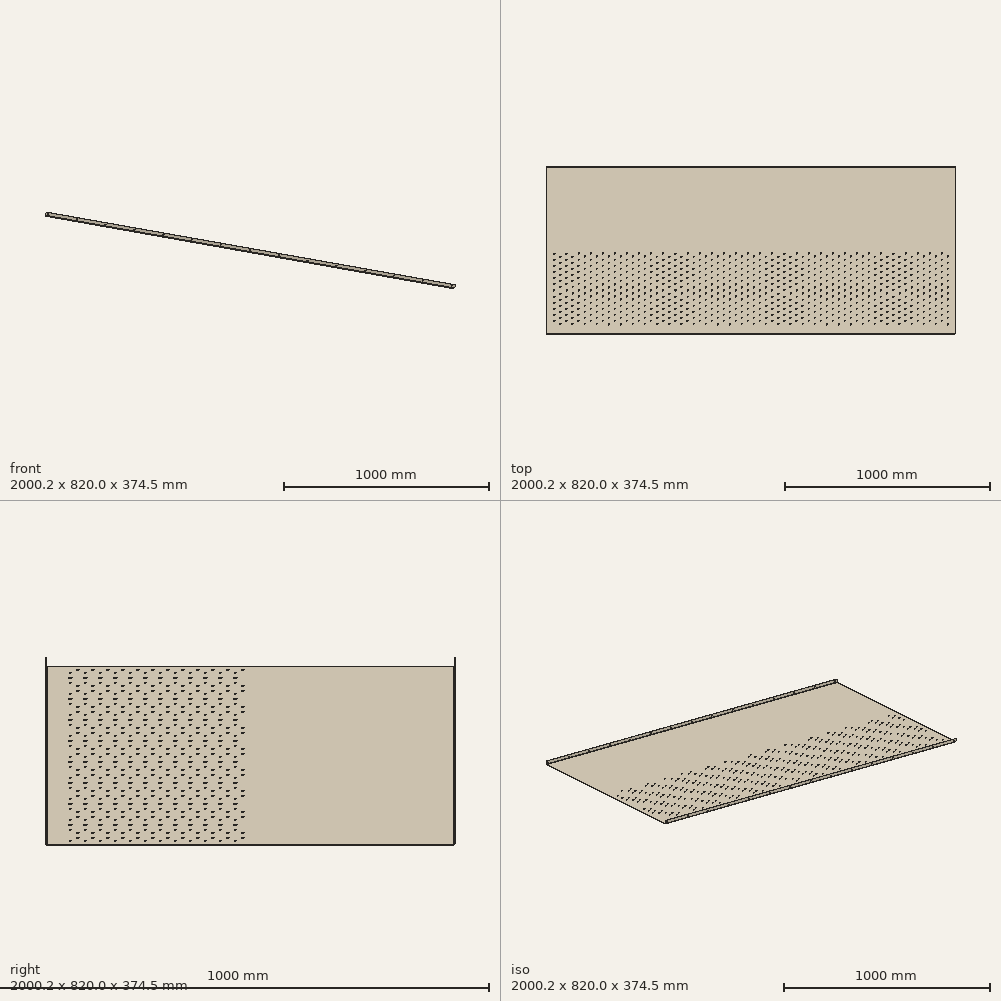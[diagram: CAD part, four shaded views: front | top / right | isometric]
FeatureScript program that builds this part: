
annotation { "Feature Type Name" : "Feature", "Feature Type Description" : "" }
export const myFeature = defineFeature(function(context is Context, id is Id, definition is map)
    precondition{}
    {
        {
            var Q0;
            Q0=qCreatedBy(makeId("Front.planeOp"),FACE);
            var sketch = newSketch(context, id + "F0", { "sketchPlane" : qUnion([Q0])});
            skLineSegment(sketch, "E0", {"start": v(1435.35, 1.97) * mm, "end": v(-561.3, 356.77) * mm});
            skLineSegment(sketch, "E1", {"start": v(-561.3, 356.77) * mm, "end": v(-561.65, 354.8) * mm});
            skLineSegment(sketch, "E2", {"start": v(1435.35, 1.97) * mm, "end": v(1435.35, 243.64) * mm});
            skLineSegment(sketch, "E3", {"start": v(-561.65, 354.8) * mm, "end": v(0, 255) * mm});
            skLineSegment(sketch, "E4", {"start": v(1435, 0) * mm, "end": v(1435.35, 1.97) * mm});
            skLineSegment(sketch, "E5", {"start": v(0, 255) * mm, "end": v(1435, 0) * mm});
            skLineSegment(sketch, "E6", {"start": v(0, 255) * mm, "end": v(0, 0) * mm, "construction": true});
            skLineSegment(sketch, "E7", {"start": v(0, 0) * mm, "end": v(1435, 0) * mm, "construction": true});
            skSolve(sketch);
        }
        {
            var Q0;
            Q0=makeQuery(id+"F0.imprint","IMPRINT",FACE,{"disambiguationData":[TD([[makeQuery(id+"F0.imprint","IMPRINT",EDGE,{"derivedFrom":sQuery(id+"F0.wireOp",EDGE,"E0")}),1.0]])]});
            extrude(context, id + "F1", {"entities" : qUnion([Q0]), "depth" : 820 * mm, "symmetric" : true});
        }
        {
            var Q0;
            Q0=makeQuery(id+"F1.opExtrude","CAP_FACE",FACE,{"disambiguationData":[OSD([sQuery(id+"F0.wireOp",EDGE,"E0"),sQuery(id+"F0.wireOp",EDGE,"E1"),sQuery(id+"F0.wireOp",EDGE,"E3"),sQuery(id+"F0.wireOp",EDGE,"E4")])],"isStart":false});
            var sketch = newSketch(context, id + "F2", { "sketchPlane" : qUnion([Q0])});
            skLineSegment(sketch, "E8", {"start": v(-561.65, 354.8) * mm, "end": v(-558.15, 374.5) * mm});
            skLineSegment(sketch, "E9", {"start": v(-558.15, 374.5) * mm, "end": v(1438.5, 19.7) * mm});
            skLineSegment(sketch, "E10", {"start": v(1438.5, 19.7) * mm, "end": v(1435, 0) * mm});
            skLineSegment(sketch, "E11", {"start": v(1435, 0) * mm, "end": v(-561.65, 354.8) * mm});
            skLineSegment(sketch, "E12", {"start": v(-558.15, 374.5) * mm, "end": v(-564.65, 375.65) * mm, "construction": true});
            skLineSegment(sketch, "E13", {"start": v(-564.65, 375.65) * mm, "end": v(-564.65, 355.34) * mm, "construction": true});
            skLineSegment(sketch, "E14", {"start": v(-564.65, 355.34) * mm, "end": v(-561.65, 354.8) * mm, "construction": true});
            skLineSegment(sketch, "E15", {"start": v(1435.35, 20.25) * mm, "end": v(1435.35, 1.97) * mm, "construction": true});
            skLineSegment(sketch, "E16", {"start": v(-564.65, 365.5) * mm, "end": v(-550.21, 362.93) * mm, "construction": true});
            skLineSegment(sketch, "E17", {"start": v(-550.21, 367) * mm, "end": v(-550.21, 358.87) * mm, "construction": true});
            skLineSegment(sketch, "E18", {"start": v(-550.21, 362.93) * mm, "end": v(1420.91, 12.66) * mm, "construction": true});
            skCircle(sketch, "E19", {"center": v(-550.21, 362.93) * mm, "radius": 3.5 * mm});
            skCircle(sketch, "E20.1.0.0", {"center": v(-409.42, 337.91) * mm, "radius": 3.5 * mm});
            skLineSegment(sketch, "E20.1.0.1", {"start": v(-409.42, 341.97) * mm, "end": v(-409.42, 333.85) * mm, "construction": true});
            skCircle(sketch, "E20.2.0.0", {"center": v(-268.62, 312.9) * mm, "radius": 3.5 * mm});
            skLineSegment(sketch, "E20.2.0.1", {"start": v(-268.62, 316.95) * mm, "end": v(-268.62, 308.83) * mm, "construction": true});
            skCircle(sketch, "E20.3.0.0", {"center": v(-127.83, 287.87) * mm, "radius": 3.5 * mm});
            skLineSegment(sketch, "E20.3.0.1", {"start": v(-127.83, 291.93) * mm, "end": v(-127.83, 283.8) * mm, "construction": true});
            skCircle(sketch, "E20.4.0.0", {"center": v(12.97, 262.85) * mm, "radius": 3.5 * mm});
            skLineSegment(sketch, "E20.4.0.1", {"start": v(12.97, 266.92) * mm, "end": v(12.97, 258.79) * mm, "construction": true});
            skCircle(sketch, "E20.5.0.0", {"center": v(153.76, 237.83) * mm, "radius": 3.5 * mm});
            skLineSegment(sketch, "E20.5.0.1", {"start": v(153.76, 241.9) * mm, "end": v(153.76, 233.77) * mm, "construction": true});
            skCircle(sketch, "E20.6.0.0", {"center": v(294.56, 212.81) * mm, "radius": 3.5 * mm});
            skLineSegment(sketch, "E20.6.0.1", {"start": v(294.56, 216.88) * mm, "end": v(294.56, 208.75) * mm, "construction": true});
            skCircle(sketch, "E20.7.0.0", {"center": v(435.35, 187.8) * mm, "radius": 3.5 * mm});
            skLineSegment(sketch, "E20.7.0.1", {"start": v(435.35, 191.86) * mm, "end": v(435.35, 183.73) * mm, "construction": true});
            skCircle(sketch, "E20.8.0.0", {"center": v(576.14, 162.78) * mm, "radius": 3.5 * mm});
            skLineSegment(sketch, "E20.8.0.1", {"start": v(576.14, 166.84) * mm, "end": v(576.14, 158.71) * mm, "construction": true});
            skCircle(sketch, "E20.9.0.0", {"center": v(716.94, 137.76) * mm, "radius": 3.5 * mm});
            skLineSegment(sketch, "E20.9.0.1", {"start": v(716.94, 141.82) * mm, "end": v(716.94, 133.7) * mm, "construction": true});
            skCircle(sketch, "E20.10.0.0", {"center": v(857.73, 112.74) * mm, "radius": 3.5 * mm});
            skLineSegment(sketch, "E20.10.0.1", {"start": v(857.73, 116.8) * mm, "end": v(857.73, 108.67) * mm, "construction": true});
            skCircle(sketch, "E20.11.0.0", {"center": v(998.53, 87.72) * mm, "radius": 3.5 * mm});
            skLineSegment(sketch, "E20.11.0.1", {"start": v(998.53, 91.78) * mm, "end": v(998.53, 83.66) * mm, "construction": true});
            skCircle(sketch, "E20.12.0.0", {"center": v(1139.32, 62.7) * mm, "radius": 3.5 * mm});
            skLineSegment(sketch, "E20.12.0.1", {"start": v(1139.32, 66.76) * mm, "end": v(1139.32, 58.64) * mm, "construction": true});
            skCircle(sketch, "E20.13.0.0", {"center": v(1280.12, 37.68) * mm, "radius": 3.5 * mm});
            skLineSegment(sketch, "E20.13.0.1", {"start": v(1280.12, 41.74) * mm, "end": v(1280.12, 33.62) * mm, "construction": true});
            skCircle(sketch, "E20.14.0.0", {"center": v(1420.91, 12.66) * mm, "radius": 3.5 * mm});
            skLineSegment(sketch, "E20.14.0.1", {"start": v(1420.91, 16.72) * mm, "end": v(1420.91, 8.6) * mm, "construction": true});
            skLineSegment(sketch, "E20.direction1", {"start": v(-550.21, 362.93) * mm, "end": v(-409.42, 337.91) * mm, "construction": true});
            skLineSegment(sketch, "E21.trimOffspring", {"start": v(1420.91, 12.66) * mm, "end": v(1435.35, 10.1) * mm, "construction": true});
            skPoint(sketch, "E22.orphan", {"position": v(1436.75, 9.85) * mm});
            skSolve(sketch);
        }
        {
            var Q0;
            Q0 = qSketchRegion(id + "F2", true);
            extrude(context, id + "F3", {"entities" : qUnion([Q0]), "operationType" : NewBodyOperationType.ADD, "oppositeDirection" : true, "depth" : 2 * mm});
        }
        {
            var Q0;
            Q0=makeQuery(id+"F1.opExtrude","CAP_FACE",FACE,{"disambiguationData":[OSD([sQuery(id+"F0.wireOp",EDGE,"E0"),sQuery(id+"F0.wireOp",EDGE,"E1"),sQuery(id+"F0.wireOp",EDGE,"E3"),sQuery(id+"F0.wireOp",EDGE,"E4")])],"isStart":true});
            var sketch = newSketch(context, id + "F4", { "sketchPlane" : qUnion([Q0])});
            skLineSegment(sketch, "E23", {"start": v(-1435, 0) * mm, "end": v(-1438.5, 19.7) * mm});
            skLineSegment(sketch, "E24", {"start": v(-1438.5, 19.7) * mm, "end": v(558.15, 374.5) * mm});
            skLineSegment(sketch, "E25", {"start": v(558.15, 374.5) * mm, "end": v(561.65, 354.8) * mm});
            skLineSegment(sketch, "E26", {"start": v(561.65, 354.8) * mm, "end": v(-1435, 0) * mm});
            skLineSegment(sketch, "E27", {"start": v(-1435.35, 1.97) * mm, "end": v(-1435.35, 20.25) * mm, "construction": true});
            skLineSegment(sketch, "E28", {"start": v(561.65, 354.8) * mm, "end": v(564.65, 355.34) * mm, "construction": true});
            skLineSegment(sketch, "E29", {"start": v(564.65, 355.34) * mm, "end": v(564.65, 375.65) * mm, "construction": true});
            skLineSegment(sketch, "E30", {"start": v(564.65, 375.65) * mm, "end": v(558.15, 374.5) * mm, "construction": true});
            skLineSegment(sketch, "E31", {"start": v(-1435.35, 10.1) * mm, "end": v(-1420.91, 12.66) * mm, "construction": true});
            skLineSegment(sketch, "E32", {"start": v(550.21, 367) * mm, "end": v(550.21, 358.87) * mm, "construction": true});
            skLineSegment(sketch, "E33", {"start": v(550.21, 362.93) * mm, "end": v(564.65, 365.5) * mm, "construction": true});
            skCircle(sketch, "E34", {"center": v(550.21, 362.93) * mm, "radius": 3.5 * mm});
            skCircle(sketch, "E35.1.0.0", {"center": v(409.42, 337.91) * mm, "radius": 3.5 * mm});
            skLineSegment(sketch, "E35.1.0.1", {"start": v(409.42, 341.97) * mm, "end": v(409.42, 333.85) * mm, "construction": true});
            skCircle(sketch, "E35.2.0.0", {"center": v(268.62, 312.9) * mm, "radius": 3.5 * mm});
            skLineSegment(sketch, "E35.2.0.1", {"start": v(268.62, 316.95) * mm, "end": v(268.62, 308.83) * mm, "construction": true});
            skCircle(sketch, "E35.3.0.0", {"center": v(127.83, 287.87) * mm, "radius": 3.5 * mm});
            skLineSegment(sketch, "E35.3.0.1", {"start": v(127.83, 291.93) * mm, "end": v(127.83, 283.8) * mm, "construction": true});
            skCircle(sketch, "E35.4.0.0", {"center": v(-12.97, 262.85) * mm, "radius": 3.5 * mm});
            skLineSegment(sketch, "E35.4.0.1", {"start": v(-12.97, 266.92) * mm, "end": v(-12.97, 258.79) * mm, "construction": true});
            skCircle(sketch, "E35.5.0.0", {"center": v(-153.76, 237.83) * mm, "radius": 3.5 * mm});
            skLineSegment(sketch, "E35.5.0.1", {"start": v(-153.76, 241.9) * mm, "end": v(-153.76, 233.77) * mm, "construction": true});
            skCircle(sketch, "E35.6.0.0", {"center": v(-294.56, 212.81) * mm, "radius": 3.5 * mm});
            skLineSegment(sketch, "E35.6.0.1", {"start": v(-294.56, 216.88) * mm, "end": v(-294.56, 208.75) * mm, "construction": true});
            skCircle(sketch, "E35.7.0.0", {"center": v(-435.35, 187.8) * mm, "radius": 3.5 * mm});
            skLineSegment(sketch, "E35.7.0.1", {"start": v(-435.35, 191.86) * mm, "end": v(-435.35, 183.73) * mm, "construction": true});
            skCircle(sketch, "E35.8.0.0", {"center": v(-576.14, 162.78) * mm, "radius": 3.5 * mm});
            skLineSegment(sketch, "E35.8.0.1", {"start": v(-576.14, 166.84) * mm, "end": v(-576.14, 158.71) * mm, "construction": true});
            skCircle(sketch, "E35.9.0.0", {"center": v(-716.94, 137.76) * mm, "radius": 3.5 * mm});
            skLineSegment(sketch, "E35.9.0.1", {"start": v(-716.94, 141.82) * mm, "end": v(-716.94, 133.7) * mm, "construction": true});
            skCircle(sketch, "E35.10.0.0", {"center": v(-857.73, 112.74) * mm, "radius": 3.5 * mm});
            skLineSegment(sketch, "E35.10.0.1", {"start": v(-857.73, 116.8) * mm, "end": v(-857.73, 108.67) * mm, "construction": true});
            skCircle(sketch, "E35.11.0.0", {"center": v(-998.53, 87.72) * mm, "radius": 3.5 * mm});
            skLineSegment(sketch, "E35.11.0.1", {"start": v(-998.53, 91.78) * mm, "end": v(-998.53, 83.66) * mm, "construction": true});
            skCircle(sketch, "E35.12.0.0", {"center": v(-1139.32, 62.7) * mm, "radius": 3.5 * mm});
            skLineSegment(sketch, "E35.12.0.1", {"start": v(-1139.32, 66.76) * mm, "end": v(-1139.32, 58.64) * mm, "construction": true});
            skCircle(sketch, "E35.13.0.0", {"center": v(-1280.12, 37.68) * mm, "radius": 3.5 * mm});
            skLineSegment(sketch, "E35.13.0.1", {"start": v(-1280.12, 41.74) * mm, "end": v(-1280.12, 33.62) * mm, "construction": true});
            skCircle(sketch, "E35.14.0.0", {"center": v(-1420.91, 12.66) * mm, "radius": 3.5 * mm});
            skLineSegment(sketch, "E35.14.0.1", {"start": v(-1420.91, 16.72) * mm, "end": v(-1420.91, 8.6) * mm, "construction": true});
            skLineSegment(sketch, "E35.direction1", {"start": v(550.21, 362.93) * mm, "end": v(409.42, 337.91) * mm, "construction": true});
            skPoint(sketch, "E36.orphan", {"position": v(-1436.75, 9.85) * mm});
            skLineSegment(sketch, "E37.trimOffspring", {"start": v(-1420.91, 12.66) * mm, "end": v(550.21, 362.93) * mm, "construction": true});
            skSolve(sketch);
        }
        {
            var Q0;
            Q0 = qSketchRegion(id + "F4", true);
            extrude(context, id + "F5", {"entities" : qUnion([Q0]), "operationType" : NewBodyOperationType.ADD, "oppositeDirection" : true, "depth" : 2 * mm});
        }
        {
            var Q0;
            Q0=makeQuery(id+"F1.opExtrude","SWEPT_FACE",FACE,{"disambiguationData":[OSD([sQuery(id+"F0.wireOp",EDGE,"E0")])]});
            var sketch = newSketch(context, id + "F6", { "sketchPlane" : qUnion([Q0])});
            skCircle(sketch, "E38", {"center": v(1373.9, -360) * mm, "radius": 3.5 * mm});
            skCircle(sketch, "E39", {"center": v(1343.9, -345) * mm, "radius": 3.5 * mm});
            skLineSegment(sketch, "E40", {"start": v(1412.87, 0) * mm, "end": v(-615.06, 0) * mm, "construction": true});
            skCircle(sketch, "E41.0.1.0", {"center": v(1373.9, -330) * mm, "radius": 3.5 * mm});
            skCircle(sketch, "E41.0.2.0", {"center": v(1373.9, -300) * mm, "radius": 3.5 * mm});
            skCircle(sketch, "E41.0.3.0", {"center": v(1373.9, -270) * mm, "radius": 3.5 * mm});
            skCircle(sketch, "E41.0.4.0", {"center": v(1373.9, -240) * mm, "radius": 3.5 * mm});
            skCircle(sketch, "E41.0.5.0", {"center": v(1373.9, -210) * mm, "radius": 3.5 * mm});
            skCircle(sketch, "E41.0.6.0", {"center": v(1373.9, -180) * mm, "radius": 3.5 * mm});
            skCircle(sketch, "E41.0.7.0", {"center": v(1373.9, -150) * mm, "radius": 3.5 * mm});
            skCircle(sketch, "E41.0.8.0", {"center": v(1373.9, -120) * mm, "radius": 3.5 * mm});
            skCircle(sketch, "E41.0.9.0", {"center": v(1373.9, -90) * mm, "radius": 3.5 * mm});
            skCircle(sketch, "E41.0.10.0", {"center": v(1373.9, -60) * mm, "radius": 3.5 * mm});
            skCircle(sketch, "E41.0.11.0", {"center": v(1373.9, -30) * mm, "radius": 3.5 * mm});
            skCircle(sketch, "E41.0.12.0", {"center": v(1373.9, 0) * mm, "radius": 3.5 * mm});
            skLineSegment(sketch, "E41.direction1", {"start": v(1373.9, -360) * mm, "end": v(1373.9, -360) * mm});
            skLineSegment(sketch, "E41.direction2", {"start": v(1373.9, -360) * mm, "end": v(1373.9, -330) * mm, "construction": true});
            skCircle(sketch, "E42.0.1.0", {"center": v(1343.9, -315) * mm, "radius": 3.5 * mm});
            skCircle(sketch, "E42.0.2.0", {"center": v(1343.9, -285) * mm, "radius": 3.5 * mm});
            skCircle(sketch, "E42.0.3.0", {"center": v(1343.9, -255) * mm, "radius": 3.5 * mm});
            skCircle(sketch, "E42.0.4.0", {"center": v(1343.9, -225) * mm, "radius": 3.5 * mm});
            skCircle(sketch, "E42.0.5.0", {"center": v(1343.9, -195) * mm, "radius": 3.5 * mm});
            skCircle(sketch, "E42.0.6.0", {"center": v(1343.9, -165) * mm, "radius": 3.5 * mm});
            skCircle(sketch, "E42.0.7.0", {"center": v(1343.9, -135) * mm, "radius": 3.5 * mm});
            skCircle(sketch, "E42.0.8.0", {"center": v(1343.9, -105) * mm, "radius": 3.5 * mm});
            skCircle(sketch, "E42.0.9.0", {"center": v(1343.9, -75) * mm, "radius": 3.5 * mm});
            skCircle(sketch, "E42.0.10.0", {"center": v(1343.9, -45) * mm, "radius": 3.5 * mm});
            skCircle(sketch, "E42.0.11.0", {"center": v(1343.9, -15) * mm, "radius": 3.5 * mm});
            skLineSegment(sketch, "E42.direction1", {"start": v(1343.9, -345) * mm, "end": v(1343.9, -345) * mm});
            skLineSegment(sketch, "E42.direction2", {"start": v(1343.9, -345) * mm, "end": v(1343.9, -315) * mm, "construction": true});
            skLineSegment(sketch, "E43.1.0.0", {"start": v(1313.9, -360) * mm, "end": v(1313.9, -330) * mm, "construction": true});
            skCircle(sketch, "E43.1.0.1", {"center": v(1313.9, -60) * mm, "radius": 3.5 * mm});
            skCircle(sketch, "E43.1.0.2", {"center": v(1313.9, -30) * mm, "radius": 3.5 * mm});
            skCircle(sketch, "E43.1.0.3", {"center": v(1313.9, 0) * mm, "radius": 3.5 * mm});
            skCircle(sketch, "E43.1.0.4", {"center": v(1313.9, -240) * mm, "radius": 3.5 * mm});
            skCircle(sketch, "E43.1.0.5", {"center": v(1313.9, -300) * mm, "radius": 3.5 * mm});
            skCircle(sketch, "E43.1.0.6", {"center": v(1283.9, -75) * mm, "radius": 3.5 * mm});
            skCircle(sketch, "E43.1.0.7", {"center": v(1283.9, -285) * mm, "radius": 3.5 * mm});
            skCircle(sketch, "E43.1.0.8", {"center": v(1283.9, -105) * mm, "radius": 3.5 * mm});
            skCircle(sketch, "E43.1.0.9", {"center": v(1283.9, -255) * mm, "radius": 3.5 * mm});
            skCircle(sketch, "E43.1.0.10", {"center": v(1283.9, -195) * mm, "radius": 3.5 * mm});
            skLineSegment(sketch, "E43.1.0.11", {"start": v(1283.9, -345) * mm, "end": v(1283.9, -315) * mm, "construction": true});
            skCircle(sketch, "E43.1.0.12", {"center": v(1283.9, -15) * mm, "radius": 3.5 * mm});
            skCircle(sketch, "E43.1.0.13", {"center": v(1313.9, -120) * mm, "radius": 3.5 * mm});
            skCircle(sketch, "E43.1.0.14", {"center": v(1283.9, -45) * mm, "radius": 3.5 * mm});
            skCircle(sketch, "E43.1.0.15", {"center": v(1313.9, -180) * mm, "radius": 3.5 * mm});
            skCircle(sketch, "E43.1.0.16", {"center": v(1313.9, -150) * mm, "radius": 3.5 * mm});
            skCircle(sketch, "E43.1.0.17", {"center": v(1313.9, -90) * mm, "radius": 3.5 * mm});
            skCircle(sketch, "E43.1.0.18", {"center": v(1283.9, -135) * mm, "radius": 3.5 * mm});
            skCircle(sketch, "E43.1.0.19", {"center": v(1283.9, -225) * mm, "radius": 3.5 * mm});
            skCircle(sketch, "E43.1.0.20", {"center": v(1313.9, -210) * mm, "radius": 3.5 * mm});
            skCircle(sketch, "E43.1.0.21", {"center": v(1283.9, -165) * mm, "radius": 3.5 * mm});
            skCircle(sketch, "E43.1.0.22", {"center": v(1313.9, -270) * mm, "radius": 3.5 * mm});
            skCircle(sketch, "E43.1.0.23", {"center": v(1313.9, -330) * mm, "radius": 3.5 * mm});
            skCircle(sketch, "E43.1.0.24", {"center": v(1283.9, -315) * mm, "radius": 3.5 * mm});
            skCircle(sketch, "E43.1.0.25", {"center": v(1283.9, -345) * mm, "radius": 3.5 * mm});
            skCircle(sketch, "E43.1.0.26", {"center": v(1313.9, -360) * mm, "radius": 3.5 * mm});
            skLineSegment(sketch, "E43.2.0.0", {"start": v(1253.9, -360) * mm, "end": v(1253.9, -330) * mm, "construction": true});
            skCircle(sketch, "E43.2.0.1", {"center": v(1253.9, -60) * mm, "radius": 3.5 * mm});
            skCircle(sketch, "E43.2.0.2", {"center": v(1253.9, -30) * mm, "radius": 3.5 * mm});
            skCircle(sketch, "E43.2.0.3", {"center": v(1253.9, 0) * mm, "radius": 3.5 * mm});
            skCircle(sketch, "E43.2.0.4", {"center": v(1253.9, -240) * mm, "radius": 3.5 * mm});
            skCircle(sketch, "E43.2.0.5", {"center": v(1253.9, -300) * mm, "radius": 3.5 * mm});
            skCircle(sketch, "E43.2.0.6", {"center": v(1223.9, -75) * mm, "radius": 3.5 * mm});
            skCircle(sketch, "E43.2.0.7", {"center": v(1223.9, -285) * mm, "radius": 3.5 * mm});
            skCircle(sketch, "E43.2.0.8", {"center": v(1223.9, -105) * mm, "radius": 3.5 * mm});
            skCircle(sketch, "E43.2.0.9", {"center": v(1223.9, -255) * mm, "radius": 3.5 * mm});
            skCircle(sketch, "E43.2.0.10", {"center": v(1223.9, -195) * mm, "radius": 3.5 * mm});
            skLineSegment(sketch, "E43.2.0.11", {"start": v(1223.9, -345) * mm, "end": v(1223.9, -315) * mm, "construction": true});
            skCircle(sketch, "E43.2.0.12", {"center": v(1223.9, -15) * mm, "radius": 3.5 * mm});
            skCircle(sketch, "E43.2.0.13", {"center": v(1253.9, -120) * mm, "radius": 3.5 * mm});
            skCircle(sketch, "E43.2.0.14", {"center": v(1223.9, -45) * mm, "radius": 3.5 * mm});
            skCircle(sketch, "E43.2.0.15", {"center": v(1253.9, -180) * mm, "radius": 3.5 * mm});
            skCircle(sketch, "E43.2.0.16", {"center": v(1253.9, -150) * mm, "radius": 3.5 * mm});
            skCircle(sketch, "E43.2.0.17", {"center": v(1253.9, -90) * mm, "radius": 3.5 * mm});
            skCircle(sketch, "E43.2.0.18", {"center": v(1223.9, -135) * mm, "radius": 3.5 * mm});
            skCircle(sketch, "E43.2.0.19", {"center": v(1223.9, -225) * mm, "radius": 3.5 * mm});
            skCircle(sketch, "E43.2.0.20", {"center": v(1253.9, -210) * mm, "radius": 3.5 * mm});
            skCircle(sketch, "E43.2.0.21", {"center": v(1223.9, -165) * mm, "radius": 3.5 * mm});
            skCircle(sketch, "E43.2.0.22", {"center": v(1253.9, -270) * mm, "radius": 3.5 * mm});
            skCircle(sketch, "E43.2.0.23", {"center": v(1253.9, -330) * mm, "radius": 3.5 * mm});
            skCircle(sketch, "E43.2.0.24", {"center": v(1223.9, -315) * mm, "radius": 3.5 * mm});
            skCircle(sketch, "E43.2.0.25", {"center": v(1223.9, -345) * mm, "radius": 3.5 * mm});
            skCircle(sketch, "E43.2.0.26", {"center": v(1253.9, -360) * mm, "radius": 3.5 * mm});
            skLineSegment(sketch, "E43.3.0.0", {"start": v(1193.9, -360) * mm, "end": v(1193.9, -330) * mm, "construction": true});
            skCircle(sketch, "E43.3.0.1", {"center": v(1193.9, -60) * mm, "radius": 3.5 * mm});
            skCircle(sketch, "E43.3.0.2", {"center": v(1193.9, -30) * mm, "radius": 3.5 * mm});
            skCircle(sketch, "E43.3.0.3", {"center": v(1193.9, 0) * mm, "radius": 3.5 * mm});
            skCircle(sketch, "E43.3.0.4", {"center": v(1193.9, -240) * mm, "radius": 3.5 * mm});
            skCircle(sketch, "E43.3.0.5", {"center": v(1193.9, -300) * mm, "radius": 3.5 * mm});
            skCircle(sketch, "E43.3.0.6", {"center": v(1163.9, -75) * mm, "radius": 3.5 * mm});
            skCircle(sketch, "E43.3.0.7", {"center": v(1163.9, -285) * mm, "radius": 3.5 * mm});
            skCircle(sketch, "E43.3.0.8", {"center": v(1163.9, -105) * mm, "radius": 3.5 * mm});
            skCircle(sketch, "E43.3.0.9", {"center": v(1163.9, -255) * mm, "radius": 3.5 * mm});
            skCircle(sketch, "E43.3.0.10", {"center": v(1163.9, -195) * mm, "radius": 3.5 * mm});
            skLineSegment(sketch, "E43.3.0.11", {"start": v(1163.9, -345) * mm, "end": v(1163.9, -315) * mm, "construction": true});
            skCircle(sketch, "E43.3.0.12", {"center": v(1163.9, -15) * mm, "radius": 3.5 * mm});
            skCircle(sketch, "E43.3.0.13", {"center": v(1193.9, -120) * mm, "radius": 3.5 * mm});
            skCircle(sketch, "E43.3.0.14", {"center": v(1163.9, -45) * mm, "radius": 3.5 * mm});
            skCircle(sketch, "E43.3.0.15", {"center": v(1193.9, -180) * mm, "radius": 3.5 * mm});
            skCircle(sketch, "E43.3.0.16", {"center": v(1193.9, -150) * mm, "radius": 3.5 * mm});
            skCircle(sketch, "E43.3.0.17", {"center": v(1193.9, -90) * mm, "radius": 3.5 * mm});
            skCircle(sketch, "E43.3.0.18", {"center": v(1163.9, -135) * mm, "radius": 3.5 * mm});
            skCircle(sketch, "E43.3.0.19", {"center": v(1163.9, -225) * mm, "radius": 3.5 * mm});
            skCircle(sketch, "E43.3.0.20", {"center": v(1193.9, -210) * mm, "radius": 3.5 * mm});
            skCircle(sketch, "E43.3.0.21", {"center": v(1163.9, -165) * mm, "radius": 3.5 * mm});
            skCircle(sketch, "E43.3.0.22", {"center": v(1193.9, -270) * mm, "radius": 3.5 * mm});
            skCircle(sketch, "E43.3.0.23", {"center": v(1193.9, -330) * mm, "radius": 3.5 * mm});
            skCircle(sketch, "E43.3.0.24", {"center": v(1163.9, -315) * mm, "radius": 3.5 * mm});
            skCircle(sketch, "E43.3.0.25", {"center": v(1163.9, -345) * mm, "radius": 3.5 * mm});
            skCircle(sketch, "E43.3.0.26", {"center": v(1193.9, -360) * mm, "radius": 3.5 * mm});
            skLineSegment(sketch, "E43.4.0.0", {"start": v(1133.9, -360) * mm, "end": v(1133.9, -330) * mm, "construction": true});
            skCircle(sketch, "E43.4.0.1", {"center": v(1133.9, -60) * mm, "radius": 3.5 * mm});
            skCircle(sketch, "E43.4.0.2", {"center": v(1133.9, -30) * mm, "radius": 3.5 * mm});
            skCircle(sketch, "E43.4.0.3", {"center": v(1133.9, 0) * mm, "radius": 3.5 * mm});
            skCircle(sketch, "E43.4.0.4", {"center": v(1133.9, -240) * mm, "radius": 3.5 * mm});
            skCircle(sketch, "E43.4.0.5", {"center": v(1133.9, -300) * mm, "radius": 3.5 * mm});
            skCircle(sketch, "E43.4.0.6", {"center": v(1103.9, -75) * mm, "radius": 3.5 * mm});
            skCircle(sketch, "E43.4.0.7", {"center": v(1103.9, -285) * mm, "radius": 3.5 * mm});
            skCircle(sketch, "E43.4.0.8", {"center": v(1103.9, -105) * mm, "radius": 3.5 * mm});
            skCircle(sketch, "E43.4.0.9", {"center": v(1103.9, -255) * mm, "radius": 3.5 * mm});
            skCircle(sketch, "E43.4.0.10", {"center": v(1103.9, -195) * mm, "radius": 3.5 * mm});
            skLineSegment(sketch, "E43.4.0.11", {"start": v(1103.9, -345) * mm, "end": v(1103.9, -315) * mm, "construction": true});
            skCircle(sketch, "E43.4.0.12", {"center": v(1103.9, -15) * mm, "radius": 3.5 * mm});
            skCircle(sketch, "E43.4.0.13", {"center": v(1133.9, -120) * mm, "radius": 3.5 * mm});
            skCircle(sketch, "E43.4.0.14", {"center": v(1103.9, -45) * mm, "radius": 3.5 * mm});
            skCircle(sketch, "E43.4.0.15", {"center": v(1133.9, -180) * mm, "radius": 3.5 * mm});
            skCircle(sketch, "E43.4.0.16", {"center": v(1133.9, -150) * mm, "radius": 3.5 * mm});
            skCircle(sketch, "E43.4.0.17", {"center": v(1133.9, -90) * mm, "radius": 3.5 * mm});
            skCircle(sketch, "E43.4.0.18", {"center": v(1103.9, -135) * mm, "radius": 3.5 * mm});
            skCircle(sketch, "E43.4.0.19", {"center": v(1103.9, -225) * mm, "radius": 3.5 * mm});
            skCircle(sketch, "E43.4.0.20", {"center": v(1133.9, -210) * mm, "radius": 3.5 * mm});
            skCircle(sketch, "E43.4.0.21", {"center": v(1103.9, -165) * mm, "radius": 3.5 * mm});
            skCircle(sketch, "E43.4.0.22", {"center": v(1133.9, -270) * mm, "radius": 3.5 * mm});
            skCircle(sketch, "E43.4.0.23", {"center": v(1133.9, -330) * mm, "radius": 3.5 * mm});
            skCircle(sketch, "E43.4.0.24", {"center": v(1103.9, -315) * mm, "radius": 3.5 * mm});
            skCircle(sketch, "E43.4.0.25", {"center": v(1103.9, -345) * mm, "radius": 3.5 * mm});
            skCircle(sketch, "E43.4.0.26", {"center": v(1133.9, -360) * mm, "radius": 3.5 * mm});
            skLineSegment(sketch, "E43.5.0.0", {"start": v(1073.9, -360) * mm, "end": v(1073.9, -330) * mm, "construction": true});
            skCircle(sketch, "E43.5.0.1", {"center": v(1073.9, -60) * mm, "radius": 3.5 * mm});
            skCircle(sketch, "E43.5.0.2", {"center": v(1073.9, -30) * mm, "radius": 3.5 * mm});
            skCircle(sketch, "E43.5.0.3", {"center": v(1073.9, 0) * mm, "radius": 3.5 * mm});
            skCircle(sketch, "E43.5.0.4", {"center": v(1073.9, -240) * mm, "radius": 3.5 * mm});
            skCircle(sketch, "E43.5.0.5", {"center": v(1073.9, -300) * mm, "radius": 3.5 * mm});
            skCircle(sketch, "E43.5.0.6", {"center": v(1043.9, -75) * mm, "radius": 3.5 * mm});
            skCircle(sketch, "E43.5.0.7", {"center": v(1043.9, -285) * mm, "radius": 3.5 * mm});
            skCircle(sketch, "E43.5.0.8", {"center": v(1043.9, -105) * mm, "radius": 3.5 * mm});
            skCircle(sketch, "E43.5.0.9", {"center": v(1043.9, -255) * mm, "radius": 3.5 * mm});
            skCircle(sketch, "E43.5.0.10", {"center": v(1043.9, -195) * mm, "radius": 3.5 * mm});
            skLineSegment(sketch, "E43.5.0.11", {"start": v(1043.9, -345) * mm, "end": v(1043.9, -315) * mm, "construction": true});
            skCircle(sketch, "E43.5.0.12", {"center": v(1043.9, -15) * mm, "radius": 3.5 * mm});
            skCircle(sketch, "E43.5.0.13", {"center": v(1073.9, -120) * mm, "radius": 3.5 * mm});
            skCircle(sketch, "E43.5.0.14", {"center": v(1043.9, -45) * mm, "radius": 3.5 * mm});
            skCircle(sketch, "E43.5.0.15", {"center": v(1073.9, -180) * mm, "radius": 3.5 * mm});
            skCircle(sketch, "E43.5.0.16", {"center": v(1073.9, -150) * mm, "radius": 3.5 * mm});
            skCircle(sketch, "E43.5.0.17", {"center": v(1073.9, -90) * mm, "radius": 3.5 * mm});
            skCircle(sketch, "E43.5.0.18", {"center": v(1043.9, -135) * mm, "radius": 3.5 * mm});
            skCircle(sketch, "E43.5.0.19", {"center": v(1043.9, -225) * mm, "radius": 3.5 * mm});
            skCircle(sketch, "E43.5.0.20", {"center": v(1073.9, -210) * mm, "radius": 3.5 * mm});
            skCircle(sketch, "E43.5.0.21", {"center": v(1043.9, -165) * mm, "radius": 3.5 * mm});
            skCircle(sketch, "E43.5.0.22", {"center": v(1073.9, -270) * mm, "radius": 3.5 * mm});
            skCircle(sketch, "E43.5.0.23", {"center": v(1073.9, -330) * mm, "radius": 3.5 * mm});
            skCircle(sketch, "E43.5.0.24", {"center": v(1043.9, -315) * mm, "radius": 3.5 * mm});
            skCircle(sketch, "E43.5.0.25", {"center": v(1043.9, -345) * mm, "radius": 3.5 * mm});
            skCircle(sketch, "E43.5.0.26", {"center": v(1073.9, -360) * mm, "radius": 3.5 * mm});
            skLineSegment(sketch, "E43.6.0.0", {"start": v(1013.9, -360) * mm, "end": v(1013.9, -330) * mm, "construction": true});
            skCircle(sketch, "E43.6.0.1", {"center": v(1013.9, -60) * mm, "radius": 3.5 * mm});
            skCircle(sketch, "E43.6.0.2", {"center": v(1013.9, -30) * mm, "radius": 3.5 * mm});
            skCircle(sketch, "E43.6.0.3", {"center": v(1013.9, 0) * mm, "radius": 3.5 * mm});
            skCircle(sketch, "E43.6.0.4", {"center": v(1013.9, -240) * mm, "radius": 3.5 * mm});
            skCircle(sketch, "E43.6.0.5", {"center": v(1013.9, -300) * mm, "radius": 3.5 * mm});
            skCircle(sketch, "E43.6.0.6", {"center": v(983.9, -75) * mm, "radius": 3.5 * mm});
            skCircle(sketch, "E43.6.0.7", {"center": v(983.9, -285) * mm, "radius": 3.5 * mm});
            skCircle(sketch, "E43.6.0.8", {"center": v(983.9, -105) * mm, "radius": 3.5 * mm});
            skCircle(sketch, "E43.6.0.9", {"center": v(983.9, -255) * mm, "radius": 3.5 * mm});
            skCircle(sketch, "E43.6.0.10", {"center": v(983.9, -195) * mm, "radius": 3.5 * mm});
            skLineSegment(sketch, "E43.6.0.11", {"start": v(983.9, -345) * mm, "end": v(983.9, -315) * mm, "construction": true});
            skCircle(sketch, "E43.6.0.12", {"center": v(983.9, -15) * mm, "radius": 3.5 * mm});
            skCircle(sketch, "E43.6.0.13", {"center": v(1013.9, -120) * mm, "radius": 3.5 * mm});
            skCircle(sketch, "E43.6.0.14", {"center": v(983.9, -45) * mm, "radius": 3.5 * mm});
            skCircle(sketch, "E43.6.0.15", {"center": v(1013.9, -180) * mm, "radius": 3.5 * mm});
            skCircle(sketch, "E43.6.0.16", {"center": v(1013.9, -150) * mm, "radius": 3.5 * mm});
            skCircle(sketch, "E43.6.0.17", {"center": v(1013.9, -90) * mm, "radius": 3.5 * mm});
            skCircle(sketch, "E43.6.0.18", {"center": v(983.9, -135) * mm, "radius": 3.5 * mm});
            skCircle(sketch, "E43.6.0.19", {"center": v(983.9, -225) * mm, "radius": 3.5 * mm});
            skCircle(sketch, "E43.6.0.20", {"center": v(1013.9, -210) * mm, "radius": 3.5 * mm});
            skCircle(sketch, "E43.6.0.21", {"center": v(983.9, -165) * mm, "radius": 3.5 * mm});
            skCircle(sketch, "E43.6.0.22", {"center": v(1013.9, -270) * mm, "radius": 3.5 * mm});
            skCircle(sketch, "E43.6.0.23", {"center": v(1013.9, -330) * mm, "radius": 3.5 * mm});
            skCircle(sketch, "E43.6.0.24", {"center": v(983.9, -315) * mm, "radius": 3.5 * mm});
            skCircle(sketch, "E43.6.0.25", {"center": v(983.9, -345) * mm, "radius": 3.5 * mm});
            skCircle(sketch, "E43.6.0.26", {"center": v(1013.9, -360) * mm, "radius": 3.5 * mm});
            skLineSegment(sketch, "E43.7.0.0", {"start": v(953.9, -360) * mm, "end": v(953.9, -330) * mm, "construction": true});
            skCircle(sketch, "E43.7.0.1", {"center": v(953.9, -60) * mm, "radius": 3.5 * mm});
            skCircle(sketch, "E43.7.0.2", {"center": v(953.9, -30) * mm, "radius": 3.5 * mm});
            skCircle(sketch, "E43.7.0.3", {"center": v(953.9, 0) * mm, "radius": 3.5 * mm});
            skCircle(sketch, "E43.7.0.4", {"center": v(953.9, -240) * mm, "radius": 3.5 * mm});
            skCircle(sketch, "E43.7.0.5", {"center": v(953.9, -300) * mm, "radius": 3.5 * mm});
            skCircle(sketch, "E43.7.0.6", {"center": v(923.9, -75) * mm, "radius": 3.5 * mm});
            skCircle(sketch, "E43.7.0.7", {"center": v(923.9, -285) * mm, "radius": 3.5 * mm});
            skCircle(sketch, "E43.7.0.8", {"center": v(923.9, -105) * mm, "radius": 3.5 * mm});
            skCircle(sketch, "E43.7.0.9", {"center": v(923.9, -255) * mm, "radius": 3.5 * mm});
            skCircle(sketch, "E43.7.0.10", {"center": v(923.9, -195) * mm, "radius": 3.5 * mm});
            skLineSegment(sketch, "E43.7.0.11", {"start": v(923.9, -345) * mm, "end": v(923.9, -315) * mm, "construction": true});
            skCircle(sketch, "E43.7.0.12", {"center": v(923.9, -15) * mm, "radius": 3.5 * mm});
            skCircle(sketch, "E43.7.0.13", {"center": v(953.9, -120) * mm, "radius": 3.5 * mm});
            skCircle(sketch, "E43.7.0.14", {"center": v(923.9, -45) * mm, "radius": 3.5 * mm});
            skCircle(sketch, "E43.7.0.15", {"center": v(953.9, -180) * mm, "radius": 3.5 * mm});
            skCircle(sketch, "E43.7.0.16", {"center": v(953.9, -150) * mm, "radius": 3.5 * mm});
            skCircle(sketch, "E43.7.0.17", {"center": v(953.9, -90) * mm, "radius": 3.5 * mm});
            skCircle(sketch, "E43.7.0.18", {"center": v(923.9, -135) * mm, "radius": 3.5 * mm});
            skCircle(sketch, "E43.7.0.19", {"center": v(923.9, -225) * mm, "radius": 3.5 * mm});
            skCircle(sketch, "E43.7.0.20", {"center": v(953.9, -210) * mm, "radius": 3.5 * mm});
            skCircle(sketch, "E43.7.0.21", {"center": v(923.9, -165) * mm, "radius": 3.5 * mm});
            skCircle(sketch, "E43.7.0.22", {"center": v(953.9, -270) * mm, "radius": 3.5 * mm});
            skCircle(sketch, "E43.7.0.23", {"center": v(953.9, -330) * mm, "radius": 3.5 * mm});
            skCircle(sketch, "E43.7.0.24", {"center": v(923.9, -315) * mm, "radius": 3.5 * mm});
            skCircle(sketch, "E43.7.0.25", {"center": v(923.9, -345) * mm, "radius": 3.5 * mm});
            skCircle(sketch, "E43.7.0.26", {"center": v(953.9, -360) * mm, "radius": 3.5 * mm});
            skLineSegment(sketch, "E43.8.0.0", {"start": v(893.9, -360) * mm, "end": v(893.9, -330) * mm, "construction": true});
            skCircle(sketch, "E43.8.0.1", {"center": v(893.9, -60) * mm, "radius": 3.5 * mm});
            skCircle(sketch, "E43.8.0.2", {"center": v(893.9, -30) * mm, "radius": 3.5 * mm});
            skCircle(sketch, "E43.8.0.3", {"center": v(893.9, 0) * mm, "radius": 3.5 * mm});
            skCircle(sketch, "E43.8.0.4", {"center": v(893.9, -240) * mm, "radius": 3.5 * mm});
            skCircle(sketch, "E43.8.0.5", {"center": v(893.9, -300) * mm, "radius": 3.5 * mm});
            skCircle(sketch, "E43.8.0.6", {"center": v(863.9, -75) * mm, "radius": 3.5 * mm});
            skCircle(sketch, "E43.8.0.7", {"center": v(863.9, -285) * mm, "radius": 3.5 * mm});
            skCircle(sketch, "E43.8.0.8", {"center": v(863.9, -105) * mm, "radius": 3.5 * mm});
            skCircle(sketch, "E43.8.0.9", {"center": v(863.9, -255) * mm, "radius": 3.5 * mm});
            skCircle(sketch, "E43.8.0.10", {"center": v(863.9, -195) * mm, "radius": 3.5 * mm});
            skLineSegment(sketch, "E43.8.0.11", {"start": v(863.9, -345) * mm, "end": v(863.9, -315) * mm, "construction": true});
            skCircle(sketch, "E43.8.0.12", {"center": v(863.9, -15) * mm, "radius": 3.5 * mm});
            skCircle(sketch, "E43.8.0.13", {"center": v(893.9, -120) * mm, "radius": 3.5 * mm});
            skCircle(sketch, "E43.8.0.14", {"center": v(863.9, -45) * mm, "radius": 3.5 * mm});
            skCircle(sketch, "E43.8.0.15", {"center": v(893.9, -180) * mm, "radius": 3.5 * mm});
            skCircle(sketch, "E43.8.0.16", {"center": v(893.9, -150) * mm, "radius": 3.5 * mm});
            skCircle(sketch, "E43.8.0.17", {"center": v(893.9, -90) * mm, "radius": 3.5 * mm});
            skCircle(sketch, "E43.8.0.18", {"center": v(863.9, -135) * mm, "radius": 3.5 * mm});
            skCircle(sketch, "E43.8.0.19", {"center": v(863.9, -225) * mm, "radius": 3.5 * mm});
            skCircle(sketch, "E43.8.0.20", {"center": v(893.9, -210) * mm, "radius": 3.5 * mm});
            skCircle(sketch, "E43.8.0.21", {"center": v(863.9, -165) * mm, "radius": 3.5 * mm});
            skCircle(sketch, "E43.8.0.22", {"center": v(893.9, -270) * mm, "radius": 3.5 * mm});
            skCircle(sketch, "E43.8.0.23", {"center": v(893.9, -330) * mm, "radius": 3.5 * mm});
            skCircle(sketch, "E43.8.0.24", {"center": v(863.9, -315) * mm, "radius": 3.5 * mm});
            skCircle(sketch, "E43.8.0.25", {"center": v(863.9, -345) * mm, "radius": 3.5 * mm});
            skCircle(sketch, "E43.8.0.26", {"center": v(893.9, -360) * mm, "radius": 3.5 * mm});
            skLineSegment(sketch, "E43.9.0.0", {"start": v(833.9, -360) * mm, "end": v(833.9, -330) * mm, "construction": true});
            skCircle(sketch, "E43.9.0.1", {"center": v(833.9, -60) * mm, "radius": 3.5 * mm});
            skCircle(sketch, "E43.9.0.2", {"center": v(833.9, -30) * mm, "radius": 3.5 * mm});
            skCircle(sketch, "E43.9.0.3", {"center": v(833.9, 0) * mm, "radius": 3.5 * mm});
            skCircle(sketch, "E43.9.0.4", {"center": v(833.9, -240) * mm, "radius": 3.5 * mm});
            skCircle(sketch, "E43.9.0.5", {"center": v(833.9, -300) * mm, "radius": 3.5 * mm});
            skCircle(sketch, "E43.9.0.6", {"center": v(803.9, -75) * mm, "radius": 3.5 * mm});
            skCircle(sketch, "E43.9.0.7", {"center": v(803.9, -285) * mm, "radius": 3.5 * mm});
            skCircle(sketch, "E43.9.0.8", {"center": v(803.9, -105) * mm, "radius": 3.5 * mm});
            skCircle(sketch, "E43.9.0.9", {"center": v(803.9, -255) * mm, "radius": 3.5 * mm});
            skCircle(sketch, "E43.9.0.10", {"center": v(803.9, -195) * mm, "radius": 3.5 * mm});
            skLineSegment(sketch, "E43.9.0.11", {"start": v(803.9, -345) * mm, "end": v(803.9, -315) * mm, "construction": true});
            skCircle(sketch, "E43.9.0.12", {"center": v(803.9, -15) * mm, "radius": 3.5 * mm});
            skCircle(sketch, "E43.9.0.13", {"center": v(833.9, -120) * mm, "radius": 3.5 * mm});
            skCircle(sketch, "E43.9.0.14", {"center": v(803.9, -45) * mm, "radius": 3.5 * mm});
            skCircle(sketch, "E43.9.0.15", {"center": v(833.9, -180) * mm, "radius": 3.5 * mm});
            skCircle(sketch, "E43.9.0.16", {"center": v(833.9, -150) * mm, "radius": 3.5 * mm});
            skCircle(sketch, "E43.9.0.17", {"center": v(833.9, -90) * mm, "radius": 3.5 * mm});
            skCircle(sketch, "E43.9.0.18", {"center": v(803.9, -135) * mm, "radius": 3.5 * mm});
            skCircle(sketch, "E43.9.0.19", {"center": v(803.9, -225) * mm, "radius": 3.5 * mm});
            skCircle(sketch, "E43.9.0.20", {"center": v(833.9, -210) * mm, "radius": 3.5 * mm});
            skCircle(sketch, "E43.9.0.21", {"center": v(803.9, -165) * mm, "radius": 3.5 * mm});
            skCircle(sketch, "E43.9.0.22", {"center": v(833.9, -270) * mm, "radius": 3.5 * mm});
            skCircle(sketch, "E43.9.0.23", {"center": v(833.9, -330) * mm, "radius": 3.5 * mm});
            skCircle(sketch, "E43.9.0.24", {"center": v(803.9, -315) * mm, "radius": 3.5 * mm});
            skCircle(sketch, "E43.9.0.25", {"center": v(803.9, -345) * mm, "radius": 3.5 * mm});
            skCircle(sketch, "E43.9.0.26", {"center": v(833.9, -360) * mm, "radius": 3.5 * mm});
            skLineSegment(sketch, "E43.10.0.0", {"start": v(773.9, -360) * mm, "end": v(773.9, -330) * mm, "construction": true});
            skCircle(sketch, "E43.10.0.1", {"center": v(773.9, -60) * mm, "radius": 3.5 * mm});
            skCircle(sketch, "E43.10.0.2", {"center": v(773.9, -30) * mm, "radius": 3.5 * mm});
            skCircle(sketch, "E43.10.0.3", {"center": v(773.9, 0) * mm, "radius": 3.5 * mm});
            skCircle(sketch, "E43.10.0.4", {"center": v(773.9, -240) * mm, "radius": 3.5 * mm});
            skCircle(sketch, "E43.10.0.5", {"center": v(773.9, -300) * mm, "radius": 3.5 * mm});
            skCircle(sketch, "E43.10.0.6", {"center": v(743.9, -75) * mm, "radius": 3.5 * mm});
            skCircle(sketch, "E43.10.0.7", {"center": v(743.9, -285) * mm, "radius": 3.5 * mm});
            skCircle(sketch, "E43.10.0.8", {"center": v(743.9, -105) * mm, "radius": 3.5 * mm});
            skCircle(sketch, "E43.10.0.9", {"center": v(743.9, -255) * mm, "radius": 3.5 * mm});
            skCircle(sketch, "E43.10.0.10", {"center": v(743.9, -195) * mm, "radius": 3.5 * mm});
            skLineSegment(sketch, "E43.10.0.11", {"start": v(743.9, -345) * mm, "end": v(743.9, -315) * mm, "construction": true});
            skCircle(sketch, "E43.10.0.12", {"center": v(743.9, -15) * mm, "radius": 3.5 * mm});
            skCircle(sketch, "E43.10.0.13", {"center": v(773.9, -120) * mm, "radius": 3.5 * mm});
            skCircle(sketch, "E43.10.0.14", {"center": v(743.9, -45) * mm, "radius": 3.5 * mm});
            skCircle(sketch, "E43.10.0.15", {"center": v(773.9, -180) * mm, "radius": 3.5 * mm});
            skCircle(sketch, "E43.10.0.16", {"center": v(773.9, -150) * mm, "radius": 3.5 * mm});
            skCircle(sketch, "E43.10.0.17", {"center": v(773.9, -90) * mm, "radius": 3.5 * mm});
            skCircle(sketch, "E43.10.0.18", {"center": v(743.9, -135) * mm, "radius": 3.5 * mm});
            skCircle(sketch, "E43.10.0.19", {"center": v(743.9, -225) * mm, "radius": 3.5 * mm});
            skCircle(sketch, "E43.10.0.20", {"center": v(773.9, -210) * mm, "radius": 3.5 * mm});
            skCircle(sketch, "E43.10.0.21", {"center": v(743.9, -165) * mm, "radius": 3.5 * mm});
            skCircle(sketch, "E43.10.0.22", {"center": v(773.9, -270) * mm, "radius": 3.5 * mm});
            skCircle(sketch, "E43.10.0.23", {"center": v(773.9, -330) * mm, "radius": 3.5 * mm});
            skCircle(sketch, "E43.10.0.24", {"center": v(743.9, -315) * mm, "radius": 3.5 * mm});
            skCircle(sketch, "E43.10.0.25", {"center": v(743.9, -345) * mm, "radius": 3.5 * mm});
            skCircle(sketch, "E43.10.0.26", {"center": v(773.9, -360) * mm, "radius": 3.5 * mm});
            skLineSegment(sketch, "E43.11.0.0", {"start": v(713.9, -360) * mm, "end": v(713.9, -330) * mm, "construction": true});
            skCircle(sketch, "E43.11.0.1", {"center": v(713.9, -60) * mm, "radius": 3.5 * mm});
            skCircle(sketch, "E43.11.0.2", {"center": v(713.9, -30) * mm, "radius": 3.5 * mm});
            skCircle(sketch, "E43.11.0.3", {"center": v(713.9, 0) * mm, "radius": 3.5 * mm});
            skCircle(sketch, "E43.11.0.4", {"center": v(713.9, -240) * mm, "radius": 3.5 * mm});
            skCircle(sketch, "E43.11.0.5", {"center": v(713.9, -300) * mm, "radius": 3.5 * mm});
            skCircle(sketch, "E43.11.0.6", {"center": v(683.9, -75) * mm, "radius": 3.5 * mm});
            skCircle(sketch, "E43.11.0.7", {"center": v(683.9, -285) * mm, "radius": 3.5 * mm});
            skCircle(sketch, "E43.11.0.8", {"center": v(683.9, -105) * mm, "radius": 3.5 * mm});
            skCircle(sketch, "E43.11.0.9", {"center": v(683.9, -255) * mm, "radius": 3.5 * mm});
            skCircle(sketch, "E43.11.0.10", {"center": v(683.9, -195) * mm, "radius": 3.5 * mm});
            skLineSegment(sketch, "E43.11.0.11", {"start": v(683.9, -345) * mm, "end": v(683.9, -315) * mm, "construction": true});
            skCircle(sketch, "E43.11.0.12", {"center": v(683.9, -15) * mm, "radius": 3.5 * mm});
            skCircle(sketch, "E43.11.0.13", {"center": v(713.9, -120) * mm, "radius": 3.5 * mm});
            skCircle(sketch, "E43.11.0.14", {"center": v(683.9, -45) * mm, "radius": 3.5 * mm});
            skCircle(sketch, "E43.11.0.15", {"center": v(713.9, -180) * mm, "radius": 3.5 * mm});
            skCircle(sketch, "E43.11.0.16", {"center": v(713.9, -150) * mm, "radius": 3.5 * mm});
            skCircle(sketch, "E43.11.0.17", {"center": v(713.9, -90) * mm, "radius": 3.5 * mm});
            skCircle(sketch, "E43.11.0.18", {"center": v(683.9, -135) * mm, "radius": 3.5 * mm});
            skCircle(sketch, "E43.11.0.19", {"center": v(683.9, -225) * mm, "radius": 3.5 * mm});
            skCircle(sketch, "E43.11.0.20", {"center": v(713.9, -210) * mm, "radius": 3.5 * mm});
            skCircle(sketch, "E43.11.0.21", {"center": v(683.9, -165) * mm, "radius": 3.5 * mm});
            skCircle(sketch, "E43.11.0.22", {"center": v(713.9, -270) * mm, "radius": 3.5 * mm});
            skCircle(sketch, "E43.11.0.23", {"center": v(713.9, -330) * mm, "radius": 3.5 * mm});
            skCircle(sketch, "E43.11.0.24", {"center": v(683.9, -315) * mm, "radius": 3.5 * mm});
            skCircle(sketch, "E43.11.0.25", {"center": v(683.9, -345) * mm, "radius": 3.5 * mm});
            skCircle(sketch, "E43.11.0.26", {"center": v(713.9, -360) * mm, "radius": 3.5 * mm});
            skLineSegment(sketch, "E43.12.0.0", {"start": v(653.9, -360) * mm, "end": v(653.9, -330) * mm, "construction": true});
            skCircle(sketch, "E43.12.0.1", {"center": v(653.9, -60) * mm, "radius": 3.5 * mm});
            skCircle(sketch, "E43.12.0.2", {"center": v(653.9, -30) * mm, "radius": 3.5 * mm});
            skCircle(sketch, "E43.12.0.3", {"center": v(653.9, 0) * mm, "radius": 3.5 * mm});
            skCircle(sketch, "E43.12.0.4", {"center": v(653.9, -240) * mm, "radius": 3.5 * mm});
            skCircle(sketch, "E43.12.0.5", {"center": v(653.9, -300) * mm, "radius": 3.5 * mm});
            skCircle(sketch, "E43.12.0.6", {"center": v(623.9, -75) * mm, "radius": 3.5 * mm});
            skCircle(sketch, "E43.12.0.7", {"center": v(623.9, -285) * mm, "radius": 3.5 * mm});
            skCircle(sketch, "E43.12.0.8", {"center": v(623.9, -105) * mm, "radius": 3.5 * mm});
            skCircle(sketch, "E43.12.0.9", {"center": v(623.9, -255) * mm, "radius": 3.5 * mm});
            skCircle(sketch, "E43.12.0.10", {"center": v(623.9, -195) * mm, "radius": 3.5 * mm});
            skLineSegment(sketch, "E43.12.0.11", {"start": v(623.9, -345) * mm, "end": v(623.9, -315) * mm, "construction": true});
            skCircle(sketch, "E43.12.0.12", {"center": v(623.9, -15) * mm, "radius": 3.5 * mm});
            skCircle(sketch, "E43.12.0.13", {"center": v(653.9, -120) * mm, "radius": 3.5 * mm});
            skCircle(sketch, "E43.12.0.14", {"center": v(623.9, -45) * mm, "radius": 3.5 * mm});
            skCircle(sketch, "E43.12.0.15", {"center": v(653.9, -180) * mm, "radius": 3.5 * mm});
            skCircle(sketch, "E43.12.0.16", {"center": v(653.9, -150) * mm, "radius": 3.5 * mm});
            skCircle(sketch, "E43.12.0.17", {"center": v(653.9, -90) * mm, "radius": 3.5 * mm});
            skCircle(sketch, "E43.12.0.18", {"center": v(623.9, -135) * mm, "radius": 3.5 * mm});
            skCircle(sketch, "E43.12.0.19", {"center": v(623.9, -225) * mm, "radius": 3.5 * mm});
            skCircle(sketch, "E43.12.0.20", {"center": v(653.9, -210) * mm, "radius": 3.5 * mm});
            skCircle(sketch, "E43.12.0.21", {"center": v(623.9, -165) * mm, "radius": 3.5 * mm});
            skCircle(sketch, "E43.12.0.22", {"center": v(653.9, -270) * mm, "radius": 3.5 * mm});
            skCircle(sketch, "E43.12.0.23", {"center": v(653.9, -330) * mm, "radius": 3.5 * mm});
            skCircle(sketch, "E43.12.0.24", {"center": v(623.9, -315) * mm, "radius": 3.5 * mm});
            skCircle(sketch, "E43.12.0.25", {"center": v(623.9, -345) * mm, "radius": 3.5 * mm});
            skCircle(sketch, "E43.12.0.26", {"center": v(653.9, -360) * mm, "radius": 3.5 * mm});
            skLineSegment(sketch, "E43.13.0.0", {"start": v(593.9, -360) * mm, "end": v(593.9, -330) * mm, "construction": true});
            skCircle(sketch, "E43.13.0.1", {"center": v(593.9, -60) * mm, "radius": 3.5 * mm});
            skCircle(sketch, "E43.13.0.2", {"center": v(593.9, -30) * mm, "radius": 3.5 * mm});
            skCircle(sketch, "E43.13.0.3", {"center": v(593.9, 0) * mm, "radius": 3.5 * mm});
            skCircle(sketch, "E43.13.0.4", {"center": v(593.9, -240) * mm, "radius": 3.5 * mm});
            skCircle(sketch, "E43.13.0.5", {"center": v(593.9, -300) * mm, "radius": 3.5 * mm});
            skCircle(sketch, "E43.13.0.6", {"center": v(563.9, -75) * mm, "radius": 3.5 * mm});
            skCircle(sketch, "E43.13.0.7", {"center": v(563.9, -285) * mm, "radius": 3.5 * mm});
            skCircle(sketch, "E43.13.0.8", {"center": v(563.9, -105) * mm, "radius": 3.5 * mm});
            skCircle(sketch, "E43.13.0.9", {"center": v(563.9, -255) * mm, "radius": 3.5 * mm});
            skCircle(sketch, "E43.13.0.10", {"center": v(563.9, -195) * mm, "radius": 3.5 * mm});
            skLineSegment(sketch, "E43.13.0.11", {"start": v(563.9, -345) * mm, "end": v(563.9, -315) * mm, "construction": true});
            skCircle(sketch, "E43.13.0.12", {"center": v(563.9, -15) * mm, "radius": 3.5 * mm});
            skCircle(sketch, "E43.13.0.13", {"center": v(593.9, -120) * mm, "radius": 3.5 * mm});
            skCircle(sketch, "E43.13.0.14", {"center": v(563.9, -45) * mm, "radius": 3.5 * mm});
            skCircle(sketch, "E43.13.0.15", {"center": v(593.9, -180) * mm, "radius": 3.5 * mm});
            skCircle(sketch, "E43.13.0.16", {"center": v(593.9, -150) * mm, "radius": 3.5 * mm});
            skCircle(sketch, "E43.13.0.17", {"center": v(593.9, -90) * mm, "radius": 3.5 * mm});
            skCircle(sketch, "E43.13.0.18", {"center": v(563.9, -135) * mm, "radius": 3.5 * mm});
            skCircle(sketch, "E43.13.0.19", {"center": v(563.9, -225) * mm, "radius": 3.5 * mm});
            skCircle(sketch, "E43.13.0.20", {"center": v(593.9, -210) * mm, "radius": 3.5 * mm});
            skCircle(sketch, "E43.13.0.21", {"center": v(563.9, -165) * mm, "radius": 3.5 * mm});
            skCircle(sketch, "E43.13.0.22", {"center": v(593.9, -270) * mm, "radius": 3.5 * mm});
            skCircle(sketch, "E43.13.0.23", {"center": v(593.9, -330) * mm, "radius": 3.5 * mm});
            skCircle(sketch, "E43.13.0.24", {"center": v(563.9, -315) * mm, "radius": 3.5 * mm});
            skCircle(sketch, "E43.13.0.25", {"center": v(563.9, -345) * mm, "radius": 3.5 * mm});
            skCircle(sketch, "E43.13.0.26", {"center": v(593.9, -360) * mm, "radius": 3.5 * mm});
            skLineSegment(sketch, "E43.14.0.0", {"start": v(533.9, -360) * mm, "end": v(533.9, -330) * mm, "construction": true});
            skCircle(sketch, "E43.14.0.1", {"center": v(533.9, -60) * mm, "radius": 3.5 * mm});
            skCircle(sketch, "E43.14.0.2", {"center": v(533.9, -30) * mm, "radius": 3.5 * mm});
            skCircle(sketch, "E43.14.0.3", {"center": v(533.9, 0) * mm, "radius": 3.5 * mm});
            skCircle(sketch, "E43.14.0.4", {"center": v(533.9, -240) * mm, "radius": 3.5 * mm});
            skCircle(sketch, "E43.14.0.5", {"center": v(533.9, -300) * mm, "radius": 3.5 * mm});
            skCircle(sketch, "E43.14.0.6", {"center": v(503.9, -75) * mm, "radius": 3.5 * mm});
            skCircle(sketch, "E43.14.0.7", {"center": v(503.9, -285) * mm, "radius": 3.5 * mm});
            skCircle(sketch, "E43.14.0.8", {"center": v(503.9, -105) * mm, "radius": 3.5 * mm});
            skCircle(sketch, "E43.14.0.9", {"center": v(503.9, -255) * mm, "radius": 3.5 * mm});
            skCircle(sketch, "E43.14.0.10", {"center": v(503.9, -195) * mm, "radius": 3.5 * mm});
            skLineSegment(sketch, "E43.14.0.11", {"start": v(503.9, -345) * mm, "end": v(503.9, -315) * mm, "construction": true});
            skCircle(sketch, "E43.14.0.12", {"center": v(503.9, -15) * mm, "radius": 3.5 * mm});
            skCircle(sketch, "E43.14.0.13", {"center": v(533.9, -120) * mm, "radius": 3.5 * mm});
            skCircle(sketch, "E43.14.0.14", {"center": v(503.9, -45) * mm, "radius": 3.5 * mm});
            skCircle(sketch, "E43.14.0.15", {"center": v(533.9, -180) * mm, "radius": 3.5 * mm});
            skCircle(sketch, "E43.14.0.16", {"center": v(533.9, -150) * mm, "radius": 3.5 * mm});
            skCircle(sketch, "E43.14.0.17", {"center": v(533.9, -90) * mm, "radius": 3.5 * mm});
            skCircle(sketch, "E43.14.0.18", {"center": v(503.9, -135) * mm, "radius": 3.5 * mm});
            skCircle(sketch, "E43.14.0.19", {"center": v(503.9, -225) * mm, "radius": 3.5 * mm});
            skCircle(sketch, "E43.14.0.20", {"center": v(533.9, -210) * mm, "radius": 3.5 * mm});
            skCircle(sketch, "E43.14.0.21", {"center": v(503.9, -165) * mm, "radius": 3.5 * mm});
            skCircle(sketch, "E43.14.0.22", {"center": v(533.9, -270) * mm, "radius": 3.5 * mm});
            skCircle(sketch, "E43.14.0.23", {"center": v(533.9, -330) * mm, "radius": 3.5 * mm});
            skCircle(sketch, "E43.14.0.24", {"center": v(503.9, -315) * mm, "radius": 3.5 * mm});
            skCircle(sketch, "E43.14.0.25", {"center": v(503.9, -345) * mm, "radius": 3.5 * mm});
            skCircle(sketch, "E43.14.0.26", {"center": v(533.9, -360) * mm, "radius": 3.5 * mm});
            skLineSegment(sketch, "E43.15.0.0", {"start": v(473.9, -360) * mm, "end": v(473.9, -330) * mm, "construction": true});
            skCircle(sketch, "E43.15.0.1", {"center": v(473.9, -60) * mm, "radius": 3.5 * mm});
            skCircle(sketch, "E43.15.0.2", {"center": v(473.9, -30) * mm, "radius": 3.5 * mm});
            skCircle(sketch, "E43.15.0.3", {"center": v(473.9, 0) * mm, "radius": 3.5 * mm});
            skCircle(sketch, "E43.15.0.4", {"center": v(473.9, -240) * mm, "radius": 3.5 * mm});
            skCircle(sketch, "E43.15.0.5", {"center": v(473.9, -300) * mm, "radius": 3.5 * mm});
            skCircle(sketch, "E43.15.0.6", {"center": v(443.9, -75) * mm, "radius": 3.5 * mm});
            skCircle(sketch, "E43.15.0.7", {"center": v(443.9, -285) * mm, "radius": 3.5 * mm});
            skCircle(sketch, "E43.15.0.8", {"center": v(443.9, -105) * mm, "radius": 3.5 * mm});
            skCircle(sketch, "E43.15.0.9", {"center": v(443.9, -255) * mm, "radius": 3.5 * mm});
            skCircle(sketch, "E43.15.0.10", {"center": v(443.9, -195) * mm, "radius": 3.5 * mm});
            skLineSegment(sketch, "E43.15.0.11", {"start": v(443.9, -345) * mm, "end": v(443.9, -315) * mm, "construction": true});
            skCircle(sketch, "E43.15.0.12", {"center": v(443.9, -15) * mm, "radius": 3.5 * mm});
            skCircle(sketch, "E43.15.0.13", {"center": v(473.9, -120) * mm, "radius": 3.5 * mm});
            skCircle(sketch, "E43.15.0.14", {"center": v(443.9, -45) * mm, "radius": 3.5 * mm});
            skCircle(sketch, "E43.15.0.15", {"center": v(473.9, -180) * mm, "radius": 3.5 * mm});
            skCircle(sketch, "E43.15.0.16", {"center": v(473.9, -150) * mm, "radius": 3.5 * mm});
            skCircle(sketch, "E43.15.0.17", {"center": v(473.9, -90) * mm, "radius": 3.5 * mm});
            skCircle(sketch, "E43.15.0.18", {"center": v(443.9, -135) * mm, "radius": 3.5 * mm});
            skCircle(sketch, "E43.15.0.19", {"center": v(443.9, -225) * mm, "radius": 3.5 * mm});
            skCircle(sketch, "E43.15.0.20", {"center": v(473.9, -210) * mm, "radius": 3.5 * mm});
            skCircle(sketch, "E43.15.0.21", {"center": v(443.9, -165) * mm, "radius": 3.5 * mm});
            skCircle(sketch, "E43.15.0.22", {"center": v(473.9, -270) * mm, "radius": 3.5 * mm});
            skCircle(sketch, "E43.15.0.23", {"center": v(473.9, -330) * mm, "radius": 3.5 * mm});
            skCircle(sketch, "E43.15.0.24", {"center": v(443.9, -315) * mm, "radius": 3.5 * mm});
            skCircle(sketch, "E43.15.0.25", {"center": v(443.9, -345) * mm, "radius": 3.5 * mm});
            skCircle(sketch, "E43.15.0.26", {"center": v(473.9, -360) * mm, "radius": 3.5 * mm});
            skLineSegment(sketch, "E43.16.0.0", {"start": v(413.9, -360) * mm, "end": v(413.9, -330) * mm, "construction": true});
            skCircle(sketch, "E43.16.0.1", {"center": v(413.9, -60) * mm, "radius": 3.5 * mm});
            skCircle(sketch, "E43.16.0.2", {"center": v(413.9, -30) * mm, "radius": 3.5 * mm});
            skCircle(sketch, "E43.16.0.3", {"center": v(413.9, 0) * mm, "radius": 3.5 * mm});
            skCircle(sketch, "E43.16.0.4", {"center": v(413.9, -240) * mm, "radius": 3.5 * mm});
            skCircle(sketch, "E43.16.0.5", {"center": v(413.9, -300) * mm, "radius": 3.5 * mm});
            skCircle(sketch, "E43.16.0.6", {"center": v(383.9, -75) * mm, "radius": 3.5 * mm});
            skCircle(sketch, "E43.16.0.7", {"center": v(383.9, -285) * mm, "radius": 3.5 * mm});
            skCircle(sketch, "E43.16.0.8", {"center": v(383.9, -105) * mm, "radius": 3.5 * mm});
            skCircle(sketch, "E43.16.0.9", {"center": v(383.9, -255) * mm, "radius": 3.5 * mm});
            skCircle(sketch, "E43.16.0.10", {"center": v(383.9, -195) * mm, "radius": 3.5 * mm});
            skLineSegment(sketch, "E43.16.0.11", {"start": v(383.9, -345) * mm, "end": v(383.9, -315) * mm, "construction": true});
            skCircle(sketch, "E43.16.0.12", {"center": v(383.9, -15) * mm, "radius": 3.5 * mm});
            skCircle(sketch, "E43.16.0.13", {"center": v(413.9, -120) * mm, "radius": 3.5 * mm});
            skCircle(sketch, "E43.16.0.14", {"center": v(383.9, -45) * mm, "radius": 3.5 * mm});
            skCircle(sketch, "E43.16.0.15", {"center": v(413.9, -180) * mm, "radius": 3.5 * mm});
            skCircle(sketch, "E43.16.0.16", {"center": v(413.9, -150) * mm, "radius": 3.5 * mm});
            skCircle(sketch, "E43.16.0.17", {"center": v(413.9, -90) * mm, "radius": 3.5 * mm});
            skCircle(sketch, "E43.16.0.18", {"center": v(383.9, -135) * mm, "radius": 3.5 * mm});
            skCircle(sketch, "E43.16.0.19", {"center": v(383.9, -225) * mm, "radius": 3.5 * mm});
            skCircle(sketch, "E43.16.0.20", {"center": v(413.9, -210) * mm, "radius": 3.5 * mm});
            skCircle(sketch, "E43.16.0.21", {"center": v(383.9, -165) * mm, "radius": 3.5 * mm});
            skCircle(sketch, "E43.16.0.22", {"center": v(413.9, -270) * mm, "radius": 3.5 * mm});
            skCircle(sketch, "E43.16.0.23", {"center": v(413.9, -330) * mm, "radius": 3.5 * mm});
            skCircle(sketch, "E43.16.0.24", {"center": v(383.9, -315) * mm, "radius": 3.5 * mm});
            skCircle(sketch, "E43.16.0.25", {"center": v(383.9, -345) * mm, "radius": 3.5 * mm});
            skCircle(sketch, "E43.16.0.26", {"center": v(413.9, -360) * mm, "radius": 3.5 * mm});
            skLineSegment(sketch, "E43.17.0.0", {"start": v(353.9, -360) * mm, "end": v(353.9, -330) * mm, "construction": true});
            skCircle(sketch, "E43.17.0.1", {"center": v(353.9, -60) * mm, "radius": 3.5 * mm});
            skCircle(sketch, "E43.17.0.2", {"center": v(353.9, -30) * mm, "radius": 3.5 * mm});
            skCircle(sketch, "E43.17.0.3", {"center": v(353.9, 0) * mm, "radius": 3.5 * mm});
            skCircle(sketch, "E43.17.0.4", {"center": v(353.9, -240) * mm, "radius": 3.5 * mm});
            skCircle(sketch, "E43.17.0.5", {"center": v(353.9, -300) * mm, "radius": 3.5 * mm});
            skCircle(sketch, "E43.17.0.6", {"center": v(323.9, -75) * mm, "radius": 3.5 * mm});
            skCircle(sketch, "E43.17.0.7", {"center": v(323.9, -285) * mm, "radius": 3.5 * mm});
            skCircle(sketch, "E43.17.0.8", {"center": v(323.9, -105) * mm, "radius": 3.5 * mm});
            skCircle(sketch, "E43.17.0.9", {"center": v(323.9, -255) * mm, "radius": 3.5 * mm});
            skCircle(sketch, "E43.17.0.10", {"center": v(323.9, -195) * mm, "radius": 3.5 * mm});
            skLineSegment(sketch, "E43.17.0.11", {"start": v(323.9, -345) * mm, "end": v(323.9, -315) * mm, "construction": true});
            skCircle(sketch, "E43.17.0.12", {"center": v(323.9, -15) * mm, "radius": 3.5 * mm});
            skCircle(sketch, "E43.17.0.13", {"center": v(353.9, -120) * mm, "radius": 3.5 * mm});
            skCircle(sketch, "E43.17.0.14", {"center": v(323.9, -45) * mm, "radius": 3.5 * mm});
            skCircle(sketch, "E43.17.0.15", {"center": v(353.9, -180) * mm, "radius": 3.5 * mm});
            skCircle(sketch, "E43.17.0.16", {"center": v(353.9, -150) * mm, "radius": 3.5 * mm});
            skCircle(sketch, "E43.17.0.17", {"center": v(353.9, -90) * mm, "radius": 3.5 * mm});
            skCircle(sketch, "E43.17.0.18", {"center": v(323.9, -135) * mm, "radius": 3.5 * mm});
            skCircle(sketch, "E43.17.0.19", {"center": v(323.9, -225) * mm, "radius": 3.5 * mm});
            skCircle(sketch, "E43.17.0.20", {"center": v(353.9, -210) * mm, "radius": 3.5 * mm});
            skCircle(sketch, "E43.17.0.21", {"center": v(323.9, -165) * mm, "radius": 3.5 * mm});
            skCircle(sketch, "E43.17.0.22", {"center": v(353.9, -270) * mm, "radius": 3.5 * mm});
            skCircle(sketch, "E43.17.0.23", {"center": v(353.9, -330) * mm, "radius": 3.5 * mm});
            skCircle(sketch, "E43.17.0.24", {"center": v(323.9, -315) * mm, "radius": 3.5 * mm});
            skCircle(sketch, "E43.17.0.25", {"center": v(323.9, -345) * mm, "radius": 3.5 * mm});
            skCircle(sketch, "E43.17.0.26", {"center": v(353.9, -360) * mm, "radius": 3.5 * mm});
            skLineSegment(sketch, "E43.18.0.0", {"start": v(293.9, -360) * mm, "end": v(293.9, -330) * mm, "construction": true});
            skCircle(sketch, "E43.18.0.1", {"center": v(293.9, -60) * mm, "radius": 3.5 * mm});
            skCircle(sketch, "E43.18.0.2", {"center": v(293.9, -30) * mm, "radius": 3.5 * mm});
            skCircle(sketch, "E43.18.0.3", {"center": v(293.9, 0) * mm, "radius": 3.5 * mm});
            skCircle(sketch, "E43.18.0.4", {"center": v(293.9, -240) * mm, "radius": 3.5 * mm});
            skCircle(sketch, "E43.18.0.5", {"center": v(293.9, -300) * mm, "radius": 3.5 * mm});
            skCircle(sketch, "E43.18.0.6", {"center": v(263.9, -75) * mm, "radius": 3.5 * mm});
            skCircle(sketch, "E43.18.0.7", {"center": v(263.9, -285) * mm, "radius": 3.5 * mm});
            skCircle(sketch, "E43.18.0.8", {"center": v(263.9, -105) * mm, "radius": 3.5 * mm});
            skCircle(sketch, "E43.18.0.9", {"center": v(263.9, -255) * mm, "radius": 3.5 * mm});
            skCircle(sketch, "E43.18.0.10", {"center": v(263.9, -195) * mm, "radius": 3.5 * mm});
            skLineSegment(sketch, "E43.18.0.11", {"start": v(263.9, -345) * mm, "end": v(263.9, -315) * mm, "construction": true});
            skCircle(sketch, "E43.18.0.12", {"center": v(263.9, -15) * mm, "radius": 3.5 * mm});
            skCircle(sketch, "E43.18.0.13", {"center": v(293.9, -120) * mm, "radius": 3.5 * mm});
            skCircle(sketch, "E43.18.0.14", {"center": v(263.9, -45) * mm, "radius": 3.5 * mm});
            skCircle(sketch, "E43.18.0.15", {"center": v(293.9, -180) * mm, "radius": 3.5 * mm});
            skCircle(sketch, "E43.18.0.16", {"center": v(293.9, -150) * mm, "radius": 3.5 * mm});
            skCircle(sketch, "E43.18.0.17", {"center": v(293.9, -90) * mm, "radius": 3.5 * mm});
            skCircle(sketch, "E43.18.0.18", {"center": v(263.9, -135) * mm, "radius": 3.5 * mm});
            skCircle(sketch, "E43.18.0.19", {"center": v(263.9, -225) * mm, "radius": 3.5 * mm});
            skCircle(sketch, "E43.18.0.20", {"center": v(293.9, -210) * mm, "radius": 3.5 * mm});
            skCircle(sketch, "E43.18.0.21", {"center": v(263.9, -165) * mm, "radius": 3.5 * mm});
            skCircle(sketch, "E43.18.0.22", {"center": v(293.9, -270) * mm, "radius": 3.5 * mm});
            skCircle(sketch, "E43.18.0.23", {"center": v(293.9, -330) * mm, "radius": 3.5 * mm});
            skCircle(sketch, "E43.18.0.24", {"center": v(263.9, -315) * mm, "radius": 3.5 * mm});
            skCircle(sketch, "E43.18.0.25", {"center": v(263.9, -345) * mm, "radius": 3.5 * mm});
            skCircle(sketch, "E43.18.0.26", {"center": v(293.9, -360) * mm, "radius": 3.5 * mm});
            skLineSegment(sketch, "E43.19.0.0", {"start": v(233.9, -360) * mm, "end": v(233.9, -330) * mm, "construction": true});
            skCircle(sketch, "E43.19.0.1", {"center": v(233.9, -60) * mm, "radius": 3.5 * mm});
            skCircle(sketch, "E43.19.0.2", {"center": v(233.9, -30) * mm, "radius": 3.5 * mm});
            skCircle(sketch, "E43.19.0.3", {"center": v(233.9, 0) * mm, "radius": 3.5 * mm});
            skCircle(sketch, "E43.19.0.4", {"center": v(233.9, -240) * mm, "radius": 3.5 * mm});
            skCircle(sketch, "E43.19.0.5", {"center": v(233.9, -300) * mm, "radius": 3.5 * mm});
            skCircle(sketch, "E43.19.0.6", {"center": v(203.9, -75) * mm, "radius": 3.5 * mm});
            skCircle(sketch, "E43.19.0.7", {"center": v(203.9, -285) * mm, "radius": 3.5 * mm});
            skCircle(sketch, "E43.19.0.8", {"center": v(203.9, -105) * mm, "radius": 3.5 * mm});
            skCircle(sketch, "E43.19.0.9", {"center": v(203.9, -255) * mm, "radius": 3.5 * mm});
            skCircle(sketch, "E43.19.0.10", {"center": v(203.9, -195) * mm, "radius": 3.5 * mm});
            skLineSegment(sketch, "E43.19.0.11", {"start": v(203.9, -345) * mm, "end": v(203.9, -315) * mm, "construction": true});
            skCircle(sketch, "E43.19.0.12", {"center": v(203.9, -15) * mm, "radius": 3.5 * mm});
            skCircle(sketch, "E43.19.0.13", {"center": v(233.9, -120) * mm, "radius": 3.5 * mm});
            skCircle(sketch, "E43.19.0.14", {"center": v(203.9, -45) * mm, "radius": 3.5 * mm});
            skCircle(sketch, "E43.19.0.15", {"center": v(233.9, -180) * mm, "radius": 3.5 * mm});
            skCircle(sketch, "E43.19.0.16", {"center": v(233.9, -150) * mm, "radius": 3.5 * mm});
            skCircle(sketch, "E43.19.0.17", {"center": v(233.9, -90) * mm, "radius": 3.5 * mm});
            skCircle(sketch, "E43.19.0.18", {"center": v(203.9, -135) * mm, "radius": 3.5 * mm});
            skCircle(sketch, "E43.19.0.19", {"center": v(203.9, -225) * mm, "radius": 3.5 * mm});
            skCircle(sketch, "E43.19.0.20", {"center": v(233.9, -210) * mm, "radius": 3.5 * mm});
            skCircle(sketch, "E43.19.0.21", {"center": v(203.9, -165) * mm, "radius": 3.5 * mm});
            skCircle(sketch, "E43.19.0.22", {"center": v(233.9, -270) * mm, "radius": 3.5 * mm});
            skCircle(sketch, "E43.19.0.23", {"center": v(233.9, -330) * mm, "radius": 3.5 * mm});
            skCircle(sketch, "E43.19.0.24", {"center": v(203.9, -315) * mm, "radius": 3.5 * mm});
            skCircle(sketch, "E43.19.0.25", {"center": v(203.9, -345) * mm, "radius": 3.5 * mm});
            skCircle(sketch, "E43.19.0.26", {"center": v(233.9, -360) * mm, "radius": 3.5 * mm});
            skLineSegment(sketch, "E43.20.0.0", {"start": v(173.9, -360) * mm, "end": v(173.9, -330) * mm, "construction": true});
            skCircle(sketch, "E43.20.0.1", {"center": v(173.9, -60) * mm, "radius": 3.5 * mm});
            skCircle(sketch, "E43.20.0.2", {"center": v(173.9, -30) * mm, "radius": 3.5 * mm});
            skCircle(sketch, "E43.20.0.3", {"center": v(173.9, 0) * mm, "radius": 3.5 * mm});
            skCircle(sketch, "E43.20.0.4", {"center": v(173.9, -240) * mm, "radius": 3.5 * mm});
            skCircle(sketch, "E43.20.0.5", {"center": v(173.9, -300) * mm, "radius": 3.5 * mm});
            skCircle(sketch, "E43.20.0.6", {"center": v(143.9, -75) * mm, "radius": 3.5 * mm});
            skCircle(sketch, "E43.20.0.7", {"center": v(143.9, -285) * mm, "radius": 3.5 * mm});
            skCircle(sketch, "E43.20.0.8", {"center": v(143.9, -105) * mm, "radius": 3.5 * mm});
            skCircle(sketch, "E43.20.0.9", {"center": v(143.9, -255) * mm, "radius": 3.5 * mm});
            skCircle(sketch, "E43.20.0.10", {"center": v(143.9, -195) * mm, "radius": 3.5 * mm});
            skLineSegment(sketch, "E43.20.0.11", {"start": v(143.9, -345) * mm, "end": v(143.9, -315) * mm, "construction": true});
            skCircle(sketch, "E43.20.0.12", {"center": v(143.9, -15) * mm, "radius": 3.5 * mm});
            skCircle(sketch, "E43.20.0.13", {"center": v(173.9, -120) * mm, "radius": 3.5 * mm});
            skCircle(sketch, "E43.20.0.14", {"center": v(143.9, -45) * mm, "radius": 3.5 * mm});
            skCircle(sketch, "E43.20.0.15", {"center": v(173.9, -180) * mm, "radius": 3.5 * mm});
            skCircle(sketch, "E43.20.0.16", {"center": v(173.9, -150) * mm, "radius": 3.5 * mm});
            skCircle(sketch, "E43.20.0.17", {"center": v(173.9, -90) * mm, "radius": 3.5 * mm});
            skCircle(sketch, "E43.20.0.18", {"center": v(143.9, -135) * mm, "radius": 3.5 * mm});
            skCircle(sketch, "E43.20.0.19", {"center": v(143.9, -225) * mm, "radius": 3.5 * mm});
            skCircle(sketch, "E43.20.0.20", {"center": v(173.9, -210) * mm, "radius": 3.5 * mm});
            skCircle(sketch, "E43.20.0.21", {"center": v(143.9, -165) * mm, "radius": 3.5 * mm});
            skCircle(sketch, "E43.20.0.22", {"center": v(173.9, -270) * mm, "radius": 3.5 * mm});
            skCircle(sketch, "E43.20.0.23", {"center": v(173.9, -330) * mm, "radius": 3.5 * mm});
            skCircle(sketch, "E43.20.0.24", {"center": v(143.9, -315) * mm, "radius": 3.5 * mm});
            skCircle(sketch, "E43.20.0.25", {"center": v(143.9, -345) * mm, "radius": 3.5 * mm});
            skCircle(sketch, "E43.20.0.26", {"center": v(173.9, -360) * mm, "radius": 3.5 * mm});
            skLineSegment(sketch, "E43.21.0.0", {"start": v(113.9, -360) * mm, "end": v(113.9, -330) * mm, "construction": true});
            skCircle(sketch, "E43.21.0.1", {"center": v(113.9, -60) * mm, "radius": 3.5 * mm});
            skCircle(sketch, "E43.21.0.2", {"center": v(113.9, -30) * mm, "radius": 3.5 * mm});
            skCircle(sketch, "E43.21.0.3", {"center": v(113.9, 0) * mm, "radius": 3.5 * mm});
            skCircle(sketch, "E43.21.0.4", {"center": v(113.9, -240) * mm, "radius": 3.5 * mm});
            skCircle(sketch, "E43.21.0.5", {"center": v(113.9, -300) * mm, "radius": 3.5 * mm});
            skCircle(sketch, "E43.21.0.6", {"center": v(83.9, -75) * mm, "radius": 3.5 * mm});
            skCircle(sketch, "E43.21.0.7", {"center": v(83.9, -285) * mm, "radius": 3.5 * mm});
            skCircle(sketch, "E43.21.0.8", {"center": v(83.9, -105) * mm, "radius": 3.5 * mm});
            skCircle(sketch, "E43.21.0.9", {"center": v(83.9, -255) * mm, "radius": 3.5 * mm});
            skCircle(sketch, "E43.21.0.10", {"center": v(83.9, -195) * mm, "radius": 3.5 * mm});
            skLineSegment(sketch, "E43.21.0.11", {"start": v(83.9, -345) * mm, "end": v(83.9, -315) * mm, "construction": true});
            skCircle(sketch, "E43.21.0.12", {"center": v(83.9, -15) * mm, "radius": 3.5 * mm});
            skCircle(sketch, "E43.21.0.13", {"center": v(113.9, -120) * mm, "radius": 3.5 * mm});
            skCircle(sketch, "E43.21.0.14", {"center": v(83.9, -45) * mm, "radius": 3.5 * mm});
            skCircle(sketch, "E43.21.0.15", {"center": v(113.9, -180) * mm, "radius": 3.5 * mm});
            skCircle(sketch, "E43.21.0.16", {"center": v(113.9, -150) * mm, "radius": 3.5 * mm});
            skCircle(sketch, "E43.21.0.17", {"center": v(113.9, -90) * mm, "radius": 3.5 * mm});
            skCircle(sketch, "E43.21.0.18", {"center": v(83.9, -135) * mm, "radius": 3.5 * mm});
            skCircle(sketch, "E43.21.0.19", {"center": v(83.9, -225) * mm, "radius": 3.5 * mm});
            skCircle(sketch, "E43.21.0.20", {"center": v(113.9, -210) * mm, "radius": 3.5 * mm});
            skCircle(sketch, "E43.21.0.21", {"center": v(83.9, -165) * mm, "radius": 3.5 * mm});
            skCircle(sketch, "E43.21.0.22", {"center": v(113.9, -270) * mm, "radius": 3.5 * mm});
            skCircle(sketch, "E43.21.0.23", {"center": v(113.9, -330) * mm, "radius": 3.5 * mm});
            skCircle(sketch, "E43.21.0.24", {"center": v(83.9, -315) * mm, "radius": 3.5 * mm});
            skCircle(sketch, "E43.21.0.25", {"center": v(83.9, -345) * mm, "radius": 3.5 * mm});
            skCircle(sketch, "E43.21.0.26", {"center": v(113.9, -360) * mm, "radius": 3.5 * mm});
            skLineSegment(sketch, "E43.22.0.0", {"start": v(53.9, -360) * mm, "end": v(53.9, -330) * mm, "construction": true});
            skCircle(sketch, "E43.22.0.1", {"center": v(53.9, -60) * mm, "radius": 3.5 * mm});
            skCircle(sketch, "E43.22.0.2", {"center": v(53.9, -30) * mm, "radius": 3.5 * mm});
            skCircle(sketch, "E43.22.0.3", {"center": v(53.9, 0) * mm, "radius": 3.5 * mm});
            skCircle(sketch, "E43.22.0.4", {"center": v(53.9, -240) * mm, "radius": 3.5 * mm});
            skCircle(sketch, "E43.22.0.5", {"center": v(53.9, -300) * mm, "radius": 3.5 * mm});
            skCircle(sketch, "E43.22.0.6", {"center": v(23.9, -75) * mm, "radius": 3.5 * mm});
            skCircle(sketch, "E43.22.0.7", {"center": v(23.9, -285) * mm, "radius": 3.5 * mm});
            skCircle(sketch, "E43.22.0.8", {"center": v(23.9, -105) * mm, "radius": 3.5 * mm});
            skCircle(sketch, "E43.22.0.9", {"center": v(23.9, -255) * mm, "radius": 3.5 * mm});
            skCircle(sketch, "E43.22.0.10", {"center": v(23.9, -195) * mm, "radius": 3.5 * mm});
            skLineSegment(sketch, "E43.22.0.11", {"start": v(23.9, -345) * mm, "end": v(23.9, -315) * mm, "construction": true});
            skCircle(sketch, "E43.22.0.12", {"center": v(23.9, -15) * mm, "radius": 3.5 * mm});
            skCircle(sketch, "E43.22.0.13", {"center": v(53.9, -120) * mm, "radius": 3.5 * mm});
            skCircle(sketch, "E43.22.0.14", {"center": v(23.9, -45) * mm, "radius": 3.5 * mm});
            skCircle(sketch, "E43.22.0.15", {"center": v(53.9, -180) * mm, "radius": 3.5 * mm});
            skCircle(sketch, "E43.22.0.16", {"center": v(53.9, -150) * mm, "radius": 3.5 * mm});
            skCircle(sketch, "E43.22.0.17", {"center": v(53.9, -90) * mm, "radius": 3.5 * mm});
            skCircle(sketch, "E43.22.0.18", {"center": v(23.9, -135) * mm, "radius": 3.5 * mm});
            skCircle(sketch, "E43.22.0.19", {"center": v(23.9, -225) * mm, "radius": 3.5 * mm});
            skCircle(sketch, "E43.22.0.20", {"center": v(53.9, -210) * mm, "radius": 3.5 * mm});
            skCircle(sketch, "E43.22.0.21", {"center": v(23.9, -165) * mm, "radius": 3.5 * mm});
            skCircle(sketch, "E43.22.0.22", {"center": v(53.9, -270) * mm, "radius": 3.5 * mm});
            skCircle(sketch, "E43.22.0.23", {"center": v(53.9, -330) * mm, "radius": 3.5 * mm});
            skCircle(sketch, "E43.22.0.24", {"center": v(23.9, -315) * mm, "radius": 3.5 * mm});
            skCircle(sketch, "E43.22.0.25", {"center": v(23.9, -345) * mm, "radius": 3.5 * mm});
            skCircle(sketch, "E43.22.0.26", {"center": v(53.9, -360) * mm, "radius": 3.5 * mm});
            skLineSegment(sketch, "E43.23.0.0", {"start": v(-6.1, -360) * mm, "end": v(-6.1, -330) * mm, "construction": true});
            skCircle(sketch, "E43.23.0.1", {"center": v(-6.1, -60) * mm, "radius": 3.5 * mm});
            skCircle(sketch, "E43.23.0.2", {"center": v(-6.1, -30) * mm, "radius": 3.5 * mm});
            skCircle(sketch, "E43.23.0.3", {"center": v(-6.1, 0) * mm, "radius": 3.5 * mm});
            skCircle(sketch, "E43.23.0.4", {"center": v(-6.1, -240) * mm, "radius": 3.5 * mm});
            skCircle(sketch, "E43.23.0.5", {"center": v(-6.1, -300) * mm, "radius": 3.5 * mm});
            skCircle(sketch, "E43.23.0.6", {"center": v(-36.1, -75) * mm, "radius": 3.5 * mm});
            skCircle(sketch, "E43.23.0.7", {"center": v(-36.1, -285) * mm, "radius": 3.5 * mm});
            skCircle(sketch, "E43.23.0.8", {"center": v(-36.1, -105) * mm, "radius": 3.5 * mm});
            skCircle(sketch, "E43.23.0.9", {"center": v(-36.1, -255) * mm, "radius": 3.5 * mm});
            skCircle(sketch, "E43.23.0.10", {"center": v(-36.1, -195) * mm, "radius": 3.5 * mm});
            skLineSegment(sketch, "E43.23.0.11", {"start": v(-36.1, -345) * mm, "end": v(-36.1, -315) * mm, "construction": true});
            skCircle(sketch, "E43.23.0.12", {"center": v(-36.1, -15) * mm, "radius": 3.5 * mm});
            skCircle(sketch, "E43.23.0.13", {"center": v(-6.1, -120) * mm, "radius": 3.5 * mm});
            skCircle(sketch, "E43.23.0.14", {"center": v(-36.1, -45) * mm, "radius": 3.5 * mm});
            skCircle(sketch, "E43.23.0.15", {"center": v(-6.1, -180) * mm, "radius": 3.5 * mm});
            skCircle(sketch, "E43.23.0.16", {"center": v(-6.1, -150) * mm, "radius": 3.5 * mm});
            skCircle(sketch, "E43.23.0.17", {"center": v(-6.1, -90) * mm, "radius": 3.5 * mm});
            skCircle(sketch, "E43.23.0.18", {"center": v(-36.1, -135) * mm, "radius": 3.5 * mm});
            skCircle(sketch, "E43.23.0.19", {"center": v(-36.1, -225) * mm, "radius": 3.5 * mm});
            skCircle(sketch, "E43.23.0.20", {"center": v(-6.1, -210) * mm, "radius": 3.5 * mm});
            skCircle(sketch, "E43.23.0.21", {"center": v(-36.1, -165) * mm, "radius": 3.5 * mm});
            skCircle(sketch, "E43.23.0.22", {"center": v(-6.1, -270) * mm, "radius": 3.5 * mm});
            skCircle(sketch, "E43.23.0.23", {"center": v(-6.1, -330) * mm, "radius": 3.5 * mm});
            skCircle(sketch, "E43.23.0.24", {"center": v(-36.1, -315) * mm, "radius": 3.5 * mm});
            skCircle(sketch, "E43.23.0.25", {"center": v(-36.1, -345) * mm, "radius": 3.5 * mm});
            skCircle(sketch, "E43.23.0.26", {"center": v(-6.1, -360) * mm, "radius": 3.5 * mm});
            skLineSegment(sketch, "E43.24.0.0", {"start": v(-66.1, -360) * mm, "end": v(-66.1, -330) * mm, "construction": true});
            skCircle(sketch, "E43.24.0.1", {"center": v(-66.1, -60) * mm, "radius": 3.5 * mm});
            skCircle(sketch, "E43.24.0.2", {"center": v(-66.1, -30) * mm, "radius": 3.5 * mm});
            skCircle(sketch, "E43.24.0.3", {"center": v(-66.1, 0) * mm, "radius": 3.5 * mm});
            skCircle(sketch, "E43.24.0.4", {"center": v(-66.1, -240) * mm, "radius": 3.5 * mm});
            skCircle(sketch, "E43.24.0.5", {"center": v(-66.1, -300) * mm, "radius": 3.5 * mm});
            skCircle(sketch, "E43.24.0.6", {"center": v(-96.1, -75) * mm, "radius": 3.5 * mm});
            skCircle(sketch, "E43.24.0.7", {"center": v(-96.1, -285) * mm, "radius": 3.5 * mm});
            skCircle(sketch, "E43.24.0.8", {"center": v(-96.1, -105) * mm, "radius": 3.5 * mm});
            skCircle(sketch, "E43.24.0.9", {"center": v(-96.1, -255) * mm, "radius": 3.5 * mm});
            skCircle(sketch, "E43.24.0.10", {"center": v(-96.1, -195) * mm, "radius": 3.5 * mm});
            skLineSegment(sketch, "E43.24.0.11", {"start": v(-96.1, -345) * mm, "end": v(-96.1, -315) * mm, "construction": true});
            skCircle(sketch, "E43.24.0.12", {"center": v(-96.1, -15) * mm, "radius": 3.5 * mm});
            skCircle(sketch, "E43.24.0.13", {"center": v(-66.1, -120) * mm, "radius": 3.5 * mm});
            skCircle(sketch, "E43.24.0.14", {"center": v(-96.1, -45) * mm, "radius": 3.5 * mm});
            skCircle(sketch, "E43.24.0.15", {"center": v(-66.1, -180) * mm, "radius": 3.5 * mm});
            skCircle(sketch, "E43.24.0.16", {"center": v(-66.1, -150) * mm, "radius": 3.5 * mm});
            skCircle(sketch, "E43.24.0.17", {"center": v(-66.1, -90) * mm, "radius": 3.5 * mm});
            skCircle(sketch, "E43.24.0.18", {"center": v(-96.1, -135) * mm, "radius": 3.5 * mm});
            skCircle(sketch, "E43.24.0.19", {"center": v(-96.1, -225) * mm, "radius": 3.5 * mm});
            skCircle(sketch, "E43.24.0.20", {"center": v(-66.1, -210) * mm, "radius": 3.5 * mm});
            skCircle(sketch, "E43.24.0.21", {"center": v(-96.1, -165) * mm, "radius": 3.5 * mm});
            skCircle(sketch, "E43.24.0.22", {"center": v(-66.1, -270) * mm, "radius": 3.5 * mm});
            skCircle(sketch, "E43.24.0.23", {"center": v(-66.1, -330) * mm, "radius": 3.5 * mm});
            skCircle(sketch, "E43.24.0.24", {"center": v(-96.1, -315) * mm, "radius": 3.5 * mm});
            skCircle(sketch, "E43.24.0.25", {"center": v(-96.1, -345) * mm, "radius": 3.5 * mm});
            skCircle(sketch, "E43.24.0.26", {"center": v(-66.1, -360) * mm, "radius": 3.5 * mm});
            skLineSegment(sketch, "E43.25.0.0", {"start": v(-126.1, -360) * mm, "end": v(-126.1, -330) * mm, "construction": true});
            skCircle(sketch, "E43.25.0.1", {"center": v(-126.1, -60) * mm, "radius": 3.5 * mm});
            skCircle(sketch, "E43.25.0.2", {"center": v(-126.1, -30) * mm, "radius": 3.5 * mm});
            skCircle(sketch, "E43.25.0.3", {"center": v(-126.1, 0) * mm, "radius": 3.5 * mm});
            skCircle(sketch, "E43.25.0.4", {"center": v(-126.1, -240) * mm, "radius": 3.5 * mm});
            skCircle(sketch, "E43.25.0.5", {"center": v(-126.1, -300) * mm, "radius": 3.5 * mm});
            skCircle(sketch, "E43.25.0.6", {"center": v(-156.1, -75) * mm, "radius": 3.5 * mm});
            skCircle(sketch, "E43.25.0.7", {"center": v(-156.1, -285) * mm, "radius": 3.5 * mm});
            skCircle(sketch, "E43.25.0.8", {"center": v(-156.1, -105) * mm, "radius": 3.5 * mm});
            skCircle(sketch, "E43.25.0.9", {"center": v(-156.1, -255) * mm, "radius": 3.5 * mm});
            skCircle(sketch, "E43.25.0.10", {"center": v(-156.1, -195) * mm, "radius": 3.5 * mm});
            skLineSegment(sketch, "E43.25.0.11", {"start": v(-156.1, -345) * mm, "end": v(-156.1, -315) * mm, "construction": true});
            skCircle(sketch, "E43.25.0.12", {"center": v(-156.1, -15) * mm, "radius": 3.5 * mm});
            skCircle(sketch, "E43.25.0.13", {"center": v(-126.1, -120) * mm, "radius": 3.5 * mm});
            skCircle(sketch, "E43.25.0.14", {"center": v(-156.1, -45) * mm, "radius": 3.5 * mm});
            skCircle(sketch, "E43.25.0.15", {"center": v(-126.1, -180) * mm, "radius": 3.5 * mm});
            skCircle(sketch, "E43.25.0.16", {"center": v(-126.1, -150) * mm, "radius": 3.5 * mm});
            skCircle(sketch, "E43.25.0.17", {"center": v(-126.1, -90) * mm, "radius": 3.5 * mm});
            skCircle(sketch, "E43.25.0.18", {"center": v(-156.1, -135) * mm, "radius": 3.5 * mm});
            skCircle(sketch, "E43.25.0.19", {"center": v(-156.1, -225) * mm, "radius": 3.5 * mm});
            skCircle(sketch, "E43.25.0.20", {"center": v(-126.1, -210) * mm, "radius": 3.5 * mm});
            skCircle(sketch, "E43.25.0.21", {"center": v(-156.1, -165) * mm, "radius": 3.5 * mm});
            skCircle(sketch, "E43.25.0.22", {"center": v(-126.1, -270) * mm, "radius": 3.5 * mm});
            skCircle(sketch, "E43.25.0.23", {"center": v(-126.1, -330) * mm, "radius": 3.5 * mm});
            skCircle(sketch, "E43.25.0.24", {"center": v(-156.1, -315) * mm, "radius": 3.5 * mm});
            skCircle(sketch, "E43.25.0.25", {"center": v(-156.1, -345) * mm, "radius": 3.5 * mm});
            skCircle(sketch, "E43.25.0.26", {"center": v(-126.1, -360) * mm, "radius": 3.5 * mm});
            skLineSegment(sketch, "E43.26.0.0", {"start": v(-186.1, -360) * mm, "end": v(-186.1, -330) * mm, "construction": true});
            skCircle(sketch, "E43.26.0.1", {"center": v(-186.1, -60) * mm, "radius": 3.5 * mm});
            skCircle(sketch, "E43.26.0.2", {"center": v(-186.1, -30) * mm, "radius": 3.5 * mm});
            skCircle(sketch, "E43.26.0.3", {"center": v(-186.1, 0) * mm, "radius": 3.5 * mm});
            skCircle(sketch, "E43.26.0.4", {"center": v(-186.1, -240) * mm, "radius": 3.5 * mm});
            skCircle(sketch, "E43.26.0.5", {"center": v(-186.1, -300) * mm, "radius": 3.5 * mm});
            skCircle(sketch, "E43.26.0.6", {"center": v(-216.1, -75) * mm, "radius": 3.5 * mm});
            skCircle(sketch, "E43.26.0.7", {"center": v(-216.1, -285) * mm, "radius": 3.5 * mm});
            skCircle(sketch, "E43.26.0.8", {"center": v(-216.1, -105) * mm, "radius": 3.5 * mm});
            skCircle(sketch, "E43.26.0.9", {"center": v(-216.1, -255) * mm, "radius": 3.5 * mm});
            skCircle(sketch, "E43.26.0.10", {"center": v(-216.1, -195) * mm, "radius": 3.5 * mm});
            skLineSegment(sketch, "E43.26.0.11", {"start": v(-216.1, -345) * mm, "end": v(-216.1, -315) * mm, "construction": true});
            skCircle(sketch, "E43.26.0.12", {"center": v(-216.1, -15) * mm, "radius": 3.5 * mm});
            skCircle(sketch, "E43.26.0.13", {"center": v(-186.1, -120) * mm, "radius": 3.5 * mm});
            skCircle(sketch, "E43.26.0.14", {"center": v(-216.1, -45) * mm, "radius": 3.5 * mm});
            skCircle(sketch, "E43.26.0.15", {"center": v(-186.1, -180) * mm, "radius": 3.5 * mm});
            skCircle(sketch, "E43.26.0.16", {"center": v(-186.1, -150) * mm, "radius": 3.5 * mm});
            skCircle(sketch, "E43.26.0.17", {"center": v(-186.1, -90) * mm, "radius": 3.5 * mm});
            skCircle(sketch, "E43.26.0.18", {"center": v(-216.1, -135) * mm, "radius": 3.5 * mm});
            skCircle(sketch, "E43.26.0.19", {"center": v(-216.1, -225) * mm, "radius": 3.5 * mm});
            skCircle(sketch, "E43.26.0.20", {"center": v(-186.1, -210) * mm, "radius": 3.5 * mm});
            skCircle(sketch, "E43.26.0.21", {"center": v(-216.1, -165) * mm, "radius": 3.5 * mm});
            skCircle(sketch, "E43.26.0.22", {"center": v(-186.1, -270) * mm, "radius": 3.5 * mm});
            skCircle(sketch, "E43.26.0.23", {"center": v(-186.1, -330) * mm, "radius": 3.5 * mm});
            skCircle(sketch, "E43.26.0.24", {"center": v(-216.1, -315) * mm, "radius": 3.5 * mm});
            skCircle(sketch, "E43.26.0.25", {"center": v(-216.1, -345) * mm, "radius": 3.5 * mm});
            skCircle(sketch, "E43.26.0.26", {"center": v(-186.1, -360) * mm, "radius": 3.5 * mm});
            skLineSegment(sketch, "E43.27.0.0", {"start": v(-246.1, -360) * mm, "end": v(-246.1, -330) * mm, "construction": true});
            skCircle(sketch, "E43.27.0.1", {"center": v(-246.1, -60) * mm, "radius": 3.5 * mm});
            skCircle(sketch, "E43.27.0.2", {"center": v(-246.1, -30) * mm, "radius": 3.5 * mm});
            skCircle(sketch, "E43.27.0.3", {"center": v(-246.1, 0) * mm, "radius": 3.5 * mm});
            skCircle(sketch, "E43.27.0.4", {"center": v(-246.1, -240) * mm, "radius": 3.5 * mm});
            skCircle(sketch, "E43.27.0.5", {"center": v(-246.1, -300) * mm, "radius": 3.5 * mm});
            skCircle(sketch, "E43.27.0.6", {"center": v(-276.1, -75) * mm, "radius": 3.5 * mm});
            skCircle(sketch, "E43.27.0.7", {"center": v(-276.1, -285) * mm, "radius": 3.5 * mm});
            skCircle(sketch, "E43.27.0.8", {"center": v(-276.1, -105) * mm, "radius": 3.5 * mm});
            skCircle(sketch, "E43.27.0.9", {"center": v(-276.1, -255) * mm, "radius": 3.5 * mm});
            skCircle(sketch, "E43.27.0.10", {"center": v(-276.1, -195) * mm, "radius": 3.5 * mm});
            skLineSegment(sketch, "E43.27.0.11", {"start": v(-276.1, -345) * mm, "end": v(-276.1, -315) * mm, "construction": true});
            skCircle(sketch, "E43.27.0.12", {"center": v(-276.1, -15) * mm, "radius": 3.5 * mm});
            skCircle(sketch, "E43.27.0.13", {"center": v(-246.1, -120) * mm, "radius": 3.5 * mm});
            skCircle(sketch, "E43.27.0.14", {"center": v(-276.1, -45) * mm, "radius": 3.5 * mm});
            skCircle(sketch, "E43.27.0.15", {"center": v(-246.1, -180) * mm, "radius": 3.5 * mm});
            skCircle(sketch, "E43.27.0.16", {"center": v(-246.1, -150) * mm, "radius": 3.5 * mm});
            skCircle(sketch, "E43.27.0.17", {"center": v(-246.1, -90) * mm, "radius": 3.5 * mm});
            skCircle(sketch, "E43.27.0.18", {"center": v(-276.1, -135) * mm, "radius": 3.5 * mm});
            skCircle(sketch, "E43.27.0.19", {"center": v(-276.1, -225) * mm, "radius": 3.5 * mm});
            skCircle(sketch, "E43.27.0.20", {"center": v(-246.1, -210) * mm, "radius": 3.5 * mm});
            skCircle(sketch, "E43.27.0.21", {"center": v(-276.1, -165) * mm, "radius": 3.5 * mm});
            skCircle(sketch, "E43.27.0.22", {"center": v(-246.1, -270) * mm, "radius": 3.5 * mm});
            skCircle(sketch, "E43.27.0.23", {"center": v(-246.1, -330) * mm, "radius": 3.5 * mm});
            skCircle(sketch, "E43.27.0.24", {"center": v(-276.1, -315) * mm, "radius": 3.5 * mm});
            skCircle(sketch, "E43.27.0.25", {"center": v(-276.1, -345) * mm, "radius": 3.5 * mm});
            skCircle(sketch, "E43.27.0.26", {"center": v(-246.1, -360) * mm, "radius": 3.5 * mm});
            skLineSegment(sketch, "E43.28.0.0", {"start": v(-306.1, -360) * mm, "end": v(-306.1, -330) * mm, "construction": true});
            skCircle(sketch, "E43.28.0.1", {"center": v(-306.1, -60) * mm, "radius": 3.5 * mm});
            skCircle(sketch, "E43.28.0.2", {"center": v(-306.1, -30) * mm, "radius": 3.5 * mm});
            skCircle(sketch, "E43.28.0.3", {"center": v(-306.1, 0) * mm, "radius": 3.5 * mm});
            skCircle(sketch, "E43.28.0.4", {"center": v(-306.1, -240) * mm, "radius": 3.5 * mm});
            skCircle(sketch, "E43.28.0.5", {"center": v(-306.1, -300) * mm, "radius": 3.5 * mm});
            skCircle(sketch, "E43.28.0.6", {"center": v(-336.1, -75) * mm, "radius": 3.5 * mm});
            skCircle(sketch, "E43.28.0.7", {"center": v(-336.1, -285) * mm, "radius": 3.5 * mm});
            skCircle(sketch, "E43.28.0.8", {"center": v(-336.1, -105) * mm, "radius": 3.5 * mm});
            skCircle(sketch, "E43.28.0.9", {"center": v(-336.1, -255) * mm, "radius": 3.5 * mm});
            skCircle(sketch, "E43.28.0.10", {"center": v(-336.1, -195) * mm, "radius": 3.5 * mm});
            skLineSegment(sketch, "E43.28.0.11", {"start": v(-336.1, -345) * mm, "end": v(-336.1, -315) * mm, "construction": true});
            skCircle(sketch, "E43.28.0.12", {"center": v(-336.1, -15) * mm, "radius": 3.5 * mm});
            skCircle(sketch, "E43.28.0.13", {"center": v(-306.1, -120) * mm, "radius": 3.5 * mm});
            skCircle(sketch, "E43.28.0.14", {"center": v(-336.1, -45) * mm, "radius": 3.5 * mm});
            skCircle(sketch, "E43.28.0.15", {"center": v(-306.1, -180) * mm, "radius": 3.5 * mm});
            skCircle(sketch, "E43.28.0.16", {"center": v(-306.1, -150) * mm, "radius": 3.5 * mm});
            skCircle(sketch, "E43.28.0.17", {"center": v(-306.1, -90) * mm, "radius": 3.5 * mm});
            skCircle(sketch, "E43.28.0.18", {"center": v(-336.1, -135) * mm, "radius": 3.5 * mm});
            skCircle(sketch, "E43.28.0.19", {"center": v(-336.1, -225) * mm, "radius": 3.5 * mm});
            skCircle(sketch, "E43.28.0.20", {"center": v(-306.1, -210) * mm, "radius": 3.5 * mm});
            skCircle(sketch, "E43.28.0.21", {"center": v(-336.1, -165) * mm, "radius": 3.5 * mm});
            skCircle(sketch, "E43.28.0.22", {"center": v(-306.1, -270) * mm, "radius": 3.5 * mm});
            skCircle(sketch, "E43.28.0.23", {"center": v(-306.1, -330) * mm, "radius": 3.5 * mm});
            skCircle(sketch, "E43.28.0.24", {"center": v(-336.1, -315) * mm, "radius": 3.5 * mm});
            skCircle(sketch, "E43.28.0.25", {"center": v(-336.1, -345) * mm, "radius": 3.5 * mm});
            skCircle(sketch, "E43.28.0.26", {"center": v(-306.1, -360) * mm, "radius": 3.5 * mm});
            skLineSegment(sketch, "E43.29.0.0", {"start": v(-366.1, -360) * mm, "end": v(-366.1, -330) * mm, "construction": true});
            skCircle(sketch, "E43.29.0.1", {"center": v(-366.1, -60) * mm, "radius": 3.5 * mm});
            skCircle(sketch, "E43.29.0.2", {"center": v(-366.1, -30) * mm, "radius": 3.5 * mm});
            skCircle(sketch, "E43.29.0.3", {"center": v(-366.1, 0) * mm, "radius": 3.5 * mm});
            skCircle(sketch, "E43.29.0.4", {"center": v(-366.1, -240) * mm, "radius": 3.5 * mm});
            skCircle(sketch, "E43.29.0.5", {"center": v(-366.1, -300) * mm, "radius": 3.5 * mm});
            skCircle(sketch, "E43.29.0.6", {"center": v(-396.1, -75) * mm, "radius": 3.5 * mm});
            skCircle(sketch, "E43.29.0.7", {"center": v(-396.1, -285) * mm, "radius": 3.5 * mm});
            skCircle(sketch, "E43.29.0.8", {"center": v(-396.1, -105) * mm, "radius": 3.5 * mm});
            skCircle(sketch, "E43.29.0.9", {"center": v(-396.1, -255) * mm, "radius": 3.5 * mm});
            skCircle(sketch, "E43.29.0.10", {"center": v(-396.1, -195) * mm, "radius": 3.5 * mm});
            skLineSegment(sketch, "E43.29.0.11", {"start": v(-396.1, -345) * mm, "end": v(-396.1, -315) * mm, "construction": true});
            skCircle(sketch, "E43.29.0.12", {"center": v(-396.1, -15) * mm, "radius": 3.5 * mm});
            skCircle(sketch, "E43.29.0.13", {"center": v(-366.1, -120) * mm, "radius": 3.5 * mm});
            skCircle(sketch, "E43.29.0.14", {"center": v(-396.1, -45) * mm, "radius": 3.5 * mm});
            skCircle(sketch, "E43.29.0.15", {"center": v(-366.1, -180) * mm, "radius": 3.5 * mm});
            skCircle(sketch, "E43.29.0.16", {"center": v(-366.1, -150) * mm, "radius": 3.5 * mm});
            skCircle(sketch, "E43.29.0.17", {"center": v(-366.1, -90) * mm, "radius": 3.5 * mm});
            skCircle(sketch, "E43.29.0.18", {"center": v(-396.1, -135) * mm, "radius": 3.5 * mm});
            skCircle(sketch, "E43.29.0.19", {"center": v(-396.1, -225) * mm, "radius": 3.5 * mm});
            skCircle(sketch, "E43.29.0.20", {"center": v(-366.1, -210) * mm, "radius": 3.5 * mm});
            skCircle(sketch, "E43.29.0.21", {"center": v(-396.1, -165) * mm, "radius": 3.5 * mm});
            skCircle(sketch, "E43.29.0.22", {"center": v(-366.1, -270) * mm, "radius": 3.5 * mm});
            skCircle(sketch, "E43.29.0.23", {"center": v(-366.1, -330) * mm, "radius": 3.5 * mm});
            skCircle(sketch, "E43.29.0.24", {"center": v(-396.1, -315) * mm, "radius": 3.5 * mm});
            skCircle(sketch, "E43.29.0.25", {"center": v(-396.1, -345) * mm, "radius": 3.5 * mm});
            skCircle(sketch, "E43.29.0.26", {"center": v(-366.1, -360) * mm, "radius": 3.5 * mm});
            skLineSegment(sketch, "E43.30.0.0", {"start": v(-426.1, -360) * mm, "end": v(-426.1, -330) * mm, "construction": true});
            skCircle(sketch, "E43.30.0.1", {"center": v(-426.1, -60) * mm, "radius": 3.5 * mm});
            skCircle(sketch, "E43.30.0.2", {"center": v(-426.1, -30) * mm, "radius": 3.5 * mm});
            skCircle(sketch, "E43.30.0.3", {"center": v(-426.1, 0) * mm, "radius": 3.5 * mm});
            skCircle(sketch, "E43.30.0.4", {"center": v(-426.1, -240) * mm, "radius": 3.5 * mm});
            skCircle(sketch, "E43.30.0.5", {"center": v(-426.1, -300) * mm, "radius": 3.5 * mm});
            skCircle(sketch, "E43.30.0.6", {"center": v(-456.1, -75) * mm, "radius": 3.5 * mm});
            skCircle(sketch, "E43.30.0.7", {"center": v(-456.1, -285) * mm, "radius": 3.5 * mm});
            skCircle(sketch, "E43.30.0.8", {"center": v(-456.1, -105) * mm, "radius": 3.5 * mm});
            skCircle(sketch, "E43.30.0.9", {"center": v(-456.1, -255) * mm, "radius": 3.5 * mm});
            skCircle(sketch, "E43.30.0.10", {"center": v(-456.1, -195) * mm, "radius": 3.5 * mm});
            skLineSegment(sketch, "E43.30.0.11", {"start": v(-456.1, -345) * mm, "end": v(-456.1, -315) * mm, "construction": true});
            skCircle(sketch, "E43.30.0.12", {"center": v(-456.1, -15) * mm, "radius": 3.5 * mm});
            skCircle(sketch, "E43.30.0.13", {"center": v(-426.1, -120) * mm, "radius": 3.5 * mm});
            skCircle(sketch, "E43.30.0.14", {"center": v(-456.1, -45) * mm, "radius": 3.5 * mm});
            skCircle(sketch, "E43.30.0.15", {"center": v(-426.1, -180) * mm, "radius": 3.5 * mm});
            skCircle(sketch, "E43.30.0.16", {"center": v(-426.1, -150) * mm, "radius": 3.5 * mm});
            skCircle(sketch, "E43.30.0.17", {"center": v(-426.1, -90) * mm, "radius": 3.5 * mm});
            skCircle(sketch, "E43.30.0.18", {"center": v(-456.1, -135) * mm, "radius": 3.5 * mm});
            skCircle(sketch, "E43.30.0.19", {"center": v(-456.1, -225) * mm, "radius": 3.5 * mm});
            skCircle(sketch, "E43.30.0.20", {"center": v(-426.1, -210) * mm, "radius": 3.5 * mm});
            skCircle(sketch, "E43.30.0.21", {"center": v(-456.1, -165) * mm, "radius": 3.5 * mm});
            skCircle(sketch, "E43.30.0.22", {"center": v(-426.1, -270) * mm, "radius": 3.5 * mm});
            skCircle(sketch, "E43.30.0.23", {"center": v(-426.1, -330) * mm, "radius": 3.5 * mm});
            skCircle(sketch, "E43.30.0.24", {"center": v(-456.1, -315) * mm, "radius": 3.5 * mm});
            skCircle(sketch, "E43.30.0.25", {"center": v(-456.1, -345) * mm, "radius": 3.5 * mm});
            skCircle(sketch, "E43.30.0.26", {"center": v(-426.1, -360) * mm, "radius": 3.5 * mm});
            skLineSegment(sketch, "E43.31.0.0", {"start": v(-486.1, -360) * mm, "end": v(-486.1, -330) * mm, "construction": true});
            skCircle(sketch, "E43.31.0.1", {"center": v(-486.1, -60) * mm, "radius": 3.5 * mm});
            skCircle(sketch, "E43.31.0.2", {"center": v(-486.1, -30) * mm, "radius": 3.5 * mm});
            skCircle(sketch, "E43.31.0.3", {"center": v(-486.1, 0) * mm, "radius": 3.5 * mm});
            skCircle(sketch, "E43.31.0.4", {"center": v(-486.1, -240) * mm, "radius": 3.5 * mm});
            skCircle(sketch, "E43.31.0.5", {"center": v(-486.1, -300) * mm, "radius": 3.5 * mm});
            skCircle(sketch, "E43.31.0.6", {"center": v(-516.1, -75) * mm, "radius": 3.5 * mm});
            skCircle(sketch, "E43.31.0.7", {"center": v(-516.1, -285) * mm, "radius": 3.5 * mm});
            skCircle(sketch, "E43.31.0.8", {"center": v(-516.1, -105) * mm, "radius": 3.5 * mm});
            skCircle(sketch, "E43.31.0.9", {"center": v(-516.1, -255) * mm, "radius": 3.5 * mm});
            skCircle(sketch, "E43.31.0.10", {"center": v(-516.1, -195) * mm, "radius": 3.5 * mm});
            skLineSegment(sketch, "E43.31.0.11", {"start": v(-516.1, -345) * mm, "end": v(-516.1, -315) * mm, "construction": true});
            skCircle(sketch, "E43.31.0.12", {"center": v(-516.1, -15) * mm, "radius": 3.5 * mm});
            skCircle(sketch, "E43.31.0.13", {"center": v(-486.1, -120) * mm, "radius": 3.5 * mm});
            skCircle(sketch, "E43.31.0.14", {"center": v(-516.1, -45) * mm, "radius": 3.5 * mm});
            skCircle(sketch, "E43.31.0.15", {"center": v(-486.1, -180) * mm, "radius": 3.5 * mm});
            skCircle(sketch, "E43.31.0.16", {"center": v(-486.1, -150) * mm, "radius": 3.5 * mm});
            skCircle(sketch, "E43.31.0.17", {"center": v(-486.1, -90) * mm, "radius": 3.5 * mm});
            skCircle(sketch, "E43.31.0.18", {"center": v(-516.1, -135) * mm, "radius": 3.5 * mm});
            skCircle(sketch, "E43.31.0.19", {"center": v(-516.1, -225) * mm, "radius": 3.5 * mm});
            skCircle(sketch, "E43.31.0.20", {"center": v(-486.1, -210) * mm, "radius": 3.5 * mm});
            skCircle(sketch, "E43.31.0.21", {"center": v(-516.1, -165) * mm, "radius": 3.5 * mm});
            skCircle(sketch, "E43.31.0.22", {"center": v(-486.1, -270) * mm, "radius": 3.5 * mm});
            skCircle(sketch, "E43.31.0.23", {"center": v(-486.1, -330) * mm, "radius": 3.5 * mm});
            skCircle(sketch, "E43.31.0.24", {"center": v(-516.1, -315) * mm, "radius": 3.5 * mm});
            skCircle(sketch, "E43.31.0.25", {"center": v(-516.1, -345) * mm, "radius": 3.5 * mm});
            skCircle(sketch, "E43.31.0.26", {"center": v(-486.1, -360) * mm, "radius": 3.5 * mm});
            skLineSegment(sketch, "E43.32.0.0", {"start": v(-546.1, -360) * mm, "end": v(-546.1, -330) * mm, "construction": true});
            skCircle(sketch, "E43.32.0.1", {"center": v(-546.1, -60) * mm, "radius": 3.5 * mm});
            skCircle(sketch, "E43.32.0.2", {"center": v(-546.1, -30) * mm, "radius": 3.5 * mm});
            skCircle(sketch, "E43.32.0.3", {"center": v(-546.1, 0) * mm, "radius": 3.5 * mm});
            skCircle(sketch, "E43.32.0.4", {"center": v(-546.1, -240) * mm, "radius": 3.5 * mm});
            skCircle(sketch, "E43.32.0.5", {"center": v(-546.1, -300) * mm, "radius": 3.5 * mm});
            skCircle(sketch, "E43.32.0.6", {"center": v(-576.1, -75) * mm, "radius": 3.5 * mm});
            skCircle(sketch, "E43.32.0.7", {"center": v(-576.1, -285) * mm, "radius": 3.5 * mm});
            skCircle(sketch, "E43.32.0.8", {"center": v(-576.1, -105) * mm, "radius": 3.5 * mm});
            skCircle(sketch, "E43.32.0.9", {"center": v(-576.1, -255) * mm, "radius": 3.5 * mm});
            skCircle(sketch, "E43.32.0.10", {"center": v(-576.1, -195) * mm, "radius": 3.5 * mm});
            skLineSegment(sketch, "E43.32.0.11", {"start": v(-576.1, -345) * mm, "end": v(-576.1, -315) * mm, "construction": true});
            skCircle(sketch, "E43.32.0.12", {"center": v(-576.1, -15) * mm, "radius": 3.5 * mm});
            skCircle(sketch, "E43.32.0.13", {"center": v(-546.1, -120) * mm, "radius": 3.5 * mm});
            skCircle(sketch, "E43.32.0.14", {"center": v(-576.1, -45) * mm, "radius": 3.5 * mm});
            skCircle(sketch, "E43.32.0.15", {"center": v(-546.1, -180) * mm, "radius": 3.5 * mm});
            skCircle(sketch, "E43.32.0.16", {"center": v(-546.1, -150) * mm, "radius": 3.5 * mm});
            skCircle(sketch, "E43.32.0.17", {"center": v(-546.1, -90) * mm, "radius": 3.5 * mm});
            skCircle(sketch, "E43.32.0.18", {"center": v(-576.1, -135) * mm, "radius": 3.5 * mm});
            skCircle(sketch, "E43.32.0.19", {"center": v(-576.1, -225) * mm, "radius": 3.5 * mm});
            skCircle(sketch, "E43.32.0.20", {"center": v(-546.1, -210) * mm, "radius": 3.5 * mm});
            skCircle(sketch, "E43.32.0.21", {"center": v(-576.1, -165) * mm, "radius": 3.5 * mm});
            skCircle(sketch, "E43.32.0.22", {"center": v(-546.1, -270) * mm, "radius": 3.5 * mm});
            skCircle(sketch, "E43.32.0.23", {"center": v(-546.1, -330) * mm, "radius": 3.5 * mm});
            skCircle(sketch, "E43.32.0.24", {"center": v(-576.1, -315) * mm, "radius": 3.5 * mm});
            skCircle(sketch, "E43.32.0.25", {"center": v(-576.1, -345) * mm, "radius": 3.5 * mm});
            skCircle(sketch, "E43.32.0.26", {"center": v(-546.1, -360) * mm, "radius": 3.5 * mm});
            skLineSegment(sketch, "E43.direction1", {"start": v(1343.9, -345) * mm, "end": v(1283.9, -345) * mm, "construction": true});
            skLineSegment(sketch, "E44", {"start": v(-576.1, -345) * mm, "end": v(-615.06, -345) * mm, "construction": true});
            skLineSegment(sketch, "E45", {"start": v(1373.9, -330) * mm, "end": v(1412.87, -330) * mm, "construction": true});
            skCircle(sketch, "E46.MirrorC", {"center": v(1343.9, 345) * mm, "radius": 3.5 * mm});
            skLineSegment(sketch, "E47.MirrorCS", {"start": v(1343.9, 345) * mm, "end": v(1283.9, 345) * mm, "construction": true});
            skLineSegment(sketch, "E48.MirrorCS", {"start": v(1373.9, 360) * mm, "end": v(1373.9, 330) * mm, "construction": true});
            skCircle(sketch, "E49.MirrorC", {"center": v(1373.9, 360) * mm, "radius": 3.5 * mm});
            skCircle(sketch, "E50.MirrorC", {"center": v(1373.9, 330) * mm, "radius": 3.5 * mm});
            skCircle(sketch, "E51.MirrorC", {"center": v(-576.1, 345) * mm, "radius": 3.5 * mm});
            skCircle(sketch, "E52.MirrorC", {"center": v(1283.9, 345) * mm, "radius": 3.5 * mm});
            skCircle(sketch, "E53.MirrorC", {"center": v(653.9, 330) * mm, "radius": 3.5 * mm});
            skCircle(sketch, "E54.MirrorC", {"center": v(-546.1, 360) * mm, "radius": 3.5 * mm});
            skCircle(sketch, "E55.MirrorC", {"center": v(23.9, 315) * mm, "radius": 3.5 * mm});
            skCircle(sketch, "E56.MirrorC", {"center": v(203.9, 345) * mm, "radius": 3.5 * mm});
            skLineSegment(sketch, "E57.MirrorCS", {"start": v(1313.9, 360) * mm, "end": v(1313.9, 330) * mm, "construction": true});
            skLineSegment(sketch, "E58.MirrorCS", {"start": v(1343.9, 345) * mm, "end": v(1343.9, 315) * mm, "construction": true});
            skLineSegment(sketch, "E59.MirrorCS", {"start": v(-576.1, 345) * mm, "end": v(-576.1, 315) * mm, "construction": true});
            skCircle(sketch, "E60.MirrorC", {"center": v(1193.9, 360) * mm, "radius": 3.5 * mm});
            skCircle(sketch, "E61.MirrorC", {"center": v(413.9, 360) * mm, "radius": 3.5 * mm});
            skCircle(sketch, "E62.MirrorC", {"center": v(1163.9, 345) * mm, "radius": 3.5 * mm});
            skCircle(sketch, "E63.MirrorC", {"center": v(-486.1, 330) * mm, "radius": 3.5 * mm});
            skCircle(sketch, "E64.MirrorC", {"center": v(-126.1, 330) * mm, "radius": 3.5 * mm});
            skCircle(sketch, "E65.MirrorC", {"center": v(1013.9, 360) * mm, "radius": 3.5 * mm});
            skCircle(sketch, "E66.MirrorC", {"center": v(803.9, 345) * mm, "radius": 3.5 * mm});
            skCircle(sketch, "E67.MirrorC", {"center": v(473.9, 330) * mm, "radius": 3.5 * mm});
            skLineSegment(sketch, "E68.MirrorCS", {"start": v(-426.1, 360) * mm, "end": v(-426.1, 330) * mm, "construction": true});
            skLineSegment(sketch, "E69.MirrorCS", {"start": v(-396.1, 345) * mm, "end": v(-396.1, 315) * mm, "construction": true});
            skCircle(sketch, "E70.MirrorC", {"center": v(623.9, 315) * mm, "radius": 3.5 * mm});
            skCircle(sketch, "E71.MirrorC", {"center": v(983.9, 345) * mm, "radius": 3.5 * mm});
            skCircle(sketch, "E72.MirrorC", {"center": v(593.9, 360) * mm, "radius": 3.5 * mm});
            skLineSegment(sketch, "E73.MirrorCS", {"start": v(743.9, 345) * mm, "end": v(743.9, 315) * mm, "construction": true});
            skLineSegment(sketch, "E74.MirrorCS", {"start": v(713.9, 360) * mm, "end": v(713.9, 330) * mm, "construction": true});
            skLineSegment(sketch, "E75.MirrorCS", {"start": v(173.9, 360) * mm, "end": v(173.9, 330) * mm, "construction": true});
            skCircle(sketch, "E76.MirrorC", {"center": v(1013.9, 330) * mm, "radius": 3.5 * mm});
            skCircle(sketch, "E77.MirrorC", {"center": v(-366.1, 360) * mm, "radius": 3.5 * mm});
            skLineSegment(sketch, "E78.MirrorCS", {"start": v(-216.1, 345) * mm, "end": v(-216.1, 315) * mm, "construction": true});
            skLineSegment(sketch, "E79.MirrorCS", {"start": v(-246.1, 360) * mm, "end": v(-246.1, 330) * mm, "construction": true});
            skCircle(sketch, "E80.MirrorC", {"center": v(53.9, 330) * mm, "radius": 3.5 * mm});
            skCircle(sketch, "E81.MirrorC", {"center": v(1163.9, 315) * mm, "radius": 3.5 * mm});
            skCircle(sketch, "E82.MirrorC", {"center": v(383.9, 315) * mm, "radius": 3.5 * mm});
            skCircle(sketch, "E83.MirrorC", {"center": v(563.9, 345) * mm, "radius": 3.5 * mm});
            skCircle(sketch, "E84.MirrorC", {"center": v(773.9, 360) * mm, "radius": 3.5 * mm});
            skLineSegment(sketch, "E85.MirrorCS", {"start": v(893.9, 360) * mm, "end": v(893.9, 330) * mm, "construction": true});
            skLineSegment(sketch, "E86.MirrorCS", {"start": v(923.9, 345) * mm, "end": v(923.9, 315) * mm, "construction": true});
            skCircle(sketch, "E87.MirrorC", {"center": v(1193.9, 330) * mm, "radius": 3.5 * mm});
            skCircle(sketch, "E88.MirrorC", {"center": v(-396.1, 345) * mm, "radius": 3.5 * mm});
            skCircle(sketch, "E89.MirrorC", {"center": v(-186.1, 360) * mm, "radius": 3.5 * mm});
            skLineSegment(sketch, "E90.MirrorCS", {"start": v(-36.1, 345) * mm, "end": v(-36.1, 315) * mm, "construction": true});
            skLineSegment(sketch, "E91.MirrorCS", {"start": v(-66.1, 360) * mm, "end": v(-66.1, 330) * mm, "construction": true});
            skCircle(sketch, "E92.MirrorC", {"center": v(233.9, 330) * mm, "radius": 3.5 * mm});
            skCircle(sketch, "E93.MirrorC", {"center": v(-576.1, 315) * mm, "radius": 3.5 * mm});
            skLineSegment(sketch, "E94.MirrorCS", {"start": v(203.9, 345) * mm, "end": v(203.9, 315) * mm, "construction": true});
            skCircle(sketch, "E95.MirrorC", {"center": v(563.9, 315) * mm, "radius": 3.5 * mm});
            skCircle(sketch, "E96.MirrorC", {"center": v(743.9, 345) * mm, "radius": 3.5 * mm});
            skCircle(sketch, "E97.MirrorC", {"center": v(953.9, 360) * mm, "radius": 3.5 * mm});
            skCircle(sketch, "E98.MirrorC", {"center": v(623.9, 345) * mm, "radius": 3.5 * mm});
            skLineSegment(sketch, "E99.MirrorCS", {"start": v(1103.9, 345) * mm, "end": v(1103.9, 315) * mm, "construction": true});
            skLineSegment(sketch, "E100.MirrorCS", {"start": v(1073.9, 360) * mm, "end": v(1073.9, 330) * mm, "construction": true});
            skCircle(sketch, "E101.MirrorC", {"center": v(-396.1, 315) * mm, "radius": 3.5 * mm});
            skCircle(sketch, "E102.MirrorC", {"center": v(-216.1, 345) * mm, "radius": 3.5 * mm});
            skCircle(sketch, "E103.MirrorC", {"center": v(-6.1, 360) * mm, "radius": 3.5 * mm});
            skLineSegment(sketch, "E104.MirrorCS", {"start": v(113.9, 360) * mm, "end": v(113.9, 330) * mm, "construction": true});
            skLineSegment(sketch, "E105.MirrorCS", {"start": v(143.9, 345) * mm, "end": v(143.9, 315) * mm, "construction": true});
            skCircle(sketch, "E106.MirrorC", {"center": v(413.9, 330) * mm, "radius": 3.5 * mm});
            skCircle(sketch, "E107.MirrorC", {"center": v(-546.1, 330) * mm, "radius": 3.5 * mm});
            skCircle(sketch, "E108.MirrorC", {"center": v(593.9, 330) * mm, "radius": 3.5 * mm});
            skCircle(sketch, "E109.MirrorC", {"center": v(743.9, 315) * mm, "radius": 3.5 * mm});
            skCircle(sketch, "E110.MirrorC", {"center": v(923.9, 345) * mm, "radius": 3.5 * mm});
            skCircle(sketch, "E111.MirrorC", {"center": v(1133.9, 360) * mm, "radius": 3.5 * mm});
            skLineSegment(sketch, "E112.MirrorCS", {"start": v(1283.9, 345) * mm, "end": v(1283.9, 315) * mm, "construction": true});
            skLineSegment(sketch, "E113.MirrorCS", {"start": v(1253.9, 360) * mm, "end": v(1253.9, 330) * mm, "construction": true});
            skCircle(sketch, "E114.MirrorC", {"center": v(-366.1, 330) * mm, "radius": 3.5 * mm});
            skCircle(sketch, "E115.MirrorC", {"center": v(-216.1, 315) * mm, "radius": 3.5 * mm});
            skCircle(sketch, "E116.MirrorC", {"center": v(-36.1, 345) * mm, "radius": 3.5 * mm});
            skCircle(sketch, "E117.MirrorC", {"center": v(173.9, 360) * mm, "radius": 3.5 * mm});
            skLineSegment(sketch, "E118.MirrorCS", {"start": v(323.9, 345) * mm, "end": v(323.9, 315) * mm, "construction": true});
            skCircle(sketch, "E119.MirrorC", {"center": v(833.9, 360) * mm, "radius": 3.5 * mm});
            skLineSegment(sketch, "E120.MirrorCS", {"start": v(-456.1, 345) * mm, "end": v(-456.1, 315) * mm, "construction": true});
            skCircle(sketch, "E121.MirrorC", {"center": v(-186.1, 330) * mm, "radius": 3.5 * mm});
            skCircle(sketch, "E122.MirrorC", {"center": v(773.9, 330) * mm, "radius": 3.5 * mm});
            skCircle(sketch, "E123.MirrorC", {"center": v(923.9, 315) * mm, "radius": 3.5 * mm});
            skCircle(sketch, "E124.MirrorC", {"center": v(1103.9, 345) * mm, "radius": 3.5 * mm});
            skCircle(sketch, "E125.MirrorC", {"center": v(1313.9, 360) * mm, "radius": 3.5 * mm});
            skCircle(sketch, "E126.MirrorC", {"center": v(-36.1, 315) * mm, "radius": 3.5 * mm});
            skCircle(sketch, "E127.MirrorC", {"center": v(143.9, 345) * mm, "radius": 3.5 * mm});
            skCircle(sketch, "E128.MirrorC", {"center": v(353.9, 360) * mm, "radius": 3.5 * mm});
            skLineSegment(sketch, "E129.MirrorCS", {"start": v(503.9, 345) * mm, "end": v(503.9, 315) * mm, "construction": true});
            skLineSegment(sketch, "E130.MirrorCS", {"start": v(473.9, 360) * mm, "end": v(473.9, 330) * mm, "construction": true});
            skLineSegment(sketch, "E131.MirrorCS", {"start": v(-306.1, 360) * mm, "end": v(-306.1, 330) * mm, "construction": true});
            skLineSegment(sketch, "E132.MirrorCS", {"start": v(-276.1, 345) * mm, "end": v(-276.1, 315) * mm, "construction": true});
            skLineSegment(sketch, "E133.MirrorCS", {"start": v(-486.1, 360) * mm, "end": v(-486.1, 330) * mm, "construction": true});
            skCircle(sketch, "E134.MirrorC", {"center": v(-336.1, 315) * mm, "radius": 3.5 * mm});
            skCircle(sketch, "E135.MirrorC", {"center": v(953.9, 330) * mm, "radius": 3.5 * mm});
            skCircle(sketch, "E136.MirrorC", {"center": v(1103.9, 315) * mm, "radius": 3.5 * mm});
            skCircle(sketch, "E137.MirrorC", {"center": v(-426.1, 360) * mm, "radius": 3.5 * mm});
            skCircle(sketch, "E138.MirrorC", {"center": v(-6.1, 330) * mm, "radius": 3.5 * mm});
            skCircle(sketch, "E139.MirrorC", {"center": v(143.9, 315) * mm, "radius": 3.5 * mm});
            skCircle(sketch, "E140.MirrorC", {"center": v(323.9, 345) * mm, "radius": 3.5 * mm});
            skCircle(sketch, "E141.MirrorC", {"center": v(533.9, 360) * mm, "radius": 3.5 * mm});
            skLineSegment(sketch, "E142.MirrorCS", {"start": v(683.9, 345) * mm, "end": v(683.9, 315) * mm, "construction": true});
            skLineSegment(sketch, "E143.MirrorCS", {"start": v(653.9, 360) * mm, "end": v(653.9, 330) * mm, "construction": true});
            skCircle(sketch, "E144.MirrorC", {"center": v(-246.1, 360) * mm, "radius": 3.5 * mm});
            skLineSegment(sketch, "E145.MirrorCS", {"start": v(-126.1, 360) * mm, "end": v(-126.1, 330) * mm, "construction": true});
            skLineSegment(sketch, "E146.MirrorCS", {"start": v(-96.1, 345) * mm, "end": v(-96.1, 315) * mm, "construction": true});
            skCircle(sketch, "E147.MirrorC", {"center": v(1133.9, 330) * mm, "radius": 3.5 * mm});
            skCircle(sketch, "E148.MirrorC", {"center": v(1283.9, 315) * mm, "radius": 3.5 * mm});
            skCircle(sketch, "E149.MirrorC", {"center": v(-456.1, 345) * mm, "radius": 3.5 * mm});
            skCircle(sketch, "E150.MirrorC", {"center": v(173.9, 330) * mm, "radius": 3.5 * mm});
            skCircle(sketch, "E151.MirrorC", {"center": v(323.9, 315) * mm, "radius": 3.5 * mm});
            skCircle(sketch, "E152.MirrorC", {"center": v(503.9, 345) * mm, "radius": 3.5 * mm});
            skCircle(sketch, "E153.MirrorC", {"center": v(713.9, 360) * mm, "radius": 3.5 * mm});
            skLineSegment(sketch, "E154.MirrorCS", {"start": v(833.9, 360) * mm, "end": v(833.9, 330) * mm, "construction": true});
            skLineSegment(sketch, "E155.MirrorCS", {"start": v(863.9, 345) * mm, "end": v(863.9, 315) * mm, "construction": true});
            skCircle(sketch, "E156.MirrorC", {"center": v(-276.1, 345) * mm, "radius": 3.5 * mm});
            skCircle(sketch, "E157.MirrorC", {"center": v(-66.1, 360) * mm, "radius": 3.5 * mm});
            skLineSegment(sketch, "E158.MirrorCS", {"start": v(53.9, 360) * mm, "end": v(53.9, 330) * mm, "construction": true});
            skLineSegment(sketch, "E159.MirrorCS", {"start": v(83.9, 345) * mm, "end": v(83.9, 315) * mm, "construction": true});
            skCircle(sketch, "E160.MirrorC", {"center": v(1313.9, 330) * mm, "radius": 3.5 * mm});
            skCircle(sketch, "E161.MirrorC", {"center": v(-456.1, 315) * mm, "radius": 3.5 * mm});
            skCircle(sketch, "E162.MirrorC", {"center": v(353.9, 330) * mm, "radius": 3.5 * mm});
            skCircle(sketch, "E163.MirrorC", {"center": v(503.9, 315) * mm, "radius": 3.5 * mm});
            skCircle(sketch, "E164.MirrorC", {"center": v(683.9, 345) * mm, "radius": 3.5 * mm});
            skCircle(sketch, "E165.MirrorC", {"center": v(893.9, 360) * mm, "radius": 3.5 * mm});
            skLineSegment(sketch, "E166.MirrorCS", {"start": v(1043.9, 345) * mm, "end": v(1043.9, 315) * mm, "construction": true});
            skLineSegment(sketch, "E167.MirrorCS", {"start": v(1013.9, 360) * mm, "end": v(1013.9, 330) * mm, "construction": true});
            skCircle(sketch, "E168.MirrorC", {"center": v(-276.1, 315) * mm, "radius": 3.5 * mm});
            skCircle(sketch, "E169.MirrorC", {"center": v(-96.1, 345) * mm, "radius": 3.5 * mm});
            skCircle(sketch, "E170.MirrorC", {"center": v(113.9, 360) * mm, "radius": 3.5 * mm});
            skLineSegment(sketch, "E171.MirrorCS", {"start": v(263.9, 345) * mm, "end": v(263.9, 315) * mm, "construction": true});
            skLineSegment(sketch, "E172.MirrorCS", {"start": v(233.9, 360) * mm, "end": v(233.9, 330) * mm, "construction": true});
            skCircle(sketch, "E173.MirrorC", {"center": v(-426.1, 330) * mm, "radius": 3.5 * mm});
            skCircle(sketch, "E174.MirrorC", {"center": v(533.9, 330) * mm, "radius": 3.5 * mm});
            skCircle(sketch, "E175.MirrorC", {"center": v(683.9, 315) * mm, "radius": 3.5 * mm});
            skCircle(sketch, "E176.MirrorC", {"center": v(863.9, 345) * mm, "radius": 3.5 * mm});
            skCircle(sketch, "E177.MirrorC", {"center": v(1073.9, 360) * mm, "radius": 3.5 * mm});
            skLineSegment(sketch, "E178.MirrorCS", {"start": v(1223.9, 345) * mm, "end": v(1223.9, 315) * mm, "construction": true});
            skLineSegment(sketch, "E179.MirrorCS", {"start": v(293.9, 360) * mm, "end": v(293.9, 330) * mm, "construction": true});
            skLineSegment(sketch, "E180.MirrorCS", {"start": v(1193.9, 360) * mm, "end": v(1193.9, 330) * mm, "construction": true});
            skCircle(sketch, "E181.MirrorC", {"center": v(-156.1, 345) * mm, "radius": 3.5 * mm});
            skCircle(sketch, "E182.MirrorC", {"center": v(-246.1, 330) * mm, "radius": 3.5 * mm});
            skCircle(sketch, "E183.MirrorC", {"center": v(-96.1, 315) * mm, "radius": 3.5 * mm});
            skCircle(sketch, "E184.MirrorC", {"center": v(83.9, 345) * mm, "radius": 3.5 * mm});
            skLineSegment(sketch, "E185.MirrorCS", {"start": v(443.9, 345) * mm, "end": v(443.9, 315) * mm, "construction": true});
            skCircle(sketch, "E186.MirrorC", {"center": v(293.9, 360) * mm, "radius": 3.5 * mm});
            skLineSegment(sketch, "E187.MirrorCS", {"start": v(413.9, 360) * mm, "end": v(413.9, 330) * mm, "construction": true});
            skLineSegment(sketch, "E188.MirrorCS", {"start": v(-516.1, 345) * mm, "end": v(-516.1, 315) * mm, "construction": true});
            skLineSegment(sketch, "E189.MirrorCS", {"start": v(-546.1, 360) * mm, "end": v(-546.1, 330) * mm, "construction": true});
            skCircle(sketch, "E190.MirrorC", {"center": v(713.9, 330) * mm, "radius": 3.5 * mm});
            skCircle(sketch, "E191.MirrorC", {"center": v(863.9, 315) * mm, "radius": 3.5 * mm});
            skCircle(sketch, "E192.MirrorC", {"center": v(53.9, 360) * mm, "radius": 3.5 * mm});
            skCircle(sketch, "E193.MirrorC", {"center": v(1043.9, 345) * mm, "radius": 3.5 * mm});
            skCircle(sketch, "E194.MirrorC", {"center": v(1253.9, 360) * mm, "radius": 3.5 * mm});
            skLineSegment(sketch, "E195.MirrorCS", {"start": v(-366.1, 360) * mm, "end": v(-366.1, 330) * mm, "construction": true});
            skLineSegment(sketch, "E196.MirrorCS", {"start": v(-336.1, 345) * mm, "end": v(-336.1, 315) * mm, "construction": true});
            skCircle(sketch, "E197.MirrorC", {"center": v(-66.1, 330) * mm, "radius": 3.5 * mm});
            skCircle(sketch, "E198.MirrorC", {"center": v(83.9, 315) * mm, "radius": 3.5 * mm});
            skCircle(sketch, "E199.MirrorC", {"center": v(263.9, 345) * mm, "radius": 3.5 * mm});
            skCircle(sketch, "E200.MirrorC", {"center": v(473.9, 360) * mm, "radius": 3.5 * mm});
            skCircle(sketch, "E201.MirrorC", {"center": v(-486.1, 360) * mm, "radius": 3.5 * mm});
            skLineSegment(sketch, "E202.MirrorCS", {"start": v(623.9, 345) * mm, "end": v(623.9, 315) * mm, "construction": true});
            skLineSegment(sketch, "E203.MirrorCS", {"start": v(593.9, 360) * mm, "end": v(593.9, 330) * mm, "construction": true});
            skCircle(sketch, "E204.MirrorC", {"center": v(893.9, 330) * mm, "radius": 3.5 * mm});
            skCircle(sketch, "E205.MirrorC", {"center": v(1043.9, 315) * mm, "radius": 3.5 * mm});
            skCircle(sketch, "E206.MirrorC", {"center": v(1223.9, 345) * mm, "radius": 3.5 * mm});
            skCircle(sketch, "E207.MirrorC", {"center": v(1343.9, 315) * mm, "radius": 3.5 * mm});
            skLineSegment(sketch, "E208.MirrorCS", {"start": v(533.9, 360) * mm, "end": v(533.9, 330) * mm, "construction": true});
            skCircle(sketch, "E209.MirrorC", {"center": v(383.9, 345) * mm, "radius": 3.5 * mm});
            skCircle(sketch, "E210.MirrorC", {"center": v(23.9, 345) * mm, "radius": 3.5 * mm});
            skCircle(sketch, "E211.MirrorC", {"center": v(983.9, 315) * mm, "radius": 3.5 * mm});
            skLineSegment(sketch, "E212.MirrorCS", {"start": v(353.9, 360) * mm, "end": v(353.9, 330) * mm, "construction": true});
            skCircle(sketch, "E213.MirrorC", {"center": v(-156.1, 315) * mm, "radius": 3.5 * mm});
            skCircle(sketch, "E214.MirrorC", {"center": v(-306.1, 330) * mm, "radius": 3.5 * mm});
            skCircle(sketch, "E215.MirrorC", {"center": v(203.9, 315) * mm, "radius": 3.5 * mm});
            skLineSegment(sketch, "E216.MirrorCS", {"start": v(1163.9, 345) * mm, "end": v(1163.9, 315) * mm, "construction": true});
            skCircle(sketch, "E217.MirrorC", {"center": v(-516.1, 315) * mm, "radius": 3.5 * mm});
            skLineSegment(sketch, "E218.MirrorCS", {"start": v(23.9, 345) * mm, "end": v(23.9, 315) * mm, "construction": true});
            skLineSegment(sketch, "E219.MirrorCS", {"start": v(983.9, 345) * mm, "end": v(983.9, 315) * mm, "construction": true});
            skLineSegment(sketch, "E220.MirrorCS", {"start": v(953.9, 360) * mm, "end": v(953.9, 330) * mm, "construction": true});
            skCircle(sketch, "E221.MirrorC", {"center": v(-516.1, 345) * mm, "radius": 3.5 * mm});
            skCircle(sketch, "E222.MirrorC", {"center": v(-336.1, 345) * mm, "radius": 3.5 * mm});
            skCircle(sketch, "E223.MirrorC", {"center": v(653.9, 360) * mm, "radius": 3.5 * mm});
            skCircle(sketch, "E224.MirrorC", {"center": v(263.9, 315) * mm, "radius": 3.5 * mm});
            skCircle(sketch, "E225.MirrorC", {"center": v(443.9, 345) * mm, "radius": 3.5 * mm});
            skLineSegment(sketch, "E226.MirrorCS", {"start": v(-186.1, 360) * mm, "end": v(-186.1, 330) * mm, "construction": true});
            skCircle(sketch, "E227.MirrorC", {"center": v(113.9, 330) * mm, "radius": 3.5 * mm});
            skLineSegment(sketch, "E228.MirrorCS", {"start": v(-156.1, 345) * mm, "end": v(-156.1, 315) * mm, "construction": true});
            skCircle(sketch, "E229.MirrorC", {"center": v(233.9, 360) * mm, "radius": 3.5 * mm});
            skLineSegment(sketch, "E230.MirrorCS", {"start": v(383.9, 345) * mm, "end": v(383.9, 315) * mm, "construction": true});
            skCircle(sketch, "E231.MirrorC", {"center": v(833.9, 330) * mm, "radius": 3.5 * mm});
            skCircle(sketch, "E232.MirrorC", {"center": v(1223.9, 315) * mm, "radius": 3.5 * mm});
            skCircle(sketch, "E233.MirrorC", {"center": v(-126.1, 360) * mm, "radius": 3.5 * mm});
            skCircle(sketch, "E234.MirrorC", {"center": v(803.9, 315) * mm, "radius": 3.5 * mm});
            skLineSegment(sketch, "E235.MirrorCS", {"start": v(773.9, 360) * mm, "end": v(773.9, 330) * mm, "construction": true});
            skLineSegment(sketch, "E236.MirrorCS", {"start": v(803.9, 345) * mm, "end": v(803.9, 315) * mm, "construction": true});
            skCircle(sketch, "E237.MirrorC", {"center": v(1073.9, 330) * mm, "radius": 3.5 * mm});
            skLineSegment(sketch, "E238.MirrorCS", {"start": v(563.9, 345) * mm, "end": v(563.9, 315) * mm, "construction": true});
            skCircle(sketch, "E239.MirrorC", {"center": v(-306.1, 360) * mm, "radius": 3.5 * mm});
            skCircle(sketch, "E240.MirrorC", {"center": v(1253.9, 330) * mm, "radius": 3.5 * mm});
            skCircle(sketch, "E241.MirrorC", {"center": v(443.9, 315) * mm, "radius": 3.5 * mm});
            skLineSegment(sketch, "E242.MirrorCS", {"start": v(1133.9, 360) * mm, "end": v(1133.9, 330) * mm, "construction": true});
            skCircle(sketch, "E243.MirrorC", {"center": v(293.9, 330) * mm, "radius": 3.5 * mm});
            skLineSegment(sketch, "E244.MirrorCS", {"start": v(-6.1, 360) * mm, "end": v(-6.1, 330) * mm, "construction": true});
            skCircle(sketch, "E245.MirrorC", {"center": v(83.9, 165) * mm, "radius": 3.5 * mm});
            skCircle(sketch, "E246.MirrorC", {"center": v(113.9, 240) * mm, "radius": 3.5 * mm});
            skCircle(sketch, "E247.MirrorC", {"center": v(473.9, 270) * mm, "radius": 3.5 * mm});
            skCircle(sketch, "E248.MirrorC", {"center": v(443.9, 75) * mm, "radius": 3.5 * mm});
            skCircle(sketch, "E249.MirrorC", {"center": v(533.9, 90) * mm, "radius": 3.5 * mm});
            skCircle(sketch, "E250.MirrorC", {"center": v(-516.1, 75) * mm, "radius": 3.5 * mm});
            skCircle(sketch, "E251.MirrorC", {"center": v(1253.9, 240) * mm, "radius": 3.5 * mm});
            skCircle(sketch, "E252.MirrorC", {"center": v(-426.1, 60) * mm, "radius": 3.5 * mm});
            skCircle(sketch, "E253.MirrorC", {"center": v(353.9, 150) * mm, "radius": 3.5 * mm});
            skCircle(sketch, "E254.MirrorC", {"center": v(173.9, 180) * mm, "radius": 3.5 * mm});
            skCircle(sketch, "E255.MirrorC", {"center": v(203.9, 105) * mm, "radius": 3.5 * mm});
            skCircle(sketch, "E256.MirrorC", {"center": v(293.9, 240) * mm, "radius": 3.5 * mm});
            skCircle(sketch, "E257.MirrorC", {"center": v(443.9, 165) * mm, "radius": 3.5 * mm});
            skCircle(sketch, "E258.MirrorC", {"center": v(143.9, 45) * mm, "radius": 3.5 * mm});
            skCircle(sketch, "E259.MirrorC", {"center": v(383.9, 255) * mm, "radius": 3.5 * mm});
            skCircle(sketch, "E260.MirrorC", {"center": v(1313.9, 180) * mm, "radius": 3.5 * mm});
            skCircle(sketch, "E261.MirrorC", {"center": v(-156.1, 285) * mm, "radius": 3.5 * mm});
            skCircle(sketch, "E262.MirrorC", {"center": v(-66.1, 30) * mm, "radius": 3.5 * mm});
            skCircle(sketch, "E263.MirrorC", {"center": v(-516.1, 165) * mm, "radius": 3.5 * mm});
            skCircle(sketch, "E264.MirrorC", {"center": v(1133.9, 180) * mm, "radius": 3.5 * mm});
            skCircle(sketch, "E265.MirrorC", {"center": v(923.9, 45) * mm, "radius": 3.5 * mm});
            skCircle(sketch, "E266.MirrorC", {"center": v(-246.1, 60) * mm, "radius": 3.5 * mm});
            skCircle(sketch, "E267.MirrorC", {"center": v(-6.1, 120) * mm, "radius": 3.5 * mm});
            skCircle(sketch, "E268.MirrorC", {"center": v(173.9, 120) * mm, "radius": 3.5 * mm});
            skCircle(sketch, "E269.MirrorC", {"center": v(473.9, 210) * mm, "radius": 3.5 * mm});
            skCircle(sketch, "E270.MirrorC", {"center": v(503.9, 225) * mm, "radius": 3.5 * mm});
            skCircle(sketch, "E271.MirrorC", {"center": v(473.9, 300) * mm, "radius": 3.5 * mm});
            skCircle(sketch, "E272.MirrorC", {"center": v(383.9, 195) * mm, "radius": 3.5 * mm});
            skCircle(sketch, "E273.MirrorC", {"center": v(353.9, 180) * mm, "radius": 3.5 * mm});
            skCircle(sketch, "E274.MirrorC", {"center": v(203.9, 255) * mm, "radius": 3.5 * mm});
            skCircle(sketch, "E275.MirrorC", {"center": v(-426.1, 150) * mm, "radius": 3.5 * mm});
            skCircle(sketch, "E276.MirrorC", {"center": v(1253.9, 210) * mm, "radius": 3.5 * mm});
            skCircle(sketch, "E277.MirrorC", {"center": v(953.9, 120) * mm, "radius": 3.5 * mm});
            skCircle(sketch, "E278.MirrorC", {"center": v(1073.9, 240) * mm, "radius": 3.5 * mm});
            skCircle(sketch, "E279.MirrorC", {"center": v(1163.9, 255) * mm, "radius": 3.5 * mm});
            skCircle(sketch, "E280.MirrorC", {"center": v(1223.9, 165) * mm, "radius": 3.5 * mm});
            skCircle(sketch, "E281.MirrorC", {"center": v(1253.9, 300) * mm, "radius": 3.5 * mm});
            skCircle(sketch, "E282.MirrorC", {"center": v(1313.9, 150) * mm, "radius": 3.5 * mm});
            skCircle(sketch, "E283.MirrorC", {"center": v(-576.1, 195) * mm, "radius": 3.5 * mm});
            skCircle(sketch, "E284.MirrorC", {"center": v(-216.1, 15) * mm, "radius": 3.5 * mm});
            skCircle(sketch, "E285.MirrorC", {"center": v(803.9, 255) * mm, "radius": 3.5 * mm});
            skCircle(sketch, "E286.MirrorC", {"center": v(-246.1, 90) * mm, "radius": 3.5 * mm});
            skCircle(sketch, "E287.MirrorC", {"center": v(383.9, 15) * mm, "radius": 3.5 * mm});
            skCircle(sketch, "E288.MirrorC", {"center": v(443.9, 285) * mm, "radius": 3.5 * mm});
            skCircle(sketch, "E289.MirrorC", {"center": v(293.9, 270) * mm, "radius": 3.5 * mm});
            skCircle(sketch, "E290.MirrorC", {"center": v(-306.1, 270) * mm, "radius": 3.5 * mm});
            skCircle(sketch, "E291.MirrorC", {"center": v(-336.1, 75) * mm, "radius": 3.5 * mm});
            skCircle(sketch, "E292.MirrorC", {"center": v(-486.1, 300) * mm, "radius": 3.5 * mm});
            skCircle(sketch, "E293.MirrorC", {"center": v(-96.1, 135) * mm, "radius": 3.5 * mm});
            skCircle(sketch, "E294.MirrorC", {"center": v(263.9, 75) * mm, "radius": 3.5 * mm});
            skCircle(sketch, "E295.MirrorC", {"center": v(353.9, 90) * mm, "radius": 3.5 * mm});
            skCircle(sketch, "E296.MirrorC", {"center": v(1373.9, 90) * mm, "radius": 3.5 * mm});
            skCircle(sketch, "E297.MirrorC", {"center": v(1373.9, 120) * mm, "radius": 3.5 * mm});
            skCircle(sketch, "E298.MirrorC", {"center": v(1373.9, 150) * mm, "radius": 3.5 * mm});
            skCircle(sketch, "E299.MirrorC", {"center": v(-516.1, 285) * mm, "radius": 3.5 * mm});
            skCircle(sketch, "E300.MirrorC", {"center": v(503.9, 135) * mm, "radius": 3.5 * mm});
            skCircle(sketch, "E301.MirrorC", {"center": v(1373.9, 60) * mm, "radius": 3.5 * mm});
            skCircle(sketch, "E302.MirrorC", {"center": v(1163.9, 195) * mm, "radius": 3.5 * mm});
            skCircle(sketch, "E303.MirrorC", {"center": v(743.9, 45) * mm, "radius": 3.5 * mm});
            skCircle(sketch, "E304.MirrorC", {"center": v(953.9, 180) * mm, "radius": 3.5 * mm});
            skCircle(sketch, "E305.MirrorC", {"center": v(893.9, 240) * mm, "radius": 3.5 * mm});
            skCircle(sketch, "E306.MirrorC", {"center": v(623.9, 105) * mm, "radius": 3.5 * mm});
            skCircle(sketch, "E307.MirrorC", {"center": v(983.9, 195) * mm, "radius": 3.5 * mm});
            skCircle(sketch, "E308.MirrorC", {"center": v(443.9, 105) * mm, "radius": 3.5 * mm});
            skCircle(sketch, "E309.MirrorC", {"center": v(893.9, 210) * mm, "radius": 3.5 * mm});
            skCircle(sketch, "E310.MirrorC", {"center": v(983.9, 255) * mm, "radius": 3.5 * mm});
            skCircle(sketch, "E311.MirrorC", {"center": v(1103.9, 45) * mm, "radius": 3.5 * mm});
            skCircle(sketch, "E312.MirrorC", {"center": v(683.9, 225) * mm, "radius": 3.5 * mm});
            skCircle(sketch, "E313.MirrorC", {"center": v(563.9, 195) * mm, "radius": 3.5 * mm});
            skCircle(sketch, "E314.MirrorC", {"center": v(533.9, 180) * mm, "radius": 3.5 * mm});
            skCircle(sketch, "E315.MirrorC", {"center": v(713.9, 150) * mm, "radius": 3.5 * mm});
            skCircle(sketch, "E316.MirrorC", {"center": v(893.9, 60) * mm, "radius": 3.5 * mm});
            skCircle(sketch, "E317.MirrorC", {"center": v(653.9, 300) * mm, "radius": 3.5 * mm});
            skCircle(sketch, "E318.MirrorC", {"center": v(893.9, 90) * mm, "radius": 3.5 * mm});
            skCircle(sketch, "E319.MirrorC", {"center": v(533.9, 30) * mm, "radius": 3.5 * mm});
            skCircle(sketch, "E320.MirrorC", {"center": v(353.9, 60) * mm, "radius": 3.5 * mm});
            skCircle(sketch, "E321.MirrorC", {"center": v(173.9, 150) * mm, "radius": 3.5 * mm});
            skCircle(sketch, "E322.MirrorC", {"center": v(113.9, 300) * mm, "radius": 3.5 * mm});
            skCircle(sketch, "E323.MirrorC", {"center": v(803.9, 75) * mm, "radius": 3.5 * mm});
            skCircle(sketch, "E324.MirrorC", {"center": v(833.9, 270) * mm, "radius": 3.5 * mm});
            skCircle(sketch, "E325.MirrorC", {"center": v(1043.9, 135) * mm, "radius": 3.5 * mm});
            skCircle(sketch, "E326.MirrorC", {"center": v(983.9, 285) * mm, "radius": 3.5 * mm});
            skCircle(sketch, "E327.MirrorC", {"center": v(923.9, 15) * mm, "radius": 3.5 * mm});
            skCircle(sketch, "E328.MirrorC", {"center": v(-426.1, 180) * mm, "radius": 3.5 * mm});
            skCircle(sketch, "E329.MirrorC", {"center": v(-306.1, 300) * mm, "radius": 3.5 * mm});
            skCircle(sketch, "E330.MirrorC", {"center": v(-336.1, 165) * mm, "radius": 3.5 * mm});
            skCircle(sketch, "E331.MirrorC", {"center": v(-396.1, 195) * mm, "radius": 3.5 * mm});
            skCircle(sketch, "E332.MirrorC", {"center": v(-126.1, 270) * mm, "radius": 3.5 * mm});
            skCircle(sketch, "E333.MirrorC", {"center": v(-246.1, 150) * mm, "radius": 3.5 * mm});
            skCircle(sketch, "E334.MirrorC", {"center": v(-36.1, 15) * mm, "radius": 3.5 * mm});
            skCircle(sketch, "E335.MirrorC", {"center": v(-66.1, 60) * mm, "radius": 3.5 * mm});
            skCircle(sketch, "E336.MirrorC", {"center": v(-66.1, 90) * mm, "radius": 3.5 * mm});
            skCircle(sketch, "E337.MirrorC", {"center": v(-156.1, 75) * mm, "radius": 3.5 * mm});
            skCircle(sketch, "E338.MirrorC", {"center": v(83.9, 135) * mm, "radius": 3.5 * mm});
            skCircle(sketch, "E339.MirrorC", {"center": v(113.9, 30) * mm, "radius": 3.5 * mm});
            skCircle(sketch, "E340.MirrorC", {"center": v(23.9, 285) * mm, "radius": 3.5 * mm});
            skCircle(sketch, "E341.MirrorC", {"center": v(1373.9, 30) * mm, "radius": 3.5 * mm});
            skCircle(sketch, "E342.MirrorC", {"center": v(1373.9, 300) * mm, "radius": 3.5 * mm});
            skCircle(sketch, "E343.MirrorC", {"center": v(1373.9, 270) * mm, "radius": 3.5 * mm});
            skCircle(sketch, "E344.MirrorC", {"center": v(1373.9, 240) * mm, "radius": 3.5 * mm});
            skCircle(sketch, "E345.MirrorC", {"center": v(1373.9, 180) * mm, "radius": 3.5 * mm});
            skCircle(sketch, "E346.MirrorC", {"center": v(1373.9, 210) * mm, "radius": 3.5 * mm});
            skCircle(sketch, "E347.MirrorC", {"center": v(1163.9, 105) * mm, "radius": 3.5 * mm});
            skCircle(sketch, "E348.MirrorC", {"center": v(1133.9, 120) * mm, "radius": 3.5 * mm});
            skCircle(sketch, "E349.MirrorC", {"center": v(713.9, 240) * mm, "radius": 3.5 * mm});
            skCircle(sketch, "E350.MirrorC", {"center": v(1073.9, 30) * mm, "radius": 3.5 * mm});
            skCircle(sketch, "E351.MirrorC", {"center": v(1283.9, 45) * mm, "radius": 3.5 * mm});
            skCircle(sketch, "E352.MirrorC", {"center": v(1343.9, 15) * mm, "radius": 3.5 * mm});
            skCircle(sketch, "E353.MirrorC", {"center": v(1223.9, 225) * mm, "radius": 3.5 * mm});
            skCircle(sketch, "E354.MirrorC", {"center": v(-576.1, 255) * mm, "radius": 3.5 * mm});
            skCircle(sketch, "E355.MirrorC", {"center": v(-486.1, 240) * mm, "radius": 3.5 * mm});
            skCircle(sketch, "E356.MirrorC", {"center": v(-486.1, 210) * mm, "radius": 3.5 * mm});
            skCircle(sketch, "E357.MirrorC", {"center": v(383.9, 105) * mm, "radius": 3.5 * mm});
            skCircle(sketch, "E358.MirrorC", {"center": v(293.9, 30) * mm, "radius": 3.5 * mm});
            skCircle(sketch, "E359.MirrorC", {"center": v(443.9, 225) * mm, "radius": 3.5 * mm});
            skCircle(sketch, "E360.MirrorC", {"center": v(353.9, 120) * mm, "radius": 3.5 * mm});
            skCircle(sketch, "E361.MirrorC", {"center": v(653.9, 210) * mm, "radius": 3.5 * mm});
            skCircle(sketch, "E362.MirrorC", {"center": v(563.9, 255) * mm, "radius": 3.5 * mm});
            skCircle(sketch, "E363.MirrorC", {"center": v(503.9, 45) * mm, "radius": 3.5 * mm});
            skCircle(sketch, "E364.MirrorC", {"center": v(743.9, 195) * mm, "radius": 3.5 * mm});
            skCircle(sketch, "E365.MirrorC", {"center": v(713.9, 180) * mm, "radius": 3.5 * mm});
            skCircle(sketch, "E366.MirrorC", {"center": v(653.9, 240) * mm, "radius": 3.5 * mm});
            skCircle(sketch, "E367.MirrorC", {"center": v(893.9, 150) * mm, "radius": 3.5 * mm});
            skCircle(sketch, "E368.MirrorC", {"center": v(833.9, 300) * mm, "radius": 3.5 * mm});
            skCircle(sketch, "E369.MirrorC", {"center": v(803.9, 165) * mm, "radius": 3.5 * mm});
            skCircle(sketch, "E370.MirrorC", {"center": v(1073.9, 90) * mm, "radius": 3.5 * mm});
            skCircle(sketch, "E371.MirrorC", {"center": v(983.9, 75) * mm, "radius": 3.5 * mm});
            skCircle(sketch, "E372.MirrorC", {"center": v(1013.9, 270) * mm, "radius": 3.5 * mm});
            skCircle(sketch, "E373.MirrorC", {"center": v(1163.9, 285) * mm, "radius": 3.5 * mm});
            skCircle(sketch, "E374.MirrorC", {"center": v(1103.9, 15) * mm, "radius": 3.5 * mm});
            skCircle(sketch, "E375.MirrorC", {"center": v(1073.9, 60) * mm, "radius": 3.5 * mm});
            skCircle(sketch, "E376.MirrorC", {"center": v(-456.1, 45) * mm, "radius": 3.5 * mm});
            skCircle(sketch, "E377.MirrorC", {"center": v(-306.1, 240) * mm, "radius": 3.5 * mm});
            skCircle(sketch, "E378.MirrorC", {"center": v(-306.1, 210) * mm, "radius": 3.5 * mm});
            skCircle(sketch, "E379.MirrorC", {"center": v(-396.1, 255) * mm, "radius": 3.5 * mm});
            skCircle(sketch, "E380.MirrorC", {"center": v(-216.1, 195) * mm, "radius": 3.5 * mm});
            skCircle(sketch, "E381.MirrorC", {"center": v(-156.1, 165) * mm, "radius": 3.5 * mm});
            skCircle(sketch, "E382.MirrorC", {"center": v(-246.1, 180) * mm, "radius": 3.5 * mm});
            skCircle(sketch, "E383.MirrorC", {"center": v(-66.1, 150) * mm, "radius": 3.5 * mm});
            skCircle(sketch, "E384.MirrorC", {"center": v(113.9, 60) * mm, "radius": 3.5 * mm});
            skCircle(sketch, "E385.MirrorC", {"center": v(-126.1, 300) * mm, "radius": 3.5 * mm});
            skCircle(sketch, "E386.MirrorC", {"center": v(23.9, 75) * mm, "radius": 3.5 * mm});
            skCircle(sketch, "E387.MirrorC", {"center": v(113.9, 90) * mm, "radius": 3.5 * mm});
            skCircle(sketch, "E388.MirrorC", {"center": v(53.9, 270) * mm, "radius": 3.5 * mm});
            skCircle(sketch, "E389.MirrorC", {"center": v(713.9, 210) * mm, "radius": 3.5 * mm});
            skCircle(sketch, "E390.MirrorC", {"center": v(263.9, 135) * mm, "radius": 3.5 * mm});
            skCircle(sketch, "E391.MirrorC", {"center": v(203.9, 285) * mm, "radius": 3.5 * mm});
            skCircle(sketch, "E392.MirrorC", {"center": v(143.9, 15) * mm, "radius": 3.5 * mm});
            skCircle(sketch, "E393.MirrorC", {"center": v(1343.9, 45) * mm, "radius": 3.5 * mm});
            skCircle(sketch, "E394.MirrorC", {"center": v(1313.9, 120) * mm, "radius": 3.5 * mm});
            skCircle(sketch, "E395.MirrorC", {"center": v(1253.9, 30) * mm, "radius": 3.5 * mm});
            skCircle(sketch, "E396.MirrorC", {"center": v(623.9, 255) * mm, "radius": 3.5 * mm});
            skCircle(sketch, "E397.MirrorC", {"center": v(1223.9, 135) * mm, "radius": 3.5 * mm});
            skCircle(sketch, "E398.MirrorC", {"center": v(-576.1, 105) * mm, "radius": 3.5 * mm});
            skCircle(sketch, "E399.MirrorC", {"center": v(-516.1, 225) * mm, "radius": 3.5 * mm});
            skCircle(sketch, "E400.MirrorC", {"center": v(443.9, 135) * mm, "radius": 3.5 * mm});
            skCircle(sketch, "E401.MirrorC", {"center": v(473.9, 30) * mm, "radius": 3.5 * mm});
            skCircle(sketch, "E402.MirrorC", {"center": v(623.9, 225) * mm, "radius": 3.5 * mm});
            skCircle(sketch, "E403.MirrorC", {"center": v(563.9, 105) * mm, "radius": 3.5 * mm});
            skCircle(sketch, "E404.MirrorC", {"center": v(533.9, 120) * mm, "radius": 3.5 * mm});
            skCircle(sketch, "E405.MirrorC", {"center": v(743.9, 255) * mm, "radius": 3.5 * mm});
            skCircle(sketch, "E406.MirrorC", {"center": v(683.9, 45) * mm, "radius": 3.5 * mm});
            skCircle(sketch, "E407.MirrorC", {"center": v(893.9, 180) * mm, "radius": 3.5 * mm});
            skCircle(sketch, "E408.MirrorC", {"center": v(833.9, 240) * mm, "radius": 3.5 * mm});
            skCircle(sketch, "E409.MirrorC", {"center": v(1073.9, 150) * mm, "radius": 3.5 * mm});
            skCircle(sketch, "E410.MirrorC", {"center": v(833.9, 210) * mm, "radius": 3.5 * mm});
            skCircle(sketch, "E411.MirrorC", {"center": v(1013.9, 300) * mm, "radius": 3.5 * mm});
            skCircle(sketch, "E412.MirrorC", {"center": v(983.9, 165) * mm, "radius": 3.5 * mm});
            skCircle(sketch, "E413.MirrorC", {"center": v(923.9, 195) * mm, "radius": 3.5 * mm});
            skCircle(sketch, "E414.MirrorC", {"center": v(1193.9, 270) * mm, "radius": 3.5 * mm});
            skCircle(sketch, "E415.MirrorC", {"center": v(1163.9, 75) * mm, "radius": 3.5 * mm});
            skCircle(sketch, "E416.MirrorC", {"center": v(1343.9, 75) * mm, "radius": 3.5 * mm});
            skCircle(sketch, "E417.MirrorC", {"center": v(1253.9, 60) * mm, "radius": 3.5 * mm});
            skCircle(sketch, "E418.MirrorC", {"center": v(1283.9, 15) * mm, "radius": 3.5 * mm});
            skCircle(sketch, "E419.MirrorC", {"center": v(1253.9, 90) * mm, "radius": 3.5 * mm});
            skCircle(sketch, "E420.MirrorC", {"center": v(-336.1, 225) * mm, "radius": 3.5 * mm});
            skCircle(sketch, "E421.MirrorC", {"center": v(-426.1, 120) * mm, "radius": 3.5 * mm});
            skCircle(sketch, "E422.MirrorC", {"center": v(-396.1, 105) * mm, "radius": 3.5 * mm});
            skCircle(sketch, "E423.MirrorC", {"center": v(-126.1, 210) * mm, "radius": 3.5 * mm});
            skCircle(sketch, "E424.MirrorC", {"center": v(-216.1, 255) * mm, "radius": 3.5 * mm});
            skCircle(sketch, "E425.MirrorC", {"center": v(-276.1, 45) * mm, "radius": 3.5 * mm});
            skCircle(sketch, "E426.MirrorC", {"center": v(-36.1, 195) * mm, "radius": 3.5 * mm});
            skCircle(sketch, "E427.MirrorC", {"center": v(-66.1, 180) * mm, "radius": 3.5 * mm});
            skCircle(sketch, "E428.MirrorC", {"center": v(-126.1, 240) * mm, "radius": 3.5 * mm});
            skCircle(sketch, "E429.MirrorC", {"center": v(113.9, 150) * mm, "radius": 3.5 * mm});
            skCircle(sketch, "E430.MirrorC", {"center": v(53.9, 300) * mm, "radius": 3.5 * mm});
            skCircle(sketch, "E431.MirrorC", {"center": v(23.9, 165) * mm, "radius": 3.5 * mm});
            skCircle(sketch, "E432.MirrorC", {"center": v(293.9, 90) * mm, "radius": 3.5 * mm});
            skCircle(sketch, "E433.MirrorC", {"center": v(203.9, 75) * mm, "radius": 3.5 * mm});
            skCircle(sketch, "E434.MirrorC", {"center": v(233.9, 270) * mm, "radius": 3.5 * mm});
            skCircle(sketch, "E435.MirrorC", {"center": v(383.9, 285) * mm, "radius": 3.5 * mm});
            skCircle(sketch, "E436.MirrorC", {"center": v(323.9, 15) * mm, "radius": 3.5 * mm});
            skCircle(sketch, "E437.MirrorC", {"center": v(293.9, 60) * mm, "radius": 3.5 * mm});
            skCircle(sketch, "E438.MirrorC", {"center": v(863.9, 165) * mm, "radius": 3.5 * mm});
            skCircle(sketch, "E439.MirrorC", {"center": v(-576.1, 285) * mm, "radius": 3.5 * mm});
            skCircle(sketch, "E440.MirrorC", {"center": v(-486.1, 30) * mm, "radius": 3.5 * mm});
            skCircle(sketch, "E441.MirrorC", {"center": v(-516.1, 135) * mm, "radius": 3.5 * mm});
            skCircle(sketch, "E442.MirrorC", {"center": v(473.9, 60) * mm, "radius": 3.5 * mm});
            skCircle(sketch, "E443.MirrorC", {"center": v(623.9, 135) * mm, "radius": 3.5 * mm});
            skCircle(sketch, "E444.MirrorC", {"center": v(563.9, 285) * mm, "radius": 3.5 * mm});
            skCircle(sketch, "E445.MirrorC", {"center": v(743.9, 105) * mm, "radius": 3.5 * mm});
            skCircle(sketch, "E446.MirrorC", {"center": v(503.9, 15) * mm, "radius": 3.5 * mm});
            skCircle(sketch, "E447.MirrorC", {"center": v(713.9, 120) * mm, "radius": 3.5 * mm});
            skCircle(sketch, "E448.MirrorC", {"center": v(653.9, 30) * mm, "radius": 3.5 * mm});
            skCircle(sketch, "E449.MirrorC", {"center": v(863.9, 45) * mm, "radius": 3.5 * mm});
            skCircle(sketch, "E450.MirrorC", {"center": v(803.9, 225) * mm, "radius": 3.5 * mm});
            skCircle(sketch, "E451.MirrorC", {"center": v(1013.9, 240) * mm, "radius": 3.5 * mm});
            skCircle(sketch, "E452.MirrorC", {"center": v(1073.9, 180) * mm, "radius": 3.5 * mm});
            skCircle(sketch, "E453.MirrorC", {"center": v(1013.9, 210) * mm, "radius": 3.5 * mm});
            skCircle(sketch, "E454.MirrorC", {"center": v(923.9, 255) * mm, "radius": 3.5 * mm});
            skCircle(sketch, "E455.MirrorC", {"center": v(1163.9, 165) * mm, "radius": 3.5 * mm});
            skCircle(sketch, "E456.MirrorC", {"center": v(1193.9, 300) * mm, "radius": 3.5 * mm});
            skCircle(sketch, "E457.MirrorC", {"center": v(1103.9, 195) * mm, "radius": 3.5 * mm});
            skCircle(sketch, "E458.MirrorC", {"center": v(1343.9, 105) * mm, "radius": 3.5 * mm});
            skCircle(sketch, "E459.MirrorC", {"center": v(1253.9, 150) * mm, "radius": 3.5 * mm});
            skCircle(sketch, "E460.MirrorC", {"center": v(-456.1, 15) * mm, "radius": 3.5 * mm});
            skCircle(sketch, "E461.MirrorC", {"center": v(-336.1, 135) * mm, "radius": 3.5 * mm});
            skCircle(sketch, "E462.MirrorC", {"center": v(803.9, 195) * mm, "radius": 3.5 * mm});
            skCircle(sketch, "E463.MirrorC", {"center": v(-396.1, 285) * mm, "radius": 3.5 * mm});
            skCircle(sketch, "E464.MirrorC", {"center": v(-306.1, 30) * mm, "radius": 3.5 * mm});
            skCircle(sketch, "E465.MirrorC", {"center": v(-156.1, 225) * mm, "radius": 3.5 * mm});
            skCircle(sketch, "E466.MirrorC", {"center": v(-216.1, 105) * mm, "radius": 3.5 * mm});
            skCircle(sketch, "E467.MirrorC", {"center": v(-246.1, 120) * mm, "radius": 3.5 * mm});
            skCircle(sketch, "E468.MirrorC", {"center": v(-96.1, 45) * mm, "radius": 3.5 * mm});
            skCircle(sketch, "E469.MirrorC", {"center": v(-36.1, 255) * mm, "radius": 3.5 * mm});
            skCircle(sketch, "E470.MirrorC", {"center": v(113.9, 180) * mm, "radius": 3.5 * mm});
            skCircle(sketch, "E471.MirrorC", {"center": v(53.9, 240) * mm, "radius": 3.5 * mm});
            skCircle(sketch, "E472.MirrorC", {"center": v(53.9, 210) * mm, "radius": 3.5 * mm});
            skCircle(sketch, "E473.MirrorC", {"center": v(293.9, 150) * mm, "radius": 3.5 * mm});
            skCircle(sketch, "E474.MirrorC", {"center": v(233.9, 300) * mm, "radius": 3.5 * mm});
            skCircle(sketch, "E475.MirrorC", {"center": v(143.9, 195) * mm, "radius": 3.5 * mm});
            skCircle(sketch, "E476.MirrorC", {"center": v(383.9, 75) * mm, "radius": 3.5 * mm});
            skCircle(sketch, "E477.MirrorC", {"center": v(203.9, 165) * mm, "radius": 3.5 * mm});
            skCircle(sketch, "E478.MirrorC", {"center": v(413.9, 270) * mm, "radius": 3.5 * mm});
            skCircle(sketch, "E479.MirrorC", {"center": v(473.9, 90) * mm, "radius": 3.5 * mm});
            skCircle(sketch, "E480.MirrorC", {"center": v(-576.1, 75) * mm, "radius": 3.5 * mm});
            skCircle(sketch, "E481.MirrorC", {"center": v(-546.1, 270) * mm, "radius": 3.5 * mm});
            skCircle(sketch, "E482.MirrorC", {"center": v(-486.1, 60) * mm, "radius": 3.5 * mm});
            skCircle(sketch, "E483.MirrorC", {"center": v(-486.1, 90) * mm, "radius": 3.5 * mm});
            skCircle(sketch, "E484.MirrorC", {"center": v(-396.1, 75) * mm, "radius": 3.5 * mm});
            skCircle(sketch, "E485.MirrorC", {"center": v(-366.1, 270) * mm, "radius": 3.5 * mm});
            skCircle(sketch, "E486.MirrorC", {"center": v(-276.1, 15) * mm, "radius": 3.5 * mm});
            skCircle(sketch, "E487.MirrorC", {"center": v(-306.1, 60) * mm, "radius": 3.5 * mm});
            skCircle(sketch, "E488.MirrorC", {"center": v(833.9, 30) * mm, "radius": 3.5 * mm});
            skCircle(sketch, "E489.MirrorC", {"center": v(-306.1, 90) * mm, "radius": 3.5 * mm});
            skCircle(sketch, "E490.MirrorC", {"center": v(803.9, 135) * mm, "radius": 3.5 * mm});
            skCircle(sketch, "E491.MirrorC", {"center": v(743.9, 285) * mm, "radius": 3.5 * mm});
            skCircle(sketch, "E492.MirrorC", {"center": v(983.9, 225) * mm, "radius": 3.5 * mm});
            skCircle(sketch, "E493.MirrorC", {"center": v(923.9, 105) * mm, "radius": 3.5 * mm});
            skCircle(sketch, "E494.MirrorC", {"center": v(893.9, 120) * mm, "radius": 3.5 * mm});
            skCircle(sketch, "E495.MirrorC", {"center": v(1103.9, 255) * mm, "radius": 3.5 * mm});
            skCircle(sketch, "E496.MirrorC", {"center": v(773.9, 180) * mm, "radius": 3.5 * mm});
            skCircle(sketch, "E497.MirrorC", {"center": v(1043.9, 45) * mm, "radius": 3.5 * mm});
            skCircle(sketch, "E498.MirrorC", {"center": v(1253.9, 180) * mm, "radius": 3.5 * mm});
            skCircle(sketch, "E499.MirrorC", {"center": v(1193.9, 240) * mm, "radius": 3.5 * mm});
            skCircle(sketch, "E500.MirrorC", {"center": v(1193.9, 210) * mm, "radius": 3.5 * mm});
            skCircle(sketch, "E501.MirrorC", {"center": v(1343.9, 135) * mm, "radius": 3.5 * mm});
            skCircle(sketch, "E502.MirrorC", {"center": v(1283.9, 195) * mm, "radius": 3.5 * mm});
            skCircle(sketch, "E503.MirrorC", {"center": v(-66.1, 120) * mm, "radius": 3.5 * mm});
            skCircle(sketch, "E504.MirrorC", {"center": v(-126.1, 30) * mm, "radius": 3.5 * mm});
            skCircle(sketch, "E505.MirrorC", {"center": v(-156.1, 135) * mm, "radius": 3.5 * mm});
            skCircle(sketch, "E506.MirrorC", {"center": v(-216.1, 285) * mm, "radius": 3.5 * mm});
            skCircle(sketch, "E507.MirrorC", {"center": v(23.9, 225) * mm, "radius": 3.5 * mm});
            skCircle(sketch, "E508.MirrorC", {"center": v(233.9, 210) * mm, "radius": 3.5 * mm});
            skCircle(sketch, "E509.MirrorC", {"center": v(-36.1, 105) * mm, "radius": 3.5 * mm});
            skCircle(sketch, "E510.MirrorC", {"center": v(143.9, 255) * mm, "radius": 3.5 * mm});
            skCircle(sketch, "E511.MirrorC", {"center": v(323.9, 195) * mm, "radius": 3.5 * mm});
            skCircle(sketch, "E512.MirrorC", {"center": v(83.9, 45) * mm, "radius": 3.5 * mm});
            skCircle(sketch, "E513.MirrorC", {"center": v(293.9, 180) * mm, "radius": 3.5 * mm});
            skCircle(sketch, "E514.MirrorC", {"center": v(233.9, 240) * mm, "radius": 3.5 * mm});
            skCircle(sketch, "E515.MirrorC", {"center": v(473.9, 150) * mm, "radius": 3.5 * mm});
            skCircle(sketch, "E516.MirrorC", {"center": v(413.9, 300) * mm, "radius": 3.5 * mm});
            skCircle(sketch, "E517.MirrorC", {"center": v(383.9, 165) * mm, "radius": 3.5 * mm});
            skCircle(sketch, "E518.MirrorC", {"center": v(593.9, 270) * mm, "radius": 3.5 * mm});
            skCircle(sketch, "E519.MirrorC", {"center": v(683.9, 15) * mm, "radius": 3.5 * mm});
            skCircle(sketch, "E520.MirrorC", {"center": v(653.9, 60) * mm, "radius": 3.5 * mm});
            skCircle(sketch, "E521.MirrorC", {"center": v(653.9, 90) * mm, "radius": 3.5 * mm});
            skCircle(sketch, "E522.MirrorC", {"center": v(563.9, 75) * mm, "radius": 3.5 * mm});
            skCircle(sketch, "E523.MirrorC", {"center": v(-396.1, 165) * mm, "radius": 3.5 * mm});
            skCircle(sketch, "E524.MirrorC", {"center": v(-366.1, 300) * mm, "radius": 3.5 * mm});
            skCircle(sketch, "E525.MirrorC", {"center": v(-456.1, 195) * mm, "radius": 3.5 * mm});
            skCircle(sketch, "E526.MirrorC", {"center": v(-186.1, 270) * mm, "radius": 3.5 * mm});
            skCircle(sketch, "E527.MirrorC", {"center": v(-306.1, 150) * mm, "radius": 3.5 * mm});
            skCircle(sketch, "E528.MirrorC", {"center": v(-96.1, 15) * mm, "radius": 3.5 * mm});
            skCircle(sketch, "E529.MirrorC", {"center": v(-126.1, 60) * mm, "radius": 3.5 * mm});
            skCircle(sketch, "E530.MirrorC", {"center": v(-126.1, 90) * mm, "radius": 3.5 * mm});
            skCircle(sketch, "E531.MirrorC", {"center": v(-216.1, 75) * mm, "radius": 3.5 * mm});
            skCircle(sketch, "E532.MirrorC", {"center": v(-486.1, 150) * mm, "radius": 3.5 * mm});
            skCircle(sketch, "E533.MirrorC", {"center": v(-546.1, 300) * mm, "radius": 3.5 * mm});
            skCircle(sketch, "E534.MirrorC", {"center": v(-576.1, 15) * mm, "radius": 3.5 * mm});
            skCircle(sketch, "E535.MirrorC", {"center": v(-576.1, 165) * mm, "radius": 3.5 * mm});
            skCircle(sketch, "E536.MirrorC", {"center": v(983.9, 135) * mm, "radius": 3.5 * mm});
            skCircle(sketch, "E537.MirrorC", {"center": v(923.9, 285) * mm, "radius": 3.5 * mm});
            skCircle(sketch, "E538.MirrorC", {"center": v(863.9, 15) * mm, "radius": 3.5 * mm});
            skCircle(sketch, "E539.MirrorC", {"center": v(1103.9, 105) * mm, "radius": 3.5 * mm});
            skCircle(sketch, "E540.MirrorC", {"center": v(1073.9, 120) * mm, "radius": 3.5 * mm});
            skCircle(sketch, "E541.MirrorC", {"center": v(1013.9, 30) * mm, "radius": 3.5 * mm});
            skCircle(sketch, "E542.MirrorC", {"center": v(1223.9, 45) * mm, "radius": 3.5 * mm});
            skCircle(sketch, "E543.MirrorC", {"center": v(1163.9, 225) * mm, "radius": 3.5 * mm});
            skCircle(sketch, "E544.MirrorC", {"center": v(1343.9, 165) * mm, "radius": 3.5 * mm});
            skCircle(sketch, "E545.MirrorC", {"center": v(1283.9, 255) * mm, "radius": 3.5 * mm});
            skCircle(sketch, "E546.MirrorC", {"center": v(-366.1, 120) * mm, "radius": 3.5 * mm});
            skCircle(sketch, "E547.MirrorC", {"center": v(-486.1, 180) * mm, "radius": 3.5 * mm});
            skCircle(sketch, "E548.MirrorC", {"center": v(-546.1, 240) * mm, "radius": 3.5 * mm});
            skCircle(sketch, "E549.MirrorC", {"center": v(-546.1, 210) * mm, "radius": 3.5 * mm});
            skCircle(sketch, "E550.MirrorC", {"center": v(53.9, 30) * mm, "radius": 3.5 * mm});
            skCircle(sketch, "E551.MirrorC", {"center": v(23.9, 135) * mm, "radius": 3.5 * mm});
            skCircle(sketch, "E552.MirrorC", {"center": v(-426.1, 30) * mm, "radius": 3.5 * mm});
            skCircle(sketch, "E553.MirrorC", {"center": v(-36.1, 285) * mm, "radius": 3.5 * mm});
            skCircle(sketch, "E554.MirrorC", {"center": v(203.9, 225) * mm, "radius": 3.5 * mm});
            skCircle(sketch, "E555.MirrorC", {"center": v(143.9, 105) * mm, "radius": 3.5 * mm});
            skCircle(sketch, "E556.MirrorC", {"center": v(113.9, 120) * mm, "radius": 3.5 * mm});
            skCircle(sketch, "E557.MirrorC", {"center": v(323.9, 255) * mm, "radius": 3.5 * mm});
            skCircle(sketch, "E558.MirrorC", {"center": v(263.9, 45) * mm, "radius": 3.5 * mm});
            skCircle(sketch, "E559.MirrorC", {"center": v(473.9, 180) * mm, "radius": 3.5 * mm});
            skCircle(sketch, "E560.MirrorC", {"center": v(413.9, 240) * mm, "radius": 3.5 * mm});
            skCircle(sketch, "E561.MirrorC", {"center": v(413.9, 210) * mm, "radius": 3.5 * mm});
            skCircle(sketch, "E562.MirrorC", {"center": v(563.9, 165) * mm, "radius": 3.5 * mm});
            skCircle(sketch, "E563.MirrorC", {"center": v(503.9, 195) * mm, "radius": 3.5 * mm});
            skCircle(sketch, "E564.MirrorC", {"center": v(653.9, 150) * mm, "radius": 3.5 * mm});
            skCircle(sketch, "E565.MirrorC", {"center": v(593.9, 300) * mm, "radius": 3.5 * mm});
            skCircle(sketch, "E566.MirrorC", {"center": v(833.9, 60) * mm, "radius": 3.5 * mm});
            skCircle(sketch, "E567.MirrorC", {"center": v(833.9, 90) * mm, "radius": 3.5 * mm});
            skCircle(sketch, "E568.MirrorC", {"center": v(743.9, 75) * mm, "radius": 3.5 * mm});
            skCircle(sketch, "E569.MirrorC", {"center": v(773.9, 270) * mm, "radius": 3.5 * mm});
            skCircle(sketch, "E570.MirrorC", {"center": v(-366.1, 210) * mm, "radius": 3.5 * mm});
            skCircle(sketch, "E571.MirrorC", {"center": v(-366.1, 240) * mm, "radius": 3.5 * mm});
            skCircle(sketch, "E572.MirrorC", {"center": v(-456.1, 255) * mm, "radius": 3.5 * mm});
            skCircle(sketch, "E573.MirrorC", {"center": v(-216.1, 165) * mm, "radius": 3.5 * mm});
            skCircle(sketch, "E574.MirrorC", {"center": v(-276.1, 195) * mm, "radius": 3.5 * mm});
            skCircle(sketch, "E575.MirrorC", {"center": v(-306.1, 180) * mm, "radius": 3.5 * mm});
            skCircle(sketch, "E576.MirrorC", {"center": v(-186.1, 300) * mm, "radius": 3.5 * mm});
            skCircle(sketch, "E577.MirrorC", {"center": v(-126.1, 150) * mm, "radius": 3.5 * mm});
            skCircle(sketch, "E578.MirrorC", {"center": v(-36.1, 75) * mm, "radius": 3.5 * mm});
            skCircle(sketch, "E579.MirrorC", {"center": v(53.9, 60) * mm, "radius": 3.5 * mm});
            skCircle(sketch, "E580.MirrorC", {"center": v(53.9, 90) * mm, "radius": 3.5 * mm});
            skCircle(sketch, "E581.MirrorC", {"center": v(-6.1, 270) * mm, "radius": 3.5 * mm});
            skCircle(sketch, "E582.MirrorC", {"center": v(1103.9, 285) * mm, "radius": 3.5 * mm});
            skCircle(sketch, "E583.MirrorC", {"center": v(1043.9, 15) * mm, "radius": 3.5 * mm});
            skCircle(sketch, "E584.MirrorC", {"center": v(1013.9, 60) * mm, "radius": 3.5 * mm});
            skCircle(sketch, "E585.MirrorC", {"center": v(-456.1, 135) * mm, "radius": 3.5 * mm});
            skCircle(sketch, "E586.MirrorC", {"center": v(1253.9, 120) * mm, "radius": 3.5 * mm});
            skCircle(sketch, "E587.MirrorC", {"center": v(1193.9, 30) * mm, "radius": 3.5 * mm});
            skCircle(sketch, "E588.MirrorC", {"center": v(1163.9, 135) * mm, "radius": 3.5 * mm});
            skCircle(sketch, "E589.MirrorC", {"center": v(1343.9, 195) * mm, "radius": 3.5 * mm});
            skCircle(sketch, "E590.MirrorC", {"center": v(1283.9, 105) * mm, "radius": 3.5 * mm});
            skCircle(sketch, "E591.MirrorC", {"center": v(-216.1, 45) * mm, "radius": 3.5 * mm});
            skCircle(sketch, "E592.MirrorC", {"center": v(-516.1, 45) * mm, "radius": 3.5 * mm});
            skCircle(sketch, "E593.MirrorC", {"center": v(-576.1, 225) * mm, "radius": 3.5 * mm});
            skCircle(sketch, "E594.MirrorC", {"center": v(203.9, 135) * mm, "radius": 3.5 * mm});
            skCircle(sketch, "E595.MirrorC", {"center": v(143.9, 285) * mm, "radius": 3.5 * mm});
            skCircle(sketch, "E596.MirrorC", {"center": v(83.9, 15) * mm, "radius": 3.5 * mm});
            skCircle(sketch, "E597.MirrorC", {"center": v(323.9, 105) * mm, "radius": 3.5 * mm});
            skCircle(sketch, "E598.MirrorC", {"center": v(293.9, 120) * mm, "radius": 3.5 * mm});
            skCircle(sketch, "E599.MirrorC", {"center": v(443.9, 45) * mm, "radius": 3.5 * mm});
            skCircle(sketch, "E600.MirrorC", {"center": v(233.9, 30) * mm, "radius": 3.5 * mm});
            skCircle(sketch, "E601.MirrorC", {"center": v(383.9, 225) * mm, "radius": 3.5 * mm});
            skCircle(sketch, "E602.MirrorC", {"center": v(593.9, 210) * mm, "radius": 3.5 * mm});
            skCircle(sketch, "E603.MirrorC", {"center": v(503.9, 255) * mm, "radius": 3.5 * mm});
            skCircle(sketch, "E604.MirrorC", {"center": v(683.9, 195) * mm, "radius": 3.5 * mm});
            skCircle(sketch, "E605.MirrorC", {"center": v(653.9, 180) * mm, "radius": 3.5 * mm});
            skCircle(sketch, "E606.MirrorC", {"center": v(593.9, 240) * mm, "radius": 3.5 * mm});
            skCircle(sketch, "E607.MirrorC", {"center": v(833.9, 150) * mm, "radius": 3.5 * mm});
            skCircle(sketch, "E608.MirrorC", {"center": v(773.9, 300) * mm, "radius": 3.5 * mm});
            skCircle(sketch, "E609.MirrorC", {"center": v(743.9, 165) * mm, "radius": 3.5 * mm});
            skCircle(sketch, "E610.MirrorC", {"center": v(1013.9, 90) * mm, "radius": 3.5 * mm});
            skCircle(sketch, "E611.MirrorC", {"center": v(923.9, 75) * mm, "radius": 3.5 * mm});
            skCircle(sketch, "E612.MirrorC", {"center": v(953.9, 270) * mm, "radius": 3.5 * mm});
            skCircle(sketch, "E613.MirrorC", {"center": v(-456.1, 105) * mm, "radius": 3.5 * mm});
            skCircle(sketch, "E614.MirrorC", {"center": v(-396.1, 225) * mm, "radius": 3.5 * mm});
            skCircle(sketch, "E615.MirrorC", {"center": v(-276.1, 255) * mm, "radius": 3.5 * mm});
            skCircle(sketch, "E616.MirrorC", {"center": v(-186.1, 210) * mm, "radius": 3.5 * mm});
            skCircle(sketch, "E617.MirrorC", {"center": v(-336.1, 45) * mm, "radius": 3.5 * mm});
            skCircle(sketch, "E618.MirrorC", {"center": v(-96.1, 195) * mm, "radius": 3.5 * mm});
            skCircle(sketch, "E619.MirrorC", {"center": v(-126.1, 180) * mm, "radius": 3.5 * mm});
            skCircle(sketch, "E620.MirrorC", {"center": v(-186.1, 240) * mm, "radius": 3.5 * mm});
            skCircle(sketch, "E621.MirrorC", {"center": v(53.9, 150) * mm, "radius": 3.5 * mm});
            skCircle(sketch, "E622.MirrorC", {"center": v(-6.1, 300) * mm, "radius": 3.5 * mm});
            skCircle(sketch, "E623.MirrorC", {"center": v(-36.1, 165) * mm, "radius": 3.5 * mm});
            skCircle(sketch, "E624.MirrorC", {"center": v(233.9, 90) * mm, "radius": 3.5 * mm});
            skCircle(sketch, "E625.MirrorC", {"center": v(143.9, 75) * mm, "radius": 3.5 * mm});
            skCircle(sketch, "E626.MirrorC", {"center": v(173.9, 270) * mm, "radius": 3.5 * mm});
            skCircle(sketch, "E627.MirrorC", {"center": v(-276.1, 225) * mm, "radius": 3.5 * mm});
            skCircle(sketch, "E628.MirrorC", {"center": v(1223.9, 15) * mm, "radius": 3.5 * mm});
            skCircle(sketch, "E629.MirrorC", {"center": v(1193.9, 60) * mm, "radius": 3.5 * mm});
            skCircle(sketch, "E630.MirrorC", {"center": v(1193.9, 90) * mm, "radius": 3.5 * mm});
            skCircle(sketch, "E631.MirrorC", {"center": v(1343.9, 225) * mm, "radius": 3.5 * mm});
            skCircle(sketch, "E632.MirrorC", {"center": v(1283.9, 285) * mm, "radius": 3.5 * mm});
            skCircle(sketch, "E633.MirrorC", {"center": v(-336.1, 105) * mm, "radius": 3.5 * mm});
            skCircle(sketch, "E634.MirrorC", {"center": v(-486.1, 120) * mm, "radius": 3.5 * mm});
            skCircle(sketch, "E635.MirrorC", {"center": v(-546.1, 30) * mm, "radius": 3.5 * mm});
            skCircle(sketch, "E636.MirrorC", {"center": v(-576.1, 135) * mm, "radius": 3.5 * mm});
            skCircle(sketch, "E637.MirrorC", {"center": v(323.9, 285) * mm, "radius": 3.5 * mm});
            skCircle(sketch, "E638.MirrorC", {"center": v(263.9, 15) * mm, "radius": 3.5 * mm});
            skCircle(sketch, "E639.MirrorC", {"center": v(233.9, 60) * mm, "radius": 3.5 * mm});
            skCircle(sketch, "E640.MirrorC", {"center": v(473.9, 120) * mm, "radius": 3.5 * mm});
            skCircle(sketch, "E641.MirrorC", {"center": v(383.9, 135) * mm, "radius": 3.5 * mm});
            skCircle(sketch, "E642.MirrorC", {"center": v(413.9, 30) * mm, "radius": 3.5 * mm});
            skCircle(sketch, "E643.MirrorC", {"center": v(563.9, 225) * mm, "radius": 3.5 * mm});
            skCircle(sketch, "E644.MirrorC", {"center": v(503.9, 105) * mm, "radius": 3.5 * mm});
            skCircle(sketch, "E645.MirrorC", {"center": v(683.9, 255) * mm, "radius": 3.5 * mm});
            skCircle(sketch, "E646.MirrorC", {"center": v(623.9, 45) * mm, "radius": 3.5 * mm});
            skCircle(sketch, "E647.MirrorC", {"center": v(833.9, 180) * mm, "radius": 3.5 * mm});
            skCircle(sketch, "E648.MirrorC", {"center": v(773.9, 240) * mm, "radius": 3.5 * mm});
            skCircle(sketch, "E649.MirrorC", {"center": v(773.9, 210) * mm, "radius": 3.5 * mm});
            skCircle(sketch, "E650.MirrorC", {"center": v(1013.9, 150) * mm, "radius": 3.5 * mm});
            skCircle(sketch, "E651.MirrorC", {"center": v(953.9, 300) * mm, "radius": 3.5 * mm});
            skCircle(sketch, "E652.MirrorC", {"center": v(923.9, 165) * mm, "radius": 3.5 * mm});
            skCircle(sketch, "E653.MirrorC", {"center": v(863.9, 195) * mm, "radius": 3.5 * mm});
            skCircle(sketch, "E654.MirrorC", {"center": v(1103.9, 75) * mm, "radius": 3.5 * mm});
            skCircle(sketch, "E655.MirrorC", {"center": v(1133.9, 270) * mm, "radius": 3.5 * mm});
            skCircle(sketch, "E656.MirrorC", {"center": v(-366.1, 30) * mm, "radius": 3.5 * mm});
            skCircle(sketch, "E657.MirrorC", {"center": v(-396.1, 135) * mm, "radius": 3.5 * mm});
            skCircle(sketch, "E658.MirrorC", {"center": v(-216.1, 225) * mm, "radius": 3.5 * mm});
            skCircle(sketch, "E659.MirrorC", {"center": v(-456.1, 285) * mm, "radius": 3.5 * mm});
            skCircle(sketch, "E660.MirrorC", {"center": v(-276.1, 105) * mm, "radius": 3.5 * mm});
            skCircle(sketch, "E661.MirrorC", {"center": v(-306.1, 120) * mm, "radius": 3.5 * mm});
            skCircle(sketch, "E662.MirrorC", {"center": v(-96.1, 255) * mm, "radius": 3.5 * mm});
            skCircle(sketch, "E663.MirrorC", {"center": v(-156.1, 45) * mm, "radius": 3.5 * mm});
            skCircle(sketch, "E664.MirrorC", {"center": v(53.9, 180) * mm, "radius": 3.5 * mm});
            skCircle(sketch, "E665.MirrorC", {"center": v(-6.1, 240) * mm, "radius": 3.5 * mm});
            skCircle(sketch, "E666.MirrorC", {"center": v(-6.1, 210) * mm, "radius": 3.5 * mm});
            skCircle(sketch, "E667.MirrorC", {"center": v(233.9, 150) * mm, "radius": 3.5 * mm});
            skCircle(sketch, "E668.MirrorC", {"center": v(173.9, 300) * mm, "radius": 3.5 * mm});
            skCircle(sketch, "E669.MirrorC", {"center": v(143.9, 165) * mm, "radius": 3.5 * mm});
            skCircle(sketch, "E670.MirrorC", {"center": v(83.9, 195) * mm, "radius": 3.5 * mm});
            skCircle(sketch, "E671.MirrorC", {"center": v(323.9, 75) * mm, "radius": 3.5 * mm});
            skCircle(sketch, "E672.MirrorC", {"center": v(353.9, 270) * mm, "radius": 3.5 * mm});
            skCircle(sketch, "E673.MirrorC", {"center": v(-66.1, 210) * mm, "radius": 3.5 * mm});
            skCircle(sketch, "E674.MirrorC", {"center": v(-66.1, 240) * mm, "radius": 3.5 * mm});
            skCircle(sketch, "E675.MirrorC", {"center": v(1343.9, 255) * mm, "radius": 3.5 * mm});
            skCircle(sketch, "E676.MirrorC", {"center": v(1283.9, 75) * mm, "radius": 3.5 * mm});
            skCircle(sketch, "E677.MirrorC", {"center": v(-516.1, 15) * mm, "radius": 3.5 * mm});
            skCircle(sketch, "E678.MirrorC", {"center": v(-546.1, 60) * mm, "radius": 3.5 * mm});
            skCircle(sketch, "E679.MirrorC", {"center": v(-546.1, 90) * mm, "radius": 3.5 * mm});
            skCircle(sketch, "E680.MirrorC", {"center": v(443.9, 15) * mm, "radius": 3.5 * mm});
            skCircle(sketch, "E681.MirrorC", {"center": v(413.9, 60) * mm, "radius": 3.5 * mm});
            skCircle(sketch, "E682.MirrorC", {"center": v(413.9, 90) * mm, "radius": 3.5 * mm});
            skCircle(sketch, "E683.MirrorC", {"center": v(563.9, 135) * mm, "radius": 3.5 * mm});
            skCircle(sketch, "E684.MirrorC", {"center": v(503.9, 285) * mm, "radius": 3.5 * mm});
            skCircle(sketch, "E685.MirrorC", {"center": v(683.9, 105) * mm, "radius": 3.5 * mm});
            skCircle(sketch, "E686.MirrorC", {"center": v(653.9, 120) * mm, "radius": 3.5 * mm});
            skCircle(sketch, "E687.MirrorC", {"center": v(593.9, 30) * mm, "radius": 3.5 * mm});
            skCircle(sketch, "E688.MirrorC", {"center": v(803.9, 45) * mm, "radius": 3.5 * mm});
            skCircle(sketch, "E689.MirrorC", {"center": v(-156.1, 255) * mm, "radius": 3.5 * mm});
            skCircle(sketch, "E690.MirrorC", {"center": v(743.9, 225) * mm, "radius": 3.5 * mm});
            skCircle(sketch, "E691.MirrorC", {"center": v(1013.9, 180) * mm, "radius": 3.5 * mm});
            skCircle(sketch, "E692.MirrorC", {"center": v(953.9, 240) * mm, "radius": 3.5 * mm});
            skCircle(sketch, "E693.MirrorC", {"center": v(863.9, 255) * mm, "radius": 3.5 * mm});
            skCircle(sketch, "E694.MirrorC", {"center": v(953.9, 210) * mm, "radius": 3.5 * mm});
            skCircle(sketch, "E695.MirrorC", {"center": v(1133.9, 300) * mm, "radius": 3.5 * mm});
            skCircle(sketch, "E696.MirrorC", {"center": v(1103.9, 165) * mm, "radius": 3.5 * mm});
            skCircle(sketch, "E697.MirrorC", {"center": v(1043.9, 195) * mm, "radius": 3.5 * mm});
            skCircle(sketch, "E698.MirrorC", {"center": v(1313.9, 270) * mm, "radius": 3.5 * mm});
            skCircle(sketch, "E699.MirrorC", {"center": v(1193.9, 150) * mm, "radius": 3.5 * mm});
            skCircle(sketch, "E700.MirrorC", {"center": v(-366.1, 60) * mm, "radius": 3.5 * mm});
            skCircle(sketch, "E701.MirrorC", {"center": v(-456.1, 75) * mm, "radius": 3.5 * mm});
            skCircle(sketch, "E702.MirrorC", {"center": v(-366.1, 90) * mm, "radius": 3.5 * mm});
            skCircle(sketch, "E703.MirrorC", {"center": v(-276.1, 285) * mm, "radius": 3.5 * mm});
            skCircle(sketch, "E704.MirrorC", {"center": v(-216.1, 135) * mm, "radius": 3.5 * mm});
            skCircle(sketch, "E705.MirrorC", {"center": v(-96.1, 105) * mm, "radius": 3.5 * mm});
            skCircle(sketch, "E706.MirrorC", {"center": v(-336.1, 15) * mm, "radius": 3.5 * mm});
            skCircle(sketch, "E707.MirrorC", {"center": v(-186.1, 30) * mm, "radius": 3.5 * mm});
            skCircle(sketch, "E708.MirrorC", {"center": v(-126.1, 120) * mm, "radius": 3.5 * mm});
            skCircle(sketch, "E709.MirrorC", {"center": v(23.9, 45) * mm, "radius": 3.5 * mm});
            skCircle(sketch, "E710.MirrorC", {"center": v(-36.1, 225) * mm, "radius": 3.5 * mm});
            skCircle(sketch, "E711.MirrorC", {"center": v(233.9, 180) * mm, "radius": 3.5 * mm});
            skCircle(sketch, "E712.MirrorC", {"center": v(173.9, 210) * mm, "radius": 3.5 * mm});
            skCircle(sketch, "E713.MirrorC", {"center": v(173.9, 240) * mm, "radius": 3.5 * mm});
            skCircle(sketch, "E714.MirrorC", {"center": v(353.9, 300) * mm, "radius": 3.5 * mm});
            skCircle(sketch, "E715.MirrorC", {"center": v(263.9, 195) * mm, "radius": 3.5 * mm});
            skCircle(sketch, "E716.MirrorC", {"center": v(83.9, 255) * mm, "radius": 3.5 * mm});
            skCircle(sketch, "E717.MirrorC", {"center": v(323.9, 165) * mm, "radius": 3.5 * mm});
            skCircle(sketch, "E718.MirrorC", {"center": v(413.9, 150) * mm, "radius": 3.5 * mm});
            skCircle(sketch, "E719.MirrorC", {"center": v(-426.1, 270) * mm, "radius": 3.5 * mm});
            skCircle(sketch, "E720.MirrorC", {"center": v(-546.1, 150) * mm, "radius": 3.5 * mm});
            skCircle(sketch, "E721.MirrorC", {"center": v(23.9, 195) * mm, "radius": 3.5 * mm});
            skCircle(sketch, "E722.MirrorC", {"center": v(593.9, 90) * mm, "radius": 3.5 * mm});
            skCircle(sketch, "E723.MirrorC", {"center": v(503.9, 75) * mm, "radius": 3.5 * mm});
            skCircle(sketch, "E724.MirrorC", {"center": v(533.9, 270) * mm, "radius": 3.5 * mm});
            skCircle(sketch, "E725.MirrorC", {"center": v(683.9, 285) * mm, "radius": 3.5 * mm});
            skCircle(sketch, "E726.MirrorC", {"center": v(593.9, 60) * mm, "radius": 3.5 * mm});
            skCircle(sketch, "E727.MirrorC", {"center": v(623.9, 15) * mm, "radius": 3.5 * mm});
            skCircle(sketch, "E728.MirrorC", {"center": v(593.9, 120) * mm, "radius": 3.5 * mm});
            skCircle(sketch, "E729.MirrorC", {"center": v(833.9, 120) * mm, "radius": 3.5 * mm});
            skCircle(sketch, "E730.MirrorC", {"center": v(773.9, 30) * mm, "radius": 3.5 * mm});
            skCircle(sketch, "E731.MirrorC", {"center": v(743.9, 135) * mm, "radius": 3.5 * mm});
            skCircle(sketch, "E732.MirrorC", {"center": v(983.9, 45) * mm, "radius": 3.5 * mm});
            skCircle(sketch, "E733.MirrorC", {"center": v(923.9, 225) * mm, "radius": 3.5 * mm});
            skCircle(sketch, "E734.MirrorC", {"center": v(863.9, 105) * mm, "radius": 3.5 * mm});
            skCircle(sketch, "E735.MirrorC", {"center": v(1133.9, 240) * mm, "radius": 3.5 * mm});
            skCircle(sketch, "E736.MirrorC", {"center": v(1133.9, 210) * mm, "radius": 3.5 * mm});
            skCircle(sketch, "E737.MirrorC", {"center": v(-6.1, 180) * mm, "radius": 3.5 * mm});
            skCircle(sketch, "E738.MirrorC", {"center": v(1043.9, 255) * mm, "radius": 3.5 * mm});
            skCircle(sketch, "E739.MirrorC", {"center": v(1283.9, 165) * mm, "radius": 3.5 * mm});
            skCircle(sketch, "E740.MirrorC", {"center": v(1223.9, 195) * mm, "radius": 3.5 * mm});
            skCircle(sketch, "E741.MirrorC", {"center": v(1193.9, 180) * mm, "radius": 3.5 * mm});
            skCircle(sketch, "E742.MirrorC", {"center": v(1343.9, 285) * mm, "radius": 3.5 * mm});
            skCircle(sketch, "E743.MirrorC", {"center": v(1313.9, 300) * mm, "radius": 3.5 * mm});
            skCircle(sketch, "E744.MirrorC", {"center": v(-366.1, 150) * mm, "radius": 3.5 * mm});
            skCircle(sketch, "E745.MirrorC", {"center": v(-186.1, 90) * mm, "radius": 3.5 * mm});
            skCircle(sketch, "E746.MirrorC", {"center": v(-426.1, 300) * mm, "radius": 3.5 * mm});
            skCircle(sketch, "E747.MirrorC", {"center": v(-246.1, 270) * mm, "radius": 3.5 * mm});
            skCircle(sketch, "E748.MirrorC", {"center": v(-96.1, 285) * mm, "radius": 3.5 * mm});
            skCircle(sketch, "E749.MirrorC", {"center": v(-276.1, 75) * mm, "radius": 3.5 * mm});
            skCircle(sketch, "E750.MirrorC", {"center": v(-156.1, 15) * mm, "radius": 3.5 * mm});
            skCircle(sketch, "E751.MirrorC", {"center": v(-186.1, 60) * mm, "radius": 3.5 * mm});
            skCircle(sketch, "E752.MirrorC", {"center": v(53.9, 120) * mm, "radius": 3.5 * mm});
            skCircle(sketch, "E753.MirrorC", {"center": v(-6.1, 30) * mm, "radius": 3.5 * mm});
            skCircle(sketch, "E754.MirrorC", {"center": v(203.9, 45) * mm, "radius": 3.5 * mm});
            skCircle(sketch, "E755.MirrorC", {"center": v(-36.1, 135) * mm, "radius": 3.5 * mm});
            skCircle(sketch, "E756.MirrorC", {"center": v(143.9, 225) * mm, "radius": 3.5 * mm});
            skCircle(sketch, "E757.MirrorC", {"center": v(353.9, 240) * mm, "radius": 3.5 * mm});
            skCircle(sketch, "E758.MirrorC", {"center": v(83.9, 105) * mm, "radius": 3.5 * mm});
            skCircle(sketch, "E759.MirrorC", {"center": v(353.9, 210) * mm, "radius": 3.5 * mm});
            skCircle(sketch, "E760.MirrorC", {"center": v(263.9, 255) * mm, "radius": 3.5 * mm});
            skCircle(sketch, "E761.MirrorC", {"center": v(443.9, 195) * mm, "radius": 3.5 * mm});
            skCircle(sketch, "E762.MirrorC", {"center": v(413.9, 180) * mm, "radius": 3.5 * mm});
            skCircle(sketch, "E763.MirrorC", {"center": v(-456.1, 165) * mm, "radius": 3.5 * mm});
            skCircle(sketch, "E764.MirrorC", {"center": v(-516.1, 195) * mm, "radius": 3.5 * mm});
            skCircle(sketch, "E765.MirrorC", {"center": v(-546.1, 180) * mm, "radius": 3.5 * mm});
            skCircle(sketch, "E766.MirrorC", {"center": v(533.9, 300) * mm, "radius": 3.5 * mm});
            skCircle(sketch, "E767.MirrorC", {"center": v(593.9, 150) * mm, "radius": 3.5 * mm});
            skCircle(sketch, "E768.MirrorC", {"center": v(503.9, 165) * mm, "radius": 3.5 * mm});
            skCircle(sketch, "E769.MirrorC", {"center": v(683.9, 75) * mm, "radius": 3.5 * mm});
            skCircle(sketch, "E770.MirrorC", {"center": v(713.9, 270) * mm, "radius": 3.5 * mm});
            skCircle(sketch, "E771.MirrorC", {"center": v(803.9, 15) * mm, "radius": 3.5 * mm});
            skCircle(sketch, "E772.MirrorC", {"center": v(773.9, 60) * mm, "radius": 3.5 * mm});
            skCircle(sketch, "E773.MirrorC", {"center": v(773.9, 90) * mm, "radius": 3.5 * mm});
            skCircle(sketch, "E774.MirrorC", {"center": v(1013.9, 120) * mm, "radius": 3.5 * mm});
            skCircle(sketch, "E775.MirrorC", {"center": v(953.9, 30) * mm, "radius": 3.5 * mm});
            skCircle(sketch, "E776.MirrorC", {"center": v(923.9, 135) * mm, "radius": 3.5 * mm});
            skCircle(sketch, "E777.MirrorC", {"center": v(863.9, 285) * mm, "radius": 3.5 * mm});
            skCircle(sketch, "E778.MirrorC", {"center": v(1103.9, 225) * mm, "radius": 3.5 * mm});
            skCircle(sketch, "E779.MirrorC", {"center": v(1043.9, 105) * mm, "radius": 3.5 * mm});
            skCircle(sketch, "E780.MirrorC", {"center": v(1313.9, 210) * mm, "radius": 3.5 * mm});
            skCircle(sketch, "E781.MirrorC", {"center": v(1223.9, 255) * mm, "radius": 3.5 * mm});
            skCircle(sketch, "E782.MirrorC", {"center": v(1163.9, 45) * mm, "radius": 3.5 * mm});
            skCircle(sketch, "E783.MirrorC", {"center": v(1313.9, 240) * mm, "radius": 3.5 * mm});
            skCircle(sketch, "E784.MirrorC", {"center": v(1073.9, 210) * mm, "radius": 3.5 * mm});
            skCircle(sketch, "E785.MirrorC", {"center": v(863.9, 225) * mm, "radius": 3.5 * mm});
            skCircle(sketch, "E786.MirrorC", {"center": v(-246.1, 30) * mm, "radius": 3.5 * mm});
            skCircle(sketch, "E787.MirrorC", {"center": v(-96.1, 225) * mm, "radius": 3.5 * mm});
            skCircle(sketch, "E788.MirrorC", {"center": v(-276.1, 135) * mm, "radius": 3.5 * mm});
            skCircle(sketch, "E789.MirrorC", {"center": v(803.9, 285) * mm, "radius": 3.5 * mm});
            skCircle(sketch, "E790.MirrorC", {"center": v(563.9, 15) * mm, "radius": 3.5 * mm});
            skCircle(sketch, "E791.MirrorC", {"center": v(-186.1, 120) * mm, "radius": 3.5 * mm});
            skCircle(sketch, "E792.MirrorC", {"center": v(293.9, 210) * mm, "radius": 3.5 * mm});
            skCircle(sketch, "E793.MirrorC", {"center": v(-396.1, 15) * mm, "radius": 3.5 * mm});
            skCircle(sketch, "E794.MirrorC", {"center": v(203.9, 195) * mm, "radius": 3.5 * mm});
            skCircle(sketch, "E795.MirrorC", {"center": v(-426.1, 90) * mm, "radius": 3.5 * mm});
            skCircle(sketch, "E796.MirrorC", {"center": v(-336.1, 285) * mm, "radius": 3.5 * mm});
            skCircle(sketch, "E797.MirrorC", {"center": v(533.9, 60) * mm, "radius": 3.5 * mm});
            skCircle(sketch, "E798.MirrorC", {"center": v(1313.9, 60) * mm, "radius": 3.5 * mm});
            skCircle(sketch, "E799.MirrorC", {"center": v(-546.1, 120) * mm, "radius": 3.5 * mm});
            skCircle(sketch, "E800.MirrorC", {"center": v(413.9, 120) * mm, "radius": 3.5 * mm});
            skCircle(sketch, "E801.MirrorC", {"center": v(353.9, 30) * mm, "radius": 3.5 * mm});
            skCircle(sketch, "E802.MirrorC", {"center": v(-6.1, 150) * mm, "radius": 3.5 * mm});
            skCircle(sketch, "E803.MirrorC", {"center": v(-516.1, 105) * mm, "radius": 3.5 * mm});
            skCircle(sketch, "E804.MirrorC", {"center": v(1313.9, 90) * mm, "radius": 3.5 * mm});
            skCircle(sketch, "E805.MirrorC", {"center": v(203.9, 15) * mm, "radius": 3.5 * mm});
            skCircle(sketch, "E806.MirrorC", {"center": v(-576.1, 45) * mm, "radius": 3.5 * mm});
            skCircle(sketch, "E807.MirrorC", {"center": v(-516.1, 255) * mm, "radius": 3.5 * mm});
            skCircle(sketch, "E808.MirrorC", {"center": v(-396.1, 45) * mm, "radius": 3.5 * mm});
            skCircle(sketch, "E809.MirrorC", {"center": v(-186.1, 180) * mm, "radius": 3.5 * mm});
            skCircle(sketch, "E810.MirrorC", {"center": v(-246.1, 240) * mm, "radius": 3.5 * mm});
            skCircle(sketch, "E811.MirrorC", {"center": v(-246.1, 210) * mm, "radius": 3.5 * mm});
            skCircle(sketch, "E812.MirrorC", {"center": v(-456.1, 225) * mm, "radius": 3.5 * mm});
            skCircle(sketch, "E813.MirrorC", {"center": v(713.9, 300) * mm, "radius": 3.5 * mm});
            skCircle(sketch, "E814.MirrorC", {"center": v(623.9, 195) * mm, "radius": 3.5 * mm});
            skCircle(sketch, "E815.MirrorC", {"center": v(533.9, 210) * mm, "radius": 3.5 * mm});
            skCircle(sketch, "E816.MirrorC", {"center": v(443.9, 255) * mm, "radius": 3.5 * mm});
            skCircle(sketch, "E817.MirrorC", {"center": v(593.9, 180) * mm, "radius": 3.5 * mm});
            skCircle(sketch, "E818.MirrorC", {"center": v(323.9, 225) * mm, "radius": 3.5 * mm});
            skCircle(sketch, "E819.MirrorC", {"center": v(263.9, 105) * mm, "radius": 3.5 * mm});
            skCircle(sketch, "E820.MirrorC", {"center": v(143.9, 135) * mm, "radius": 3.5 * mm});
            skCircle(sketch, "E821.MirrorC", {"center": v(83.9, 285) * mm, "radius": 3.5 * mm});
            skCircle(sketch, "E822.MirrorC", {"center": v(383.9, 45) * mm, "radius": 3.5 * mm});
            skCircle(sketch, "E823.MirrorC", {"center": v(-66.1, 270) * mm, "radius": 3.5 * mm});
            skCircle(sketch, "E824.MirrorC", {"center": v(-6.1, 90) * mm, "radius": 3.5 * mm});
            skCircle(sketch, "E825.MirrorC", {"center": v(233.9, 120) * mm, "radius": 3.5 * mm});
            skCircle(sketch, "E826.MirrorC", {"center": v(173.9, 30) * mm, "radius": 3.5 * mm});
            skCircle(sketch, "E827.MirrorC", {"center": v(23.9, 15) * mm, "radius": 3.5 * mm});
            skCircle(sketch, "E828.MirrorC", {"center": v(-6.1, 60) * mm, "radius": 3.5 * mm});
            skCircle(sketch, "E829.MirrorC", {"center": v(-96.1, 75) * mm, "radius": 3.5 * mm});
            skCircle(sketch, "E830.MirrorC", {"center": v(-276.1, 165) * mm, "radius": 3.5 * mm});
            skCircle(sketch, "E831.MirrorC", {"center": v(893.9, 270) * mm, "radius": 3.5 * mm});
            skCircle(sketch, "E832.MirrorC", {"center": v(623.9, 75) * mm, "radius": 3.5 * mm});
            skCircle(sketch, "E833.MirrorC", {"center": v(893.9, 30) * mm, "radius": 3.5 * mm});
            skCircle(sketch, "E834.MirrorC", {"center": v(713.9, 90) * mm, "radius": 3.5 * mm});
            skCircle(sketch, "E835.MirrorC", {"center": v(263.9, 225) * mm, "radius": 3.5 * mm});
            skCircle(sketch, "E836.MirrorC", {"center": v(773.9, 120) * mm, "radius": 3.5 * mm});
            skCircle(sketch, "E837.MirrorC", {"center": v(713.9, 60) * mm, "radius": 3.5 * mm});
            skCircle(sketch, "E838.MirrorC", {"center": v(-156.1, 105) * mm, "radius": 3.5 * mm});
            skCircle(sketch, "E839.MirrorC", {"center": v(263.9, 165) * mm, "radius": 3.5 * mm});
            skCircle(sketch, "E840.MirrorC", {"center": v(113.9, 210) * mm, "radius": 3.5 * mm});
            skCircle(sketch, "E841.MirrorC", {"center": v(83.9, 225) * mm, "radius": 3.5 * mm});
            skCircle(sketch, "E842.MirrorC", {"center": v(623.9, 285) * mm, "radius": 3.5 * mm});
            skCircle(sketch, "E843.MirrorC", {"center": v(1253.9, 270) * mm, "radius": 3.5 * mm});
            skCircle(sketch, "E844.MirrorC", {"center": v(83.9, 75) * mm, "radius": 3.5 * mm});
            skCircle(sketch, "E845.MirrorC", {"center": v(1193.9, 120) * mm, "radius": 3.5 * mm});
            skCircle(sketch, "E846.MirrorC", {"center": v(683.9, 165) * mm, "radius": 3.5 * mm});
            skCircle(sketch, "E847.MirrorC", {"center": v(-96.1, 165) * mm, "radius": 3.5 * mm});
            skCircle(sketch, "E848.MirrorC", {"center": v(-66.1, 300) * mm, "radius": 3.5 * mm});
            skCircle(sketch, "E849.MirrorC", {"center": v(-336.1, 255) * mm, "radius": 3.5 * mm});
            skCircle(sketch, "E850.MirrorC", {"center": v(-156.1, 195) * mm, "radius": 3.5 * mm});
            skCircle(sketch, "E851.MirrorC", {"center": v(863.9, 135) * mm, "radius": 3.5 * mm});
            skCircle(sketch, "E852.MirrorC", {"center": v(-486.1, 270) * mm, "radius": 3.5 * mm});
            skCircle(sketch, "E853.MirrorC", {"center": v(1103.9, 135) * mm, "radius": 3.5 * mm});
            skCircle(sketch, "E854.MirrorC", {"center": v(1043.9, 285) * mm, "radius": 3.5 * mm});
            skCircle(sketch, "E855.MirrorC", {"center": v(863.9, 75) * mm, "radius": 3.5 * mm});
            skCircle(sketch, "E856.MirrorC", {"center": v(1133.9, 30) * mm, "radius": 3.5 * mm});
            skCircle(sketch, "E857.MirrorC", {"center": v(743.9, 15) * mm, "radius": 3.5 * mm});
            skCircle(sketch, "E858.MirrorC", {"center": v(23.9, 255) * mm, "radius": 3.5 * mm});
            skCircle(sketch, "E859.MirrorC", {"center": v(713.9, 30) * mm, "radius": 3.5 * mm});
            skCircle(sketch, "E860.MirrorC", {"center": v(323.9, 45) * mm, "radius": 3.5 * mm});
            skCircle(sketch, "E861.MirrorC", {"center": v(-36.1, 45) * mm, "radius": 3.5 * mm});
            skCircle(sketch, "E862.MirrorC", {"center": v(953.9, 90) * mm, "radius": 3.5 * mm});
            skCircle(sketch, "E863.MirrorC", {"center": v(953.9, 60) * mm, "radius": 3.5 * mm});
            skCircle(sketch, "E864.MirrorC", {"center": v(983.9, 105) * mm, "radius": 3.5 * mm});
            skCircle(sketch, "E865.MirrorC", {"center": v(983.9, 15) * mm, "radius": 3.5 * mm});
            skCircle(sketch, "E866.MirrorC", {"center": v(473.9, 240) * mm, "radius": 3.5 * mm});
            skCircle(sketch, "E867.MirrorC", {"center": v(533.9, 240) * mm, "radius": 3.5 * mm});
            skCircle(sketch, "E868.MirrorC", {"center": v(773.9, 150) * mm, "radius": 3.5 * mm});
            skCircle(sketch, "E869.MirrorC", {"center": v(23.9, 105) * mm, "radius": 3.5 * mm});
            skCircle(sketch, "E870.MirrorC", {"center": v(293.9, 300) * mm, "radius": 3.5 * mm});
            skCircle(sketch, "E871.MirrorC", {"center": v(-426.1, 210) * mm, "radius": 3.5 * mm});
            skCircle(sketch, "E872.MirrorC", {"center": v(1283.9, 225) * mm, "radius": 3.5 * mm});
            skCircle(sketch, "E873.MirrorC", {"center": v(1223.9, 105) * mm, "radius": 3.5 * mm});
            skCircle(sketch, "E874.MirrorC", {"center": v(683.9, 135) * mm, "radius": 3.5 * mm});
            skCircle(sketch, "E875.MirrorC", {"center": v(-246.1, 300) * mm, "radius": 3.5 * mm});
            skCircle(sketch, "E876.MirrorC", {"center": v(-336.1, 195) * mm, "radius": 3.5 * mm});
            skCircle(sketch, "E877.MirrorC", {"center": v(-186.1, 150) * mm, "radius": 3.5 * mm});
            skCircle(sketch, "E878.MirrorC", {"center": v(-426.1, 240) * mm, "radius": 3.5 * mm});
            skCircle(sketch, "E879.MirrorC", {"center": v(653.9, 270) * mm, "radius": 3.5 * mm});
            skCircle(sketch, "E880.MirrorC", {"center": v(1283.9, 135) * mm, "radius": 3.5 * mm});
            skCircle(sketch, "E881.MirrorC", {"center": v(893.9, 300) * mm, "radius": 3.5 * mm});
            skCircle(sketch, "E882.MirrorC", {"center": v(113.9, 270) * mm, "radius": 3.5 * mm});
            skCircle(sketch, "E883.MirrorC", {"center": v(1223.9, 75) * mm, "radius": 3.5 * mm});
            skCircle(sketch, "E884.MirrorC", {"center": v(1043.9, 165) * mm, "radius": 3.5 * mm});
            skCircle(sketch, "E885.MirrorC", {"center": v(1133.9, 90) * mm, "radius": 3.5 * mm});
            skCircle(sketch, "E886.MirrorC", {"center": v(1073.9, 270) * mm, "radius": 3.5 * mm});
            skCircle(sketch, "E887.MirrorC", {"center": v(1313.9, 30) * mm, "radius": 3.5 * mm});
            skCircle(sketch, "E888.MirrorC", {"center": v(263.9, 285) * mm, "radius": 3.5 * mm});
            skCircle(sketch, "E889.MirrorC", {"center": v(1073.9, 300) * mm, "radius": 3.5 * mm});
            skCircle(sketch, "E890.MirrorC", {"center": v(323.9, 135) * mm, "radius": 3.5 * mm});
            skCircle(sketch, "E891.MirrorC", {"center": v(533.9, 150) * mm, "radius": 3.5 * mm});
            skCircle(sketch, "E892.MirrorC", {"center": v(803.9, 105) * mm, "radius": 3.5 * mm});
            skCircle(sketch, "E893.MirrorC", {"center": v(-366.1, 180) * mm, "radius": 3.5 * mm});
            skCircle(sketch, "E894.MirrorC", {"center": v(1043.9, 225) * mm, "radius": 3.5 * mm});
            skCircle(sketch, "E895.MirrorC", {"center": v(173.9, 60) * mm, "radius": 3.5 * mm});
            skCircle(sketch, "E896.MirrorC", {"center": v(1133.9, 150) * mm, "radius": 3.5 * mm});
            skCircle(sketch, "E897.MirrorC", {"center": v(173.9, 90) * mm, "radius": 3.5 * mm});
            skCircle(sketch, "E898.MirrorC", {"center": v(563.9, 45) * mm, "radius": 3.5 * mm});
            skCircle(sketch, "E899.MirrorC", {"center": v(623.9, 165) * mm, "radius": 3.5 * mm});
            skCircle(sketch, "E900.MirrorC", {"center": v(953.9, 150) * mm, "radius": 3.5 * mm});
            skCircle(sketch, "E901.MirrorC", {"center": v(1043.9, 75) * mm, "radius": 3.5 * mm});
            skCircle(sketch, "E902.MirrorC", {"center": v(1223.9, 285) * mm, "radius": 3.5 * mm});
            skCircle(sketch, "E903.MirrorC", {"center": v(1133.9, 60) * mm, "radius": 3.5 * mm});
            skCircle(sketch, "E904.MirrorC", {"center": v(1163.9, 15) * mm, "radius": 3.5 * mm});
            skLineSegment(sketch, "E905.MirrorCS", {"start": v(1343.9, 345) * mm, "end": v(1343.9, 345) * mm});
            skLineSegment(sketch, "E906.MirrorCS", {"start": v(1373.9, 360) * mm, "end": v(1373.9, 360) * mm});
            skSolve(sketch);
        }
        {
            var Q0;
            Q0=makeQuery(id+"F6.imprint","IMPRINT",FACE,{"disambiguationData":[TD([[makeQuery(id+"F6.imprint","IMPRINT",EDGE,{"derivedFrom":sQuery(id+"F6.wireOp",EDGE,"E638.MirrorC")}),-1.0]])]});
            var Q1;
            Q1=makeQuery(id+"F6.imprint","IMPRINT",FACE,{"disambiguationData":[TD([[makeQuery(id+"F6.imprint","IMPRINT",EDGE,{"derivedFrom":sQuery(id+"F6.wireOp",EDGE,"E587.MirrorC")}),-1.0]])]});
            var Q2;
            Q2=makeQuery(id+"F6.imprint","IMPRINT",FACE,{"disambiguationData":[TD([[makeQuery(id+"F6.imprint","IMPRINT",EDGE,{"derivedFrom":sQuery(id+"F6.wireOp",EDGE,"E41.0.2.0")}),1.0]])]});
            var Q3;
            Q3=makeQuery(id+"F6.imprint","IMPRINT",FACE,{"disambiguationData":[TD([[makeQuery(id+"F6.imprint","IMPRINT",EDGE,{"derivedFrom":sQuery(id+"F6.wireOp",EDGE,"E393.MirrorC")}),-1.0]])]});
            var Q4;
            Q4=makeQuery(id+"F6.imprint","IMPRINT",FACE,{"disambiguationData":[TD([[makeQuery(id+"F6.imprint","IMPRINT",EDGE,{"derivedFrom":sQuery(id+"F6.wireOp",EDGE,"E41.0.3.0")}),1.0]])]});
            var Q5;
            Q5=makeQuery(id+"F6.imprint","IMPRINT",FACE,{"disambiguationData":[TD([[makeQuery(id+"F6.imprint","IMPRINT",EDGE,{"derivedFrom":sQuery(id+"F6.wireOp",EDGE,"E341.MirrorC")}),-1.0]])]});
            var Q6;
            Q6=makeQuery(id+"F6.imprint","IMPRINT",FACE,{"disambiguationData":[TD([[makeQuery(id+"F6.imprint","IMPRINT",EDGE,{"derivedFrom":sQuery(id+"F6.wireOp",EDGE,"E41.0.4.0")}),1.0]])]});
            var Q7;
            Q7=makeQuery(id+"F6.imprint","IMPRINT",FACE,{"disambiguationData":[TD([[makeQuery(id+"F6.imprint","IMPRINT",EDGE,{"derivedFrom":sQuery(id+"F6.wireOp",EDGE,"E41.0.5.0")}),1.0]])]});
            var Q8;
            Q8=makeQuery(id+"F6.imprint","IMPRINT",FACE,{"disambiguationData":[TD([[makeQuery(id+"F6.imprint","IMPRINT",EDGE,{"derivedFrom":sQuery(id+"F6.wireOp",EDGE,"E740.MirrorC")}),-1.0]])]});
            var Q9;
            Q9=makeQuery(id+"F6.imprint","IMPRINT",FACE,{"disambiguationData":[TD([[makeQuery(id+"F6.imprint","IMPRINT",EDGE,{"derivedFrom":sQuery(id+"F6.wireOp",EDGE,"E41.0.6.0")}),1.0]])]});
            var Q10;
            Q10=makeQuery(id+"F6.imprint","IMPRINT",FACE,{"disambiguationData":[TD([[makeQuery(id+"F6.imprint","IMPRINT",EDGE,{"derivedFrom":sQuery(id+"F6.wireOp",EDGE,"E41.0.7.0")}),1.0]])]});
            var Q11;
            Q11=makeQuery(id+"F6.imprint","IMPRINT",FACE,{"disambiguationData":[TD([[makeQuery(id+"F6.imprint","IMPRINT",EDGE,{"derivedFrom":sQuery(id+"F6.wireOp",EDGE,"E601.MirrorC")}),-1.0]])]});
            var Q12;
            Q12=makeQuery(id+"F6.imprint","IMPRINT",FACE,{"disambiguationData":[TD([[makeQuery(id+"F6.imprint","IMPRINT",EDGE,{"derivedFrom":sQuery(id+"F6.wireOp",EDGE,"E653.MirrorC")}),-1.0]])]});
            var Q13;
            Q13=makeQuery(id+"F6.imprint","IMPRINT",FACE,{"disambiguationData":[TD([[makeQuery(id+"F6.imprint","IMPRINT",EDGE,{"derivedFrom":sQuery(id+"F6.wireOp",EDGE,"E41.0.8.0")}),1.0]])]});
            var Q14;
            Q14=makeQuery(id+"F6.imprint","IMPRINT",FACE,{"disambiguationData":[TD([[makeQuery(id+"F6.imprint","IMPRINT",EDGE,{"derivedFrom":sQuery(id+"F6.wireOp",EDGE,"E355.MirrorC")}),-1.0]])]});
            var Q15;
            Q15=makeQuery(id+"F6.imprint","IMPRINT",FACE,{"disambiguationData":[TD([[makeQuery(id+"F6.imprint","IMPRINT",EDGE,{"derivedFrom":sQuery(id+"F6.wireOp",EDGE,"E41.0.9.0")}),1.0]])]});
            var Q16;
            Q16=makeQuery(id+"F6.imprint","IMPRINT",FACE,{"disambiguationData":[TD([[makeQuery(id+"F6.imprint","IMPRINT",EDGE,{"derivedFrom":sQuery(id+"F6.wireOp",EDGE,"E407.MirrorC")}),-1.0]])]});
            var Q17;
            Q17=makeQuery(id+"F6.imprint","IMPRINT",FACE,{"disambiguationData":[TD([[makeQuery(id+"F6.imprint","IMPRINT",EDGE,{"derivedFrom":sQuery(id+"F6.wireOp",EDGE,"E41.0.10.0")}),1.0]])]});
            var Q18;
            Q18=makeQuery(id+"F6.imprint","IMPRINT",FACE,{"disambiguationData":[TD([[makeQuery(id+"F6.imprint","IMPRINT",EDGE,{"derivedFrom":sQuery(id+"F6.wireOp",EDGE,"E41.0.11.0")}),1.0]])]});
            var Q19;
            Q19=makeQuery(id+"F6.imprint","IMPRINT",FACE,{"disambiguationData":[TD([[makeQuery(id+"F6.imprint","IMPRINT",EDGE,{"derivedFrom":sQuery(id+"F6.wireOp",EDGE,"E808.MirrorC")}),-1.0]])]});
            var Q20;
            Q20=makeQuery(id+"F6.imprint","IMPRINT",FACE,{"disambiguationData":[TD([[makeQuery(id+"F6.imprint","IMPRINT",EDGE,{"derivedFrom":sQuery(id+"F6.wireOp",EDGE,"E608.MirrorC")}),-1.0]])]});
            var Q21;
            Q21=makeQuery(id+"F6.imprint","IMPRINT",FACE,{"disambiguationData":[TD([[makeQuery(id+"F6.imprint","IMPRINT",EDGE,{"derivedFrom":sQuery(id+"F6.wireOp",EDGE,"E361.MirrorC")}),-1.0]])]});
            var Q22;
            Q22=makeQuery(id+"F6.imprint","IMPRINT",FACE,{"disambiguationData":[TD([[makeQuery(id+"F6.imprint","IMPRINT",EDGE,{"derivedFrom":sQuery(id+"F6.wireOp",EDGE,"E556.MirrorC")}),-1.0]])]});
            var Q23;
            Q23=makeQuery(id+"F6.imprint","IMPRINT",FACE,{"disambiguationData":[TD([[makeQuery(id+"F6.imprint","IMPRINT",EDGE,{"derivedFrom":sQuery(id+"F6.wireOp",EDGE,"E347.MirrorC")}),-1.0]])]});
            var Q24;
            Q24=makeQuery(id+"F6.imprint","IMPRINT",FACE,{"disambiguationData":[TD([[makeQuery(id+"F6.imprint","IMPRINT",EDGE,{"derivedFrom":sQuery(id+"F6.wireOp",EDGE,"E762.MirrorC")}),-1.0]])]});
            var Q25;
            Q25=makeQuery(id+"F6.imprint","IMPRINT",FACE,{"disambiguationData":[TD([[makeQuery(id+"F6.imprint","IMPRINT",EDGE,{"derivedFrom":sQuery(id+"F6.wireOp",EDGE,"E571.MirrorC")}),-1.0]])]});
            var Q26;
            Q26=makeQuery(id+"F6.imprint","IMPRINT",FACE,{"disambiguationData":[TD([[makeQuery(id+"F6.imprint","IMPRINT",EDGE,{"derivedFrom":sQuery(id+"F6.wireOp",EDGE,"E623.MirrorC")}),-1.0]])]});
            var Q27;
            Q27=makeQuery(id+"F6.imprint","IMPRINT",FACE,{"disambiguationData":[TD([[makeQuery(id+"F6.imprint","IMPRINT",EDGE,{"derivedFrom":sQuery(id+"F6.wireOp",EDGE,"E377.MirrorC")}),-1.0]])]});
            var Q28;
            Q28=makeQuery(id+"F6.imprint","IMPRINT",FACE,{"disambiguationData":[TD([[makeQuery(id+"F6.imprint","IMPRINT",EDGE,{"derivedFrom":sQuery(id+"F6.wireOp",EDGE,"E699.MirrorC")}),-1.0]])]});
            var Q29;
            Q29=makeQuery(id+"F6.imprint","IMPRINT",FACE,{"disambiguationData":[TD([[makeQuery(id+"F6.imprint","IMPRINT",EDGE,{"derivedFrom":sQuery(id+"F6.wireOp",EDGE,"E453.MirrorC")}),-1.0]])]});
            var Q30;
            Q30=makeQuery(id+"F6.imprint","IMPRINT",FACE,{"disambiguationData":[TD([[makeQuery(id+"F6.imprint","IMPRINT",EDGE,{"derivedFrom":sQuery(id+"F6.wireOp",EDGE,"E401.MirrorC")}),-1.0]])]});
            var Q31;
            Q31=makeQuery(id+"F6.imprint","IMPRINT",FACE,{"disambiguationData":[TD([[makeQuery(id+"F6.imprint","IMPRINT",EDGE,{"derivedFrom":sQuery(id+"F6.wireOp",EDGE,"E383.MirrorC")}),-1.0]])]});
            var Q32;
            Q32=makeQuery(id+"F6.imprint","IMPRINT",FACE,{"disambiguationData":[TD([[makeQuery(id+"F6.imprint","IMPRINT",EDGE,{"derivedFrom":sQuery(id+"F6.wireOp",EDGE,"E801.MirrorC")}),-1.0]])]});
            var Q33;
            Q33=makeQuery(id+"F6.imprint","IMPRINT",FACE,{"disambiguationData":[TD([[makeQuery(id+"F6.imprint","IMPRINT",EDGE,{"derivedFrom":sQuery(id+"F6.wireOp",EDGE,"E662.MirrorC")}),-1.0]])]});
            var Q34;
            Q34=makeQuery(id+"F6.imprint","IMPRINT",FACE,{"disambiguationData":[TD([[makeQuery(id+"F6.imprint","IMPRINT",EDGE,{"derivedFrom":sQuery(id+"F6.wireOp",EDGE,"E714.MirrorC")}),-1.0]])]});
            var Q35;
            Q35=makeQuery(id+"F6.imprint","IMPRINT",FACE,{"disambiguationData":[TD([[makeQuery(id+"F6.imprint","IMPRINT",EDGE,{"derivedFrom":sQuery(id+"F6.wireOp",EDGE,"E416.MirrorC")}),-1.0]])]});
            var Q36;
            Q36=makeQuery(id+"F6.imprint","IMPRINT",FACE,{"disambiguationData":[TD([[makeQuery(id+"F6.imprint","IMPRINT",EDGE,{"derivedFrom":sQuery(id+"F6.wireOp",EDGE,"E469.MirrorC")}),-1.0]])]});
            var Q37;
            Q37=makeQuery(id+"F6.imprint","IMPRINT",FACE,{"disambiguationData":[TD([[makeQuery(id+"F6.imprint","IMPRINT",EDGE,{"derivedFrom":sQuery(id+"F6.wireOp",EDGE,"E816.MirrorC")}),-1.0]])]});
            var Q38;
            Q38=makeQuery(id+"F6.imprint","IMPRINT",FACE,{"disambiguationData":[TD([[makeQuery(id+"F6.imprint","IMPRINT",EDGE,{"derivedFrom":sQuery(id+"F6.wireOp",EDGE,"E868.MirrorC")}),-1.0]])]});
            var Q39;
            Q39=makeQuery(id+"F6.imprint","IMPRINT",FACE,{"disambiguationData":[TD([[makeQuery(id+"F6.imprint","IMPRINT",EDGE,{"derivedFrom":sQuery(id+"F6.wireOp",EDGE,"E616.MirrorC")}),-1.0]])]});
            var Q40;
            Q40=makeQuery(id+"F6.imprint","IMPRINT",FACE,{"disambiguationData":[TD([[makeQuery(id+"F6.imprint","IMPRINT",EDGE,{"derivedFrom":sQuery(id+"F6.wireOp",EDGE,"E668.MirrorC")}),-1.0]])]});
            var Q41;
            Q41=makeQuery(id+"F6.imprint","IMPRINT",FACE,{"disambiguationData":[TD([[makeQuery(id+"F6.imprint","IMPRINT",EDGE,{"derivedFrom":sQuery(id+"F6.wireOp",EDGE,"E370.MirrorC")}),-1.0]])]});
            var Q42;
            Q42=makeQuery(id+"F6.imprint","IMPRINT",FACE,{"disambiguationData":[TD([[makeQuery(id+"F6.imprint","IMPRINT",EDGE,{"derivedFrom":sQuery(id+"F6.wireOp",EDGE,"E422.MirrorC")}),-1.0]])]});
            var Q43;
            Q43=makeQuery(id+"F6.imprint","IMPRINT",FACE,{"disambiguationData":[TD([[makeQuery(id+"F6.imprint","IMPRINT",EDGE,{"derivedFrom":sQuery(id+"F6.wireOp",EDGE,"E353.MirrorC")}),-1.0]])]});
            var Q44;
            Q44=makeQuery(id+"F6.imprint","IMPRINT",FACE,{"disambiguationData":[TD([[makeQuery(id+"F6.imprint","IMPRINT",EDGE,{"derivedFrom":sQuery(id+"F6.wireOp",EDGE,"E771.MirrorC")}),-1.0]])]});
            var Q45;
            Q45=makeQuery(id+"F6.imprint","IMPRINT",FACE,{"disambiguationData":[TD([[makeQuery(id+"F6.imprint","IMPRINT",EDGE,{"derivedFrom":sQuery(id+"F6.wireOp",EDGE,"E822.MirrorC")}),-1.0]])]});
            var Q46;
            Q46=makeQuery(id+"F6.imprint","IMPRINT",FACE,{"disambiguationData":[TD([[makeQuery(id+"F6.imprint","IMPRINT",EDGE,{"derivedFrom":sQuery(id+"F6.wireOp",EDGE,"E631.MirrorC")}),-1.0]])]});
            var Q47;
            Q47=makeQuery(id+"F6.imprint","IMPRINT",FACE,{"disambiguationData":[TD([[makeQuery(id+"F6.imprint","IMPRINT",EDGE,{"derivedFrom":sQuery(id+"F6.wireOp",EDGE,"E684.MirrorC")}),-1.0]])]});
            var Q48;
            Q48=makeQuery(id+"F6.imprint","IMPRINT",FACE,{"disambiguationData":[TD([[makeQuery(id+"F6.imprint","IMPRINT",EDGE,{"derivedFrom":sQuery(id+"F6.wireOp",EDGE,"E386.MirrorC")}),-1.0]])]});
            var Q49;
            Q49=makeQuery(id+"F6.imprint","IMPRINT",FACE,{"disambiguationData":[TD([[makeQuery(id+"F6.imprint","IMPRINT",EDGE,{"derivedFrom":sQuery(id+"F6.wireOp",EDGE,"E438.MirrorC")}),-1.0]])]});
            var Q50;
            Q50=makeQuery(id+"F6.imprint","IMPRINT",FACE,{"disambiguationData":[TD([[makeQuery(id+"F6.imprint","IMPRINT",EDGE,{"derivedFrom":sQuery(id+"F6.wireOp",EDGE,"E367.MirrorC")}),-1.0]])]});
            var Q51;
            Q51=makeQuery(id+"F6.imprint","IMPRINT",FACE,{"disambiguationData":[TD([[makeQuery(id+"F6.imprint","IMPRINT",EDGE,{"derivedFrom":sQuery(id+"F6.wireOp",EDGE,"E837.MirrorC")}),-1.0]])]});
            var Q52;
            Q52=makeQuery(id+"F6.imprint","IMPRINT",FACE,{"disambiguationData":[TD([[makeQuery(id+"F6.imprint","IMPRINT",EDGE,{"derivedFrom":sQuery(id+"F6.wireOp",EDGE,"E786.MirrorC")}),-1.0]])]});
            var Q53;
            Q53=makeQuery(id+"F6.imprint","IMPRINT",FACE,{"disambiguationData":[TD([[makeQuery(id+"F6.imprint","IMPRINT",EDGE,{"derivedFrom":sQuery(id+"F6.wireOp",EDGE,"E514.MirrorC")}),-1.0]])]});
            var Q54;
            Q54=makeQuery(id+"F6.imprint","IMPRINT",FACE,{"disambiguationData":[TD([[makeQuery(id+"F6.imprint","IMPRINT",EDGE,{"derivedFrom":sQuery(id+"F6.wireOp",EDGE,"E462.MirrorC")}),-1.0]])]});
            var Q55;
            Q55=makeQuery(id+"F6.imprint","IMPRINT",FACE,{"disambiguationData":[TD([[makeQuery(id+"F6.imprint","IMPRINT",EDGE,{"derivedFrom":sQuery(id+"F6.wireOp",EDGE,"E444.MirrorC")}),-1.0]])]});
            var Q56;
            Q56=makeQuery(id+"F6.imprint","IMPRINT",FACE,{"disambiguationData":[TD([[makeQuery(id+"F6.imprint","IMPRINT",EDGE,{"derivedFrom":sQuery(id+"F6.wireOp",EDGE,"E861.MirrorC")}),-1.0]])]});
            var Q57;
            Q57=makeQuery(id+"F6.imprint","IMPRINT",FACE,{"disambiguationData":[TD([[makeQuery(id+"F6.imprint","IMPRINT",EDGE,{"derivedFrom":sQuery(id+"F6.wireOp",EDGE,"E708.MirrorC")}),-1.0]])]});
            var Q58;
            Q58=makeQuery(id+"F6.imprint","IMPRINT",FACE,{"disambiguationData":[TD([[makeQuery(id+"F6.imprint","IMPRINT",EDGE,{"derivedFrom":sQuery(id+"F6.wireOp",EDGE,"E477.MirrorC")}),-1.0]])]});
            var Q59;
            Q59=makeQuery(id+"F6.imprint","IMPRINT",FACE,{"disambiguationData":[TD([[makeQuery(id+"F6.imprint","IMPRINT",EDGE,{"derivedFrom":sQuery(id+"F6.wireOp",EDGE,"E530.MirrorC")}),-1.0]])]});
            var Q60;
            Q60=makeQuery(id+"F6.imprint","IMPRINT",FACE,{"disambiguationData":[TD([[makeQuery(id+"F6.imprint","IMPRINT",EDGE,{"derivedFrom":sQuery(id+"F6.wireOp",EDGE,"E876.MirrorC")}),-1.0]])]});
            var Q61;
            Q61=makeQuery(id+"F6.imprint","IMPRINT",FACE,{"disambiguationData":[TD([[makeQuery(id+"F6.imprint","IMPRINT",EDGE,{"derivedFrom":sQuery(id+"F6.wireOp",EDGE,"E459.MirrorC")}),-1.0]])]});
            var Q62;
            Q62=makeQuery(id+"F6.imprint","IMPRINT",FACE,{"disambiguationData":[TD([[makeQuery(id+"F6.imprint","IMPRINT",EDGE,{"derivedFrom":sQuery(id+"F6.wireOp",EDGE,"E723.MirrorC")}),-1.0]])]});
            var Q63;
            Q63=makeQuery(id+"F6.imprint","IMPRINT",FACE,{"disambiguationData":[TD([[makeQuery(id+"F6.imprint","IMPRINT",EDGE,{"derivedFrom":sQuery(id+"F6.wireOp",EDGE,"E484.MirrorC")}),-1.0]])]});
            var Q64;
            Q64=makeQuery(id+"F6.imprint","IMPRINT",FACE,{"disambiguationData":[TD([[makeQuery(id+"F6.imprint","IMPRINT",EDGE,{"derivedFrom":sQuery(id+"F6.wireOp",EDGE,"E677.MirrorC")}),-1.0]])]});
            var Q65;
            Q65=makeQuery(id+"F6.imprint","IMPRINT",FACE,{"disambiguationData":[TD([[makeQuery(id+"F6.imprint","IMPRINT",EDGE,{"derivedFrom":sQuery(id+"F6.wireOp",EDGE,"E431.MirrorC")}),-1.0]])]});
            var Q66;
            Q66=makeQuery(id+"F6.imprint","IMPRINT",FACE,{"disambiguationData":[TD([[makeQuery(id+"F6.imprint","IMPRINT",EDGE,{"derivedFrom":sQuery(id+"F6.wireOp",EDGE,"E883.MirrorC")}),-1.0]])]});
            var Q67;
            Q67=makeQuery(id+"F6.imprint","IMPRINT",FACE,{"disambiguationData":[TD([[makeQuery(id+"F6.imprint","IMPRINT",EDGE,{"derivedFrom":sQuery(id+"F6.wireOp",EDGE,"E730.MirrorC")}),-1.0]])]});
            var Q68;
            Q68=makeQuery(id+"F6.imprint","IMPRINT",FACE,{"disambiguationData":[TD([[makeQuery(id+"F6.imprint","IMPRINT",EDGE,{"derivedFrom":sQuery(id+"F6.wireOp",EDGE,"E413.MirrorC")}),-1.0]])]});
            var Q69;
            Q69=makeQuery(id+"F6.imprint","IMPRINT",FACE,{"disambiguationData":[TD([[makeQuery(id+"F6.imprint","IMPRINT",EDGE,{"derivedFrom":sQuery(id+"F6.wireOp",EDGE,"E831.MirrorC")}),-1.0]])]});
            var Q70;
            Q70=makeQuery(id+"F6.imprint","IMPRINT",FACE,{"disambiguationData":[TD([[makeQuery(id+"F6.imprint","IMPRINT",EDGE,{"derivedFrom":sQuery(id+"F6.wireOp",EDGE,"E447.MirrorC")}),-1.0]])]});
            var Q71;
            Q71=makeQuery(id+"F6.imprint","IMPRINT",FACE,{"disambiguationData":[TD([[makeQuery(id+"F6.imprint","IMPRINT",EDGE,{"derivedFrom":sQuery(id+"F6.wireOp",EDGE,"E499.MirrorC")}),-1.0]])]});
            var Q72;
            Q72=makeQuery(id+"F6.imprint","IMPRINT",FACE,{"disambiguationData":[TD([[makeQuery(id+"F6.imprint","IMPRINT",EDGE,{"derivedFrom":sQuery(id+"F6.wireOp",EDGE,"E899.MirrorC")}),-1.0]])]});
            var Q73;
            Q73=makeQuery(id+"F6.imprint","IMPRINT",FACE,{"disambiguationData":[TD([[makeQuery(id+"F6.imprint","IMPRINT",EDGE,{"derivedFrom":sQuery(id+"F6.wireOp",EDGE,"E846.MirrorC")}),-1.0]])]});
            var Q74;
            Q74=makeQuery(id+"F6.imprint","IMPRINT",FACE,{"disambiguationData":[TD([[makeQuery(id+"F6.imprint","IMPRINT",EDGE,{"derivedFrom":sQuery(id+"F6.wireOp",EDGE,"E692.MirrorC")}),-1.0]])]});
            var Q75;
            Q75=makeQuery(id+"F6.imprint","IMPRINT",FACE,{"disambiguationData":[TD([[makeQuery(id+"F6.imprint","IMPRINT",EDGE,{"derivedFrom":sQuery(id+"F6.wireOp",EDGE,"E428.MirrorC")}),-1.0]])]});
            var Q76;
            Q76=makeQuery(id+"F6.imprint","IMPRINT",FACE,{"disambiguationData":[TD([[makeQuery(id+"F6.imprint","IMPRINT",EDGE,{"derivedFrom":sQuery(id+"F6.wireOp",EDGE,"E576.MirrorC")}),-1.0]])]});
            var Q77;
            Q77=makeQuery(id+"F6.imprint","IMPRINT",FACE,{"disambiguationData":[TD([[makeQuery(id+"F6.imprint","IMPRINT",EDGE,{"derivedFrom":sQuery(id+"F6.wireOp",EDGE,"E523.MirrorC")}),-1.0]])]});
            var Q78;
            Q78=makeQuery(id+"F6.imprint","IMPRINT",FACE,{"disambiguationData":[TD([[makeQuery(id+"F6.imprint","IMPRINT",EDGE,{"derivedFrom":sQuery(id+"F6.wireOp",EDGE,"E505.MirrorC")}),-1.0]])]});
            var Q79;
            Q79=makeQuery(id+"F6.imprint","IMPRINT",FACE,{"disambiguationData":[TD([[makeQuery(id+"F6.imprint","IMPRINT",EDGE,{"derivedFrom":sQuery(id+"F6.wireOp",EDGE,"E539.MirrorC")}),-1.0]])]});
            var Q80;
            Q80=makeQuery(id+"F6.imprint","IMPRINT",FACE,{"disambiguationData":[TD([[makeQuery(id+"F6.imprint","IMPRINT",EDGE,{"derivedFrom":sQuery(id+"F6.wireOp",EDGE,"E592.MirrorC")}),-1.0]])]});
            var Q81;
            Q81=makeQuery(id+"F6.imprint","IMPRINT",FACE,{"disambiguationData":[TD([[makeQuery(id+"F6.imprint","IMPRINT",EDGE,{"derivedFrom":sQuery(id+"F6.wireOp",EDGE,"E520.MirrorC")}),-1.0]])]});
            var Q82;
            Q82=makeQuery(id+"F6.imprint","IMPRINT",FACE,{"disambiguationData":[TD([[makeQuery(id+"F6.imprint","IMPRINT",EDGE,{"derivedFrom":sQuery(id+"F6.wireOp",EDGE,"E745.MirrorC")}),-1.0]])]});
            var Q83;
            Q83=makeQuery(id+"F6.imprint","IMPRINT",FACE,{"disambiguationData":[TD([[makeQuery(id+"F6.imprint","IMPRINT",EDGE,{"derivedFrom":sQuery(id+"F6.wireOp",EDGE,"E493.MirrorC")}),-1.0]])]});
            var Q84;
            Q84=makeQuery(id+"F6.imprint","IMPRINT",FACE,{"disambiguationData":[TD([[makeQuery(id+"F6.imprint","IMPRINT",EDGE,{"derivedFrom":sQuery(id+"F6.wireOp",EDGE,"E545.MirrorC")}),-1.0]])]});
            var Q85;
            Q85=makeQuery(id+"F6.imprint","IMPRINT",FACE,{"disambiguationData":[TD([[makeQuery(id+"F6.imprint","IMPRINT",EDGE,{"derivedFrom":sQuery(id+"F6.wireOp",EDGE,"E474.MirrorC")}),-1.0]])]});
            var Q86;
            Q86=makeQuery(id+"F6.imprint","IMPRINT",FACE,{"disambiguationData":[TD([[makeQuery(id+"F6.imprint","IMPRINT",EDGE,{"derivedFrom":sQuery(id+"F6.wireOp",EDGE,"E892.MirrorC")}),-1.0]])]});
            var Q87;
            Q87=makeQuery(id+"F6.imprint","IMPRINT",FACE,{"disambiguationData":[TD([[makeQuery(id+"F6.imprint","IMPRINT",EDGE,{"derivedFrom":sQuery(id+"F6.wireOp",EDGE,"E507.MirrorC")}),-1.0]])]});
            var Q88;
            Q88=makeQuery(id+"F6.imprint","IMPRINT",FACE,{"disambiguationData":[TD([[makeQuery(id+"F6.imprint","IMPRINT",EDGE,{"derivedFrom":sQuery(id+"F6.wireOp",EDGE,"E560.MirrorC")}),-1.0]])]});
            var Q89;
            Q89=makeQuery(id+"F6.imprint","IMPRINT",FACE,{"disambiguationData":[TD([[makeQuery(id+"F6.imprint","IMPRINT",EDGE,{"derivedFrom":sQuery(id+"F6.wireOp",EDGE,"E490.MirrorC")}),-1.0]])]});
            var Q90;
            Q90=makeQuery(id+"F6.imprint","IMPRINT",FACE,{"disambiguationData":[TD([[makeQuery(id+"F6.imprint","IMPRINT",EDGE,{"derivedFrom":sQuery(id+"F6.wireOp",EDGE,"E582.MirrorC")}),-1.0]])]});
            var Q91;
            Q91=makeQuery(id+"F6.imprint","IMPRINT",FACE,{"disambiguationData":[TD([[makeQuery(id+"F6.imprint","IMPRINT",EDGE,{"derivedFrom":sQuery(id+"F6.wireOp",EDGE,"E791.MirrorC")}),-1.0]])]});
            var Q92;
            Q92=makeQuery(id+"F6.imprint","IMPRINT",FACE,{"disambiguationData":[TD([[makeQuery(id+"F6.imprint","IMPRINT",EDGE,{"derivedFrom":sQuery(id+"F6.wireOp",EDGE,"E738.MirrorC")}),-1.0]])]});
            var Q93;
            Q93=makeQuery(id+"F6.imprint","IMPRINT",FACE,{"disambiguationData":[TD([[makeQuery(id+"F6.imprint","IMPRINT",EDGE,{"derivedFrom":sQuery(id+"F6.wireOp",EDGE,"E636.MirrorC")}),-1.0]])]});
            var Q94;
            Q94=makeQuery(id+"F6.imprint","IMPRINT",FACE,{"disambiguationData":[TD([[makeQuery(id+"F6.imprint","IMPRINT",EDGE,{"derivedFrom":sQuery(id+"F6.wireOp",EDGE,"E585.MirrorC")}),-1.0]])]});
            var Q95;
            Q95=makeQuery(id+"F6.imprint","IMPRINT",FACE,{"disambiguationData":[TD([[makeQuery(id+"F6.imprint","IMPRINT",EDGE,{"derivedFrom":sQuery(id+"F6.wireOp",EDGE,"E597.MirrorC")}),-1.0]])]});
            var Q96;
            Q96=makeQuery(id+"F6.imprint","IMPRINT",FACE,{"disambiguationData":[TD([[makeQuery(id+"F6.imprint","IMPRINT",EDGE,{"derivedFrom":sQuery(id+"F6.wireOp",EDGE,"E754.MirrorC")}),-1.0]])]});
            var Q97;
            Q97=makeQuery(id+"F6.imprint","IMPRINT",FACE,{"disambiguationData":[TD([[makeQuery(id+"F6.imprint","IMPRINT",EDGE,{"derivedFrom":sQuery(id+"F6.wireOp",EDGE,"E806.MirrorC")}),-1.0]])]});
            var Q98;
            Q98=makeQuery(id+"F6.imprint","IMPRINT",FACE,{"disambiguationData":[TD([[makeQuery(id+"F6.imprint","IMPRINT",EDGE,{"derivedFrom":sQuery(id+"F6.wireOp",EDGE,"E600.MirrorC")}),-1.0]])]});
            var Q99;
            Q99=makeQuery(id+"F6.imprint","IMPRINT",FACE,{"disambiguationData":[TD([[makeQuery(id+"F6.imprint","IMPRINT",EDGE,{"derivedFrom":sQuery(id+"F6.wireOp",EDGE,"E651.MirrorC")}),-1.0]])]});
            var Q100;
            Q100=makeQuery(id+"F6.imprint","IMPRINT",FACE,{"disambiguationData":[TD([[makeQuery(id+"F6.imprint","IMPRINT",EDGE,{"derivedFrom":sQuery(id+"F6.wireOp",EDGE,"E554.MirrorC")}),-1.0]])]});
            var Q101;
            Q101=makeQuery(id+"F6.imprint","IMPRINT",FACE,{"disambiguationData":[TD([[makeQuery(id+"F6.imprint","IMPRINT",EDGE,{"derivedFrom":sQuery(id+"F6.wireOp",EDGE,"E760.MirrorC")}),-1.0]])]});
            var Q102;
            Q102=makeQuery(id+"F6.imprint","IMPRINT",FACE,{"disambiguationData":[TD([[makeQuery(id+"F6.imprint","IMPRINT",EDGE,{"derivedFrom":sQuery(id+"F6.wireOp",EDGE,"E536.MirrorC")}),-1.0]])]});
            var Q103;
            Q103=makeQuery(id+"F6.imprint","IMPRINT",FACE,{"disambiguationData":[TD([[makeQuery(id+"F6.imprint","IMPRINT",EDGE,{"derivedFrom":sQuery(id+"F6.wireOp",EDGE,"E606.MirrorC")}),-1.0]])]});
            var Q104;
            Q104=makeQuery(id+"F6.imprint","IMPRINT",FACE,{"disambiguationData":[TD([[makeQuery(id+"F6.imprint","IMPRINT",EDGE,{"derivedFrom":sQuery(id+"F6.wireOp",EDGE,"E566.MirrorC")}),-1.0]])]});
            var Q105;
            Q105=makeQuery(id+"F6.imprint","IMPRINT",FACE,{"disambiguationData":[TD([[makeQuery(id+"F6.imprint","IMPRINT",EDGE,{"derivedFrom":sQuery(id+"F6.wireOp",EDGE,"E776.MirrorC")}),-1.0]])]});
            var Q106;
            Q106=makeQuery(id+"F6.imprint","IMPRINT",FACE,{"disambiguationData":[TD([[makeQuery(id+"F6.imprint","IMPRINT",EDGE,{"derivedFrom":sQuery(id+"F6.wireOp",EDGE,"E551.MirrorC")}),-1.0]])]});
            var Q107;
            Q107=makeQuery(id+"F6.imprint","IMPRINT",FACE,{"disambiguationData":[TD([[makeQuery(id+"F6.imprint","IMPRINT",EDGE,{"derivedFrom":sQuery(id+"F6.wireOp",EDGE,"E569.MirrorC")}),-1.0]])]});
            var Q108;
            Q108=makeQuery(id+"F6.imprint","IMPRINT",FACE,{"disambiguationData":[TD([[makeQuery(id+"F6.imprint","IMPRINT",EDGE,{"derivedFrom":sQuery(id+"F6.wireOp",EDGE,"E621.MirrorC")}),-1.0]])]});
            var Q109;
            Q109=makeQuery(id+"F6.imprint","IMPRINT",FACE,{"disambiguationData":[TD([[makeQuery(id+"F6.imprint","IMPRINT",EDGE,{"derivedFrom":sQuery(id+"F6.wireOp",EDGE,"E642.MirrorC")}),-1.0]])]});
            var Q110;
            Q110=makeQuery(id+"F6.imprint","IMPRINT",FACE,{"disambiguationData":[TD([[makeQuery(id+"F6.imprint","IMPRINT",EDGE,{"derivedFrom":sQuery(id+"F6.wireOp",EDGE,"E851.MirrorC")}),-1.0]])]});
            var Q111;
            Q111=makeQuery(id+"F6.imprint","IMPRINT",FACE,{"disambiguationData":[TD([[makeQuery(id+"F6.imprint","IMPRINT",EDGE,{"derivedFrom":sQuery(id+"F6.wireOp",EDGE,"E799.MirrorC")}),-1.0]])]});
            var Q112;
            Q112=makeQuery(id+"F6.imprint","IMPRINT",FACE,{"disambiguationData":[TD([[makeQuery(id+"F6.imprint","IMPRINT",EDGE,{"derivedFrom":sQuery(id+"F6.wireOp",EDGE,"E697.MirrorC")}),-1.0]])]});
            var Q113;
            Q113=makeQuery(id+"F6.imprint","IMPRINT",FACE,{"disambiguationData":[TD([[makeQuery(id+"F6.imprint","IMPRINT",EDGE,{"derivedFrom":sQuery(id+"F6.wireOp",EDGE,"E645.MirrorC")}),-1.0]])]});
            var Q114;
            Q114=makeQuery(id+"F6.imprint","IMPRINT",FACE,{"disambiguationData":[TD([[makeQuery(id+"F6.imprint","IMPRINT",EDGE,{"derivedFrom":sQuery(id+"F6.wireOp",EDGE,"E881.MirrorC")}),-1.0]])]});
            var Q115;
            Q115=makeQuery(id+"F6.imprint","IMPRINT",FACE,{"disambiguationData":[TD([[makeQuery(id+"F6.imprint","IMPRINT",EDGE,{"derivedFrom":sQuery(id+"F6.wireOp",EDGE,"E657.MirrorC")}),-1.0]])]});
            var Q116;
            Q116=makeQuery(id+"F6.imprint","IMPRINT",FACE,{"disambiguationData":[TD([[makeQuery(id+"F6.imprint","IMPRINT",EDGE,{"derivedFrom":sQuery(id+"F6.wireOp",EDGE,"E814.MirrorC")}),-1.0]])]});
            var Q117;
            Q117=makeQuery(id+"F6.imprint","IMPRINT",FACE,{"disambiguationData":[TD([[makeQuery(id+"F6.imprint","IMPRINT",EDGE,{"derivedFrom":sQuery(id+"F6.wireOp",EDGE,"E866.MirrorC")}),-1.0]])]});
            var Q118;
            Q118=makeQuery(id+"F6.imprint","IMPRINT",FACE,{"disambiguationData":[TD([[makeQuery(id+"F6.imprint","IMPRINT",EDGE,{"derivedFrom":sQuery(id+"F6.wireOp",EDGE,"E660.MirrorC")}),-1.0]])]});
            var Q119;
            Q119=makeQuery(id+"F6.imprint","IMPRINT",FACE,{"disambiguationData":[TD([[makeQuery(id+"F6.imprint","IMPRINT",EDGE,{"derivedFrom":sQuery(id+"F6.wireOp",EDGE,"E712.MirrorC")}),-1.0]])]});
            var Q120;
            Q120=makeQuery(id+"F6.imprint","IMPRINT",FACE,{"disambiguationData":[TD([[makeQuery(id+"F6.imprint","IMPRINT",EDGE,{"derivedFrom":sQuery(id+"F6.wireOp",EDGE,"E612.MirrorC")}),-1.0]])]});
            var Q121;
            Q121=makeQuery(id+"F6.imprint","IMPRINT",FACE,{"disambiguationData":[TD([[makeQuery(id+"F6.imprint","IMPRINT",EDGE,{"derivedFrom":sQuery(id+"F6.wireOp",EDGE,"E769.MirrorC")}),-1.0]])]});
            var Q122;
            Q122=makeQuery(id+"F6.imprint","IMPRINT",FACE,{"disambiguationData":[TD([[makeQuery(id+"F6.imprint","IMPRINT",EDGE,{"derivedFrom":sQuery(id+"F6.wireOp",EDGE,"E821.MirrorC")}),-1.0]])]});
            var Q123;
            Q123=makeQuery(id+"F6.imprint","IMPRINT",FACE,{"disambiguationData":[TD([[makeQuery(id+"F6.imprint","IMPRINT",EDGE,{"derivedFrom":sQuery(id+"F6.wireOp",EDGE,"E614.MirrorC")}),-1.0]])]});
            var Q124;
            Q124=makeQuery(id+"F6.imprint","IMPRINT",FACE,{"disambiguationData":[TD([[makeQuery(id+"F6.imprint","IMPRINT",EDGE,{"derivedFrom":sQuery(id+"F6.wireOp",EDGE,"E666.MirrorC")}),-1.0]])]});
            var Q125;
            Q125=makeQuery(id+"F6.imprint","IMPRINT",FACE,{"disambiguationData":[TD([[makeQuery(id+"F6.imprint","IMPRINT",EDGE,{"derivedFrom":sQuery(id+"F6.wireOp",EDGE,"E784.MirrorC")}),-1.0]])]});
            var Q126;
            Q126=makeQuery(id+"F6.imprint","IMPRINT",FACE,{"disambiguationData":[TD([[makeQuery(id+"F6.imprint","IMPRINT",EDGE,{"derivedFrom":sQuery(id+"F6.wireOp",EDGE,"E835.MirrorC")}),-1.0]])]});
            var Q127;
            Q127=makeQuery(id+"F6.imprint","IMPRINT",FACE,{"disambiguationData":[TD([[makeQuery(id+"F6.imprint","IMPRINT",EDGE,{"derivedFrom":sQuery(id+"F6.wireOp",EDGE,"E629.MirrorC")}),-1.0]])]});
            var Q128;
            Q128=makeQuery(id+"F6.imprint","IMPRINT",FACE,{"disambiguationData":[TD([[makeQuery(id+"F6.imprint","IMPRINT",EDGE,{"derivedFrom":sQuery(id+"F6.wireOp",EDGE,"E682.MirrorC")}),-1.0]])]});
            var Q129;
            Q129=makeQuery(id+"F6.imprint","IMPRINT",FACE,{"disambiguationData":[TD([[makeQuery(id+"F6.imprint","IMPRINT",EDGE,{"derivedFrom":sQuery(id+"F6.wireOp",EDGE,"E703.MirrorC")}),-1.0]])]});
            var Q130;
            Q130=makeQuery(id+"F6.imprint","IMPRINT",FACE,{"disambiguationData":[TD([[makeQuery(id+"F6.imprint","IMPRINT",EDGE,{"derivedFrom":sQuery(id+"F6.wireOp",EDGE,"E875.MirrorC")}),-1.0]])]});
            var Q131;
            Q131=makeQuery(id+"F6.imprint","IMPRINT",FACE,{"disambiguationData":[TD([[makeQuery(id+"F6.imprint","IMPRINT",EDGE,{"derivedFrom":sQuery(id+"F6.wireOp",EDGE,"E706.MirrorC")}),-1.0]])]});
            var Q132;
            Q132=makeQuery(id+"F6.imprint","IMPRINT",FACE,{"disambiguationData":[TD([[makeQuery(id+"F6.imprint","IMPRINT",EDGE,{"derivedFrom":sQuery(id+"F6.wireOp",EDGE,"E718.MirrorC")}),-1.0]])]});
            var Q133;
            Q133=makeQuery(id+"F6.imprint","IMPRINT",FACE,{"disambiguationData":[TD([[makeQuery(id+"F6.imprint","IMPRINT",EDGE,{"derivedFrom":sQuery(id+"F6.wireOp",EDGE,"E890.MirrorC")}),-1.0]])]});
            var Q134;
            Q134=makeQuery(id+"F6.imprint","IMPRINT",FACE,{"disambiguationData":[TD([[makeQuery(id+"F6.imprint","IMPRINT",EDGE,{"derivedFrom":sQuery(id+"F6.wireOp",EDGE,"E721.MirrorC")}),-1.0]])]});
            var Q135;
            Q135=makeQuery(id+"F6.imprint","IMPRINT",FACE,{"disambiguationData":[TD([[makeQuery(id+"F6.imprint","IMPRINT",EDGE,{"derivedFrom":sQuery(id+"F6.wireOp",EDGE,"E844.MirrorC")}),-1.0]])]});
            var Q136;
            Q136=makeQuery(id+"F6.imprint","IMPRINT",FACE,{"disambiguationData":[TD([[makeQuery(id+"F6.imprint","IMPRINT",EDGE,{"derivedFrom":sQuery(id+"F6.wireOp",EDGE,"E897.MirrorC")}),-1.0]])]});
            var Q137;
            Q137=makeQuery(id+"F6.imprint","IMPRINT",FACE,{"disambiguationData":[TD([[makeQuery(id+"F6.imprint","IMPRINT",EDGE,{"derivedFrom":sQuery(id+"F6.wireOp",EDGE,"E672.MirrorC")}),-1.0]])]});
            var Q138;
            Q138=makeQuery(id+"F6.imprint","IMPRINT",FACE,{"disambiguationData":[TD([[makeQuery(id+"F6.imprint","IMPRINT",EDGE,{"derivedFrom":sQuery(id+"F6.wireOp",EDGE,"E728.MirrorC")}),-1.0]])]});
            var Q139;
            Q139=makeQuery(id+"F6.imprint","IMPRINT",FACE,{"disambiguationData":[TD([[makeQuery(id+"F6.imprint","IMPRINT",EDGE,{"derivedFrom":sQuery(id+"F6.wireOp",EDGE,"E829.MirrorC")}),-1.0]])]});
            var Q140;
            Q140=makeQuery(id+"F6.imprint","IMPRINT",FACE,{"disambiguationData":[TD([[makeQuery(id+"F6.imprint","IMPRINT",EDGE,{"derivedFrom":sQuery(id+"F6.wireOp",EDGE,"E675.MirrorC")}),-1.0]])]});
            var Q141;
            Q141=makeQuery(id+"F6.imprint","IMPRINT",FACE,{"disambiguationData":[TD([[makeQuery(id+"F6.imprint","IMPRINT",EDGE,{"derivedFrom":sQuery(id+"F6.wireOp",EDGE,"E688.MirrorC")}),-1.0]])]});
            var Q142;
            Q142=makeQuery(id+"F6.imprint","IMPRINT",FACE,{"disambiguationData":[TD([[makeQuery(id+"F6.imprint","IMPRINT",EDGE,{"derivedFrom":sQuery(id+"F6.wireOp",EDGE,"E859.MirrorC")}),-1.0]])]});
            var Q143;
            Q143=makeQuery(id+"F6.imprint","IMPRINT",FACE,{"disambiguationData":[TD([[makeQuery(id+"F6.imprint","IMPRINT",EDGE,{"derivedFrom":sQuery(id+"F6.wireOp",EDGE,"E690.MirrorC")}),-1.0]])]});
            var Q144;
            Q144=makeQuery(id+"F6.imprint","IMPRINT",FACE,{"disambiguationData":[TD([[makeQuery(id+"F6.imprint","IMPRINT",EDGE,{"derivedFrom":sQuery(id+"F6.wireOp",EDGE,"E758.MirrorC")}),-1.0]])]});
            var Q145;
            Q145=makeQuery(id+"F6.imprint","IMPRINT",FACE,{"disambiguationData":[TD([[makeQuery(id+"F6.imprint","IMPRINT",EDGE,{"derivedFrom":sQuery(id+"F6.wireOp",EDGE,"E743.MirrorC")}),-1.0]])]});
            var Q146;
            Q146=makeQuery(id+"F6.imprint","IMPRINT",FACE,{"disambiguationData":[TD([[makeQuery(id+"F6.imprint","IMPRINT",EDGE,{"derivedFrom":sQuery(id+"F6.wireOp",EDGE,"E733.MirrorC")}),-1.0]])]});
            var Q147;
            Q147=makeQuery(id+"F6.imprint","IMPRINT",FACE,{"disambiguationData":[TD([[makeQuery(id+"F6.imprint","IMPRINT",EDGE,{"derivedFrom":sQuery(id+"F6.wireOp",EDGE,"E381.MirrorC")}),-1.0]])]});
            var Q148;
            Q148=makeQuery(id+"F6.imprint","IMPRINT",FACE,{"disambiguationData":[TD([[makeQuery(id+"F6.imprint","IMPRINT",EDGE,{"derivedFrom":sQuery(id+"F6.wireOp",EDGE,"E344.MirrorC")}),-1.0]])]});
            var Q149;
            Q149=makeQuery(id+"F6.imprint","IMPRINT",FACE,{"disambiguationData":[TD([[makeQuery(id+"F6.imprint","IMPRINT",EDGE,{"derivedFrom":sQuery(id+"F6.wireOp",EDGE,"E397.MirrorC")}),-1.0]])]});
            var Q150;
            Q150=makeQuery(id+"F6.imprint","IMPRINT",FACE,{"disambiguationData":[TD([[makeQuery(id+"F6.imprint","IMPRINT",EDGE,{"derivedFrom":sQuery(id+"F6.wireOp",EDGE,"E351.MirrorC")}),-1.0]])]});
            var Q151;
            Q151=makeQuery(id+"F6.imprint","IMPRINT",FACE,{"disambiguationData":[TD([[makeQuery(id+"F6.imprint","IMPRINT",EDGE,{"derivedFrom":sQuery(id+"F6.wireOp",EDGE,"E365.MirrorC")}),-1.0]])]});
            var Q152;
            Q152=makeQuery(id+"F6.imprint","IMPRINT",FACE,{"disambiguationData":[TD([[makeQuery(id+"F6.imprint","IMPRINT",EDGE,{"derivedFrom":sQuery(id+"F6.wireOp",EDGE,"E442.MirrorC")}),-1.0]])]});
            var Q153;
            Q153=makeQuery(id+"F6.imprint","IMPRINT",FACE,{"disambiguationData":[TD([[makeQuery(id+"F6.imprint","IMPRINT",EDGE,{"derivedFrom":sQuery(id+"F6.wireOp",EDGE,"E390.MirrorC")}),-1.0]])]});
            var Q154;
            Q154=makeQuery(id+"F6.imprint","IMPRINT",FACE,{"disambiguationData":[TD([[makeQuery(id+"F6.imprint","IMPRINT",EDGE,{"derivedFrom":sQuery(id+"F6.wireOp",EDGE,"E457.MirrorC")}),-1.0]])]});
            var Q155;
            Q155=makeQuery(id+"F6.imprint","IMPRINT",FACE,{"disambiguationData":[TD([[makeQuery(id+"F6.imprint","IMPRINT",EDGE,{"derivedFrom":sQuery(id+"F6.wireOp",EDGE,"E405.MirrorC")}),-1.0]])]});
            var Q156;
            Q156=makeQuery(id+"F6.imprint","IMPRINT",FACE,{"disambiguationData":[TD([[makeQuery(id+"F6.imprint","IMPRINT",EDGE,{"derivedFrom":sQuery(id+"F6.wireOp",EDGE,"E359.MirrorC")}),-1.0]])]});
            var Q157;
            Q157=makeQuery(id+"F6.imprint","IMPRINT",FACE,{"disambiguationData":[TD([[makeQuery(id+"F6.imprint","IMPRINT",EDGE,{"derivedFrom":sQuery(id+"F6.wireOp",EDGE,"E411.MirrorC")}),-1.0]])]});
            var Q158;
            Q158=makeQuery(id+"F6.imprint","IMPRINT",FACE,{"disambiguationData":[TD([[makeQuery(id+"F6.imprint","IMPRINT",EDGE,{"derivedFrom":sQuery(id+"F6.wireOp",EDGE,"E374.MirrorC")}),-1.0]])]});
            var Q159;
            Q159=makeQuery(id+"F6.imprint","IMPRINT",FACE,{"disambiguationData":[TD([[makeQuery(id+"F6.imprint","IMPRINT",EDGE,{"derivedFrom":sQuery(id+"F6.wireOp",EDGE,"E426.MirrorC")}),-1.0]])]});
            var Q160;
            Q160=makeQuery(id+"F6.imprint","IMPRINT",FACE,{"disambiguationData":[TD([[makeQuery(id+"F6.imprint","IMPRINT",EDGE,{"derivedFrom":sQuery(id+"F6.wireOp",EDGE,"E503.MirrorC")}),-1.0]])]});
            var Q161;
            Q161=makeQuery(id+"F6.imprint","IMPRINT",FACE,{"disambiguationData":[TD([[makeQuery(id+"F6.imprint","IMPRINT",EDGE,{"derivedFrom":sQuery(id+"F6.wireOp",EDGE,"E450.MirrorC")}),-1.0]])]});
            var Q162;
            Q162=makeQuery(id+"F6.imprint","IMPRINT",FACE,{"disambiguationData":[TD([[makeQuery(id+"F6.imprint","IMPRINT",EDGE,{"derivedFrom":sQuery(id+"F6.wireOp",EDGE,"E518.MirrorC")}),-1.0]])]});
            var Q163;
            Q163=makeQuery(id+"F6.imprint","IMPRINT",FACE,{"disambiguationData":[TD([[makeQuery(id+"F6.imprint","IMPRINT",EDGE,{"derivedFrom":sQuery(id+"F6.wireOp",EDGE,"E466.MirrorC")}),-1.0]])]});
            var Q164;
            Q164=makeQuery(id+"F6.imprint","IMPRINT",FACE,{"disambiguationData":[TD([[makeQuery(id+"F6.imprint","IMPRINT",EDGE,{"derivedFrom":sQuery(id+"F6.wireOp",EDGE,"E472.MirrorC")}),-1.0]])]});
            var Q165;
            Q165=makeQuery(id+"F6.imprint","IMPRINT",FACE,{"disambiguationData":[TD([[makeQuery(id+"F6.imprint","IMPRINT",EDGE,{"derivedFrom":sQuery(id+"F6.wireOp",EDGE,"E488.MirrorC")}),-1.0]])]});
            var Q166;
            Q166=makeQuery(id+"F6.imprint","IMPRINT",FACE,{"disambiguationData":[TD([[makeQuery(id+"F6.imprint","IMPRINT",EDGE,{"derivedFrom":sQuery(id+"F6.wireOp",EDGE,"E435.MirrorC")}),-1.0]])]});
            var Q167;
            Q167=makeQuery(id+"F6.imprint","IMPRINT",FACE,{"disambiguationData":[TD([[makeQuery(id+"F6.imprint","IMPRINT",EDGE,{"derivedFrom":sQuery(id+"F6.wireOp",EDGE,"E564.MirrorC")}),-1.0]])]});
            var Q168;
            Q168=makeQuery(id+"F6.imprint","IMPRINT",FACE,{"disambiguationData":[TD([[makeQuery(id+"F6.imprint","IMPRINT",EDGE,{"derivedFrom":sQuery(id+"F6.wireOp",EDGE,"E511.MirrorC")}),-1.0]])]});
            var Q169;
            Q169=makeQuery(id+"F6.imprint","IMPRINT",FACE,{"disambiguationData":[TD([[makeQuery(id+"F6.imprint","IMPRINT",EDGE,{"derivedFrom":sQuery(id+"F6.wireOp",EDGE,"E527.MirrorC")}),-1.0]])]});
            var Q170;
            Q170=makeQuery(id+"F6.imprint","IMPRINT",FACE,{"disambiguationData":[TD([[makeQuery(id+"F6.imprint","IMPRINT",EDGE,{"derivedFrom":sQuery(id+"F6.wireOp",EDGE,"E580.MirrorC")}),-1.0]])]});
            var Q171;
            Q171=makeQuery(id+"F6.imprint","IMPRINT",FACE,{"disambiguationData":[TD([[makeQuery(id+"F6.imprint","IMPRINT",EDGE,{"derivedFrom":sQuery(id+"F6.wireOp",EDGE,"E481.MirrorC")}),-1.0]])]});
            var Q172;
            Q172=makeQuery(id+"F6.imprint","IMPRINT",FACE,{"disambiguationData":[TD([[makeQuery(id+"F6.imprint","IMPRINT",EDGE,{"derivedFrom":sQuery(id+"F6.wireOp",EDGE,"E534.MirrorC")}),-1.0]])]});
            var Q173;
            Q173=makeQuery(id+"F6.imprint","IMPRINT",FACE,{"disambiguationData":[TD([[makeQuery(id+"F6.imprint","IMPRINT",EDGE,{"derivedFrom":sQuery(id+"F6.wireOp",EDGE,"E497.MirrorC")}),-1.0]])]});
            var Q174;
            Q174=makeQuery(id+"F6.imprint","IMPRINT",FACE,{"disambiguationData":[TD([[makeQuery(id+"F6.imprint","IMPRINT",EDGE,{"derivedFrom":sQuery(id+"F6.wireOp",EDGE,"E549.MirrorC")}),-1.0]])]});
            var Q175;
            Q175=makeQuery(id+"F6.imprint","IMPRINT",FACE,{"disambiguationData":[TD([[makeQuery(id+"F6.imprint","IMPRINT",EDGE,{"derivedFrom":sQuery(id+"F6.wireOp",EDGE,"E640.MirrorC")}),-1.0]])]});
            var Q176;
            Q176=makeQuery(id+"F6.imprint","IMPRINT",FACE,{"disambiguationData":[TD([[makeQuery(id+"F6.imprint","IMPRINT",EDGE,{"derivedFrom":sQuery(id+"F6.wireOp",EDGE,"E589.MirrorC")}),-1.0]])]});
            var Q177;
            Q177=makeQuery(id+"F6.imprint","IMPRINT",FACE,{"disambiguationData":[TD([[makeQuery(id+"F6.imprint","IMPRINT",EDGE,{"derivedFrom":sQuery(id+"F6.wireOp",EDGE,"E379.MirrorC")}),-1.0]])]});
            var Q178;
            Q178=makeQuery(id+"F6.imprint","IMPRINT",FACE,{"disambiguationData":[TD([[makeQuery(id+"F6.imprint","IMPRINT",EDGE,{"derivedFrom":sQuery(id+"F6.wireOp",EDGE,"E603.MirrorC")}),-1.0]])]});
            var Q179;
            Q179=makeQuery(id+"F6.imprint","IMPRINT",FACE,{"disambiguationData":[TD([[makeQuery(id+"F6.imprint","IMPRINT",EDGE,{"derivedFrom":sQuery(id+"F6.wireOp",EDGE,"E655.MirrorC")}),-1.0]])]});
            var Q180;
            Q180=makeQuery(id+"F6.imprint","IMPRINT",FACE,{"disambiguationData":[TD([[makeQuery(id+"F6.imprint","IMPRINT",EDGE,{"derivedFrom":sQuery(id+"F6.wireOp",EDGE,"E395.MirrorC")}),-1.0]])]});
            var Q181;
            Q181=makeQuery(id+"F6.imprint","IMPRINT",FACE,{"disambiguationData":[TD([[makeQuery(id+"F6.imprint","IMPRINT",EDGE,{"derivedFrom":sQuery(id+"F6.wireOp",EDGE,"E342.MirrorC")}),-1.0]])]});
            var Q182;
            Q182=makeQuery(id+"F6.imprint","IMPRINT",FACE,{"disambiguationData":[TD([[makeQuery(id+"F6.imprint","IMPRINT",EDGE,{"derivedFrom":sQuery(id+"F6.wireOp",EDGE,"E610.MirrorC")}),-1.0]])]});
            var Q183;
            Q183=makeQuery(id+"F6.imprint","IMPRINT",FACE,{"disambiguationData":[TD([[makeQuery(id+"F6.imprint","IMPRINT",EDGE,{"derivedFrom":sQuery(id+"F6.wireOp",EDGE,"E595.MirrorC")}),-1.0]])]});
            var Q184;
            Q184=makeQuery(id+"F6.imprint","IMPRINT",FACE,{"disambiguationData":[TD([[makeQuery(id+"F6.imprint","IMPRINT",EDGE,{"derivedFrom":sQuery(id+"F6.wireOp",EDGE,"E349.MirrorC")}),-1.0]])]});
            var Q185;
            Q185=makeQuery(id+"F6.imprint","IMPRINT",FACE,{"disambiguationData":[TD([[makeQuery(id+"F6.imprint","IMPRINT",EDGE,{"derivedFrom":sQuery(id+"F6.wireOp",EDGE,"E625.MirrorC")}),-1.0]])]});
            var Q186;
            Q186=makeQuery(id+"F6.imprint","IMPRINT",FACE,{"disambiguationData":[TD([[makeQuery(id+"F6.imprint","IMPRINT",EDGE,{"derivedFrom":sQuery(id+"F6.wireOp",EDGE,"E573.MirrorC")}),-1.0]])]});
            var Q187;
            Q187=makeQuery(id+"F6.imprint","IMPRINT",FACE,{"disambiguationData":[TD([[makeQuery(id+"F6.imprint","IMPRINT",EDGE,{"derivedFrom":sQuery(id+"F6.wireOp",EDGE,"E363.MirrorC")}),-1.0]])]});
            var Q188;
            Q188=makeQuery(id+"F6.imprint","IMPRINT",FACE,{"disambiguationData":[TD([[makeQuery(id+"F6.imprint","IMPRINT",EDGE,{"derivedFrom":sQuery(id+"F6.wireOp",EDGE,"E558.MirrorC")}),-1.0]])]});
            var Q189;
            Q189=makeQuery(id+"F6.imprint","IMPRINT",FACE,{"disambiguationData":[TD([[makeQuery(id+"F6.imprint","IMPRINT",EDGE,{"derivedFrom":sQuery(id+"F6.wireOp",EDGE,"E648.MirrorC")}),-1.0]])]});
            var Q190;
            Q190=makeQuery(id+"F6.imprint","IMPRINT",FACE,{"disambiguationData":[TD([[makeQuery(id+"F6.imprint","IMPRINT",EDGE,{"derivedFrom":sQuery(id+"F6.wireOp",EDGE,"E701.MirrorC")}),-1.0]])]});
            var Q191;
            Q191=makeQuery(id+"F6.imprint","IMPRINT",FACE,{"disambiguationData":[TD([[makeQuery(id+"F6.imprint","IMPRINT",EDGE,{"derivedFrom":sQuery(id+"F6.wireOp",EDGE,"E388.MirrorC")}),-1.0]])]});
            var Q192;
            Q192=makeQuery(id+"F6.imprint","IMPRINT",FACE,{"disambiguationData":[TD([[makeQuery(id+"F6.imprint","IMPRINT",EDGE,{"derivedFrom":sQuery(id+"F6.wireOp",EDGE,"E440.MirrorC")}),-1.0]])]});
            var Q193;
            Q193=makeQuery(id+"F6.imprint","IMPRINT",FACE,{"disambiguationData":[TD([[makeQuery(id+"F6.imprint","IMPRINT",EDGE,{"derivedFrom":sQuery(id+"F6.wireOp",EDGE,"E716.MirrorC")}),-1.0]])]});
            var Q194;
            Q194=makeQuery(id+"F6.imprint","IMPRINT",FACE,{"disambiguationData":[TD([[makeQuery(id+"F6.imprint","IMPRINT",EDGE,{"derivedFrom":sQuery(id+"F6.wireOp",EDGE,"E455.MirrorC")}),-1.0]])]});
            var Q195;
            Q195=makeQuery(id+"F6.imprint","IMPRINT",FACE,{"disambiguationData":[TD([[makeQuery(id+"F6.imprint","IMPRINT",EDGE,{"derivedFrom":sQuery(id+"F6.wireOp",EDGE,"E403.MirrorC")}),-1.0]])]});
            var Q196;
            Q196=makeQuery(id+"F6.imprint","IMPRINT",FACE,{"disambiguationData":[TD([[makeQuery(id+"F6.imprint","IMPRINT",EDGE,{"derivedFrom":sQuery(id+"F6.wireOp",EDGE,"E618.MirrorC")}),-1.0]])]});
            var Q197;
            Q197=makeQuery(id+"F6.imprint","IMPRINT",FACE,{"disambiguationData":[TD([[makeQuery(id+"F6.imprint","IMPRINT",EDGE,{"derivedFrom":sQuery(id+"F6.wireOp",EDGE,"E670.MirrorC")}),-1.0]])]});
            var Q198;
            Q198=makeQuery(id+"F6.imprint","IMPRINT",FACE,{"disambiguationData":[TD([[makeQuery(id+"F6.imprint","IMPRINT",EDGE,{"derivedFrom":sQuery(id+"F6.wireOp",EDGE,"E357.MirrorC")}),-1.0]])]});
            var Q199;
            Q199=makeQuery(id+"F6.imprint","IMPRINT",FACE,{"disambiguationData":[TD([[makeQuery(id+"F6.imprint","IMPRINT",EDGE,{"derivedFrom":sQuery(id+"F6.wireOp",EDGE,"E409.MirrorC")}),-1.0]])]});
            var Q200;
            Q200=makeQuery(id+"F6.imprint","IMPRINT",FACE,{"disambiguationData":[TD([[makeQuery(id+"F6.imprint","IMPRINT",EDGE,{"derivedFrom":sQuery(id+"F6.wireOp",EDGE,"E686.MirrorC")}),-1.0]])]});
            var Q201;
            Q201=makeQuery(id+"F6.imprint","IMPRINT",FACE,{"disambiguationData":[TD([[makeQuery(id+"F6.imprint","IMPRINT",EDGE,{"derivedFrom":sQuery(id+"F6.wireOp",EDGE,"E633.MirrorC")}),-1.0]])]});
            var Q202;
            Q202=makeQuery(id+"F6.imprint","IMPRINT",FACE,{"disambiguationData":[TD([[makeQuery(id+"F6.imprint","IMPRINT",EDGE,{"derivedFrom":sQuery(id+"F6.wireOp",EDGE,"E372.MirrorC")}),-1.0]])]});
            var Q203;
            Q203=makeQuery(id+"F6.imprint","IMPRINT",FACE,{"disambiguationData":[TD([[makeQuery(id+"F6.imprint","IMPRINT",EDGE,{"derivedFrom":sQuery(id+"F6.wireOp",EDGE,"E424.MirrorC")}),-1.0]])]});
            var Q204;
            Q204=makeQuery(id+"F6.imprint","IMPRINT",FACE,{"disambiguationData":[TD([[makeQuery(id+"F6.imprint","IMPRINT",EDGE,{"derivedFrom":sQuery(id+"F6.wireOp",EDGE,"E516.MirrorC")}),-1.0]])]});
            var Q205;
            Q205=makeQuery(id+"F6.imprint","IMPRINT",FACE,{"disambiguationData":[TD([[makeQuery(id+"F6.imprint","IMPRINT",EDGE,{"derivedFrom":sQuery(id+"F6.wireOp",EDGE,"E464.MirrorC")}),-1.0]])]});
            var Q206;
            Q206=makeQuery(id+"F6.imprint","IMPRINT",FACE,{"disambiguationData":[TD([[makeQuery(id+"F6.imprint","IMPRINT",EDGE,{"derivedFrom":sQuery(id+"F6.wireOp",EDGE,"E725.MirrorC")}),-1.0]])]});
            var Q207;
            Q207=makeQuery(id+"F6.imprint","IMPRINT",FACE,{"disambiguationData":[TD([[makeQuery(id+"F6.imprint","IMPRINT",EDGE,{"derivedFrom":sQuery(id+"F6.wireOp",EDGE,"E479.MirrorC")}),-1.0]])]});
            var Q208;
            Q208=makeQuery(id+"F6.imprint","IMPRINT",FACE,{"disambiguationData":[TD([[makeQuery(id+"F6.imprint","IMPRINT",EDGE,{"derivedFrom":sQuery(id+"F6.wireOp",EDGE,"E532.MirrorC")}),-1.0]])]});
            var Q209;
            Q209=makeQuery(id+"F6.imprint","IMPRINT",FACE,{"disambiguationData":[TD([[makeQuery(id+"F6.imprint","IMPRINT",EDGE,{"derivedFrom":sQuery(id+"F6.wireOp",EDGE,"E732.MirrorC")}),-1.0]])]});
            var Q210;
            Q210=makeQuery(id+"F6.imprint","IMPRINT",FACE,{"disambiguationData":[TD([[makeQuery(id+"F6.imprint","IMPRINT",EDGE,{"derivedFrom":sQuery(id+"F6.wireOp",EDGE,"E486.MirrorC")}),-1.0]])]});
            var Q211;
            Q211=makeQuery(id+"F6.imprint","IMPRINT",FACE,{"disambiguationData":[TD([[makeQuery(id+"F6.imprint","IMPRINT",EDGE,{"derivedFrom":sQuery(id+"F6.wireOp",EDGE,"E679.MirrorC")}),-1.0]])]});
            var Q212;
            Q212=makeQuery(id+"F6.imprint","IMPRINT",FACE,{"disambiguationData":[TD([[makeQuery(id+"F6.imprint","IMPRINT",EDGE,{"derivedFrom":sQuery(id+"F6.wireOp",EDGE,"E418.MirrorC")}),-1.0]])]});
            var Q213;
            Q213=makeQuery(id+"F6.imprint","IMPRINT",FACE,{"disambiguationData":[TD([[makeQuery(id+"F6.imprint","IMPRINT",EDGE,{"derivedFrom":sQuery(id+"F6.wireOp",EDGE,"E470.MirrorC")}),-1.0]])]});
            var Q214;
            Q214=makeQuery(id+"F6.imprint","IMPRINT",FACE,{"disambiguationData":[TD([[makeQuery(id+"F6.imprint","IMPRINT",EDGE,{"derivedFrom":sQuery(id+"F6.wireOp",EDGE,"E694.MirrorC")}),-1.0]])]});
            var Q215;
            Q215=makeQuery(id+"F6.imprint","IMPRINT",FACE,{"disambiguationData":[TD([[makeQuery(id+"F6.imprint","IMPRINT",EDGE,{"derivedFrom":sQuery(id+"F6.wireOp",EDGE,"E449.MirrorC")}),-1.0]])]});
            var Q216;
            Q216=makeQuery(id+"F6.imprint","IMPRINT",FACE,{"disambiguationData":[TD([[makeQuery(id+"F6.imprint","IMPRINT",EDGE,{"derivedFrom":sQuery(id+"F6.wireOp",EDGE,"E501.MirrorC")}),-1.0]])]});
            var Q217;
            Q217=makeQuery(id+"F6.imprint","IMPRINT",FACE,{"disambiguationData":[TD([[makeQuery(id+"F6.imprint","IMPRINT",EDGE,{"derivedFrom":sQuery(id+"F6.wireOp",EDGE,"E433.MirrorC")}),-1.0]])]});
            var Q218;
            Q218=makeQuery(id+"F6.imprint","IMPRINT",FACE,{"disambiguationData":[TD([[makeQuery(id+"F6.imprint","IMPRINT",EDGE,{"derivedFrom":sQuery(id+"F6.wireOp",EDGE,"E578.MirrorC")}),-1.0]])]});
            var Q219;
            Q219=makeQuery(id+"F6.imprint","IMPRINT",FACE,{"disambiguationData":[TD([[makeQuery(id+"F6.imprint","IMPRINT",EDGE,{"derivedFrom":sQuery(id+"F6.wireOp",EDGE,"E525.MirrorC")}),-1.0]])]});
            var Q220;
            Q220=makeQuery(id+"F6.imprint","IMPRINT",FACE,{"disambiguationData":[TD([[makeQuery(id+"F6.imprint","IMPRINT",EDGE,{"derivedFrom":sQuery(id+"F6.wireOp",EDGE,"E747.MirrorC")}),-1.0]])]});
            var Q221;
            Q221=makeQuery(id+"F6.imprint","IMPRINT",FACE,{"disambiguationData":[TD([[makeQuery(id+"F6.imprint","IMPRINT",EDGE,{"derivedFrom":sQuery(id+"F6.wireOp",EDGE,"E541.MirrorC")}),-1.0]])]});
            var Q222;
            Q222=makeQuery(id+"F6.imprint","IMPRINT",FACE,{"disambiguationData":[TD([[makeQuery(id+"F6.imprint","IMPRINT",EDGE,{"derivedFrom":sQuery(id+"F6.wireOp",EDGE,"E593.MirrorC")}),-1.0]])]});
            var Q223;
            Q223=makeQuery(id+"F6.imprint","IMPRINT",FACE,{"disambiguationData":[TD([[makeQuery(id+"F6.imprint","IMPRINT",EDGE,{"derivedFrom":sQuery(id+"F6.wireOp",EDGE,"E495.MirrorC")}),-1.0]])]});
            var Q224;
            Q224=makeQuery(id+"F6.imprint","IMPRINT",FACE,{"disambiguationData":[TD([[makeQuery(id+"F6.imprint","IMPRINT",EDGE,{"derivedFrom":sQuery(id+"F6.wireOp",EDGE,"E547.MirrorC")}),-1.0]])]});
            var Q225;
            Q225=makeQuery(id+"F6.imprint","IMPRINT",FACE,{"disambiguationData":[TD([[makeQuery(id+"F6.imprint","IMPRINT",EDGE,{"derivedFrom":sQuery(id+"F6.wireOp",EDGE,"E509.MirrorC")}),-1.0]])]});
            var Q226;
            Q226=makeQuery(id+"F6.imprint","IMPRINT",FACE,{"disambiguationData":[TD([[makeQuery(id+"F6.imprint","IMPRINT",EDGE,{"derivedFrom":sQuery(id+"F6.wireOp",EDGE,"E562.MirrorC")}),-1.0]])]});
            var Q227;
            Q227=makeQuery(id+"F6.imprint","IMPRINT",FACE,{"disambiguationData":[TD([[makeQuery(id+"F6.imprint","IMPRINT",EDGE,{"derivedFrom":sQuery(id+"F6.wireOp",EDGE,"E613.MirrorC")}),-1.0]])]});
            var Q228;
            Q228=makeQuery(id+"F6.imprint","IMPRINT",FACE,{"disambiguationData":[TD([[makeQuery(id+"F6.imprint","IMPRINT",EDGE,{"derivedFrom":sQuery(id+"F6.wireOp",EDGE,"E628.MirrorC")}),-1.0]])]});
            var Q229;
            Q229=makeQuery(id+"F6.imprint","IMPRINT",FACE,{"disambiguationData":[TD([[makeQuery(id+"F6.imprint","IMPRINT",EDGE,{"derivedFrom":sQuery(id+"F6.wireOp",EDGE,"E584.MirrorC")}),-1.0]])]});
            var Q230;
            Q230=makeQuery(id+"F6.imprint","IMPRINT",FACE,{"disambiguationData":[TD([[makeQuery(id+"F6.imprint","IMPRINT",EDGE,{"derivedFrom":sQuery(id+"F6.wireOp",EDGE,"E599.MirrorC")}),-1.0]])]});
            var Q231;
            Q231=makeQuery(id+"F6.imprint","IMPRINT",FACE,{"disambiguationData":[TD([[makeQuery(id+"F6.imprint","IMPRINT",EDGE,{"derivedFrom":sQuery(id+"F6.wireOp",EDGE,"E674.MirrorC")}),-1.0]])]});
            var Q232;
            Q232=makeQuery(id+"F6.imprint","IMPRINT",FACE,{"disambiguationData":[TD([[makeQuery(id+"F6.imprint","IMPRINT",EDGE,{"derivedFrom":sQuery(id+"F6.wireOp",EDGE,"E644.MirrorC")}),-1.0]])]});
            var Q233;
            Q233=makeQuery(id+"F6.imprint","IMPRINT",FACE,{"disambiguationData":[TD([[makeQuery(id+"F6.imprint","IMPRINT",EDGE,{"derivedFrom":sQuery(id+"F6.wireOp",EDGE,"E659.MirrorC")}),-1.0]])]});
            var Q234;
            Q234=makeQuery(id+"F6.imprint","IMPRINT",FACE,{"disambiguationData":[TD([[makeQuery(id+"F6.imprint","IMPRINT",EDGE,{"derivedFrom":sQuery(id+"F6.wireOp",EDGE,"E735.MirrorC")}),-1.0]])]});
            var Q235;
            Q235=makeQuery(id+"F6.imprint","IMPRINT",FACE,{"disambiguationData":[TD([[makeQuery(id+"F6.imprint","IMPRINT",EDGE,{"derivedFrom":sQuery(id+"F6.wireOp",EDGE,"E705.MirrorC")}),-1.0]])]});
            var Q236;
            Q236=makeQuery(id+"F6.imprint","IMPRINT",FACE,{"disambiguationData":[TD([[makeQuery(id+"F6.imprint","IMPRINT",EDGE,{"derivedFrom":sQuery(id+"F6.wireOp",EDGE,"E720.MirrorC")}),-1.0]])]});
            var Q237;
            Q237=makeQuery(id+"F6.imprint","IMPRINT",FACE,{"disambiguationData":[TD([[makeQuery(id+"F6.imprint","IMPRINT",EDGE,{"derivedFrom":sQuery(id+"F6.wireOp",EDGE,"E766.MirrorC")}),-1.0]])]});
            var Q238;
            Q238=makeQuery(id+"F6.imprint","IMPRINT",FACE,{"disambiguationData":[TD([[makeQuery(id+"F6.imprint","IMPRINT",EDGE,{"derivedFrom":sQuery(id+"F6.wireOp",EDGE,"E781.MirrorC")}),-1.0]])]});
            var Q239;
            Q239=makeQuery(id+"F6.imprint","IMPRINT",FACE,{"disambiguationData":[TD([[makeQuery(id+"F6.imprint","IMPRINT",EDGE,{"derivedFrom":sQuery(id+"F6.wireOp",EDGE,"E751.MirrorC")}),-1.0]])]});
            var Q240;
            Q240=makeQuery(id+"F6.imprint","IMPRINT",FACE,{"disambiguationData":[TD([[makeQuery(id+"F6.imprint","IMPRINT",EDGE,{"derivedFrom":sQuery(id+"F6.wireOp",EDGE,"E826.MirrorC")}),-1.0]])]});
            var Q241;
            Q241=makeQuery(id+"F6.imprint","IMPRINT",FACE,{"disambiguationData":[TD([[makeQuery(id+"F6.imprint","IMPRINT",EDGE,{"derivedFrom":sQuery(id+"F6.wireOp",EDGE,"E856.MirrorC")}),-1.0]])]});
            var Q242;
            Q242=makeQuery(id+"F6.imprint","IMPRINT",FACE,{"disambiguationData":[TD([[makeQuery(id+"F6.imprint","IMPRINT",EDGE,{"derivedFrom":sQuery(id+"F6.wireOp",EDGE,"E841.MirrorC")}),-1.0]])]});
            var Q243;
            Q243=makeQuery(id+"F6.imprint","IMPRINT",FACE,{"disambiguationData":[TD([[makeQuery(id+"F6.imprint","IMPRINT",EDGE,{"derivedFrom":sQuery(id+"F6.wireOp",EDGE,"E796.MirrorC")}),-1.0]])]});
            var Q244;
            Q244=makeQuery(id+"F6.imprint","IMPRINT",FACE,{"disambiguationData":[TD([[makeQuery(id+"F6.imprint","IMPRINT",EDGE,{"derivedFrom":sQuery(id+"F6.wireOp",EDGE,"E382.MirrorC")}),-1.0]])]});
            var Q245;
            Q245=makeQuery(id+"F6.imprint","IMPRINT",FACE,{"disambiguationData":[TD([[makeQuery(id+"F6.imprint","IMPRINT",EDGE,{"derivedFrom":sQuery(id+"F6.wireOp",EDGE,"E903.MirrorC")}),-1.0]])]});
            var Q246;
            Q246=makeQuery(id+"F6.imprint","IMPRINT",FACE,{"disambiguationData":[TD([[makeQuery(id+"F6.imprint","IMPRINT",EDGE,{"derivedFrom":sQuery(id+"F6.wireOp",EDGE,"E345.MirrorC")}),-1.0]])]});
            var Q247;
            Q247=makeQuery(id+"F6.imprint","IMPRINT",FACE,{"disambiguationData":[TD([[makeQuery(id+"F6.imprint","IMPRINT",EDGE,{"derivedFrom":sQuery(id+"F6.wireOp",EDGE,"E398.MirrorC")}),-1.0]])]});
            var Q248;
            Q248=makeQuery(id+"F6.imprint","IMPRINT",FACE,{"disambiguationData":[TD([[makeQuery(id+"F6.imprint","IMPRINT",EDGE,{"derivedFrom":sQuery(id+"F6.wireOp",EDGE,"E352.MirrorC")}),-1.0]])]});
            var Q249;
            Q249=makeQuery(id+"F6.imprint","IMPRINT",FACE,{"disambiguationData":[TD([[makeQuery(id+"F6.imprint","IMPRINT",EDGE,{"derivedFrom":sQuery(id+"F6.wireOp",EDGE,"E872.MirrorC")}),-1.0]])]});
            var Q250;
            Q250=makeQuery(id+"F6.imprint","IMPRINT",FACE,{"disambiguationData":[TD([[makeQuery(id+"F6.imprint","IMPRINT",EDGE,{"derivedFrom":sQuery(id+"F6.wireOp",EDGE,"E366.MirrorC")}),-1.0]])]});
            var Q251;
            Q251=makeQuery(id+"F6.imprint","IMPRINT",FACE,{"disambiguationData":[TD([[makeQuery(id+"F6.imprint","IMPRINT",EDGE,{"derivedFrom":sQuery(id+"F6.wireOp",EDGE,"E887.MirrorC")}),-1.0]])]});
            var Q252;
            Q252=makeQuery(id+"F6.imprint","IMPRINT",FACE,{"disambiguationData":[TD([[makeQuery(id+"F6.imprint","IMPRINT",EDGE,{"derivedFrom":sQuery(id+"F6.wireOp",EDGE,"E443.MirrorC")}),-1.0]])]});
            var Q253;
            Q253=makeQuery(id+"F6.imprint","IMPRINT",FACE,{"disambiguationData":[TD([[makeQuery(id+"F6.imprint","IMPRINT",EDGE,{"derivedFrom":sQuery(id+"F6.wireOp",EDGE,"E391.MirrorC")}),-1.0]])]});
            var Q254;
            Q254=makeQuery(id+"F6.imprint","IMPRINT",FACE,{"disambiguationData":[TD([[makeQuery(id+"F6.imprint","IMPRINT",EDGE,{"derivedFrom":sQuery(id+"F6.wireOp",EDGE,"E458.MirrorC")}),-1.0]])]});
            var Q255;
            Q255=makeQuery(id+"F6.imprint","IMPRINT",FACE,{"disambiguationData":[TD([[makeQuery(id+"F6.imprint","IMPRINT",EDGE,{"derivedFrom":sQuery(id+"F6.wireOp",EDGE,"E406.MirrorC")}),-1.0]])]});
            var Q256;
            Q256=makeQuery(id+"F6.imprint","IMPRINT",FACE,{"disambiguationData":[TD([[makeQuery(id+"F6.imprint","IMPRINT",EDGE,{"derivedFrom":sQuery(id+"F6.wireOp",EDGE,"E360.MirrorC")}),-1.0]])]});
            var Q257;
            Q257=makeQuery(id+"F6.imprint","IMPRINT",FACE,{"disambiguationData":[TD([[makeQuery(id+"F6.imprint","IMPRINT",EDGE,{"derivedFrom":sQuery(id+"F6.wireOp",EDGE,"E412.MirrorC")}),-1.0]])]});
            var Q258;
            Q258=makeQuery(id+"F6.imprint","IMPRINT",FACE,{"disambiguationData":[TD([[makeQuery(id+"F6.imprint","IMPRINT",EDGE,{"derivedFrom":sQuery(id+"F6.wireOp",EDGE,"E375.MirrorC")}),-1.0]])]});
            var Q259;
            Q259=makeQuery(id+"F6.imprint","IMPRINT",FACE,{"disambiguationData":[TD([[makeQuery(id+"F6.imprint","IMPRINT",EDGE,{"derivedFrom":sQuery(id+"F6.wireOp",EDGE,"E427.MirrorC")}),-1.0]])]});
            var Q260;
            Q260=makeQuery(id+"F6.imprint","IMPRINT",FACE,{"disambiguationData":[TD([[makeQuery(id+"F6.imprint","IMPRINT",EDGE,{"derivedFrom":sQuery(id+"F6.wireOp",EDGE,"E752.MirrorC")}),-1.0]])]});
            var Q261;
            Q261=makeQuery(id+"F6.imprint","IMPRINT",FACE,{"disambiguationData":[TD([[makeQuery(id+"F6.imprint","IMPRINT",EDGE,{"derivedFrom":sQuery(id+"F6.wireOp",EDGE,"E804.MirrorC")}),-1.0]])]});
            var Q262;
            Q262=makeQuery(id+"F6.imprint","IMPRINT",FACE,{"disambiguationData":[TD([[makeQuery(id+"F6.imprint","IMPRINT",EDGE,{"derivedFrom":sQuery(id+"F6.wireOp",EDGE,"E767.MirrorC")}),-1.0]])]});
            var Q263;
            Q263=makeQuery(id+"F6.imprint","IMPRINT",FACE,{"disambiguationData":[TD([[makeQuery(id+"F6.imprint","IMPRINT",EDGE,{"derivedFrom":sQuery(id+"F6.wireOp",EDGE,"E819.MirrorC")}),-1.0]])]});
            var Q264;
            Q264=makeQuery(id+"F6.imprint","IMPRINT",FACE,{"disambiguationData":[TD([[makeQuery(id+"F6.imprint","IMPRINT",EDGE,{"derivedFrom":sQuery(id+"F6.wireOp",EDGE,"E749.MirrorC")}),-1.0]])]});
            var Q265;
            Q265=makeQuery(id+"F6.imprint","IMPRINT",FACE,{"disambiguationData":[TD([[makeQuery(id+"F6.imprint","IMPRINT",EDGE,{"derivedFrom":sQuery(id+"F6.wireOp",EDGE,"E774.MirrorC")}),-1.0]])]});
            var Q266;
            Q266=makeQuery(id+"F6.imprint","IMPRINT",FACE,{"disambiguationData":[TD([[makeQuery(id+"F6.imprint","IMPRINT",EDGE,{"derivedFrom":sQuery(id+"F6.wireOp",EDGE,"E789.MirrorC")}),-1.0]])]});
            var Q267;
            Q267=makeQuery(id+"F6.imprint","IMPRINT",FACE,{"disambiguationData":[TD([[makeQuery(id+"F6.imprint","IMPRINT",EDGE,{"derivedFrom":sQuery(id+"F6.wireOp",EDGE,"E736.MirrorC")}),-1.0]])]});
            var Q268;
            Q268=makeQuery(id+"F6.imprint","IMPRINT",FACE,{"disambiguationData":[TD([[makeQuery(id+"F6.imprint","IMPRINT",EDGE,{"derivedFrom":sQuery(id+"F6.wireOp",EDGE,"E812.MirrorC")}),-1.0]])]});
            var Q269;
            Q269=makeQuery(id+"F6.imprint","IMPRINT",FACE,{"disambiguationData":[TD([[makeQuery(id+"F6.imprint","IMPRINT",EDGE,{"derivedFrom":sQuery(id+"F6.wireOp",EDGE,"E864.MirrorC")}),-1.0]])]});
            var Q270;
            Q270=makeQuery(id+"F6.imprint","IMPRINT",FACE,{"disambiguationData":[TD([[makeQuery(id+"F6.imprint","IMPRINT",EDGE,{"derivedFrom":sQuery(id+"F6.wireOp",EDGE,"E794.MirrorC")}),-1.0]])]});
            var Q271;
            Q271=makeQuery(id+"F6.imprint","IMPRINT",FACE,{"disambiguationData":[TD([[makeQuery(id+"F6.imprint","IMPRINT",EDGE,{"derivedFrom":sQuery(id+"F6.wireOp",EDGE,"E879.MirrorC")}),-1.0]])]});
            var Q272;
            Q272=makeQuery(id+"F6.imprint","IMPRINT",FACE,{"disambiguationData":[TD([[makeQuery(id+"F6.imprint","IMPRINT",EDGE,{"derivedFrom":sQuery(id+"F6.wireOp",EDGE,"E827.MirrorC")}),-1.0]])]});
            var Q273;
            Q273=makeQuery(id+"F6.imprint","IMPRINT",FACE,{"disambiguationData":[TD([[makeQuery(id+"F6.imprint","IMPRINT",EDGE,{"derivedFrom":sQuery(id+"F6.wireOp",EDGE,"E810.MirrorC")}),-1.0]])]});
            var Q274;
            Q274=makeQuery(id+"F6.imprint","IMPRINT",FACE,{"disambiguationData":[TD([[makeQuery(id+"F6.imprint","IMPRINT",EDGE,{"derivedFrom":sQuery(id+"F6.wireOp",EDGE,"E782.MirrorC")}),-1.0]])]});
            var Q275;
            Q275=makeQuery(id+"F6.imprint","IMPRINT",FACE,{"disambiguationData":[TD([[makeQuery(id+"F6.imprint","IMPRINT",EDGE,{"derivedFrom":sQuery(id+"F6.wireOp",EDGE,"E833.MirrorC")}),-1.0]])]});
            var Q276;
            Q276=makeQuery(id+"F6.imprint","IMPRINT",FACE,{"disambiguationData":[TD([[makeQuery(id+"F6.imprint","IMPRINT",EDGE,{"derivedFrom":sQuery(id+"F6.wireOp",EDGE,"E764.MirrorC")}),-1.0]])]});
            var Q277;
            Q277=makeQuery(id+"F6.imprint","IMPRINT",FACE,{"disambiguationData":[TD([[makeQuery(id+"F6.imprint","IMPRINT",EDGE,{"derivedFrom":sQuery(id+"F6.wireOp",EDGE,"E849.MirrorC")}),-1.0]])]});
            var Q278;
            Q278=makeQuery(id+"F6.imprint","IMPRINT",FACE,{"disambiguationData":[TD([[makeQuery(id+"F6.imprint","IMPRINT",EDGE,{"derivedFrom":sQuery(id+"F6.wireOp",EDGE,"E797.MirrorC")}),-1.0]])]});
            var Q279;
            Q279=makeQuery(id+"F6.imprint","IMPRINT",FACE,{"disambiguationData":[TD([[makeQuery(id+"F6.imprint","IMPRINT",EDGE,{"derivedFrom":sQuery(id+"F6.wireOp",EDGE,"E779.MirrorC")}),-1.0]])]});
            var Q280;
            Q280=makeQuery(id+"F6.imprint","IMPRINT",FACE,{"disambiguationData":[TD([[makeQuery(id+"F6.imprint","IMPRINT",EDGE,{"derivedFrom":sQuery(id+"F6.wireOp",EDGE,"E873.MirrorC")}),-1.0]])]});
            var Q281;
            Q281=makeQuery(id+"F6.imprint","IMPRINT",FACE,{"disambiguationData":[TD([[makeQuery(id+"F6.imprint","IMPRINT",EDGE,{"derivedFrom":sQuery(id+"F6.wireOp",EDGE,"E854.MirrorC")}),-1.0]])]});
            var Q282;
            Q282=makeQuery(id+"F6.imprint","IMPRINT",FACE,{"disambiguationData":[TD([[makeQuery(id+"F6.imprint","IMPRINT",EDGE,{"derivedFrom":sQuery(id+"F6.wireOp",EDGE,"E888.MirrorC")}),-1.0]])]});
            var Q283;
            Q283=makeQuery(id+"F6.imprint","IMPRINT",FACE,{"disambiguationData":[TD([[makeQuery(id+"F6.imprint","IMPRINT",EDGE,{"derivedFrom":sQuery(id+"F6.wireOp",EDGE,"E870.MirrorC")}),-1.0]])]});
            var Q284;
            Q284=makeQuery(id+"F6.imprint","IMPRINT",FACE,{"disambiguationData":[TD([[makeQuery(id+"F6.imprint","IMPRINT",EDGE,{"derivedFrom":sQuery(id+"F6.wireOp",EDGE,"E842.MirrorC")}),-1.0]])]});
            var Q285;
            Q285=makeQuery(id+"F6.imprint","IMPRINT",FACE,{"disambiguationData":[TD([[makeQuery(id+"F6.imprint","IMPRINT",EDGE,{"derivedFrom":sQuery(id+"F6.wireOp",EDGE,"E895.MirrorC")}),-1.0]])]});
            var Q286;
            Q286=makeQuery(id+"F6.imprint","IMPRINT",FACE,{"disambiguationData":[TD([[makeQuery(id+"F6.imprint","IMPRINT",EDGE,{"derivedFrom":sQuery(id+"F6.wireOp",EDGE,"E824.MirrorC")}),-1.0]])]});
            var Q287;
            Q287=makeQuery(id+"F6.imprint","IMPRINT",FACE,{"disambiguationData":[TD([[makeQuery(id+"F6.imprint","IMPRINT",EDGE,{"derivedFrom":sQuery(id+"F6.wireOp",EDGE,"E857.MirrorC")}),-1.0]])]});
            var Q288;
            Q288=makeQuery(id+"F6.imprint","IMPRINT",FACE,{"disambiguationData":[TD([[makeQuery(id+"F6.imprint","IMPRINT",EDGE,{"derivedFrom":sQuery(id+"F6.wireOp",EDGE,"E839.MirrorC")}),-1.0]])]});
            var Q289;
            Q289=makeQuery(id+"F6.imprint","IMPRINT",FACE,{"disambiguationData":[TD([[makeQuery(id+"F6.imprint","IMPRINT",EDGE,{"derivedFrom":sQuery(id+"F6.wireOp",EDGE,"E904.MirrorC")}),-1.0]])]});
            var Q290;
            Q290=makeQuery(id+"F6.imprint","IMPRINT",FACE,{"disambiguationData":[TD([[makeQuery(id+"F6.imprint","IMPRINT",EDGE,{"derivedFrom":sQuery(id+"F6.wireOp",EDGE,"E885.MirrorC")}),-1.0]])]});
            var Q291;
            Q291=makeQuery(id+"F6.imprint","IMPRINT",FACE,{"disambiguationData":[TD([[makeQuery(id+"F6.imprint","IMPRINT",EDGE,{"derivedFrom":sQuery(id+"F6.wireOp",EDGE,"E901.MirrorC")}),-1.0]])]});
            var Q292;
            Q292=makeQuery(id+"F6.imprint","IMPRINT",FACE,{"disambiguationData":[TD([[makeQuery(id+"F6.imprint","IMPRINT",EDGE,{"derivedFrom":sQuery(id+"F6.wireOp",EDGE,"E354.MirrorC")}),-1.0]])]});
            var Q293;
            Q293=makeQuery(id+"F6.imprint","IMPRINT",FACE,{"disambiguationData":[TD([[makeQuery(id+"F6.imprint","IMPRINT",EDGE,{"derivedFrom":sQuery(id+"F6.wireOp",EDGE,"E369.MirrorC")}),-1.0]])]});
            var Q294;
            Q294=makeQuery(id+"F6.imprint","IMPRINT",FACE,{"disambiguationData":[TD([[makeQuery(id+"F6.imprint","IMPRINT",EDGE,{"derivedFrom":sQuery(id+"F6.wireOp",EDGE,"E415.MirrorC")}),-1.0]])]});
            var Q295;
            Q295=makeQuery(id+"F6.imprint","IMPRINT",FACE,{"disambiguationData":[TD([[makeQuery(id+"F6.imprint","IMPRINT",EDGE,{"derivedFrom":sQuery(id+"F6.wireOp",EDGE,"E430.MirrorC")}),-1.0]])]});
            var Q296;
            Q296=makeQuery(id+"F6.imprint","IMPRINT",FACE,{"disambiguationData":[TD([[makeQuery(id+"F6.imprint","IMPRINT",EDGE,{"derivedFrom":sQuery(id+"F6.wireOp",EDGE,"E385.MirrorC")}),-1.0]])]});
            var Q297;
            Q297=makeQuery(id+"F6.imprint","IMPRINT",FACE,{"disambiguationData":[TD([[makeQuery(id+"F6.imprint","IMPRINT",EDGE,{"derivedFrom":sQuery(id+"F6.wireOp",EDGE,"E400.MirrorC")}),-1.0]])]});
            var Q298;
            Q298=makeQuery(id+"F6.imprint","IMPRINT",FACE,{"disambiguationData":[TD([[makeQuery(id+"F6.imprint","IMPRINT",EDGE,{"derivedFrom":sQuery(id+"F6.wireOp",EDGE,"E492.MirrorC")}),-1.0]])]});
            var Q299;
            Q299=makeQuery(id+"F6.imprint","IMPRINT",FACE,{"disambiguationData":[TD([[makeQuery(id+"F6.imprint","IMPRINT",EDGE,{"derivedFrom":sQuery(id+"F6.wireOp",EDGE,"E506.MirrorC")}),-1.0]])]});
            var Q300;
            Q300=makeQuery(id+"F6.imprint","IMPRINT",FACE,{"disambiguationData":[TD([[makeQuery(id+"F6.imprint","IMPRINT",EDGE,{"derivedFrom":sQuery(id+"F6.wireOp",EDGE,"E461.MirrorC")}),-1.0]])]});
            var Q301;
            Q301=makeQuery(id+"F6.imprint","IMPRINT",FACE,{"disambiguationData":[TD([[makeQuery(id+"F6.imprint","IMPRINT",EDGE,{"derivedFrom":sQuery(id+"F6.wireOp",EDGE,"E446.MirrorC")}),-1.0]])]});
            var Q302;
            Q302=makeQuery(id+"F6.imprint","IMPRINT",FACE,{"disambiguationData":[TD([[makeQuery(id+"F6.imprint","IMPRINT",EDGE,{"derivedFrom":sQuery(id+"F6.wireOp",EDGE,"E476.MirrorC")}),-1.0]])]});
            var Q303;
            Q303=makeQuery(id+"F6.imprint","IMPRINT",FACE,{"disambiguationData":[TD([[makeQuery(id+"F6.imprint","IMPRINT",EDGE,{"derivedFrom":sQuery(id+"F6.wireOp",EDGE,"E553.MirrorC")}),-1.0]])]});
            var Q304;
            Q304=makeQuery(id+"F6.imprint","IMPRINT",FACE,{"disambiguationData":[TD([[makeQuery(id+"F6.imprint","IMPRINT",EDGE,{"derivedFrom":sQuery(id+"F6.wireOp",EDGE,"E568.MirrorC")}),-1.0]])]});
            var Q305;
            Q305=makeQuery(id+"F6.imprint","IMPRINT",FACE,{"disambiguationData":[TD([[makeQuery(id+"F6.imprint","IMPRINT",EDGE,{"derivedFrom":sQuery(id+"F6.wireOp",EDGE,"E522.MirrorC")}),-1.0]])]});
            var Q306;
            Q306=makeQuery(id+"F6.imprint","IMPRINT",FACE,{"disambiguationData":[TD([[makeQuery(id+"F6.imprint","IMPRINT",EDGE,{"derivedFrom":sQuery(id+"F6.wireOp",EDGE,"E538.MirrorC")}),-1.0]])]});
            var Q307;
            Q307=makeQuery(id+"F6.imprint","IMPRINT",FACE,{"disambiguationData":[TD([[makeQuery(id+"F6.imprint","IMPRINT",EDGE,{"derivedFrom":sQuery(id+"F6.wireOp",EDGE,"E709.MirrorC")}),-1.0]])]});
            var Q308;
            Q308=makeQuery(id+"F6.imprint","IMPRINT",FACE,{"disambiguationData":[TD([[makeQuery(id+"F6.imprint","IMPRINT",EDGE,{"derivedFrom":sQuery(id+"F6.wireOp",EDGE,"E515.MirrorC")}),-1.0]])]});
            var Q309;
            Q309=makeQuery(id+"F6.imprint","IMPRINT",FACE,{"disambiguationData":[TD([[makeQuery(id+"F6.imprint","IMPRINT",EDGE,{"derivedFrom":sQuery(id+"F6.wireOp",EDGE,"E463.MirrorC")}),-1.0]])]});
            var Q310;
            Q310=makeQuery(id+"F6.imprint","IMPRINT",FACE,{"disambiguationData":[TD([[makeQuery(id+"F6.imprint","IMPRINT",EDGE,{"derivedFrom":sQuery(id+"F6.wireOp",EDGE,"E445.MirrorC")}),-1.0]])]});
            var Q311;
            Q311=makeQuery(id+"F6.imprint","IMPRINT",FACE,{"disambiguationData":[TD([[makeQuery(id+"F6.imprint","IMPRINT",EDGE,{"derivedFrom":sQuery(id+"F6.wireOp",EDGE,"E862.MirrorC")}),-1.0]])]});
            var Q312;
            Q312=makeQuery(id+"F6.imprint","IMPRINT",FACE,{"disambiguationData":[TD([[makeQuery(id+"F6.imprint","IMPRINT",EDGE,{"derivedFrom":sQuery(id+"F6.wireOp",EDGE,"E724.MirrorC")}),-1.0]])]});
            var Q313;
            Q313=makeQuery(id+"F6.imprint","IMPRINT",FACE,{"disambiguationData":[TD([[makeQuery(id+"F6.imprint","IMPRINT",EDGE,{"derivedFrom":sQuery(id+"F6.wireOp",EDGE,"E478.MirrorC")}),-1.0]])]});
            var Q314;
            Q314=makeQuery(id+"F6.imprint","IMPRINT",FACE,{"disambiguationData":[TD([[makeQuery(id+"F6.imprint","IMPRINT",EDGE,{"derivedFrom":sQuery(id+"F6.wireOp",EDGE,"E531.MirrorC")}),-1.0]])]});
            var Q315;
            Q315=makeQuery(id+"F6.imprint","IMPRINT",FACE,{"disambiguationData":[TD([[makeQuery(id+"F6.imprint","IMPRINT",EDGE,{"derivedFrom":sQuery(id+"F6.wireOp",EDGE,"E877.MirrorC")}),-1.0]])]});
            var Q316;
            Q316=makeQuery(id+"F6.imprint","IMPRINT",FACE,{"disambiguationData":[TD([[makeQuery(id+"F6.imprint","IMPRINT",EDGE,{"derivedFrom":sQuery(id+"F6.wireOp",EDGE,"E460.MirrorC")}),-1.0]])]});
            var Q317;
            Q317=makeQuery(id+"F6.imprint","IMPRINT",FACE,{"disambiguationData":[TD([[makeQuery(id+"F6.imprint","IMPRINT",EDGE,{"derivedFrom":sQuery(id+"F6.wireOp",EDGE,"E678.MirrorC")}),-1.0]])]});
            var Q318;
            Q318=makeQuery(id+"F6.imprint","IMPRINT",FACE,{"disambiguationData":[TD([[makeQuery(id+"F6.imprint","IMPRINT",EDGE,{"derivedFrom":sQuery(id+"F6.wireOp",EDGE,"E731.MirrorC")}),-1.0]])]});
            var Q319;
            Q319=makeQuery(id+"F6.imprint","IMPRINT",FACE,{"disambiguationData":[TD([[makeQuery(id+"F6.imprint","IMPRINT",EDGE,{"derivedFrom":sQuery(id+"F6.wireOp",EDGE,"E432.MirrorC")}),-1.0]])]});
            var Q320;
            Q320=makeQuery(id+"F6.imprint","IMPRINT",FACE,{"disambiguationData":[TD([[makeQuery(id+"F6.imprint","IMPRINT",EDGE,{"derivedFrom":sQuery(id+"F6.wireOp",EDGE,"E485.MirrorC")}),-1.0]])]});
            var Q321;
            Q321=makeQuery(id+"F6.imprint","IMPRINT",FACE,{"disambiguationData":[TD([[makeQuery(id+"F6.imprint","IMPRINT",EDGE,{"derivedFrom":sQuery(id+"F6.wireOp",EDGE,"E414.MirrorC")}),-1.0]])]});
            var Q322;
            Q322=makeQuery(id+"F6.imprint","IMPRINT",FACE,{"disambiguationData":[TD([[makeQuery(id+"F6.imprint","IMPRINT",EDGE,{"derivedFrom":sQuery(id+"F6.wireOp",EDGE,"E884.MirrorC")}),-1.0]])]});
            var Q323;
            Q323=makeQuery(id+"F6.imprint","IMPRINT",FACE,{"disambiguationData":[TD([[makeQuery(id+"F6.imprint","IMPRINT",EDGE,{"derivedFrom":sQuery(id+"F6.wireOp",EDGE,"E693.MirrorC")}),-1.0]])]});
            var Q324;
            Q324=makeQuery(id+"F6.imprint","IMPRINT",FACE,{"disambiguationData":[TD([[makeQuery(id+"F6.imprint","IMPRINT",EDGE,{"derivedFrom":sQuery(id+"F6.wireOp",EDGE,"E448.MirrorC")}),-1.0]])]});
            var Q325;
            Q325=makeQuery(id+"F6.imprint","IMPRINT",FACE,{"disambiguationData":[TD([[makeQuery(id+"F6.imprint","IMPRINT",EDGE,{"derivedFrom":sQuery(id+"F6.wireOp",EDGE,"E500.MirrorC")}),-1.0]])]});
            var Q326;
            Q326=makeQuery(id+"F6.imprint","IMPRINT",FACE,{"disambiguationData":[TD([[makeQuery(id+"F6.imprint","IMPRINT",EDGE,{"derivedFrom":sQuery(id+"F6.wireOp",EDGE,"E429.MirrorC")}),-1.0]])]});
            var Q327;
            Q327=makeQuery(id+"F6.imprint","IMPRINT",FACE,{"disambiguationData":[TD([[makeQuery(id+"F6.imprint","IMPRINT",EDGE,{"derivedFrom":sQuery(id+"F6.wireOp",EDGE,"E900.MirrorC")}),-1.0]])]});
            var Q328;
            Q328=makeQuery(id+"F6.imprint","IMPRINT",FACE,{"disambiguationData":[TD([[makeQuery(id+"F6.imprint","IMPRINT",EDGE,{"derivedFrom":sQuery(id+"F6.wireOp",EDGE,"E847.MirrorC")}),-1.0]])]});
            var Q329;
            Q329=makeQuery(id+"F6.imprint","IMPRINT",FACE,{"disambiguationData":[TD([[makeQuery(id+"F6.imprint","IMPRINT",EDGE,{"derivedFrom":sQuery(id+"F6.wireOp",EDGE,"E577.MirrorC")}),-1.0]])]});
            var Q330;
            Q330=makeQuery(id+"F6.imprint","IMPRINT",FACE,{"disambiguationData":[TD([[makeQuery(id+"F6.imprint","IMPRINT",EDGE,{"derivedFrom":sQuery(id+"F6.wireOp",EDGE,"E524.MirrorC")}),-1.0]])]});
            var Q331;
            Q331=makeQuery(id+"F6.imprint","IMPRINT",FACE,{"disambiguationData":[TD([[makeQuery(id+"F6.imprint","IMPRINT",EDGE,{"derivedFrom":sQuery(id+"F6.wireOp",EDGE,"E540.MirrorC")}),-1.0]])]});
            var Q332;
            Q332=makeQuery(id+"F6.imprint","IMPRINT",FACE,{"disambiguationData":[TD([[makeQuery(id+"F6.imprint","IMPRINT",EDGE,{"derivedFrom":sQuery(id+"F6.wireOp",EDGE,"E346.MirrorC")}),-1.0]])]});
            var Q333;
            Q333=makeQuery(id+"F6.imprint","IMPRINT",FACE,{"disambiguationData":[TD([[makeQuery(id+"F6.imprint","IMPRINT",EDGE,{"derivedFrom":sQuery(id+"F6.wireOp",EDGE,"E521.MirrorC")}),-1.0]])]});
            var Q334;
            Q334=makeQuery(id+"F6.imprint","IMPRINT",FACE,{"disambiguationData":[TD([[makeQuery(id+"F6.imprint","IMPRINT",EDGE,{"derivedFrom":sQuery(id+"F6.wireOp",EDGE,"E746.MirrorC")}),-1.0]])]});
            var Q335;
            Q335=makeQuery(id+"F6.imprint","IMPRINT",FACE,{"disambiguationData":[TD([[makeQuery(id+"F6.imprint","IMPRINT",EDGE,{"derivedFrom":sQuery(id+"F6.wireOp",EDGE,"E546.MirrorC")}),-1.0]])]});
            var Q336;
            Q336=makeQuery(id+"F6.imprint","IMPRINT",FACE,{"disambiguationData":[TD([[makeQuery(id+"F6.imprint","IMPRINT",EDGE,{"derivedFrom":sQuery(id+"F6.wireOp",EDGE,"E494.MirrorC")}),-1.0]])]});
            var Q337;
            Q337=makeQuery(id+"F6.imprint","IMPRINT",FACE,{"disambiguationData":[TD([[makeQuery(id+"F6.imprint","IMPRINT",EDGE,{"derivedFrom":sQuery(id+"F6.wireOp",EDGE,"E475.MirrorC")}),-1.0]])]});
            var Q338;
            Q338=makeQuery(id+"F6.imprint","IMPRINT",FACE,{"disambiguationData":[TD([[makeQuery(id+"F6.imprint","IMPRINT",EDGE,{"derivedFrom":sQuery(id+"F6.wireOp",EDGE,"E893.MirrorC")}),-1.0]])]});
            var Q339;
            Q339=makeQuery(id+"F6.imprint","IMPRINT",FACE,{"disambiguationData":[TD([[makeQuery(id+"F6.imprint","IMPRINT",EDGE,{"derivedFrom":sQuery(id+"F6.wireOp",EDGE,"E508.MirrorC")}),-1.0]])]});
            var Q340;
            Q340=makeQuery(id+"F6.imprint","IMPRINT",FACE,{"disambiguationData":[TD([[makeQuery(id+"F6.imprint","IMPRINT",EDGE,{"derivedFrom":sQuery(id+"F6.wireOp",EDGE,"E561.MirrorC")}),-1.0]])]});
            var Q341;
            Q341=makeQuery(id+"F6.imprint","IMPRINT",FACE,{"disambiguationData":[TD([[makeQuery(id+"F6.imprint","IMPRINT",EDGE,{"derivedFrom":sQuery(id+"F6.wireOp",EDGE,"E491.MirrorC")}),-1.0]])]});
            var Q342;
            Q342=makeQuery(id+"F6.imprint","IMPRINT",FACE,{"disambiguationData":[TD([[makeQuery(id+"F6.imprint","IMPRINT",EDGE,{"derivedFrom":sQuery(id+"F6.wireOp",EDGE,"E43.4.0.18")}),1.0]])]});
            var Q343;
            Q343=makeQuery(id+"F6.imprint","IMPRINT",FACE,{"disambiguationData":[TD([[makeQuery(id+"F6.imprint","IMPRINT",EDGE,{"derivedFrom":sQuery(id+"F6.wireOp",EDGE,"E43.3.0.9")}),1.0]])]});
            var Q344;
            Q344=makeQuery(id+"F6.imprint","IMPRINT",FACE,{"disambiguationData":[TD([[makeQuery(id+"F6.imprint","IMPRINT",EDGE,{"derivedFrom":sQuery(id+"F6.wireOp",EDGE,"E43.2.0.18")}),1.0]])]});
            var Q345;
            Q345=makeQuery(id+"F6.imprint","IMPRINT",FACE,{"disambiguationData":[TD([[makeQuery(id+"F6.imprint","IMPRINT",EDGE,{"derivedFrom":sQuery(id+"F6.wireOp",EDGE,"E43.7.0.9")}),1.0]])]});
            var Q346;
            Q346=makeQuery(id+"F6.imprint","IMPRINT",FACE,{"disambiguationData":[TD([[makeQuery(id+"F6.imprint","IMPRINT",EDGE,{"derivedFrom":sQuery(id+"F6.wireOp",EDGE,"E637.MirrorC")}),-1.0]])]});
            var Q347;
            Q347=makeQuery(id+"F6.imprint","IMPRINT",FACE,{"disambiguationData":[TD([[makeQuery(id+"F6.imprint","IMPRINT",EDGE,{"derivedFrom":sQuery(id+"F6.wireOp",EDGE,"E43.6.0.18")}),1.0]])]});
            var Q348;
            Q348=makeQuery(id+"F6.imprint","IMPRINT",FACE,{"disambiguationData":[TD([[makeQuery(id+"F6.imprint","IMPRINT",EDGE,{"derivedFrom":sQuery(id+"F6.wireOp",EDGE,"E43.5.0.9")}),1.0]])]});
            var Q349;
            Q349=makeQuery(id+"F6.imprint","IMPRINT",FACE,{"disambiguationData":[TD([[makeQuery(id+"F6.imprint","IMPRINT",EDGE,{"derivedFrom":sQuery(id+"F6.wireOp",EDGE,"E586.MirrorC")}),-1.0]])]});
            var Q350;
            Q350=makeQuery(id+"F6.imprint","IMPRINT",FACE,{"disambiguationData":[TD([[makeQuery(id+"F6.imprint","IMPRINT",EDGE,{"derivedFrom":sQuery(id+"F6.wireOp",EDGE,"E43.9.0.9")}),1.0]])]});
            var Q351;
            Q351=makeQuery(id+"F6.imprint","IMPRINT",FACE,{"disambiguationData":[TD([[makeQuery(id+"F6.imprint","IMPRINT",EDGE,{"derivedFrom":sQuery(id+"F6.wireOp",EDGE,"E43.8.0.18")}),1.0]])]});
            var Q352;
            Q352=makeQuery(id+"F6.imprint","IMPRINT",FACE,{"disambiguationData":[TD([[makeQuery(id+"F6.imprint","IMPRINT",EDGE,{"derivedFrom":sQuery(id+"F6.wireOp",EDGE,"E43.12.0.18")}),1.0]])]});
            var Q353;
            Q353=makeQuery(id+"F6.imprint","IMPRINT",FACE,{"disambiguationData":[TD([[makeQuery(id+"F6.imprint","IMPRINT",EDGE,{"derivedFrom":sQuery(id+"F6.wireOp",EDGE,"E392.MirrorC")}),-1.0]])]});
            var Q354;
            Q354=makeQuery(id+"F6.imprint","IMPRINT",FACE,{"disambiguationData":[TD([[makeQuery(id+"F6.imprint","IMPRINT",EDGE,{"derivedFrom":sQuery(id+"F6.wireOp",EDGE,"E43.11.0.9")}),1.0]])]});
            var Q355;
            Q355=makeQuery(id+"F6.imprint","IMPRINT",FACE,{"disambiguationData":[TD([[makeQuery(id+"F6.imprint","IMPRINT",EDGE,{"derivedFrom":sQuery(id+"F6.wireOp",EDGE,"E43.10.0.18")}),1.0]])]});
            var Q356;
            Q356=makeQuery(id+"F6.imprint","IMPRINT",FACE,{"disambiguationData":[TD([[makeQuery(id+"F6.imprint","IMPRINT",EDGE,{"derivedFrom":sQuery(id+"F6.wireOp",EDGE,"E43.15.0.9")}),1.0]])]});
            var Q357;
            Q357=makeQuery(id+"F6.imprint","IMPRINT",FACE,{"disambiguationData":[TD([[makeQuery(id+"F6.imprint","IMPRINT",EDGE,{"derivedFrom":sQuery(id+"F6.wireOp",EDGE,"E43.14.0.18")}),1.0]])]});
            var Q358;
            Q358=makeQuery(id+"F6.imprint","IMPRINT",FACE,{"disambiguationData":[TD([[makeQuery(id+"F6.imprint","IMPRINT",EDGE,{"derivedFrom":sQuery(id+"F6.wireOp",EDGE,"E43.13.0.9")}),1.0]])]});
            var Q359;
            Q359=makeQuery(id+"F6.imprint","IMPRINT",FACE,{"disambiguationData":[TD([[makeQuery(id+"F6.imprint","IMPRINT",EDGE,{"derivedFrom":sQuery(id+"F6.wireOp",EDGE,"E43.17.0.9")}),1.0]])]});
            var Q360;
            Q360=makeQuery(id+"F6.imprint","IMPRINT",FACE,{"disambiguationData":[TD([[makeQuery(id+"F6.imprint","IMPRINT",EDGE,{"derivedFrom":sQuery(id+"F6.wireOp",EDGE,"E567.MirrorC")}),-1.0]])]});
            var Q361;
            Q361=makeQuery(id+"F6.imprint","IMPRINT",FACE,{"disambiguationData":[TD([[makeQuery(id+"F6.imprint","IMPRINT",EDGE,{"derivedFrom":sQuery(id+"F6.wireOp",EDGE,"E43.16.0.18")}),1.0]])]});
            var Q362;
            Q362=makeQuery(id+"F6.imprint","IMPRINT",FACE,{"disambiguationData":[TD([[makeQuery(id+"F6.imprint","IMPRINT",EDGE,{"derivedFrom":sQuery(id+"F6.wireOp",EDGE,"E792.MirrorC")}),-1.0]])]});
            var Q363;
            Q363=makeQuery(id+"F6.imprint","IMPRINT",FACE,{"disambiguationData":[TD([[makeQuery(id+"F6.imprint","IMPRINT",EDGE,{"derivedFrom":sQuery(id+"F6.wireOp",EDGE,"E43.19.0.9")}),1.0]])]});
            var Q364;
            Q364=makeQuery(id+"F6.imprint","IMPRINT",FACE,{"disambiguationData":[TD([[makeQuery(id+"F6.imprint","IMPRINT",EDGE,{"derivedFrom":sQuery(id+"F6.wireOp",EDGE,"E43.18.0.18")}),1.0]])]});
            var Q365;
            Q365=makeQuery(id+"F6.imprint","IMPRINT",FACE,{"disambiguationData":[TD([[makeQuery(id+"F6.imprint","IMPRINT",EDGE,{"derivedFrom":sQuery(id+"F6.wireOp",EDGE,"E739.MirrorC")}),-1.0]])]});
            var Q366;
            Q366=makeQuery(id+"F6.imprint","IMPRINT",FACE,{"disambiguationData":[TD([[makeQuery(id+"F6.imprint","IMPRINT",EDGE,{"derivedFrom":sQuery(id+"F6.wireOp",EDGE,"E324.MirrorC")}),-1.0]])]});
            var Q367;
            Q367=makeQuery(id+"F6.imprint","IMPRINT",FACE,{"disambiguationData":[TD([[makeQuery(id+"F6.imprint","IMPRINT",EDGE,{"derivedFrom":sQuery(id+"F6.wireOp",EDGE,"E652.MirrorC")}),-1.0]])]});
            var Q368;
            Q368=makeQuery(id+"F6.imprint","IMPRINT",FACE,{"disambiguationData":[TD([[makeQuery(id+"F6.imprint","IMPRINT",EDGE,{"derivedFrom":sQuery(id+"F6.wireOp",EDGE,"E340.MirrorC")}),-1.0]])]});
            var Q369;
            Q369=makeQuery(id+"F6.imprint","IMPRINT",FACE,{"disambiguationData":[TD([[makeQuery(id+"F6.imprint","IMPRINT",EDGE,{"derivedFrom":sQuery(id+"F6.wireOp",EDGE,"E277.MirrorC")}),-1.0]])]});
            var Q370;
            Q370=makeQuery(id+"F6.imprint","IMPRINT",FACE,{"disambiguationData":[TD([[makeQuery(id+"F6.imprint","IMPRINT",EDGE,{"derivedFrom":sQuery(id+"F6.wireOp",EDGE,"E261.MirrorC")}),-1.0]])]});
            var Q371;
            Q371=makeQuery(id+"F6.imprint","IMPRINT",FACE,{"disambiguationData":[TD([[makeQuery(id+"F6.imprint","IMPRINT",EDGE,{"derivedFrom":sQuery(id+"F6.wireOp",EDGE,"E248.MirrorC")}),-1.0]])]});
            var Q372;
            Q372=makeQuery(id+"F6.imprint","IMPRINT",FACE,{"disambiguationData":[TD([[makeQuery(id+"F6.imprint","IMPRINT",EDGE,{"derivedFrom":sQuery(id+"F6.wireOp",EDGE,"E309.MirrorC")}),-1.0]])]});
            var Q373;
            Q373=makeQuery(id+"F6.imprint","IMPRINT",FACE,{"disambiguationData":[TD([[makeQuery(id+"F6.imprint","IMPRINT",EDGE,{"derivedFrom":sQuery(id+"F6.wireOp",EDGE,"E293.MirrorC")}),-1.0]])]});
            var Q374;
            Q374=makeQuery(id+"F6.imprint","IMPRINT",FACE,{"disambiguationData":[TD([[makeQuery(id+"F6.imprint","IMPRINT",EDGE,{"derivedFrom":sQuery(id+"F6.wireOp",EDGE,"E583.MirrorC")}),-1.0]])]});
            var Q375;
            Q375=makeQuery(id+"F6.imprint","IMPRINT",FACE,{"disambiguationData":[TD([[makeQuery(id+"F6.imprint","IMPRINT",EDGE,{"derivedFrom":sQuery(id+"F6.wireOp",EDGE,"E755.MirrorC")}),-1.0]])]});
            var Q376;
            Q376=makeQuery(id+"F6.imprint","IMPRINT",FACE,{"disambiguationData":[TD([[makeQuery(id+"F6.imprint","IMPRINT",EDGE,{"derivedFrom":sQuery(id+"F6.wireOp",EDGE,"E807.MirrorC")}),-1.0]])]});
            var Q377;
            Q377=makeQuery(id+"F6.imprint","IMPRINT",FACE,{"disambiguationData":[TD([[makeQuery(id+"F6.imprint","IMPRINT",EDGE,{"derivedFrom":sQuery(id+"F6.wireOp",EDGE,"E43.1.0.9")}),1.0]])]});
            var Q378;
            Q378=makeQuery(id+"F6.imprint","IMPRINT",FACE,{"disambiguationData":[TD([[makeQuery(id+"F6.imprint","IMPRINT",EDGE,{"derivedFrom":sQuery(id+"F6.wireOp",EDGE,"E555.MirrorC")}),-1.0]])]});
            var Q379;
            Q379=makeQuery(id+"F6.imprint","IMPRINT",FACE,{"disambiguationData":[TD([[makeQuery(id+"F6.imprint","IMPRINT",EDGE,{"derivedFrom":sQuery(id+"F6.wireOp",EDGE,"E607.MirrorC")}),-1.0]])]});
            var Q380;
            Q380=makeQuery(id+"F6.imprint","IMPRINT",FACE,{"disambiguationData":[TD([[makeQuery(id+"F6.imprint","IMPRINT",EDGE,{"derivedFrom":sQuery(id+"F6.wireOp",EDGE,"E537.MirrorC")}),-1.0]])]});
            var Q381;
            Q381=makeQuery(id+"F6.imprint","IMPRINT",FACE,{"disambiguationData":[TD([[makeQuery(id+"F6.imprint","IMPRINT",EDGE,{"derivedFrom":sQuery(id+"F6.wireOp",EDGE,"E761.MirrorC")}),-1.0]])]});
            var Q382;
            Q382=makeQuery(id+"F6.imprint","IMPRINT",FACE,{"disambiguationData":[TD([[makeQuery(id+"F6.imprint","IMPRINT",EDGE,{"derivedFrom":sQuery(id+"F6.wireOp",EDGE,"E43.21.0.9")}),1.0]])]});
            var Q383;
            Q383=makeQuery(id+"F6.imprint","IMPRINT",FACE,{"disambiguationData":[TD([[makeQuery(id+"F6.imprint","IMPRINT",EDGE,{"derivedFrom":sQuery(id+"F6.wireOp",EDGE,"E43.20.0.18")}),1.0]])]});
            var Q384;
            Q384=makeQuery(id+"F6.imprint","IMPRINT",FACE,{"disambiguationData":[TD([[makeQuery(id+"F6.imprint","IMPRINT",EDGE,{"derivedFrom":sQuery(id+"F6.wireOp",EDGE,"E43.24.0.18")}),1.0]])]});
            var Q385;
            Q385=makeQuery(id+"F6.imprint","IMPRINT",FACE,{"disambiguationData":[TD([[makeQuery(id+"F6.imprint","IMPRINT",EDGE,{"derivedFrom":sQuery(id+"F6.wireOp",EDGE,"E43.23.0.9")}),1.0]])]});
            var Q386;
            Q386=makeQuery(id+"F6.imprint","IMPRINT",FACE,{"disambiguationData":[TD([[makeQuery(id+"F6.imprint","IMPRINT",EDGE,{"derivedFrom":sQuery(id+"F6.wireOp",EDGE,"E570.MirrorC")}),-1.0]])]});
            var Q387;
            Q387=makeQuery(id+"F6.imprint","IMPRINT",FACE,{"disambiguationData":[TD([[makeQuery(id+"F6.imprint","IMPRINT",EDGE,{"derivedFrom":sQuery(id+"F6.wireOp",EDGE,"E622.MirrorC")}),-1.0]])]});
            var Q388;
            Q388=makeQuery(id+"F6.imprint","IMPRINT",FACE,{"disambiguationData":[TD([[makeQuery(id+"F6.imprint","IMPRINT",EDGE,{"derivedFrom":sQuery(id+"F6.wireOp",EDGE,"E43.22.0.18")}),1.0]])]});
            var Q389;
            Q389=makeQuery(id+"F6.imprint","IMPRINT",FACE,{"disambiguationData":[TD([[makeQuery(id+"F6.imprint","IMPRINT",EDGE,{"derivedFrom":sQuery(id+"F6.wireOp",EDGE,"E43.27.0.9")}),1.0]])]});
            var Q390;
            Q390=makeQuery(id+"F6.imprint","IMPRINT",FACE,{"disambiguationData":[TD([[makeQuery(id+"F6.imprint","IMPRINT",EDGE,{"derivedFrom":sQuery(id+"F6.wireOp",EDGE,"E43.26.0.18")}),1.0]])]});
            var Q391;
            Q391=makeQuery(id+"F6.imprint","IMPRINT",FACE,{"disambiguationData":[TD([[makeQuery(id+"F6.imprint","IMPRINT",EDGE,{"derivedFrom":sQuery(id+"F6.wireOp",EDGE,"E43.25.0.9")}),1.0]])]});
            var Q392;
            Q392=makeQuery(id+"F6.imprint","IMPRINT",FACE,{"disambiguationData":[TD([[makeQuery(id+"F6.imprint","IMPRINT",EDGE,{"derivedFrom":sQuery(id+"F6.wireOp",EDGE,"E43.29.0.9")}),1.0]])]});
            var Q393;
            Q393=makeQuery(id+"F6.imprint","IMPRINT",FACE,{"disambiguationData":[TD([[makeQuery(id+"F6.imprint","IMPRINT",EDGE,{"derivedFrom":sQuery(id+"F6.wireOp",EDGE,"E43.28.0.18")}),1.0]])]});
            var Q394;
            Q394=makeQuery(id+"F6.imprint","IMPRINT",FACE,{"disambiguationData":[TD([[makeQuery(id+"F6.imprint","IMPRINT",EDGE,{"derivedFrom":sQuery(id+"F6.wireOp",EDGE,"E376.MirrorC")}),-1.0]])]});
            var Q395;
            Q395=makeQuery(id+"F6.imprint","IMPRINT",FACE,{"disambiguationData":[TD([[makeQuery(id+"F6.imprint","IMPRINT",EDGE,{"derivedFrom":sQuery(id+"F6.wireOp",EDGE,"E43.32.0.18")}),1.0]])]});
            var Q396;
            Q396=makeQuery(id+"F6.imprint","IMPRINT",FACE,{"disambiguationData":[TD([[makeQuery(id+"F6.imprint","IMPRINT",EDGE,{"derivedFrom":sQuery(id+"F6.wireOp",EDGE,"E552.MirrorC")}),-1.0]])]});
            var Q397;
            Q397=makeQuery(id+"F6.imprint","IMPRINT",FACE,{"disambiguationData":[TD([[makeQuery(id+"F6.imprint","IMPRINT",EDGE,{"derivedFrom":sQuery(id+"F6.wireOp",EDGE,"E43.31.0.9")}),1.0]])]});
            var Q398;
            Q398=makeQuery(id+"F6.imprint","IMPRINT",FACE,{"disambiguationData":[TD([[makeQuery(id+"F6.imprint","IMPRINT",EDGE,{"derivedFrom":sQuery(id+"F6.wireOp",EDGE,"E43.30.0.18")}),1.0]])]});
            var Q399;
            Q399=makeQuery(id+"F6.imprint","IMPRINT",FACE,{"disambiguationData":[TD([[makeQuery(id+"F6.imprint","IMPRINT",EDGE,{"derivedFrom":sQuery(id+"F6.wireOp",EDGE,"E777.MirrorC")}),-1.0]])]});
            var Q400;
            Q400=makeQuery(id+"F6.imprint","IMPRINT",FACE,{"disambiguationData":[TD([[makeQuery(id+"F6.imprint","IMPRINT",EDGE,{"derivedFrom":sQuery(id+"F6.wireOp",EDGE,"E452.MirrorC")}),-1.0]])]});
            var Q401;
            Q401=makeQuery(id+"F6.imprint","IMPRINT",FACE,{"disambiguationData":[TD([[makeQuery(id+"F6.imprint","IMPRINT",EDGE,{"derivedFrom":sQuery(id+"F6.wireOp",EDGE,"E643.MirrorC")}),-1.0]])]});
            var Q402;
            Q402=makeQuery(id+"F6.imprint","IMPRINT",FACE,{"disambiguationData":[TD([[makeQuery(id+"F6.imprint","IMPRINT",EDGE,{"derivedFrom":sQuery(id+"F6.wireOp",EDGE,"E852.MirrorC")}),-1.0]])]});
            var Q403;
            Q403=makeQuery(id+"F6.imprint","IMPRINT",FACE,{"disambiguationData":[TD([[makeQuery(id+"F6.imprint","IMPRINT",EDGE,{"derivedFrom":sQuery(id+"F6.wireOp",EDGE,"E800.MirrorC")}),-1.0]])]});
            var Q404;
            Q404=makeQuery(id+"F6.imprint","IMPRINT",FACE,{"disambiguationData":[TD([[makeQuery(id+"F6.imprint","IMPRINT",EDGE,{"derivedFrom":sQuery(id+"F6.wireOp",EDGE,"E698.MirrorC")}),-1.0]])]});
            var Q405;
            Q405=makeQuery(id+"F6.imprint","IMPRINT",FACE,{"disambiguationData":[TD([[makeQuery(id+"F6.imprint","IMPRINT",EDGE,{"derivedFrom":sQuery(id+"F6.wireOp",EDGE,"E646.MirrorC")}),-1.0]])]});
            var Q406;
            Q406=makeQuery(id+"F6.imprint","IMPRINT",FACE,{"disambiguationData":[TD([[makeQuery(id+"F6.imprint","IMPRINT",EDGE,{"derivedFrom":sQuery(id+"F6.wireOp",EDGE,"E468.MirrorC")}),-1.0]])]});
            var Q407;
            Q407=makeQuery(id+"F6.imprint","IMPRINT",FACE,{"disambiguationData":[TD([[makeQuery(id+"F6.imprint","IMPRINT",EDGE,{"derivedFrom":sQuery(id+"F6.wireOp",EDGE,"E658.MirrorC")}),-1.0]])]});
            var Q408;
            Q408=makeQuery(id+"F6.imprint","IMPRINT",FACE,{"disambiguationData":[TD([[makeQuery(id+"F6.imprint","IMPRINT",EDGE,{"derivedFrom":sQuery(id+"F6.wireOp",EDGE,"E815.MirrorC")}),-1.0]])]});
            var Q409;
            Q409=makeQuery(id+"F6.imprint","IMPRINT",FACE,{"disambiguationData":[TD([[makeQuery(id+"F6.imprint","IMPRINT",EDGE,{"derivedFrom":sQuery(id+"F6.wireOp",EDGE,"E867.MirrorC")}),-1.0]])]});
            var Q410;
            Q410=makeQuery(id+"F6.imprint","IMPRINT",FACE,{"disambiguationData":[TD([[makeQuery(id+"F6.imprint","IMPRINT",EDGE,{"derivedFrom":sQuery(id+"F6.wireOp",EDGE,"E661.MirrorC")}),-1.0]])]});
            var Q411;
            Q411=makeQuery(id+"F6.imprint","IMPRINT",FACE,{"disambiguationData":[TD([[makeQuery(id+"F6.imprint","IMPRINT",EDGE,{"derivedFrom":sQuery(id+"F6.wireOp",EDGE,"E713.MirrorC")}),-1.0]])]});
            var Q412;
            Q412=makeQuery(id+"F6.imprint","IMPRINT",FACE,{"disambiguationData":[TD([[makeQuery(id+"F6.imprint","IMPRINT",EDGE,{"derivedFrom":sQuery(id+"F6.wireOp",EDGE,"E421.MirrorC")}),-1.0]])]});
            var Q413;
            Q413=makeQuery(id+"F6.imprint","IMPRINT",FACE,{"disambiguationData":[TD([[makeQuery(id+"F6.imprint","IMPRINT",EDGE,{"derivedFrom":sQuery(id+"F6.wireOp",EDGE,"E322.MirrorC")}),-1.0]])]});
            var Q414;
            Q414=makeQuery(id+"F6.imprint","IMPRINT",FACE,{"disambiguationData":[TD([[makeQuery(id+"F6.imprint","IMPRINT",EDGE,{"derivedFrom":sQuery(id+"F6.wireOp",EDGE,"E615.MirrorC")}),-1.0]])]});
            var Q415;
            Q415=makeQuery(id+"F6.imprint","IMPRINT",FACE,{"disambiguationData":[TD([[makeQuery(id+"F6.imprint","IMPRINT",EDGE,{"derivedFrom":sQuery(id+"F6.wireOp",EDGE,"E338.MirrorC")}),-1.0]])]});
            var Q416;
            Q416=makeQuery(id+"F6.imprint","IMPRINT",FACE,{"disambiguationData":[TD([[makeQuery(id+"F6.imprint","IMPRINT",EDGE,{"derivedFrom":sQuery(id+"F6.wireOp",EDGE,"E246.MirrorC")}),-1.0]])]});
            var Q417;
            Q417=makeQuery(id+"F6.imprint","IMPRINT",FACE,{"disambiguationData":[TD([[makeQuery(id+"F6.imprint","IMPRINT",EDGE,{"derivedFrom":sQuery(id+"F6.wireOp",EDGE,"E307.MirrorC")}),-1.0]])]});
            var Q418;
            Q418=makeQuery(id+"F6.imprint","IMPRINT",FACE,{"disambiguationData":[TD([[makeQuery(id+"F6.imprint","IMPRINT",EDGE,{"derivedFrom":sQuery(id+"F6.wireOp",EDGE,"E291.MirrorC")}),-1.0]])]});
            var Q419;
            Q419=makeQuery(id+"F6.imprint","IMPRINT",FACE,{"disambiguationData":[TD([[makeQuery(id+"F6.imprint","IMPRINT",EDGE,{"derivedFrom":sQuery(id+"F6.wireOp",EDGE,"E275.MirrorC")}),-1.0]])]});
            var Q420;
            Q420=makeQuery(id+"F6.imprint","IMPRINT",FACE,{"disambiguationData":[TD([[makeQuery(id+"F6.imprint","IMPRINT",EDGE,{"derivedFrom":sQuery(id+"F6.wireOp",EDGE,"E598.MirrorC")}),-1.0]])]});
            var Q421;
            Q421=makeQuery(id+"F6.imprint","IMPRINT",FACE,{"disambiguationData":[TD([[makeQuery(id+"F6.imprint","IMPRINT",EDGE,{"derivedFrom":sQuery(id+"F6.wireOp",EDGE,"E43.1.0.7")}),1.0]])]});
            var Q422;
            Q422=makeQuery(id+"F6.imprint","IMPRINT",FACE,{"disambiguationData":[TD([[makeQuery(id+"F6.imprint","IMPRINT",EDGE,{"derivedFrom":sQuery(id+"F6.wireOp",EDGE,"E43.3.0.7")}),1.0]])]});
            var Q423;
            Q423=makeQuery(id+"F6.imprint","IMPRINT",FACE,{"disambiguationData":[TD([[makeQuery(id+"F6.imprint","IMPRINT",EDGE,{"derivedFrom":sQuery(id+"F6.wireOp",EDGE,"E667.MirrorC")}),-1.0]])]});
            var Q424;
            Q424=makeQuery(id+"F6.imprint","IMPRINT",FACE,{"disambiguationData":[TD([[makeQuery(id+"F6.imprint","IMPRINT",EDGE,{"derivedFrom":sQuery(id+"F6.wireOp",EDGE,"E43.2.0.16")}),1.0]])]});
            var Q425;
            Q425=makeQuery(id+"F6.imprint","IMPRINT",FACE,{"disambiguationData":[TD([[makeQuery(id+"F6.imprint","IMPRINT",EDGE,{"derivedFrom":sQuery(id+"F6.wireOp",EDGE,"E43.6.0.16")}),1.0]])]});
            var Q426;
            Q426=makeQuery(id+"F6.imprint","IMPRINT",FACE,{"disambiguationData":[TD([[makeQuery(id+"F6.imprint","IMPRINT",EDGE,{"derivedFrom":sQuery(id+"F6.wireOp",EDGE,"E770.MirrorC")}),-1.0]])]});
            var Q427;
            Q427=makeQuery(id+"F6.imprint","IMPRINT",FACE,{"disambiguationData":[TD([[makeQuery(id+"F6.imprint","IMPRINT",EDGE,{"derivedFrom":sQuery(id+"F6.wireOp",EDGE,"E43.5.0.7")}),1.0]])]});
            var Q428;
            Q428=makeQuery(id+"F6.imprint","IMPRINT",FACE,{"disambiguationData":[TD([[makeQuery(id+"F6.imprint","IMPRINT",EDGE,{"derivedFrom":sQuery(id+"F6.wireOp",EDGE,"E43.4.0.16")}),1.0]])]});
            var Q429;
            Q429=makeQuery(id+"F6.imprint","IMPRINT",FACE,{"disambiguationData":[TD([[makeQuery(id+"F6.imprint","IMPRINT",EDGE,{"derivedFrom":sQuery(id+"F6.wireOp",EDGE,"E437.MirrorC")}),-1.0]])]});
            var Q430;
            Q430=makeQuery(id+"F6.imprint","IMPRINT",FACE,{"disambiguationData":[TD([[makeQuery(id+"F6.imprint","IMPRINT",EDGE,{"derivedFrom":sQuery(id+"F6.wireOp",EDGE,"E627.MirrorC")}),-1.0]])]});
            var Q431;
            Q431=makeQuery(id+"F6.imprint","IMPRINT",FACE,{"disambiguationData":[TD([[makeQuery(id+"F6.imprint","IMPRINT",EDGE,{"derivedFrom":sQuery(id+"F6.wireOp",EDGE,"E785.MirrorC")}),-1.0]])]});
            var Q432;
            Q432=makeQuery(id+"F6.imprint","IMPRINT",FACE,{"disambiguationData":[TD([[makeQuery(id+"F6.imprint","IMPRINT",EDGE,{"derivedFrom":sQuery(id+"F6.wireOp",EDGE,"E836.MirrorC")}),-1.0]])]});
            var Q433;
            Q433=makeQuery(id+"F6.imprint","IMPRINT",FACE,{"disambiguationData":[TD([[makeQuery(id+"F6.imprint","IMPRINT",EDGE,{"derivedFrom":sQuery(id+"F6.wireOp",EDGE,"E630.MirrorC")}),-1.0]])]});
            var Q434;
            Q434=makeQuery(id+"F6.imprint","IMPRINT",FACE,{"disambiguationData":[TD([[makeQuery(id+"F6.imprint","IMPRINT",EDGE,{"derivedFrom":sQuery(id+"F6.wireOp",EDGE,"E683.MirrorC")}),-1.0]])]});
            var Q435;
            Q435=makeQuery(id+"F6.imprint","IMPRINT",FACE,{"disambiguationData":[TD([[makeQuery(id+"F6.imprint","IMPRINT",EDGE,{"derivedFrom":sQuery(id+"F6.wireOp",EDGE,"E43.26.0.16")}),1.0]])]});
            var Q436;
            Q436=makeQuery(id+"F6.imprint","IMPRINT",FACE,{"disambiguationData":[TD([[makeQuery(id+"F6.imprint","IMPRINT",EDGE,{"derivedFrom":sQuery(id+"F6.wireOp",EDGE,"E43.25.0.7")}),1.0]])]});
            var Q437;
            Q437=makeQuery(id+"F6.imprint","IMPRINT",FACE,{"disambiguationData":[TD([[makeQuery(id+"F6.imprint","IMPRINT",EDGE,{"derivedFrom":sQuery(id+"F6.wireOp",EDGE,"E43.24.0.16")}),1.0]])]});
            var Q438;
            Q438=makeQuery(id+"F6.imprint","IMPRINT",FACE,{"disambiguationData":[TD([[makeQuery(id+"F6.imprint","IMPRINT",EDGE,{"derivedFrom":sQuery(id+"F6.wireOp",EDGE,"E43.29.0.7")}),1.0]])]});
            var Q439;
            Q439=makeQuery(id+"F6.imprint","IMPRINT",FACE,{"disambiguationData":[TD([[makeQuery(id+"F6.imprint","IMPRINT",EDGE,{"derivedFrom":sQuery(id+"F6.wireOp",EDGE,"E513.MirrorC")}),-1.0]])]});
            var Q440;
            Q440=makeQuery(id+"F6.imprint","IMPRINT",FACE,{"disambiguationData":[TD([[makeQuery(id+"F6.imprint","IMPRINT",EDGE,{"derivedFrom":sQuery(id+"F6.wireOp",EDGE,"E43.28.0.16")}),1.0]])]});
            var Q441;
            Q441=makeQuery(id+"F6.imprint","IMPRINT",FACE,{"disambiguationData":[TD([[makeQuery(id+"F6.imprint","IMPRINT",EDGE,{"derivedFrom":sQuery(id+"F6.wireOp",EDGE,"E43.27.0.7")}),1.0]])]});
            var Q442;
            Q442=makeQuery(id+"F6.imprint","IMPRINT",FACE,{"disambiguationData":[TD([[makeQuery(id+"F6.imprint","IMPRINT",EDGE,{"derivedFrom":sQuery(id+"F6.wireOp",EDGE,"E43.31.0.7")}),1.0]])]});
            var Q443;
            Q443=makeQuery(id+"F6.imprint","IMPRINT",FACE,{"disambiguationData":[TD([[makeQuery(id+"F6.imprint","IMPRINT",EDGE,{"derivedFrom":sQuery(id+"F6.wireOp",EDGE,"E43.30.0.16")}),1.0]])]});
            var Q444;
            Q444=makeQuery(id+"F6.imprint","IMPRINT",FACE,{"disambiguationData":[TD([[makeQuery(id+"F6.imprint","IMPRINT",EDGE,{"derivedFrom":sQuery(id+"F6.wireOp",EDGE,"E704.MirrorC")}),-1.0]])]});
            var Q445;
            Q445=makeQuery(id+"F6.imprint","IMPRINT",FACE,{"disambiguationData":[TD([[makeQuery(id+"F6.imprint","IMPRINT",EDGE,{"derivedFrom":sQuery(id+"F6.wireOp",EDGE,"E43.32.0.16")}),1.0]])]});
            var Q446;
            Q446=makeQuery(id+"F6.imprint","IMPRINT",FACE,{"disambiguationData":[TD([[makeQuery(id+"F6.imprint","IMPRINT",EDGE,{"derivedFrom":sQuery(id+"F6.wireOp",EDGE,"E860.MirrorC")}),-1.0]])]});
            var Q447;
            Q447=makeQuery(id+"F6.imprint","IMPRINT",FACE,{"disambiguationData":[TD([[makeQuery(id+"F6.imprint","IMPRINT",EDGE,{"derivedFrom":sQuery(id+"F6.wireOp",EDGE,"E707.MirrorC")}),-1.0]])]});
            var Q448;
            Q448=makeQuery(id+"F6.imprint","IMPRINT",FACE,{"disambiguationData":[TD([[makeQuery(id+"F6.imprint","IMPRINT",EDGE,{"derivedFrom":sQuery(id+"F6.wireOp",EDGE,"E43.9.0.7")}),1.0]])]});
            var Q449;
            Q449=makeQuery(id+"F6.imprint","IMPRINT",FACE,{"disambiguationData":[TD([[makeQuery(id+"F6.imprint","IMPRINT",EDGE,{"derivedFrom":sQuery(id+"F6.wireOp",EDGE,"E43.8.0.16")}),1.0]])]});
            var Q450;
            Q450=makeQuery(id+"F6.imprint","IMPRINT",FACE,{"disambiguationData":[TD([[makeQuery(id+"F6.imprint","IMPRINT",EDGE,{"derivedFrom":sQuery(id+"F6.wireOp",EDGE,"E43.7.0.7")}),1.0]])]});
            var Q451;
            Q451=makeQuery(id+"F6.imprint","IMPRINT",FACE,{"disambiguationData":[TD([[makeQuery(id+"F6.imprint","IMPRINT",EDGE,{"derivedFrom":sQuery(id+"F6.wireOp",EDGE,"E529.MirrorC")}),-1.0]])]});
            var Q452;
            Q452=makeQuery(id+"F6.imprint","IMPRINT",FACE,{"disambiguationData":[TD([[makeQuery(id+"F6.imprint","IMPRINT",EDGE,{"derivedFrom":sQuery(id+"F6.wireOp",EDGE,"E43.11.0.7")}),1.0]])]});
            var Q453;
            Q453=makeQuery(id+"F6.imprint","IMPRINT",FACE,{"disambiguationData":[TD([[makeQuery(id+"F6.imprint","IMPRINT",EDGE,{"derivedFrom":sQuery(id+"F6.wireOp",EDGE,"E43.10.0.16")}),1.0]])]});
            var Q454;
            Q454=makeQuery(id+"F6.imprint","IMPRINT",FACE,{"disambiguationData":[TD([[makeQuery(id+"F6.imprint","IMPRINT",EDGE,{"derivedFrom":sQuery(id+"F6.wireOp",EDGE,"E43.14.0.16")}),1.0]])]});
            var Q455;
            Q455=makeQuery(id+"F6.imprint","IMPRINT",FACE,{"disambiguationData":[TD([[makeQuery(id+"F6.imprint","IMPRINT",EDGE,{"derivedFrom":sQuery(id+"F6.wireOp",EDGE,"E43.13.0.7")}),1.0]])]});
            var Q456;
            Q456=makeQuery(id+"F6.imprint","IMPRINT",FACE,{"disambiguationData":[TD([[makeQuery(id+"F6.imprint","IMPRINT",EDGE,{"derivedFrom":sQuery(id+"F6.wireOp",EDGE,"E43.12.0.16")}),1.0]])]});
            var Q457;
            Q457=makeQuery(id+"F6.imprint","IMPRINT",FACE,{"disambiguationData":[TD([[makeQuery(id+"F6.imprint","IMPRINT",EDGE,{"derivedFrom":sQuery(id+"F6.wireOp",EDGE,"E719.MirrorC")}),-1.0]])]});
            var Q458;
            Q458=makeQuery(id+"F6.imprint","IMPRINT",FACE,{"disambiguationData":[TD([[makeQuery(id+"F6.imprint","IMPRINT",EDGE,{"derivedFrom":sQuery(id+"F6.wireOp",EDGE,"E43.17.0.7")}),1.0]])]});
            var Q459;
            Q459=makeQuery(id+"F6.imprint","IMPRINT",FACE,{"disambiguationData":[TD([[makeQuery(id+"F6.imprint","IMPRINT",EDGE,{"derivedFrom":sQuery(id+"F6.wireOp",EDGE,"E43.16.0.16")}),1.0]])]});
            var Q460;
            Q460=makeQuery(id+"F6.imprint","IMPRINT",FACE,{"disambiguationData":[TD([[makeQuery(id+"F6.imprint","IMPRINT",EDGE,{"derivedFrom":sQuery(id+"F6.wireOp",EDGE,"E43.15.0.7")}),1.0]])]});
            var Q461;
            Q461=makeQuery(id+"F6.imprint","IMPRINT",FACE,{"disambiguationData":[TD([[makeQuery(id+"F6.imprint","IMPRINT",EDGE,{"derivedFrom":sQuery(id+"F6.wireOp",EDGE,"E43.18.0.16")}),1.0]])]});
            var Q462;
            Q462=makeQuery(id+"F6.imprint","IMPRINT",FACE,{"disambiguationData":[TD([[makeQuery(id+"F6.imprint","IMPRINT",EDGE,{"derivedFrom":sQuery(id+"F6.wireOp",EDGE,"E43.21.0.7")}),1.0]])]});
            var Q463;
            Q463=makeQuery(id+"F6.imprint","IMPRINT",FACE,{"disambiguationData":[TD([[makeQuery(id+"F6.imprint","IMPRINT",EDGE,{"derivedFrom":sQuery(id+"F6.wireOp",EDGE,"E43.20.0.16")}),1.0]])]});
            var Q464;
            Q464=makeQuery(id+"F6.imprint","IMPRINT",FACE,{"disambiguationData":[TD([[makeQuery(id+"F6.imprint","IMPRINT",EDGE,{"derivedFrom":sQuery(id+"F6.wireOp",EDGE,"E43.19.0.7")}),1.0]])]});
            var Q465;
            Q465=makeQuery(id+"F6.imprint","IMPRINT",FACE,{"disambiguationData":[TD([[makeQuery(id+"F6.imprint","IMPRINT",EDGE,{"derivedFrom":sQuery(id+"F6.wireOp",EDGE,"E722.MirrorC")}),-1.0]])]});
            var Q466;
            Q466=makeQuery(id+"F6.imprint","IMPRINT",FACE,{"disambiguationData":[TD([[makeQuery(id+"F6.imprint","IMPRINT",EDGE,{"derivedFrom":sQuery(id+"F6.wireOp",EDGE,"E43.23.0.7")}),1.0]])]});
            var Q467;
            Q467=makeQuery(id+"F6.imprint","IMPRINT",FACE,{"disambiguationData":[TD([[makeQuery(id+"F6.imprint","IMPRINT",EDGE,{"derivedFrom":sQuery(id+"F6.wireOp",EDGE,"E43.22.0.16")}),1.0]])]});
            var Q468;
            Q468=makeQuery(id+"F6.imprint","IMPRINT",FACE,{"disambiguationData":[TD([[makeQuery(id+"F6.imprint","IMPRINT",EDGE,{"derivedFrom":sQuery(id+"F6.wireOp",EDGE,"E339.MirrorC")}),-1.0]])]});
            var Q469;
            Q469=makeQuery(id+"F6.imprint","IMPRINT",FACE,{"disambiguationData":[TD([[makeQuery(id+"F6.imprint","IMPRINT",EDGE,{"derivedFrom":sQuery(id+"F6.wireOp",EDGE,"E247.MirrorC")}),-1.0]])]});
            var Q470;
            Q470=makeQuery(id+"F6.imprint","IMPRINT",FACE,{"disambiguationData":[TD([[makeQuery(id+"F6.imprint","IMPRINT",EDGE,{"derivedFrom":sQuery(id+"F6.wireOp",EDGE,"E483.MirrorC")}),-1.0]])]});
            var Q471;
            Q471=makeQuery(id+"F6.imprint","IMPRINT",FACE,{"disambiguationData":[TD([[makeQuery(id+"F6.imprint","IMPRINT",EDGE,{"derivedFrom":sQuery(id+"F6.wireOp",EDGE,"E673.MirrorC")}),-1.0]])]});
            var Q472;
            Q472=makeQuery(id+"F6.imprint","IMPRINT",FACE,{"disambiguationData":[TD([[makeQuery(id+"F6.imprint","IMPRINT",EDGE,{"derivedFrom":sQuery(id+"F6.wireOp",EDGE,"E308.MirrorC")}),-1.0]])]});
            var Q473;
            Q473=makeQuery(id+"F6.imprint","IMPRINT",FACE,{"disambiguationData":[TD([[makeQuery(id+"F6.imprint","IMPRINT",EDGE,{"derivedFrom":sQuery(id+"F6.wireOp",EDGE,"E292.MirrorC")}),-1.0]])]});
            var Q474;
            Q474=makeQuery(id+"F6.imprint","IMPRINT",FACE,{"disambiguationData":[TD([[makeQuery(id+"F6.imprint","IMPRINT",EDGE,{"derivedFrom":sQuery(id+"F6.wireOp",EDGE,"E276.MirrorC")}),-1.0]])]});
            var Q475;
            Q475=makeQuery(id+"F6.imprint","IMPRINT",FACE,{"disambiguationData":[TD([[makeQuery(id+"F6.imprint","IMPRINT",EDGE,{"derivedFrom":sQuery(id+"F6.wireOp",EDGE,"E43.1.0.8")}),1.0]])]});
            var Q476;
            Q476=makeQuery(id+"F6.imprint","IMPRINT",FACE,{"disambiguationData":[TD([[makeQuery(id+"F6.imprint","IMPRINT",EDGE,{"derivedFrom":sQuery(id+"F6.wireOp",EDGE,"E830.MirrorC")}),-1.0]])]});
            var Q477;
            Q477=makeQuery(id+"F6.imprint","IMPRINT",FACE,{"disambiguationData":[TD([[makeQuery(id+"F6.imprint","IMPRINT",EDGE,{"derivedFrom":sQuery(id+"F6.wireOp",EDGE,"E43.3.0.8")}),1.0]])]});
            var Q478;
            Q478=makeQuery(id+"F6.imprint","IMPRINT",FACE,{"disambiguationData":[TD([[makeQuery(id+"F6.imprint","IMPRINT",EDGE,{"derivedFrom":sQuery(id+"F6.wireOp",EDGE,"E43.2.0.17")}),1.0]])]});
            var Q479;
            Q479=makeQuery(id+"F6.imprint","IMPRINT",FACE,{"disambiguationData":[TD([[makeQuery(id+"F6.imprint","IMPRINT",EDGE,{"derivedFrom":sQuery(id+"F6.wireOp",EDGE,"E882.MirrorC")}),-1.0]])]});
            var Q480;
            Q480=makeQuery(id+"F6.imprint","IMPRINT",FACE,{"disambiguationData":[TD([[makeQuery(id+"F6.imprint","IMPRINT",EDGE,{"derivedFrom":sQuery(id+"F6.wireOp",EDGE,"E43.6.0.17")}),1.0]])]});
            var Q481;
            Q481=makeQuery(id+"F6.imprint","IMPRINT",FACE,{"disambiguationData":[TD([[makeQuery(id+"F6.imprint","IMPRINT",EDGE,{"derivedFrom":sQuery(id+"F6.wireOp",EDGE,"E676.MirrorC")}),-1.0]])]});
            var Q482;
            Q482=makeQuery(id+"F6.imprint","IMPRINT",FACE,{"disambiguationData":[TD([[makeQuery(id+"F6.imprint","IMPRINT",EDGE,{"derivedFrom":sQuery(id+"F6.wireOp",EDGE,"E43.5.0.8")}),1.0]])]});
            var Q483;
            Q483=makeQuery(id+"F6.imprint","IMPRINT",FACE,{"disambiguationData":[TD([[makeQuery(id+"F6.imprint","IMPRINT",EDGE,{"derivedFrom":sQuery(id+"F6.wireOp",EDGE,"E43.4.0.17")}),1.0]])]});
            var Q484;
            Q484=makeQuery(id+"F6.imprint","IMPRINT",FACE,{"disambiguationData":[TD([[makeQuery(id+"F6.imprint","IMPRINT",EDGE,{"derivedFrom":sQuery(id+"F6.wireOp",EDGE,"E43.9.0.8")}),1.0]])]});
            var Q485;
            Q485=makeQuery(id+"F6.imprint","IMPRINT",FACE,{"disambiguationData":[TD([[makeQuery(id+"F6.imprint","IMPRINT",EDGE,{"derivedFrom":sQuery(id+"F6.wireOp",EDGE,"E43.8.0.17")}),1.0]])]});
            var Q486;
            Q486=makeQuery(id+"F6.imprint","IMPRINT",FACE,{"disambiguationData":[TD([[makeQuery(id+"F6.imprint","IMPRINT",EDGE,{"derivedFrom":sQuery(id+"F6.wireOp",EDGE,"E729.MirrorC")}),-1.0]])]});
            var Q487;
            Q487=makeQuery(id+"F6.imprint","IMPRINT",FACE,{"disambiguationData":[TD([[makeQuery(id+"F6.imprint","IMPRINT",EDGE,{"derivedFrom":sQuery(id+"F6.wireOp",EDGE,"E43.7.0.8")}),1.0]])]});
            var Q488;
            Q488=makeQuery(id+"F6.imprint","IMPRINT",FACE,{"disambiguationData":[TD([[makeQuery(id+"F6.imprint","IMPRINT",EDGE,{"derivedFrom":sQuery(id+"F6.wireOp",EDGE,"E498.MirrorC")}),-1.0]])]});
            var Q489;
            Q489=makeQuery(id+"F6.imprint","IMPRINT",FACE,{"disambiguationData":[TD([[makeQuery(id+"F6.imprint","IMPRINT",EDGE,{"derivedFrom":sQuery(id+"F6.wireOp",EDGE,"E689.MirrorC")}),-1.0]])]});
            var Q490;
            Q490=makeQuery(id+"F6.imprint","IMPRINT",FACE,{"disambiguationData":[TD([[makeQuery(id+"F6.imprint","IMPRINT",EDGE,{"derivedFrom":sQuery(id+"F6.wireOp",EDGE,"E845.MirrorC")}),-1.0]])]});
            var Q491;
            Q491=makeQuery(id+"F6.imprint","IMPRINT",FACE,{"disambiguationData":[TD([[makeQuery(id+"F6.imprint","IMPRINT",EDGE,{"derivedFrom":sQuery(id+"F6.wireOp",EDGE,"E898.MirrorC")}),-1.0]])]});
            var Q492;
            Q492=makeQuery(id+"F6.imprint","IMPRINT",FACE,{"disambiguationData":[TD([[makeQuery(id+"F6.imprint","IMPRINT",EDGE,{"derivedFrom":sQuery(id+"F6.wireOp",EDGE,"E691.MirrorC")}),-1.0]])]});
            var Q493;
            Q493=makeQuery(id+"F6.imprint","IMPRINT",FACE,{"disambiguationData":[TD([[makeQuery(id+"F6.imprint","IMPRINT",EDGE,{"derivedFrom":sQuery(id+"F6.wireOp",EDGE,"E323.MirrorC")}),-1.0]])]});
            var Q494;
            Q494=makeQuery(id+"F6.imprint","IMPRINT",FACE,{"disambiguationData":[TD([[makeQuery(id+"F6.imprint","IMPRINT",EDGE,{"derivedFrom":sQuery(id+"F6.wireOp",EDGE,"E43.29.0.8")}),1.0]])]});
            var Q495;
            Q495=makeQuery(id+"F6.imprint","IMPRINT",FACE,{"disambiguationData":[TD([[makeQuery(id+"F6.imprint","IMPRINT",EDGE,{"derivedFrom":sQuery(id+"F6.wireOp",EDGE,"E43.28.0.17")}),1.0]])]});
            var Q496;
            Q496=makeQuery(id+"F6.imprint","IMPRINT",FACE,{"disambiguationData":[TD([[makeQuery(id+"F6.imprint","IMPRINT",EDGE,{"derivedFrom":sQuery(id+"F6.wireOp",EDGE,"E43.27.0.8")}),1.0]])]});
            var Q497;
            Q497=makeQuery(id+"F6.imprint","IMPRINT",FACE,{"disambiguationData":[TD([[makeQuery(id+"F6.imprint","IMPRINT",EDGE,{"derivedFrom":sQuery(id+"F6.wireOp",EDGE,"E43.31.0.8")}),1.0]])]});
            var Q498;
            Q498=makeQuery(id+"F6.imprint","IMPRINT",FACE,{"disambiguationData":[TD([[makeQuery(id+"F6.imprint","IMPRINT",EDGE,{"derivedFrom":sQuery(id+"F6.wireOp",EDGE,"E43.30.0.17")}),1.0]])]});
            var Q499;
            Q499=makeQuery(id+"F6.imprint","IMPRINT",FACE,{"disambiguationData":[TD([[makeQuery(id+"F6.imprint","IMPRINT",EDGE,{"derivedFrom":sQuery(id+"F6.wireOp",EDGE,"E43.32.0.17")}),1.0]])]});
            var Q500;
            Q500=makeQuery(id+"F6.imprint","IMPRINT",FACE,{"disambiguationData":[TD([[makeQuery(id+"F6.imprint","IMPRINT",EDGE,{"derivedFrom":sQuery(id+"F6.wireOp",EDGE,"E575.MirrorC")}),-1.0]])]});
            var Q501;
            Q501=makeQuery(id+"F6.imprint","IMPRINT",FACE,{"disambiguationData":[TD([[makeQuery(id+"F6.imprint","IMPRINT",EDGE,{"derivedFrom":sQuery(id+"F6.wireOp",EDGE,"E43.11.0.8")}),1.0]])]});
            var Q502;
            Q502=makeQuery(id+"F6.imprint","IMPRINT",FACE,{"disambiguationData":[TD([[makeQuery(id+"F6.imprint","IMPRINT",EDGE,{"derivedFrom":sQuery(id+"F6.wireOp",EDGE,"E43.10.0.17")}),1.0]])]});
            var Q503;
            Q503=makeQuery(id+"F6.imprint","IMPRINT",FACE,{"disambiguationData":[TD([[makeQuery(id+"F6.imprint","IMPRINT",EDGE,{"derivedFrom":sQuery(id+"F6.wireOp",EDGE,"E43.14.0.17")}),1.0]])]});
            var Q504;
            Q504=makeQuery(id+"F6.imprint","IMPRINT",FACE,{"disambiguationData":[TD([[makeQuery(id+"F6.imprint","IMPRINT",EDGE,{"derivedFrom":sQuery(id+"F6.wireOp",EDGE,"E43.13.0.8")}),1.0]])]});
            var Q505;
            Q505=makeQuery(id+"F6.imprint","IMPRINT",FACE,{"disambiguationData":[TD([[makeQuery(id+"F6.imprint","IMPRINT",EDGE,{"derivedFrom":sQuery(id+"F6.wireOp",EDGE,"E43.12.0.17")}),1.0]])]});
            var Q506;
            Q506=makeQuery(id+"F6.imprint","IMPRINT",FACE,{"disambiguationData":[TD([[makeQuery(id+"F6.imprint","IMPRINT",EDGE,{"derivedFrom":sQuery(id+"F6.wireOp",EDGE,"E43.17.0.8")}),1.0]])]});
            var Q507;
            Q507=makeQuery(id+"F6.imprint","IMPRINT",FACE,{"disambiguationData":[TD([[makeQuery(id+"F6.imprint","IMPRINT",EDGE,{"derivedFrom":sQuery(id+"F6.wireOp",EDGE,"E43.16.0.17")}),1.0]])]});
            var Q508;
            Q508=makeQuery(id+"F6.imprint","IMPRINT",FACE,{"disambiguationData":[TD([[makeQuery(id+"F6.imprint","IMPRINT",EDGE,{"derivedFrom":sQuery(id+"F6.wireOp",EDGE,"E43.15.0.8")}),1.0]])]});
            var Q509;
            Q509=makeQuery(id+"F6.imprint","IMPRINT",FACE,{"disambiguationData":[TD([[makeQuery(id+"F6.imprint","IMPRINT",EDGE,{"derivedFrom":sQuery(id+"F6.wireOp",EDGE,"E43.18.0.17")}),1.0]])]});
            var Q510;
            Q510=makeQuery(id+"F6.imprint","IMPRINT",FACE,{"disambiguationData":[TD([[makeQuery(id+"F6.imprint","IMPRINT",EDGE,{"derivedFrom":sQuery(id+"F6.wireOp",EDGE,"E744.MirrorC")}),-1.0]])]});
            var Q511;
            Q511=makeQuery(id+"F6.imprint","IMPRINT",FACE,{"disambiguationData":[TD([[makeQuery(id+"F6.imprint","IMPRINT",EDGE,{"derivedFrom":sQuery(id+"F6.wireOp",EDGE,"E43.21.0.8")}),1.0]])]});
            var Q512;
            Q512=makeQuery(id+"F6.imprint","IMPRINT",FACE,{"disambiguationData":[TD([[makeQuery(id+"F6.imprint","IMPRINT",EDGE,{"derivedFrom":sQuery(id+"F6.wireOp",EDGE,"E43.20.0.17")}),1.0]])]});
            var Q513;
            Q513=makeQuery(id+"F6.imprint","IMPRINT",FACE,{"disambiguationData":[TD([[makeQuery(id+"F6.imprint","IMPRINT",EDGE,{"derivedFrom":sQuery(id+"F6.wireOp",EDGE,"E43.19.0.8")}),1.0]])]});
            var Q514;
            Q514=makeQuery(id+"F6.imprint","IMPRINT",FACE,{"disambiguationData":[TD([[makeQuery(id+"F6.imprint","IMPRINT",EDGE,{"derivedFrom":sQuery(id+"F6.wireOp",EDGE,"E591.MirrorC")}),-1.0]])]});
            var Q515;
            Q515=makeQuery(id+"F6.imprint","IMPRINT",FACE,{"disambiguationData":[TD([[makeQuery(id+"F6.imprint","IMPRINT",EDGE,{"derivedFrom":sQuery(id+"F6.wireOp",EDGE,"E43.23.0.8")}),1.0]])]});
            var Q516;
            Q516=makeQuery(id+"F6.imprint","IMPRINT",FACE,{"disambiguationData":[TD([[makeQuery(id+"F6.imprint","IMPRINT",EDGE,{"derivedFrom":sQuery(id+"F6.wireOp",EDGE,"E43.22.0.17")}),1.0]])]});
            var Q517;
            Q517=makeQuery(id+"F6.imprint","IMPRINT",FACE,{"disambiguationData":[TD([[makeQuery(id+"F6.imprint","IMPRINT",EDGE,{"derivedFrom":sQuery(id+"F6.wireOp",EDGE,"E43.26.0.17")}),1.0]])]});
            var Q518;
            Q518=makeQuery(id+"F6.imprint","IMPRINT",FACE,{"disambiguationData":[TD([[makeQuery(id+"F6.imprint","IMPRINT",EDGE,{"derivedFrom":sQuery(id+"F6.wireOp",EDGE,"E43.25.0.8")}),1.0]])]});
            var Q519;
            Q519=makeQuery(id+"F6.imprint","IMPRINT",FACE,{"disambiguationData":[TD([[makeQuery(id+"F6.imprint","IMPRINT",EDGE,{"derivedFrom":sQuery(id+"F6.wireOp",EDGE,"E43.24.0.17")}),1.0]])]});
            var Q520;
            Q520=makeQuery(id+"F6.imprint","IMPRINT",FACE,{"disambiguationData":[TD([[makeQuery(id+"F6.imprint","IMPRINT",EDGE,{"derivedFrom":sQuery(id+"F6.wireOp",EDGE,"E734.MirrorC")}),-1.0]])]});
            var Q521;
            Q521=makeQuery(id+"F6.imprint","IMPRINT",FACE,{"disambiguationData":[TD([[makeQuery(id+"F6.imprint","IMPRINT",EDGE,{"derivedFrom":sQuery(id+"F6.wireOp",EDGE,"E891.MirrorC")}),-1.0]])]});
            var Q522;
            Q522=makeQuery(id+"F6.imprint","IMPRINT",FACE,{"disambiguationData":[TD([[makeQuery(id+"F6.imprint","IMPRINT",EDGE,{"derivedFrom":sQuery(id+"F6.wireOp",EDGE,"E544.MirrorC")}),-1.0]])]});
            var Q523;
            Q523=makeQuery(id+"F6.imprint","IMPRINT",FACE,{"disambiguationData":[TD([[makeQuery(id+"F6.imprint","IMPRINT",EDGE,{"derivedFrom":sQuery(id+"F6.wireOp",EDGE,"E559.MirrorC")}),-1.0]])]});
            var Q524;
            Q524=makeQuery(id+"F6.imprint","IMPRINT",FACE,{"disambiguationData":[TD([[makeQuery(id+"F6.imprint","IMPRINT",EDGE,{"derivedFrom":sQuery(id+"F6.wireOp",EDGE,"E790.MirrorC")}),-1.0]])]});
            var Q525;
            Q525=makeQuery(id+"F6.imprint","IMPRINT",FACE,{"disambiguationData":[TD([[makeQuery(id+"F6.imprint","IMPRINT",EDGE,{"derivedFrom":sQuery(id+"F6.wireOp",EDGE,"E737.MirrorC")}),-1.0]])]});
            var Q526;
            Q526=makeQuery(id+"F6.imprint","IMPRINT",FACE,{"disambiguationData":[TD([[makeQuery(id+"F6.imprint","IMPRINT",EDGE,{"derivedFrom":sQuery(id+"F6.wireOp",EDGE,"E635.MirrorC")}),-1.0]])]});
            var Q527;
            Q527=makeQuery(id+"F6.imprint","IMPRINT",FACE,{"disambiguationData":[TD([[makeQuery(id+"F6.imprint","IMPRINT",EDGE,{"derivedFrom":sQuery(id+"F6.wireOp",EDGE,"E750.MirrorC")}),-1.0]])]});
            var Q528;
            Q528=makeQuery(id+"F6.imprint","IMPRINT",FACE,{"disambiguationData":[TD([[makeQuery(id+"F6.imprint","IMPRINT",EDGE,{"derivedFrom":sQuery(id+"F6.wireOp",EDGE,"E820.MirrorC")}),-1.0]])]});
            var Q529;
            Q529=makeQuery(id+"F6.imprint","IMPRINT",FACE,{"disambiguationData":[TD([[makeQuery(id+"F6.imprint","IMPRINT",EDGE,{"derivedFrom":sQuery(id+"F6.wireOp",EDGE,"E753.MirrorC")}),-1.0]])]});
            var Q530;
            Q530=makeQuery(id+"F6.imprint","IMPRINT",FACE,{"disambiguationData":[TD([[makeQuery(id+"F6.imprint","IMPRINT",EDGE,{"derivedFrom":sQuery(id+"F6.wireOp",EDGE,"E805.MirrorC")}),-1.0]])]});
            var Q531;
            Q531=makeQuery(id+"F6.imprint","IMPRINT",FACE,{"disambiguationData":[TD([[makeQuery(id+"F6.imprint","IMPRINT",EDGE,{"derivedFrom":sQuery(id+"F6.wireOp",EDGE,"E650.MirrorC")}),-1.0]])]});
            var Q532;
            Q532=makeQuery(id+"F6.imprint","IMPRINT",FACE,{"disambiguationData":[TD([[makeQuery(id+"F6.imprint","IMPRINT",EDGE,{"derivedFrom":sQuery(id+"F6.wireOp",EDGE,"E759.MirrorC")}),-1.0]])]});
            var Q533;
            Q533=makeQuery(id+"F6.imprint","IMPRINT",FACE,{"disambiguationData":[TD([[makeQuery(id+"F6.imprint","IMPRINT",EDGE,{"derivedFrom":sQuery(id+"F6.wireOp",EDGE,"E605.MirrorC")}),-1.0]])]});
            var Q534;
            Q534=makeQuery(id+"F6.imprint","IMPRINT",FACE,{"disambiguationData":[TD([[makeQuery(id+"F6.imprint","IMPRINT",EDGE,{"derivedFrom":sQuery(id+"F6.wireOp",EDGE,"E775.MirrorC")}),-1.0]])]});
            var Q535;
            Q535=makeQuery(id+"F6.imprint","IMPRINT",FACE,{"disambiguationData":[TD([[makeQuery(id+"F6.imprint","IMPRINT",EDGE,{"derivedFrom":sQuery(id+"F6.wireOp",EDGE,"E620.MirrorC")}),-1.0]])]});
            var Q536;
            Q536=makeQuery(id+"F6.imprint","IMPRINT",FACE,{"disambiguationData":[TD([[makeQuery(id+"F6.imprint","IMPRINT",EDGE,{"derivedFrom":sQuery(id+"F6.wireOp",EDGE,"E813.MirrorC")}),-1.0]])]});
            var Q537;
            Q537=makeQuery(id+"F6.imprint","IMPRINT",FACE,{"disambiguationData":[TD([[makeQuery(id+"F6.imprint","IMPRINT",EDGE,{"derivedFrom":sQuery(id+"F6.wireOp",EDGE,"E865.MirrorC")}),-1.0]])]});
            var Q538;
            Q538=makeQuery(id+"F6.imprint","IMPRINT",FACE,{"disambiguationData":[TD([[makeQuery(id+"F6.imprint","IMPRINT",EDGE,{"derivedFrom":sQuery(id+"F6.wireOp",EDGE,"E696.MirrorC")}),-1.0]])]});
            var Q539;
            Q539=makeQuery(id+"F6.imprint","IMPRINT",FACE,{"disambiguationData":[TD([[makeQuery(id+"F6.imprint","IMPRINT",EDGE,{"derivedFrom":sQuery(id+"F6.wireOp",EDGE,"E795.MirrorC")}),-1.0]])]});
            var Q540;
            Q540=makeQuery(id+"F6.imprint","IMPRINT",FACE,{"disambiguationData":[TD([[makeQuery(id+"F6.imprint","IMPRINT",EDGE,{"derivedFrom":sQuery(id+"F6.wireOp",EDGE,"E828.MirrorC")}),-1.0]])]});
            var Q541;
            Q541=makeQuery(id+"F6.imprint","IMPRINT",FACE,{"disambiguationData":[TD([[makeQuery(id+"F6.imprint","IMPRINT",EDGE,{"derivedFrom":sQuery(id+"F6.wireOp",EDGE,"E880.MirrorC")}),-1.0]])]});
            var Q542;
            Q542=makeQuery(id+"F6.imprint","IMPRINT",FACE,{"disambiguationData":[TD([[makeQuery(id+"F6.imprint","IMPRINT",EDGE,{"derivedFrom":sQuery(id+"F6.wireOp",EDGE,"E711.MirrorC")}),-1.0]])]});
            var Q543;
            Q543=makeQuery(id+"F6.imprint","IMPRINT",FACE,{"disambiguationData":[TD([[makeQuery(id+"F6.imprint","IMPRINT",EDGE,{"derivedFrom":sQuery(id+"F6.wireOp",EDGE,"E811.MirrorC")}),-1.0]])]});
            var Q544;
            Q544=makeQuery(id+"F6.imprint","IMPRINT",FACE,{"disambiguationData":[TD([[makeQuery(id+"F6.imprint","IMPRINT",EDGE,{"derivedFrom":sQuery(id+"F6.wireOp",EDGE,"E765.MirrorC")}),-1.0]])]});
            var Q545;
            Q545=makeQuery(id+"F6.imprint","IMPRINT",FACE,{"disambiguationData":[TD([[makeQuery(id+"F6.imprint","IMPRINT",EDGE,{"derivedFrom":sQuery(id+"F6.wireOp",EDGE,"E783.MirrorC")}),-1.0]])]});
            var Q546;
            Q546=makeQuery(id+"F6.imprint","IMPRINT",FACE,{"disambiguationData":[TD([[makeQuery(id+"F6.imprint","IMPRINT",EDGE,{"derivedFrom":sQuery(id+"F6.wireOp",EDGE,"E834.MirrorC")}),-1.0]])]});
            var Q547;
            Q547=makeQuery(id+"F6.imprint","IMPRINT",FACE,{"disambiguationData":[TD([[makeQuery(id+"F6.imprint","IMPRINT",EDGE,{"derivedFrom":sQuery(id+"F6.wireOp",EDGE,"E310.MirrorC")}),-1.0]])]});
            var Q548;
            Q548=makeQuery(id+"F6.imprint","IMPRINT",FACE,{"disambiguationData":[TD([[makeQuery(id+"F6.imprint","IMPRINT",EDGE,{"derivedFrom":sQuery(id+"F6.wireOp",EDGE,"E325.MirrorC")}),-1.0]])]});
            var Q549;
            Q549=makeQuery(id+"F6.imprint","IMPRINT",FACE,{"disambiguationData":[TD([[makeQuery(id+"F6.imprint","IMPRINT",EDGE,{"derivedFrom":sQuery(id+"F6.wireOp",EDGE,"E665.MirrorC")}),-1.0]])]});
            var Q550;
            Q550=makeQuery(id+"F6.imprint","IMPRINT",FACE,{"disambiguationData":[TD([[makeQuery(id+"F6.imprint","IMPRINT",EDGE,{"derivedFrom":sQuery(id+"F6.wireOp",EDGE,"E768.MirrorC")}),-1.0]])]});
            var Q551;
            Q551=makeQuery(id+"F6.imprint","IMPRINT",FACE,{"disambiguationData":[TD([[makeQuery(id+"F6.imprint","IMPRINT",EDGE,{"derivedFrom":sQuery(id+"F6.wireOp",EDGE,"E262.MirrorC")}),-1.0]])]});
            var Q552;
            Q552=makeQuery(id+"F6.imprint","IMPRINT",FACE,{"disambiguationData":[TD([[makeQuery(id+"F6.imprint","IMPRINT",EDGE,{"derivedFrom":sQuery(id+"F6.wireOp",EDGE,"E249.MirrorC")}),-1.0]])]});
            var Q553;
            Q553=makeQuery(id+"F6.imprint","IMPRINT",FACE,{"disambiguationData":[TD([[makeQuery(id+"F6.imprint","IMPRINT",EDGE,{"derivedFrom":sQuery(id+"F6.wireOp",EDGE,"E294.MirrorC")}),-1.0]])]});
            var Q554;
            Q554=makeQuery(id+"F6.imprint","IMPRINT",FACE,{"disambiguationData":[TD([[makeQuery(id+"F6.imprint","IMPRINT",EDGE,{"derivedFrom":sQuery(id+"F6.wireOp",EDGE,"E278.MirrorC")}),-1.0]])]});
            var Q555;
            Q555=makeQuery(id+"F6.imprint","IMPRINT",FACE,{"disambiguationData":[TD([[makeQuery(id+"F6.imprint","IMPRINT",EDGE,{"derivedFrom":sQuery(id+"F6.wireOp",EDGE,"E850.MirrorC")}),-1.0]])]});
            var Q556;
            Q556=makeQuery(id+"F6.imprint","IMPRINT",FACE,{"disambiguationData":[TD([[makeQuery(id+"F6.imprint","IMPRINT",EDGE,{"derivedFrom":sQuery(id+"F6.wireOp",EDGE,"E798.MirrorC")}),-1.0]])]});
            var Q557;
            Q557=makeQuery(id+"F6.imprint","IMPRINT",FACE,{"disambiguationData":[TD([[makeQuery(id+"F6.imprint","IMPRINT",EDGE,{"derivedFrom":sQuery(id+"F6.wireOp",EDGE,"E681.MirrorC")}),-1.0]])]});
            var Q558;
            Q558=makeQuery(id+"F6.imprint","IMPRINT",FACE,{"disambiguationData":[TD([[makeQuery(id+"F6.imprint","IMPRINT",EDGE,{"derivedFrom":sQuery(id+"F6.wireOp",EDGE,"E780.MirrorC")}),-1.0]])]});
            var Q559;
            Q559=makeQuery(id+"F6.imprint","IMPRINT",FACE,{"disambiguationData":[TD([[makeQuery(id+"F6.imprint","IMPRINT",EDGE,{"derivedFrom":sQuery(id+"F6.wireOp",EDGE,"E43.18.0.19")}),1.0]])]});
            var Q560;
            Q560=makeQuery(id+"F6.imprint","IMPRINT",FACE,{"disambiguationData":[TD([[makeQuery(id+"F6.imprint","IMPRINT",EDGE,{"derivedFrom":sQuery(id+"F6.wireOp",EDGE,"E43.18.0.1")}),1.0]])]});
            var Q561;
            Q561=makeQuery(id+"F6.imprint","IMPRINT",FACE,{"disambiguationData":[TD([[makeQuery(id+"F6.imprint","IMPRINT",EDGE,{"derivedFrom":sQuery(id+"F6.wireOp",EDGE,"E43.17.0.10")}),1.0]])]});
            var Q562;
            Q562=makeQuery(id+"F6.imprint","IMPRINT",FACE,{"disambiguationData":[TD([[makeQuery(id+"F6.imprint","IMPRINT",EDGE,{"derivedFrom":sQuery(id+"F6.wireOp",EDGE,"E43.21.0.10")}),1.0]])]});
            var Q563;
            Q563=makeQuery(id+"F6.imprint","IMPRINT",FACE,{"disambiguationData":[TD([[makeQuery(id+"F6.imprint","IMPRINT",EDGE,{"derivedFrom":sQuery(id+"F6.wireOp",EDGE,"E43.20.0.19")}),1.0]])]});
            var Q564;
            Q564=makeQuery(id+"F6.imprint","IMPRINT",FACE,{"disambiguationData":[TD([[makeQuery(id+"F6.imprint","IMPRINT",EDGE,{"derivedFrom":sQuery(id+"F6.wireOp",EDGE,"E43.20.0.1")}),1.0]])]});
            var Q565;
            Q565=makeQuery(id+"F6.imprint","IMPRINT",FACE,{"disambiguationData":[TD([[makeQuery(id+"F6.imprint","IMPRINT",EDGE,{"derivedFrom":sQuery(id+"F6.wireOp",EDGE,"E43.19.0.10")}),1.0]])]});
            var Q566;
            Q566=makeQuery(id+"F6.imprint","IMPRINT",FACE,{"disambiguationData":[TD([[makeQuery(id+"F6.imprint","IMPRINT",EDGE,{"derivedFrom":sQuery(id+"F6.wireOp",EDGE,"E43.24.0.1")}),1.0]])]});
            var Q567;
            Q567=makeQuery(id+"F6.imprint","IMPRINT",FACE,{"disambiguationData":[TD([[makeQuery(id+"F6.imprint","IMPRINT",EDGE,{"derivedFrom":sQuery(id+"F6.wireOp",EDGE,"E43.23.0.10")}),1.0]])]});
            var Q568;
            Q568=makeQuery(id+"F6.imprint","IMPRINT",FACE,{"disambiguationData":[TD([[makeQuery(id+"F6.imprint","IMPRINT",EDGE,{"derivedFrom":sQuery(id+"F6.wireOp",EDGE,"E43.22.0.19")}),1.0]])]});
            var Q569;
            Q569=makeQuery(id+"F6.imprint","IMPRINT",FACE,{"disambiguationData":[TD([[makeQuery(id+"F6.imprint","IMPRINT",EDGE,{"derivedFrom":sQuery(id+"F6.wireOp",EDGE,"E43.22.0.1")}),1.0]])]});
            var Q570;
            Q570=makeQuery(id+"F6.imprint","IMPRINT",FACE,{"disambiguationData":[TD([[makeQuery(id+"F6.imprint","IMPRINT",EDGE,{"derivedFrom":sQuery(id+"F6.wireOp",EDGE,"E43.26.0.19")}),1.0]])]});
            var Q571;
            Q571=makeQuery(id+"F6.imprint","IMPRINT",FACE,{"disambiguationData":[TD([[makeQuery(id+"F6.imprint","IMPRINT",EDGE,{"derivedFrom":sQuery(id+"F6.wireOp",EDGE,"E43.26.0.1")}),1.0]])]});
            var Q572;
            Q572=makeQuery(id+"F6.imprint","IMPRINT",FACE,{"disambiguationData":[TD([[makeQuery(id+"F6.imprint","IMPRINT",EDGE,{"derivedFrom":sQuery(id+"F6.wireOp",EDGE,"E43.25.0.10")}),1.0]])]});
            var Q573;
            Q573=makeQuery(id+"F6.imprint","IMPRINT",FACE,{"disambiguationData":[TD([[makeQuery(id+"F6.imprint","IMPRINT",EDGE,{"derivedFrom":sQuery(id+"F6.wireOp",EDGE,"E43.24.0.19")}),1.0]])]});
            var Q574;
            Q574=makeQuery(id+"F6.imprint","IMPRINT",FACE,{"disambiguationData":[TD([[makeQuery(id+"F6.imprint","IMPRINT",EDGE,{"derivedFrom":sQuery(id+"F6.wireOp",EDGE,"E43.29.0.10")}),1.0]])]});
            var Q575;
            Q575=makeQuery(id+"F6.imprint","IMPRINT",FACE,{"disambiguationData":[TD([[makeQuery(id+"F6.imprint","IMPRINT",EDGE,{"derivedFrom":sQuery(id+"F6.wireOp",EDGE,"E43.28.0.19")}),1.0]])]});
            var Q576;
            Q576=makeQuery(id+"F6.imprint","IMPRINT",FACE,{"disambiguationData":[TD([[makeQuery(id+"F6.imprint","IMPRINT",EDGE,{"derivedFrom":sQuery(id+"F6.wireOp",EDGE,"E43.28.0.1")}),1.0]])]});
            var Q577;
            Q577=makeQuery(id+"F6.imprint","IMPRINT",FACE,{"disambiguationData":[TD([[makeQuery(id+"F6.imprint","IMPRINT",EDGE,{"derivedFrom":sQuery(id+"F6.wireOp",EDGE,"E43.27.0.10")}),1.0]])]});
            var Q578;
            Q578=makeQuery(id+"F6.imprint","IMPRINT",FACE,{"disambiguationData":[TD([[makeQuery(id+"F6.imprint","IMPRINT",EDGE,{"derivedFrom":sQuery(id+"F6.wireOp",EDGE,"E43.32.0.1")}),1.0]])]});
            var Q579;
            Q579=makeQuery(id+"F6.imprint","IMPRINT",FACE,{"disambiguationData":[TD([[makeQuery(id+"F6.imprint","IMPRINT",EDGE,{"derivedFrom":sQuery(id+"F6.wireOp",EDGE,"E43.31.0.10")}),1.0]])]});
            var Q580;
            Q580=makeQuery(id+"F6.imprint","IMPRINT",FACE,{"disambiguationData":[TD([[makeQuery(id+"F6.imprint","IMPRINT",EDGE,{"derivedFrom":sQuery(id+"F6.wireOp",EDGE,"E43.30.0.19")}),1.0]])]});
            var Q581;
            Q581=makeQuery(id+"F6.imprint","IMPRINT",FACE,{"disambiguationData":[TD([[makeQuery(id+"F6.imprint","IMPRINT",EDGE,{"derivedFrom":sQuery(id+"F6.wireOp",EDGE,"E43.30.0.1")}),1.0]])]});
            var Q582;
            Q582=makeQuery(id+"F6.imprint","IMPRINT",FACE,{"disambiguationData":[TD([[makeQuery(id+"F6.imprint","IMPRINT",EDGE,{"derivedFrom":sQuery(id+"F6.wireOp",EDGE,"E504.MirrorC")}),-1.0]])]});
            var Q583;
            Q583=makeQuery(id+"F6.imprint","IMPRINT",FACE,{"disambiguationData":[TD([[makeQuery(id+"F6.imprint","IMPRINT",EDGE,{"derivedFrom":sQuery(id+"F6.wireOp",EDGE,"E451.MirrorC")}),-1.0]])]});
            var Q584;
            Q584=makeQuery(id+"F6.imprint","IMPRINT",FACE,{"disambiguationData":[TD([[makeQuery(id+"F6.imprint","IMPRINT",EDGE,{"derivedFrom":sQuery(id+"F6.wireOp",EDGE,"E43.32.0.19")}),1.0]])]});
            var Q585;
            Q585=makeQuery(id+"F6.imprint","IMPRINT",FACE,{"disambiguationData":[TD([[makeQuery(id+"F6.imprint","IMPRINT",EDGE,{"derivedFrom":sQuery(id+"F6.wireOp",EDGE,"E43.1.0.10")}),1.0]])]});
            var Q586;
            Q586=makeQuery(id+"F6.imprint","IMPRINT",FACE,{"disambiguationData":[TD([[makeQuery(id+"F6.imprint","IMPRINT",EDGE,{"derivedFrom":sQuery(id+"F6.wireOp",EDGE,"E42.0.4.0")}),1.0]])]});
            var Q587;
            Q587=makeQuery(id+"F6.imprint","IMPRINT",FACE,{"disambiguationData":[TD([[makeQuery(id+"F6.imprint","IMPRINT",EDGE,{"derivedFrom":sQuery(id+"F6.wireOp",EDGE,"E43.4.0.1")}),1.0]])]});
            var Q588;
            Q588=makeQuery(id+"F6.imprint","IMPRINT",FACE,{"disambiguationData":[TD([[makeQuery(id+"F6.imprint","IMPRINT",EDGE,{"derivedFrom":sQuery(id+"F6.wireOp",EDGE,"E43.3.0.10")}),1.0]])]});
            var Q589;
            Q589=makeQuery(id+"F6.imprint","IMPRINT",FACE,{"disambiguationData":[TD([[makeQuery(id+"F6.imprint","IMPRINT",EDGE,{"derivedFrom":sQuery(id+"F6.wireOp",EDGE,"E43.2.0.19")}),1.0]])]});
            var Q590;
            Q590=makeQuery(id+"F6.imprint","IMPRINT",FACE,{"disambiguationData":[TD([[makeQuery(id+"F6.imprint","IMPRINT",EDGE,{"derivedFrom":sQuery(id+"F6.wireOp",EDGE,"E43.2.0.1")}),1.0]])]});
            var Q591;
            Q591=makeQuery(id+"F6.imprint","IMPRINT",FACE,{"disambiguationData":[TD([[makeQuery(id+"F6.imprint","IMPRINT",EDGE,{"derivedFrom":sQuery(id+"F6.wireOp",EDGE,"E43.6.0.19")}),1.0]])]});
            var Q592;
            Q592=makeQuery(id+"F6.imprint","IMPRINT",FACE,{"disambiguationData":[TD([[makeQuery(id+"F6.imprint","IMPRINT",EDGE,{"derivedFrom":sQuery(id+"F6.wireOp",EDGE,"E43.6.0.1")}),1.0]])]});
            var Q593;
            Q593=makeQuery(id+"F6.imprint","IMPRINT",FACE,{"disambiguationData":[TD([[makeQuery(id+"F6.imprint","IMPRINT",EDGE,{"derivedFrom":sQuery(id+"F6.wireOp",EDGE,"E43.5.0.10")}),1.0]])]});
            var Q594;
            Q594=makeQuery(id+"F6.imprint","IMPRINT",FACE,{"disambiguationData":[TD([[makeQuery(id+"F6.imprint","IMPRINT",EDGE,{"derivedFrom":sQuery(id+"F6.wireOp",EDGE,"E43.4.0.19")}),1.0]])]});
            var Q595;
            Q595=makeQuery(id+"F6.imprint","IMPRINT",FACE,{"disambiguationData":[TD([[makeQuery(id+"F6.imprint","IMPRINT",EDGE,{"derivedFrom":sQuery(id+"F6.wireOp",EDGE,"E43.9.0.10")}),1.0]])]});
            var Q596;
            Q596=makeQuery(id+"F6.imprint","IMPRINT",FACE,{"disambiguationData":[TD([[makeQuery(id+"F6.imprint","IMPRINT",EDGE,{"derivedFrom":sQuery(id+"F6.wireOp",EDGE,"E43.8.0.19")}),1.0]])]});
            var Q597;
            Q597=makeQuery(id+"F6.imprint","IMPRINT",FACE,{"disambiguationData":[TD([[makeQuery(id+"F6.imprint","IMPRINT",EDGE,{"derivedFrom":sQuery(id+"F6.wireOp",EDGE,"E43.8.0.1")}),1.0]])]});
            var Q598;
            Q598=makeQuery(id+"F6.imprint","IMPRINT",FACE,{"disambiguationData":[TD([[makeQuery(id+"F6.imprint","IMPRINT",EDGE,{"derivedFrom":sQuery(id+"F6.wireOp",EDGE,"E43.7.0.10")}),1.0]])]});
            var Q599;
            Q599=makeQuery(id+"F6.imprint","IMPRINT",FACE,{"disambiguationData":[TD([[makeQuery(id+"F6.imprint","IMPRINT",EDGE,{"derivedFrom":sQuery(id+"F6.wireOp",EDGE,"E43.12.0.1")}),1.0]])]});
            var Q600;
            Q600=makeQuery(id+"F6.imprint","IMPRINT",FACE,{"disambiguationData":[TD([[makeQuery(id+"F6.imprint","IMPRINT",EDGE,{"derivedFrom":sQuery(id+"F6.wireOp",EDGE,"E43.11.0.10")}),1.0]])]});
            var Q601;
            Q601=makeQuery(id+"F6.imprint","IMPRINT",FACE,{"disambiguationData":[TD([[makeQuery(id+"F6.imprint","IMPRINT",EDGE,{"derivedFrom":sQuery(id+"F6.wireOp",EDGE,"E43.10.0.19")}),1.0]])]});
            var Q602;
            Q602=makeQuery(id+"F6.imprint","IMPRINT",FACE,{"disambiguationData":[TD([[makeQuery(id+"F6.imprint","IMPRINT",EDGE,{"derivedFrom":sQuery(id+"F6.wireOp",EDGE,"E43.10.0.1")}),1.0]])]});
            var Q603;
            Q603=makeQuery(id+"F6.imprint","IMPRINT",FACE,{"disambiguationData":[TD([[makeQuery(id+"F6.imprint","IMPRINT",EDGE,{"derivedFrom":sQuery(id+"F6.wireOp",EDGE,"E43.14.0.19")}),1.0]])]});
            var Q604;
            Q604=makeQuery(id+"F6.imprint","IMPRINT",FACE,{"disambiguationData":[TD([[makeQuery(id+"F6.imprint","IMPRINT",EDGE,{"derivedFrom":sQuery(id+"F6.wireOp",EDGE,"E43.14.0.1")}),1.0]])]});
            var Q605;
            Q605=makeQuery(id+"F6.imprint","IMPRINT",FACE,{"disambiguationData":[TD([[makeQuery(id+"F6.imprint","IMPRINT",EDGE,{"derivedFrom":sQuery(id+"F6.wireOp",EDGE,"E43.13.0.10")}),1.0]])]});
            var Q606;
            Q606=makeQuery(id+"F6.imprint","IMPRINT",FACE,{"disambiguationData":[TD([[makeQuery(id+"F6.imprint","IMPRINT",EDGE,{"derivedFrom":sQuery(id+"F6.wireOp",EDGE,"E43.12.0.19")}),1.0]])]});
            var Q607;
            Q607=makeQuery(id+"F6.imprint","IMPRINT",FACE,{"disambiguationData":[TD([[makeQuery(id+"F6.imprint","IMPRINT",EDGE,{"derivedFrom":sQuery(id+"F6.wireOp",EDGE,"E43.16.0.19")}),1.0]])]});
            var Q608;
            Q608=makeQuery(id+"F6.imprint","IMPRINT",FACE,{"disambiguationData":[TD([[makeQuery(id+"F6.imprint","IMPRINT",EDGE,{"derivedFrom":sQuery(id+"F6.wireOp",EDGE,"E43.16.0.1")}),1.0]])]});
            var Q609;
            Q609=makeQuery(id+"F6.imprint","IMPRINT",FACE,{"disambiguationData":[TD([[makeQuery(id+"F6.imprint","IMPRINT",EDGE,{"derivedFrom":sQuery(id+"F6.wireOp",EDGE,"E467.MirrorC")}),-1.0]])]});
            var Q610;
            Q610=makeQuery(id+"F6.imprint","IMPRINT",FACE,{"disambiguationData":[TD([[makeQuery(id+"F6.imprint","IMPRINT",EDGE,{"derivedFrom":sQuery(id+"F6.wireOp",EDGE,"E43.15.0.10")}),1.0]])]});
            var Q611;
            Q611=makeQuery(id+"F6.imprint","IMPRINT",FACE,{"disambiguationData":[TD([[makeQuery(id+"F6.imprint","IMPRINT",EDGE,{"derivedFrom":sQuery(id+"F6.wireOp",EDGE,"E519.MirrorC")}),-1.0]])]});
            var Q612;
            Q612=makeQuery(id+"F6.imprint","IMPRINT",FACE,{"disambiguationData":[TD([[makeQuery(id+"F6.imprint","IMPRINT",EDGE,{"derivedFrom":sQuery(id+"F6.wireOp",EDGE,"E311.MirrorC")}),-1.0]])]});
            var Q613;
            Q613=makeQuery(id+"F6.imprint","IMPRINT",FACE,{"disambiguationData":[TD([[makeQuery(id+"F6.imprint","IMPRINT",EDGE,{"derivedFrom":sQuery(id+"F6.wireOp",EDGE,"E326.MirrorC")}),-1.0]])]});
            var Q614;
            Q614=makeQuery(id+"F6.imprint","IMPRINT",FACE,{"disambiguationData":[TD([[makeQuery(id+"F6.imprint","IMPRINT",EDGE,{"derivedFrom":sQuery(id+"F6.wireOp",EDGE,"E263.MirrorC")}),-1.0]])]});
            var Q615;
            Q615=makeQuery(id+"F6.imprint","IMPRINT",FACE,{"disambiguationData":[TD([[makeQuery(id+"F6.imprint","IMPRINT",EDGE,{"derivedFrom":sQuery(id+"F6.wireOp",EDGE,"E250.MirrorC")}),-1.0]])]});
            var Q616;
            Q616=makeQuery(id+"F6.imprint","IMPRINT",FACE,{"disambiguationData":[TD([[makeQuery(id+"F6.imprint","IMPRINT",EDGE,{"derivedFrom":sQuery(id+"F6.wireOp",EDGE,"E420.MirrorC")}),-1.0]])]});
            var Q617;
            Q617=makeQuery(id+"F6.imprint","IMPRINT",FACE,{"disambiguationData":[TD([[makeQuery(id+"F6.imprint","IMPRINT",EDGE,{"derivedFrom":sQuery(id+"F6.wireOp",EDGE,"E473.MirrorC")}),-1.0]])]});
            var Q618;
            Q618=makeQuery(id+"F6.imprint","IMPRINT",FACE,{"disambiguationData":[TD([[makeQuery(id+"F6.imprint","IMPRINT",EDGE,{"derivedFrom":sQuery(id+"F6.wireOp",EDGE,"E295.MirrorC")}),-1.0]])]});
            var Q619;
            Q619=makeQuery(id+"F6.imprint","IMPRINT",FACE,{"disambiguationData":[TD([[makeQuery(id+"F6.imprint","IMPRINT",EDGE,{"derivedFrom":sQuery(id+"F6.wireOp",EDGE,"E279.MirrorC")}),-1.0]])]});
            var Q620;
            Q620=makeQuery(id+"F6.imprint","IMPRINT",FACE,{"disambiguationData":[TD([[makeQuery(id+"F6.imprint","IMPRINT",EDGE,{"derivedFrom":sQuery(id+"F6.wireOp",EDGE,"E436.MirrorC")}),-1.0]])]});
            var Q621;
            Q621=makeQuery(id+"F6.imprint","IMPRINT",FACE,{"disambiguationData":[TD([[makeQuery(id+"F6.imprint","IMPRINT",EDGE,{"derivedFrom":sQuery(id+"F6.wireOp",EDGE,"E489.MirrorC")}),-1.0]])]});
            var Q622;
            Q622=makeQuery(id+"F6.imprint","IMPRINT",FACE,{"disambiguationData":[TD([[makeQuery(id+"F6.imprint","IMPRINT",EDGE,{"derivedFrom":sQuery(id+"F6.wireOp",EDGE,"E43.18.0.20")}),1.0]])]});
            var Q623;
            Q623=makeQuery(id+"F6.imprint","IMPRINT",FACE,{"disambiguationData":[TD([[makeQuery(id+"F6.imprint","IMPRINT",EDGE,{"derivedFrom":sQuery(id+"F6.wireOp",EDGE,"E43.18.0.2")}),1.0]])]});
            var Q624;
            Q624=makeQuery(id+"F6.imprint","IMPRINT",FACE,{"disambiguationData":[TD([[makeQuery(id+"F6.imprint","IMPRINT",EDGE,{"derivedFrom":sQuery(id+"F6.wireOp",EDGE,"E43.17.0.12")}),1.0]])]});
            var Q625;
            Q625=makeQuery(id+"F6.imprint","IMPRINT",FACE,{"disambiguationData":[TD([[makeQuery(id+"F6.imprint","IMPRINT",EDGE,{"derivedFrom":sQuery(id+"F6.wireOp",EDGE,"E43.21.0.12")}),1.0]])]});
            var Q626;
            Q626=makeQuery(id+"F6.imprint","IMPRINT",FACE,{"disambiguationData":[TD([[makeQuery(id+"F6.imprint","IMPRINT",EDGE,{"derivedFrom":sQuery(id+"F6.wireOp",EDGE,"E43.20.0.20")}),1.0]])]});
            var Q627;
            Q627=makeQuery(id+"F6.imprint","IMPRINT",FACE,{"disambiguationData":[TD([[makeQuery(id+"F6.imprint","IMPRINT",EDGE,{"derivedFrom":sQuery(id+"F6.wireOp",EDGE,"E43.20.0.2")}),1.0]])]});
            var Q628;
            Q628=makeQuery(id+"F6.imprint","IMPRINT",FACE,{"disambiguationData":[TD([[makeQuery(id+"F6.imprint","IMPRINT",EDGE,{"derivedFrom":sQuery(id+"F6.wireOp",EDGE,"E43.19.0.12")}),1.0]])]});
            var Q629;
            Q629=makeQuery(id+"F6.imprint","IMPRINT",FACE,{"disambiguationData":[TD([[makeQuery(id+"F6.imprint","IMPRINT",EDGE,{"derivedFrom":sQuery(id+"F6.wireOp",EDGE,"E43.24.0.2")}),1.0]])]});
            var Q630;
            Q630=makeQuery(id+"F6.imprint","IMPRINT",FACE,{"disambiguationData":[TD([[makeQuery(id+"F6.imprint","IMPRINT",EDGE,{"derivedFrom":sQuery(id+"F6.wireOp",EDGE,"E43.23.0.12")}),1.0]])]});
            var Q631;
            Q631=makeQuery(id+"F6.imprint","IMPRINT",FACE,{"disambiguationData":[TD([[makeQuery(id+"F6.imprint","IMPRINT",EDGE,{"derivedFrom":sQuery(id+"F6.wireOp",EDGE,"E43.22.0.20")}),1.0]])]});
            var Q632;
            Q632=makeQuery(id+"F6.imprint","IMPRINT",FACE,{"disambiguationData":[TD([[makeQuery(id+"F6.imprint","IMPRINT",EDGE,{"derivedFrom":sQuery(id+"F6.wireOp",EDGE,"E43.22.0.2")}),1.0]])]});
            var Q633;
            Q633=makeQuery(id+"F6.imprint","IMPRINT",FACE,{"disambiguationData":[TD([[makeQuery(id+"F6.imprint","IMPRINT",EDGE,{"derivedFrom":sQuery(id+"F6.wireOp",EDGE,"E43.26.0.20")}),1.0]])]});
            var Q634;
            Q634=makeQuery(id+"F6.imprint","IMPRINT",FACE,{"disambiguationData":[TD([[makeQuery(id+"F6.imprint","IMPRINT",EDGE,{"derivedFrom":sQuery(id+"F6.wireOp",EDGE,"E43.26.0.2")}),1.0]])]});
            var Q635;
            Q635=makeQuery(id+"F6.imprint","IMPRINT",FACE,{"disambiguationData":[TD([[makeQuery(id+"F6.imprint","IMPRINT",EDGE,{"derivedFrom":sQuery(id+"F6.wireOp",EDGE,"E43.25.0.12")}),1.0]])]});
            var Q636;
            Q636=makeQuery(id+"F6.imprint","IMPRINT",FACE,{"disambiguationData":[TD([[makeQuery(id+"F6.imprint","IMPRINT",EDGE,{"derivedFrom":sQuery(id+"F6.wireOp",EDGE,"E43.24.0.20")}),1.0]])]});
            var Q637;
            Q637=makeQuery(id+"F6.imprint","IMPRINT",FACE,{"disambiguationData":[TD([[makeQuery(id+"F6.imprint","IMPRINT",EDGE,{"derivedFrom":sQuery(id+"F6.wireOp",EDGE,"E565.MirrorC")}),-1.0]])]});
            var Q638;
            Q638=makeQuery(id+"F6.imprint","IMPRINT",FACE,{"disambiguationData":[TD([[makeQuery(id+"F6.imprint","IMPRINT",EDGE,{"derivedFrom":sQuery(id+"F6.wireOp",EDGE,"E43.29.0.12")}),1.0]])]});
            var Q639;
            Q639=makeQuery(id+"F6.imprint","IMPRINT",FACE,{"disambiguationData":[TD([[makeQuery(id+"F6.imprint","IMPRINT",EDGE,{"derivedFrom":sQuery(id+"F6.wireOp",EDGE,"E43.28.0.20")}),1.0]])]});
            var Q640;
            Q640=makeQuery(id+"F6.imprint","IMPRINT",FACE,{"disambiguationData":[TD([[makeQuery(id+"F6.imprint","IMPRINT",EDGE,{"derivedFrom":sQuery(id+"F6.wireOp",EDGE,"E43.28.0.2")}),1.0]])]});
            var Q641;
            Q641=makeQuery(id+"F6.imprint","IMPRINT",FACE,{"disambiguationData":[TD([[makeQuery(id+"F6.imprint","IMPRINT",EDGE,{"derivedFrom":sQuery(id+"F6.wireOp",EDGE,"E512.MirrorC")}),-1.0]])]});
            var Q642;
            Q642=makeQuery(id+"F6.imprint","IMPRINT",FACE,{"disambiguationData":[TD([[makeQuery(id+"F6.imprint","IMPRINT",EDGE,{"derivedFrom":sQuery(id+"F6.wireOp",EDGE,"E43.27.0.12")}),1.0]])]});
            var Q643;
            Q643=makeQuery(id+"F6.imprint","IMPRINT",FACE,{"disambiguationData":[TD([[makeQuery(id+"F6.imprint","IMPRINT",EDGE,{"derivedFrom":sQuery(id+"F6.wireOp",EDGE,"E43.32.0.2")}),1.0]])]});
            var Q644;
            Q644=makeQuery(id+"F6.imprint","IMPRINT",FACE,{"disambiguationData":[TD([[makeQuery(id+"F6.imprint","IMPRINT",EDGE,{"derivedFrom":sQuery(id+"F6.wireOp",EDGE,"E43.31.0.12")}),1.0]])]});
            var Q645;
            Q645=makeQuery(id+"F6.imprint","IMPRINT",FACE,{"disambiguationData":[TD([[makeQuery(id+"F6.imprint","IMPRINT",EDGE,{"derivedFrom":sQuery(id+"F6.wireOp",EDGE,"E43.30.0.20")}),1.0]])]});
            var Q646;
            Q646=makeQuery(id+"F6.imprint","IMPRINT",FACE,{"disambiguationData":[TD([[makeQuery(id+"F6.imprint","IMPRINT",EDGE,{"derivedFrom":sQuery(id+"F6.wireOp",EDGE,"E43.30.0.2")}),1.0]])]});
            var Q647;
            Q647=makeQuery(id+"F6.imprint","IMPRINT",FACE,{"disambiguationData":[TD([[makeQuery(id+"F6.imprint","IMPRINT",EDGE,{"derivedFrom":sQuery(id+"F6.wireOp",EDGE,"E43.32.0.20")}),1.0]])]});
            var Q648;
            Q648=makeQuery(id+"F6.imprint","IMPRINT",FACE,{"disambiguationData":[TD([[makeQuery(id+"F6.imprint","IMPRINT",EDGE,{"derivedFrom":sQuery(id+"F6.wireOp",EDGE,"E43.1.0.12")}),1.0]])]});
            var Q649;
            Q649=makeQuery(id+"F6.imprint","IMPRINT",FACE,{"disambiguationData":[TD([[makeQuery(id+"F6.imprint","IMPRINT",EDGE,{"derivedFrom":sQuery(id+"F6.wireOp",EDGE,"E42.0.5.0")}),1.0]])]});
            var Q650;
            Q650=makeQuery(id+"F6.imprint","IMPRINT",FACE,{"disambiguationData":[TD([[makeQuery(id+"F6.imprint","IMPRINT",EDGE,{"derivedFrom":sQuery(id+"F6.wireOp",EDGE,"E43.4.0.2")}),1.0]])]});
            var Q651;
            Q651=makeQuery(id+"F6.imprint","IMPRINT",FACE,{"disambiguationData":[TD([[makeQuery(id+"F6.imprint","IMPRINT",EDGE,{"derivedFrom":sQuery(id+"F6.wireOp",EDGE,"E43.3.0.12")}),1.0]])]});
            var Q652;
            Q652=makeQuery(id+"F6.imprint","IMPRINT",FACE,{"disambiguationData":[TD([[makeQuery(id+"F6.imprint","IMPRINT",EDGE,{"derivedFrom":sQuery(id+"F6.wireOp",EDGE,"E43.2.0.20")}),1.0]])]});
            var Q653;
            Q653=makeQuery(id+"F6.imprint","IMPRINT",FACE,{"disambiguationData":[TD([[makeQuery(id+"F6.imprint","IMPRINT",EDGE,{"derivedFrom":sQuery(id+"F6.wireOp",EDGE,"E43.2.0.2")}),1.0]])]});
            var Q654;
            Q654=makeQuery(id+"F6.imprint","IMPRINT",FACE,{"disambiguationData":[TD([[makeQuery(id+"F6.imprint","IMPRINT",EDGE,{"derivedFrom":sQuery(id+"F6.wireOp",EDGE,"E43.6.0.20")}),1.0]])]});
            var Q655;
            Q655=makeQuery(id+"F6.imprint","IMPRINT",FACE,{"disambiguationData":[TD([[makeQuery(id+"F6.imprint","IMPRINT",EDGE,{"derivedFrom":sQuery(id+"F6.wireOp",EDGE,"E43.6.0.2")}),1.0]])]});
            var Q656;
            Q656=makeQuery(id+"F6.imprint","IMPRINT",FACE,{"disambiguationData":[TD([[makeQuery(id+"F6.imprint","IMPRINT",EDGE,{"derivedFrom":sQuery(id+"F6.wireOp",EDGE,"E43.5.0.12")}),1.0]])]});
            var Q657;
            Q657=makeQuery(id+"F6.imprint","IMPRINT",FACE,{"disambiguationData":[TD([[makeQuery(id+"F6.imprint","IMPRINT",EDGE,{"derivedFrom":sQuery(id+"F6.wireOp",EDGE,"E43.4.0.20")}),1.0]])]});
            var Q658;
            Q658=makeQuery(id+"F6.imprint","IMPRINT",FACE,{"disambiguationData":[TD([[makeQuery(id+"F6.imprint","IMPRINT",EDGE,{"derivedFrom":sQuery(id+"F6.wireOp",EDGE,"E43.9.0.12")}),1.0]])]});
            var Q659;
            Q659=makeQuery(id+"F6.imprint","IMPRINT",FACE,{"disambiguationData":[TD([[makeQuery(id+"F6.imprint","IMPRINT",EDGE,{"derivedFrom":sQuery(id+"F6.wireOp",EDGE,"E43.8.0.20")}),1.0]])]});
            var Q660;
            Q660=makeQuery(id+"F6.imprint","IMPRINT",FACE,{"disambiguationData":[TD([[makeQuery(id+"F6.imprint","IMPRINT",EDGE,{"derivedFrom":sQuery(id+"F6.wireOp",EDGE,"E43.8.0.2")}),1.0]])]});
            var Q661;
            Q661=makeQuery(id+"F6.imprint","IMPRINT",FACE,{"disambiguationData":[TD([[makeQuery(id+"F6.imprint","IMPRINT",EDGE,{"derivedFrom":sQuery(id+"F6.wireOp",EDGE,"E43.7.0.12")}),1.0]])]});
            var Q662;
            Q662=makeQuery(id+"F6.imprint","IMPRINT",FACE,{"disambiguationData":[TD([[makeQuery(id+"F6.imprint","IMPRINT",EDGE,{"derivedFrom":sQuery(id+"F6.wireOp",EDGE,"E43.12.0.2")}),1.0]])]});
            var Q663;
            Q663=makeQuery(id+"F6.imprint","IMPRINT",FACE,{"disambiguationData":[TD([[makeQuery(id+"F6.imprint","IMPRINT",EDGE,{"derivedFrom":sQuery(id+"F6.wireOp",EDGE,"E43.11.0.12")}),1.0]])]});
            var Q664;
            Q664=makeQuery(id+"F6.imprint","IMPRINT",FACE,{"disambiguationData":[TD([[makeQuery(id+"F6.imprint","IMPRINT",EDGE,{"derivedFrom":sQuery(id+"F6.wireOp",EDGE,"E43.10.0.20")}),1.0]])]});
            var Q665;
            Q665=makeQuery(id+"F6.imprint","IMPRINT",FACE,{"disambiguationData":[TD([[makeQuery(id+"F6.imprint","IMPRINT",EDGE,{"derivedFrom":sQuery(id+"F6.wireOp",EDGE,"E528.MirrorC")}),-1.0]])]});
            var Q666;
            Q666=makeQuery(id+"F6.imprint","IMPRINT",FACE,{"disambiguationData":[TD([[makeQuery(id+"F6.imprint","IMPRINT",EDGE,{"derivedFrom":sQuery(id+"F6.wireOp",EDGE,"E581.MirrorC")}),-1.0]])]});
            var Q667;
            Q667=makeQuery(id+"F6.imprint","IMPRINT",FACE,{"disambiguationData":[TD([[makeQuery(id+"F6.imprint","IMPRINT",EDGE,{"derivedFrom":sQuery(id+"F6.wireOp",EDGE,"E43.10.0.2")}),1.0]])]});
            var Q668;
            Q668=makeQuery(id+"F6.imprint","IMPRINT",FACE,{"disambiguationData":[TD([[makeQuery(id+"F6.imprint","IMPRINT",EDGE,{"derivedFrom":sQuery(id+"F6.wireOp",EDGE,"E43.14.0.20")}),1.0]])]});
            var Q669;
            Q669=makeQuery(id+"F6.imprint","IMPRINT",FACE,{"disambiguationData":[TD([[makeQuery(id+"F6.imprint","IMPRINT",EDGE,{"derivedFrom":sQuery(id+"F6.wireOp",EDGE,"E43.14.0.2")}),1.0]])]});
            var Q670;
            Q670=makeQuery(id+"F6.imprint","IMPRINT",FACE,{"disambiguationData":[TD([[makeQuery(id+"F6.imprint","IMPRINT",EDGE,{"derivedFrom":sQuery(id+"F6.wireOp",EDGE,"E43.13.0.12")}),1.0]])]});
            var Q671;
            Q671=makeQuery(id+"F6.imprint","IMPRINT",FACE,{"disambiguationData":[TD([[makeQuery(id+"F6.imprint","IMPRINT",EDGE,{"derivedFrom":sQuery(id+"F6.wireOp",EDGE,"E43.12.0.20")}),1.0]])]});
            var Q672;
            Q672=makeQuery(id+"F6.imprint","IMPRINT",FACE,{"disambiguationData":[TD([[makeQuery(id+"F6.imprint","IMPRINT",EDGE,{"derivedFrom":sQuery(id+"F6.wireOp",EDGE,"E43.16.0.20")}),1.0]])]});
            var Q673;
            Q673=makeQuery(id+"F6.imprint","IMPRINT",FACE,{"disambiguationData":[TD([[makeQuery(id+"F6.imprint","IMPRINT",EDGE,{"derivedFrom":sQuery(id+"F6.wireOp",EDGE,"E43.16.0.2")}),1.0]])]});
            var Q674;
            Q674=makeQuery(id+"F6.imprint","IMPRINT",FACE,{"disambiguationData":[TD([[makeQuery(id+"F6.imprint","IMPRINT",EDGE,{"derivedFrom":sQuery(id+"F6.wireOp",EDGE,"E43.15.0.12")}),1.0]])]});
            var Q675;
            Q675=makeQuery(id+"F6.imprint","IMPRINT",FACE,{"disambiguationData":[TD([[makeQuery(id+"F6.imprint","IMPRINT",EDGE,{"derivedFrom":sQuery(id+"F6.wireOp",EDGE,"E312.MirrorC")}),-1.0]])]});
            var Q676;
            Q676=makeQuery(id+"F6.imprint","IMPRINT",FACE,{"disambiguationData":[TD([[makeQuery(id+"F6.imprint","IMPRINT",EDGE,{"derivedFrom":sQuery(id+"F6.wireOp",EDGE,"E327.MirrorC")}),-1.0]])]});
            var Q677;
            Q677=makeQuery(id+"F6.imprint","IMPRINT",FACE,{"disambiguationData":[TD([[makeQuery(id+"F6.imprint","IMPRINT",EDGE,{"derivedFrom":sQuery(id+"F6.wireOp",EDGE,"E264.MirrorC")}),-1.0]])]});
            var Q678;
            Q678=makeQuery(id+"F6.imprint","IMPRINT",FACE,{"disambiguationData":[TD([[makeQuery(id+"F6.imprint","IMPRINT",EDGE,{"derivedFrom":sQuery(id+"F6.wireOp",EDGE,"E251.MirrorC")}),-1.0]])]});
            var Q679;
            Q679=makeQuery(id+"F6.imprint","IMPRINT",FACE,{"disambiguationData":[TD([[makeQuery(id+"F6.imprint","IMPRINT",EDGE,{"derivedFrom":sQuery(id+"F6.wireOp",EDGE,"E296.MirrorC")}),-1.0]])]});
            var Q680;
            Q680=makeQuery(id+"F6.imprint","IMPRINT",FACE,{"disambiguationData":[TD([[makeQuery(id+"F6.imprint","IMPRINT",EDGE,{"derivedFrom":sQuery(id+"F6.wireOp",EDGE,"E280.MirrorC")}),-1.0]])]});
            var Q681;
            Q681=makeQuery(id+"F6.imprint","IMPRINT",FACE,{"disambiguationData":[TD([[makeQuery(id+"F6.imprint","IMPRINT",EDGE,{"derivedFrom":sQuery(id+"F6.wireOp",EDGE,"E43.1.0.13")}),1.0]])]});
            var Q682;
            Q682=makeQuery(id+"F6.imprint","IMPRINT",FACE,{"disambiguationData":[TD([[makeQuery(id+"F6.imprint","IMPRINT",EDGE,{"derivedFrom":sQuery(id+"F6.wireOp",EDGE,"E482.MirrorC")}),-1.0]])]});
            var Q683;
            Q683=makeQuery(id+"F6.imprint","IMPRINT",FACE,{"disambiguationData":[TD([[makeQuery(id+"F6.imprint","IMPRINT",EDGE,{"derivedFrom":sQuery(id+"F6.wireOp",EDGE,"E42.0.6.0")}),1.0]])]});
            var Q684;
            Q684=makeQuery(id+"F6.imprint","IMPRINT",FACE,{"disambiguationData":[TD([[makeQuery(id+"F6.imprint","IMPRINT",EDGE,{"derivedFrom":sQuery(id+"F6.wireOp",EDGE,"E535.MirrorC")}),-1.0]])]});
            var Q685;
            Q685=makeQuery(id+"F6.imprint","IMPRINT",FACE,{"disambiguationData":[TD([[makeQuery(id+"F6.imprint","IMPRINT",EDGE,{"derivedFrom":sQuery(id+"F6.wireOp",EDGE,"E550.MirrorC")}),-1.0]])]});
            var Q686;
            Q686=makeQuery(id+"F6.imprint","IMPRINT",FACE,{"disambiguationData":[TD([[makeQuery(id+"F6.imprint","IMPRINT",EDGE,{"derivedFrom":sQuery(id+"F6.wireOp",EDGE,"E43.21.0.13")}),1.0]])]});
            var Q687;
            Q687=makeQuery(id+"F6.imprint","IMPRINT",FACE,{"disambiguationData":[TD([[makeQuery(id+"F6.imprint","IMPRINT",EDGE,{"derivedFrom":sQuery(id+"F6.wireOp",EDGE,"E43.20.0.21")}),1.0]])]});
            var Q688;
            Q688=makeQuery(id+"F6.imprint","IMPRINT",FACE,{"disambiguationData":[TD([[makeQuery(id+"F6.imprint","IMPRINT",EDGE,{"derivedFrom":sQuery(id+"F6.wireOp",EDGE,"E43.20.0.4")}),1.0]])]});
            var Q689;
            Q689=makeQuery(id+"F6.imprint","IMPRINT",FACE,{"disambiguationData":[TD([[makeQuery(id+"F6.imprint","IMPRINT",EDGE,{"derivedFrom":sQuery(id+"F6.wireOp",EDGE,"E43.19.0.13")}),1.0]])]});
            var Q690;
            Q690=makeQuery(id+"F6.imprint","IMPRINT",FACE,{"disambiguationData":[TD([[makeQuery(id+"F6.imprint","IMPRINT",EDGE,{"derivedFrom":sQuery(id+"F6.wireOp",EDGE,"E43.24.0.4")}),1.0]])]});
            var Q691;
            Q691=makeQuery(id+"F6.imprint","IMPRINT",FACE,{"disambiguationData":[TD([[makeQuery(id+"F6.imprint","IMPRINT",EDGE,{"derivedFrom":sQuery(id+"F6.wireOp",EDGE,"E43.23.0.13")}),1.0]])]});
            var Q692;
            Q692=makeQuery(id+"F6.imprint","IMPRINT",FACE,{"disambiguationData":[TD([[makeQuery(id+"F6.imprint","IMPRINT",EDGE,{"derivedFrom":sQuery(id+"F6.wireOp",EDGE,"E43.22.0.21")}),1.0]])]});
            var Q693;
            Q693=makeQuery(id+"F6.imprint","IMPRINT",FACE,{"disambiguationData":[TD([[makeQuery(id+"F6.imprint","IMPRINT",EDGE,{"derivedFrom":sQuery(id+"F6.wireOp",EDGE,"E43.22.0.4")}),1.0]])]});
            var Q694;
            Q694=makeQuery(id+"F6.imprint","IMPRINT",FACE,{"disambiguationData":[TD([[makeQuery(id+"F6.imprint","IMPRINT",EDGE,{"derivedFrom":sQuery(id+"F6.wireOp",EDGE,"E43.26.0.21")}),1.0]])]});
            var Q695;
            Q695=makeQuery(id+"F6.imprint","IMPRINT",FACE,{"disambiguationData":[TD([[makeQuery(id+"F6.imprint","IMPRINT",EDGE,{"derivedFrom":sQuery(id+"F6.wireOp",EDGE,"E43.26.0.4")}),1.0]])]});
            var Q696;
            Q696=makeQuery(id+"F6.imprint","IMPRINT",FACE,{"disambiguationData":[TD([[makeQuery(id+"F6.imprint","IMPRINT",EDGE,{"derivedFrom":sQuery(id+"F6.wireOp",EDGE,"E43.25.0.13")}),1.0]])]});
            var Q697;
            Q697=makeQuery(id+"F6.imprint","IMPRINT",FACE,{"disambiguationData":[TD([[makeQuery(id+"F6.imprint","IMPRINT",EDGE,{"derivedFrom":sQuery(id+"F6.wireOp",EDGE,"E43.24.0.21")}),1.0]])]});
            var Q698;
            Q698=makeQuery(id+"F6.imprint","IMPRINT",FACE,{"disambiguationData":[TD([[makeQuery(id+"F6.imprint","IMPRINT",EDGE,{"derivedFrom":sQuery(id+"F6.wireOp",EDGE,"E43.29.0.13")}),1.0]])]});
            var Q699;
            Q699=makeQuery(id+"F6.imprint","IMPRINT",FACE,{"disambiguationData":[TD([[makeQuery(id+"F6.imprint","IMPRINT",EDGE,{"derivedFrom":sQuery(id+"F6.wireOp",EDGE,"E43.28.0.21")}),1.0]])]});
            var Q700;
            Q700=makeQuery(id+"F6.imprint","IMPRINT",FACE,{"disambiguationData":[TD([[makeQuery(id+"F6.imprint","IMPRINT",EDGE,{"derivedFrom":sQuery(id+"F6.wireOp",EDGE,"E43.28.0.4")}),1.0]])]});
            var Q701;
            Q701=makeQuery(id+"F6.imprint","IMPRINT",FACE,{"disambiguationData":[TD([[makeQuery(id+"F6.imprint","IMPRINT",EDGE,{"derivedFrom":sQuery(id+"F6.wireOp",EDGE,"E43.27.0.13")}),1.0]])]});
            var Q702;
            Q702=makeQuery(id+"F6.imprint","IMPRINT",FACE,{"disambiguationData":[TD([[makeQuery(id+"F6.imprint","IMPRINT",EDGE,{"derivedFrom":sQuery(id+"F6.wireOp",EDGE,"E43.32.0.4")}),1.0]])]});
            var Q703;
            Q703=makeQuery(id+"F6.imprint","IMPRINT",FACE,{"disambiguationData":[TD([[makeQuery(id+"F6.imprint","IMPRINT",EDGE,{"derivedFrom":sQuery(id+"F6.wireOp",EDGE,"E43.31.0.13")}),1.0]])]});
            var Q704;
            Q704=makeQuery(id+"F6.imprint","IMPRINT",FACE,{"disambiguationData":[TD([[makeQuery(id+"F6.imprint","IMPRINT",EDGE,{"derivedFrom":sQuery(id+"F6.wireOp",EDGE,"E43.30.0.21")}),1.0]])]});
            var Q705;
            Q705=makeQuery(id+"F6.imprint","IMPRINT",FACE,{"disambiguationData":[TD([[makeQuery(id+"F6.imprint","IMPRINT",EDGE,{"derivedFrom":sQuery(id+"F6.wireOp",EDGE,"E43.30.0.4")}),1.0]])]});
            var Q706;
            Q706=makeQuery(id+"F6.imprint","IMPRINT",FACE,{"disambiguationData":[TD([[makeQuery(id+"F6.imprint","IMPRINT",EDGE,{"derivedFrom":sQuery(id+"F6.wireOp",EDGE,"E626.MirrorC")}),-1.0]])]});
            var Q707;
            Q707=makeQuery(id+"F6.imprint","IMPRINT",FACE,{"disambiguationData":[TD([[makeQuery(id+"F6.imprint","IMPRINT",EDGE,{"derivedFrom":sQuery(id+"F6.wireOp",EDGE,"E574.MirrorC")}),-1.0]])]});
            var Q708;
            Q708=makeQuery(id+"F6.imprint","IMPRINT",FACE,{"disambiguationData":[TD([[makeQuery(id+"F6.imprint","IMPRINT",EDGE,{"derivedFrom":sQuery(id+"F6.wireOp",EDGE,"E43.32.0.21")}),1.0]])]});
            var Q709;
            Q709=makeQuery(id+"F6.imprint","IMPRINT",FACE,{"disambiguationData":[TD([[makeQuery(id+"F6.imprint","IMPRINT",EDGE,{"derivedFrom":sQuery(id+"F6.wireOp",EDGE,"E380.MirrorC")}),-1.0]])]});
            var Q710;
            Q710=makeQuery(id+"F6.imprint","IMPRINT",FACE,{"disambiguationData":[TD([[makeQuery(id+"F6.imprint","IMPRINT",EDGE,{"derivedFrom":sQuery(id+"F6.wireOp",EDGE,"E43.4.0.4")}),1.0]])]});
            var Q711;
            Q711=makeQuery(id+"F6.imprint","IMPRINT",FACE,{"disambiguationData":[TD([[makeQuery(id+"F6.imprint","IMPRINT",EDGE,{"derivedFrom":sQuery(id+"F6.wireOp",EDGE,"E43.3.0.13")}),1.0]])]});
            var Q712;
            Q712=makeQuery(id+"F6.imprint","IMPRINT",FACE,{"disambiguationData":[TD([[makeQuery(id+"F6.imprint","IMPRINT",EDGE,{"derivedFrom":sQuery(id+"F6.wireOp",EDGE,"E43.2.0.21")}),1.0]])]});
            var Q713;
            Q713=makeQuery(id+"F6.imprint","IMPRINT",FACE,{"disambiguationData":[TD([[makeQuery(id+"F6.imprint","IMPRINT",EDGE,{"derivedFrom":sQuery(id+"F6.wireOp",EDGE,"E43.2.0.4")}),1.0]])]});
            var Q714;
            Q714=makeQuery(id+"F6.imprint","IMPRINT",FACE,{"disambiguationData":[TD([[makeQuery(id+"F6.imprint","IMPRINT",EDGE,{"derivedFrom":sQuery(id+"F6.wireOp",EDGE,"E43.6.0.21")}),1.0]])]});
            var Q715;
            Q715=makeQuery(id+"F6.imprint","IMPRINT",FACE,{"disambiguationData":[TD([[makeQuery(id+"F6.imprint","IMPRINT",EDGE,{"derivedFrom":sQuery(id+"F6.wireOp",EDGE,"E43.6.0.4")}),1.0]])]});
            var Q716;
            Q716=makeQuery(id+"F6.imprint","IMPRINT",FACE,{"disambiguationData":[TD([[makeQuery(id+"F6.imprint","IMPRINT",EDGE,{"derivedFrom":sQuery(id+"F6.wireOp",EDGE,"E43.5.0.13")}),1.0]])]});
            var Q717;
            Q717=makeQuery(id+"F6.imprint","IMPRINT",FACE,{"disambiguationData":[TD([[makeQuery(id+"F6.imprint","IMPRINT",EDGE,{"derivedFrom":sQuery(id+"F6.wireOp",EDGE,"E43.4.0.21")}),1.0]])]});
            var Q718;
            Q718=makeQuery(id+"F6.imprint","IMPRINT",FACE,{"disambiguationData":[TD([[makeQuery(id+"F6.imprint","IMPRINT",EDGE,{"derivedFrom":sQuery(id+"F6.wireOp",EDGE,"E43.9.0.13")}),1.0]])]});
            var Q719;
            Q719=makeQuery(id+"F6.imprint","IMPRINT",FACE,{"disambiguationData":[TD([[makeQuery(id+"F6.imprint","IMPRINT",EDGE,{"derivedFrom":sQuery(id+"F6.wireOp",EDGE,"E43.8.0.21")}),1.0]])]});
            var Q720;
            Q720=makeQuery(id+"F6.imprint","IMPRINT",FACE,{"disambiguationData":[TD([[makeQuery(id+"F6.imprint","IMPRINT",EDGE,{"derivedFrom":sQuery(id+"F6.wireOp",EDGE,"E43.8.0.4")}),1.0]])]});
            var Q721;
            Q721=makeQuery(id+"F6.imprint","IMPRINT",FACE,{"disambiguationData":[TD([[makeQuery(id+"F6.imprint","IMPRINT",EDGE,{"derivedFrom":sQuery(id+"F6.wireOp",EDGE,"E43.7.0.13")}),1.0]])]});
            var Q722;
            Q722=makeQuery(id+"F6.imprint","IMPRINT",FACE,{"disambiguationData":[TD([[makeQuery(id+"F6.imprint","IMPRINT",EDGE,{"derivedFrom":sQuery(id+"F6.wireOp",EDGE,"E43.12.0.4")}),1.0]])]});
            var Q723;
            Q723=makeQuery(id+"F6.imprint","IMPRINT",FACE,{"disambiguationData":[TD([[makeQuery(id+"F6.imprint","IMPRINT",EDGE,{"derivedFrom":sQuery(id+"F6.wireOp",EDGE,"E43.11.0.13")}),1.0]])]});
            var Q724;
            Q724=makeQuery(id+"F6.imprint","IMPRINT",FACE,{"disambiguationData":[TD([[makeQuery(id+"F6.imprint","IMPRINT",EDGE,{"derivedFrom":sQuery(id+"F6.wireOp",EDGE,"E43.10.0.21")}),1.0]])]});
            var Q725;
            Q725=makeQuery(id+"F6.imprint","IMPRINT",FACE,{"disambiguationData":[TD([[makeQuery(id+"F6.imprint","IMPRINT",EDGE,{"derivedFrom":sQuery(id+"F6.wireOp",EDGE,"E43.10.0.4")}),1.0]])]});
            var Q726;
            Q726=makeQuery(id+"F6.imprint","IMPRINT",FACE,{"disambiguationData":[TD([[makeQuery(id+"F6.imprint","IMPRINT",EDGE,{"derivedFrom":sQuery(id+"F6.wireOp",EDGE,"E43.14.0.21")}),1.0]])]});
            var Q727;
            Q727=makeQuery(id+"F6.imprint","IMPRINT",FACE,{"disambiguationData":[TD([[makeQuery(id+"F6.imprint","IMPRINT",EDGE,{"derivedFrom":sQuery(id+"F6.wireOp",EDGE,"E43.14.0.4")}),1.0]])]});
            var Q728;
            Q728=makeQuery(id+"F6.imprint","IMPRINT",FACE,{"disambiguationData":[TD([[makeQuery(id+"F6.imprint","IMPRINT",EDGE,{"derivedFrom":sQuery(id+"F6.wireOp",EDGE,"E43.13.0.13")}),1.0]])]});
            var Q729;
            Q729=makeQuery(id+"F6.imprint","IMPRINT",FACE,{"disambiguationData":[TD([[makeQuery(id+"F6.imprint","IMPRINT",EDGE,{"derivedFrom":sQuery(id+"F6.wireOp",EDGE,"E43.12.0.21")}),1.0]])]});
            var Q730;
            Q730=makeQuery(id+"F6.imprint","IMPRINT",FACE,{"disambiguationData":[TD([[makeQuery(id+"F6.imprint","IMPRINT",EDGE,{"derivedFrom":sQuery(id+"F6.wireOp",EDGE,"E43.16.0.21")}),1.0]])]});
            var Q731;
            Q731=makeQuery(id+"F6.imprint","IMPRINT",FACE,{"disambiguationData":[TD([[makeQuery(id+"F6.imprint","IMPRINT",EDGE,{"derivedFrom":sQuery(id+"F6.wireOp",EDGE,"E43.16.0.4")}),1.0]])]});
            var Q732;
            Q732=makeQuery(id+"F6.imprint","IMPRINT",FACE,{"disambiguationData":[TD([[makeQuery(id+"F6.imprint","IMPRINT",EDGE,{"derivedFrom":sQuery(id+"F6.wireOp",EDGE,"E641.MirrorC")}),-1.0]])]});
            var Q733;
            Q733=makeQuery(id+"F6.imprint","IMPRINT",FACE,{"disambiguationData":[TD([[makeQuery(id+"F6.imprint","IMPRINT",EDGE,{"derivedFrom":sQuery(id+"F6.wireOp",EDGE,"E43.15.0.13")}),1.0]])]});
            var Q734;
            Q734=makeQuery(id+"F6.imprint","IMPRINT",FACE,{"disambiguationData":[TD([[makeQuery(id+"F6.imprint","IMPRINT",EDGE,{"derivedFrom":sQuery(id+"F6.wireOp",EDGE,"E590.MirrorC")}),-1.0]])]});
            var Q735;
            Q735=makeQuery(id+"F6.imprint","IMPRINT",FACE,{"disambiguationData":[TD([[makeQuery(id+"F6.imprint","IMPRINT",EDGE,{"derivedFrom":sQuery(id+"F6.wireOp",EDGE,"E43.18.0.21")}),1.0]])]});
            var Q736;
            Q736=makeQuery(id+"F6.imprint","IMPRINT",FACE,{"disambiguationData":[TD([[makeQuery(id+"F6.imprint","IMPRINT",EDGE,{"derivedFrom":sQuery(id+"F6.wireOp",EDGE,"E396.MirrorC")}),-1.0]])]});
            var Q737;
            Q737=makeQuery(id+"F6.imprint","IMPRINT",FACE,{"disambiguationData":[TD([[makeQuery(id+"F6.imprint","IMPRINT",EDGE,{"derivedFrom":sQuery(id+"F6.wireOp",EDGE,"E43.18.0.4")}),1.0]])]});
            var Q738;
            Q738=makeQuery(id+"F6.imprint","IMPRINT",FACE,{"disambiguationData":[TD([[makeQuery(id+"F6.imprint","IMPRINT",EDGE,{"derivedFrom":sQuery(id+"F6.wireOp",EDGE,"E43.17.0.13")}),1.0]])]});
            var Q739;
            Q739=makeQuery(id+"F6.imprint","IMPRINT",FACE,{"disambiguationData":[TD([[makeQuery(id+"F6.imprint","IMPRINT",EDGE,{"derivedFrom":sQuery(id+"F6.wireOp",EDGE,"E343.MirrorC")}),-1.0]])]});
            var Q740;
            Q740=makeQuery(id+"F6.imprint","IMPRINT",FACE,{"disambiguationData":[TD([[makeQuery(id+"F6.imprint","IMPRINT",EDGE,{"derivedFrom":sQuery(id+"F6.wireOp",EDGE,"E313.MirrorC")}),-1.0]])]});
            var Q741;
            Q741=makeQuery(id+"F6.imprint","IMPRINT",FACE,{"disambiguationData":[TD([[makeQuery(id+"F6.imprint","IMPRINT",EDGE,{"derivedFrom":sQuery(id+"F6.wireOp",EDGE,"E328.MirrorC")}),-1.0]])]});
            var Q742;
            Q742=makeQuery(id+"F6.imprint","IMPRINT",FACE,{"disambiguationData":[TD([[makeQuery(id+"F6.imprint","IMPRINT",EDGE,{"derivedFrom":sQuery(id+"F6.wireOp",EDGE,"E265.MirrorC")}),-1.0]])]});
            var Q743;
            Q743=makeQuery(id+"F6.imprint","IMPRINT",FACE,{"disambiguationData":[TD([[makeQuery(id+"F6.imprint","IMPRINT",EDGE,{"derivedFrom":sQuery(id+"F6.wireOp",EDGE,"E543.MirrorC")}),-1.0]])]});
            var Q744;
            Q744=makeQuery(id+"F6.imprint","IMPRINT",FACE,{"disambiguationData":[TD([[makeQuery(id+"F6.imprint","IMPRINT",EDGE,{"derivedFrom":sQuery(id+"F6.wireOp",EDGE,"E297.MirrorC")}),-1.0]])]});
            var Q745;
            Q745=makeQuery(id+"F6.imprint","IMPRINT",FACE,{"disambiguationData":[TD([[makeQuery(id+"F6.imprint","IMPRINT",EDGE,{"derivedFrom":sQuery(id+"F6.wireOp",EDGE,"E596.MirrorC")}),-1.0]])]});
            var Q746;
            Q746=makeQuery(id+"F6.imprint","IMPRINT",FACE,{"disambiguationData":[TD([[makeQuery(id+"F6.imprint","IMPRINT",EDGE,{"derivedFrom":sQuery(id+"F6.wireOp",EDGE,"E281.MirrorC")}),-1.0]])]});
            var Q747;
            Q747=makeQuery(id+"F6.imprint","IMPRINT",FACE,{"disambiguationData":[TD([[makeQuery(id+"F6.imprint","IMPRINT",EDGE,{"derivedFrom":sQuery(id+"F6.wireOp",EDGE,"E43.1.0.14")}),1.0]])]});
            var Q748;
            Q748=makeQuery(id+"F6.imprint","IMPRINT",FACE,{"disambiguationData":[TD([[makeQuery(id+"F6.imprint","IMPRINT",EDGE,{"derivedFrom":sQuery(id+"F6.wireOp",EDGE,"E350.MirrorC")}),-1.0]])]});
            var Q749;
            Q749=makeQuery(id+"F6.imprint","IMPRINT",FACE,{"disambiguationData":[TD([[makeQuery(id+"F6.imprint","IMPRINT",EDGE,{"derivedFrom":sQuery(id+"F6.wireOp",EDGE,"E42.0.7.0")}),1.0]])]});
            var Q750;
            Q750=makeQuery(id+"F6.imprint","IMPRINT",FACE,{"disambiguationData":[TD([[makeQuery(id+"F6.imprint","IMPRINT",EDGE,{"derivedFrom":sQuery(id+"F6.wireOp",EDGE,"E43.4.0.5")}),1.0]])]});
            var Q751;
            Q751=makeQuery(id+"F6.imprint","IMPRINT",FACE,{"disambiguationData":[TD([[makeQuery(id+"F6.imprint","IMPRINT",EDGE,{"derivedFrom":sQuery(id+"F6.wireOp",EDGE,"E43.3.0.14")}),1.0]])]});
            var Q752;
            Q752=makeQuery(id+"F6.imprint","IMPRINT",FACE,{"disambiguationData":[TD([[makeQuery(id+"F6.imprint","IMPRINT",EDGE,{"derivedFrom":sQuery(id+"F6.wireOp",EDGE,"E43.2.0.22")}),1.0]])]});
            var Q753;
            Q753=makeQuery(id+"F6.imprint","IMPRINT",FACE,{"disambiguationData":[TD([[makeQuery(id+"F6.imprint","IMPRINT",EDGE,{"derivedFrom":sQuery(id+"F6.wireOp",EDGE,"E43.2.0.5")}),1.0]])]});
            var Q754;
            Q754=makeQuery(id+"F6.imprint","IMPRINT",FACE,{"disambiguationData":[TD([[makeQuery(id+"F6.imprint","IMPRINT",EDGE,{"derivedFrom":sQuery(id+"F6.wireOp",EDGE,"E611.MirrorC")}),-1.0]])]});
            var Q755;
            Q755=makeQuery(id+"F6.imprint","IMPRINT",FACE,{"disambiguationData":[TD([[makeQuery(id+"F6.imprint","IMPRINT",EDGE,{"derivedFrom":sQuery(id+"F6.wireOp",EDGE,"E364.MirrorC")}),-1.0]])]});
            var Q756;
            Q756=makeQuery(id+"F6.imprint","IMPRINT",FACE,{"disambiguationData":[TD([[makeQuery(id+"F6.imprint","IMPRINT",EDGE,{"derivedFrom":sQuery(id+"F6.wireOp",EDGE,"E43.24.0.5")}),1.0]])]});
            var Q757;
            Q757=makeQuery(id+"F6.imprint","IMPRINT",FACE,{"disambiguationData":[TD([[makeQuery(id+"F6.imprint","IMPRINT",EDGE,{"derivedFrom":sQuery(id+"F6.wireOp",EDGE,"E43.23.0.14")}),1.0]])]});
            var Q758;
            Q758=makeQuery(id+"F6.imprint","IMPRINT",FACE,{"disambiguationData":[TD([[makeQuery(id+"F6.imprint","IMPRINT",EDGE,{"derivedFrom":sQuery(id+"F6.wireOp",EDGE,"E43.22.0.22")}),1.0]])]});
            var Q759;
            Q759=makeQuery(id+"F6.imprint","IMPRINT",FACE,{"disambiguationData":[TD([[makeQuery(id+"F6.imprint","IMPRINT",EDGE,{"derivedFrom":sQuery(id+"F6.wireOp",EDGE,"E43.22.0.5")}),1.0]])]});
            var Q760;
            Q760=makeQuery(id+"F6.imprint","IMPRINT",FACE,{"disambiguationData":[TD([[makeQuery(id+"F6.imprint","IMPRINT",EDGE,{"derivedFrom":sQuery(id+"F6.wireOp",EDGE,"E43.26.0.22")}),1.0]])]});
            var Q761;
            Q761=makeQuery(id+"F6.imprint","IMPRINT",FACE,{"disambiguationData":[TD([[makeQuery(id+"F6.imprint","IMPRINT",EDGE,{"derivedFrom":sQuery(id+"F6.wireOp",EDGE,"E43.26.0.5")}),1.0]])]});
            var Q762;
            Q762=makeQuery(id+"F6.imprint","IMPRINT",FACE,{"disambiguationData":[TD([[makeQuery(id+"F6.imprint","IMPRINT",EDGE,{"derivedFrom":sQuery(id+"F6.wireOp",EDGE,"E43.25.0.14")}),1.0]])]});
            var Q763;
            Q763=makeQuery(id+"F6.imprint","IMPRINT",FACE,{"disambiguationData":[TD([[makeQuery(id+"F6.imprint","IMPRINT",EDGE,{"derivedFrom":sQuery(id+"F6.wireOp",EDGE,"E43.24.0.22")}),1.0]])]});
            var Q764;
            Q764=makeQuery(id+"F6.imprint","IMPRINT",FACE,{"disambiguationData":[TD([[makeQuery(id+"F6.imprint","IMPRINT",EDGE,{"derivedFrom":sQuery(id+"F6.wireOp",EDGE,"E43.29.0.14")}),1.0]])]});
            var Q765;
            Q765=makeQuery(id+"F6.imprint","IMPRINT",FACE,{"disambiguationData":[TD([[makeQuery(id+"F6.imprint","IMPRINT",EDGE,{"derivedFrom":sQuery(id+"F6.wireOp",EDGE,"E43.28.0.22")}),1.0]])]});
            var Q766;
            Q766=makeQuery(id+"F6.imprint","IMPRINT",FACE,{"disambiguationData":[TD([[makeQuery(id+"F6.imprint","IMPRINT",EDGE,{"derivedFrom":sQuery(id+"F6.wireOp",EDGE,"E43.28.0.5")}),1.0]])]});
            var Q767;
            Q767=makeQuery(id+"F6.imprint","IMPRINT",FACE,{"disambiguationData":[TD([[makeQuery(id+"F6.imprint","IMPRINT",EDGE,{"derivedFrom":sQuery(id+"F6.wireOp",EDGE,"E702.MirrorC")}),-1.0]])]});
            var Q768;
            Q768=makeQuery(id+"F6.imprint","IMPRINT",FACE,{"disambiguationData":[TD([[makeQuery(id+"F6.imprint","IMPRINT",EDGE,{"derivedFrom":sQuery(id+"F6.wireOp",EDGE,"E649.MirrorC")}),-1.0]])]});
            var Q769;
            Q769=makeQuery(id+"F6.imprint","IMPRINT",FACE,{"disambiguationData":[TD([[makeQuery(id+"F6.imprint","IMPRINT",EDGE,{"derivedFrom":sQuery(id+"F6.wireOp",EDGE,"E43.27.0.14")}),1.0]])]});
            var Q770;
            Q770=makeQuery(id+"F6.imprint","IMPRINT",FACE,{"disambiguationData":[TD([[makeQuery(id+"F6.imprint","IMPRINT",EDGE,{"derivedFrom":sQuery(id+"F6.wireOp",EDGE,"E43.32.0.5")}),1.0]])]});
            var Q771;
            Q771=makeQuery(id+"F6.imprint","IMPRINT",FACE,{"disambiguationData":[TD([[makeQuery(id+"F6.imprint","IMPRINT",EDGE,{"derivedFrom":sQuery(id+"F6.wireOp",EDGE,"E43.31.0.14")}),1.0]])]});
            var Q772;
            Q772=makeQuery(id+"F6.imprint","IMPRINT",FACE,{"disambiguationData":[TD([[makeQuery(id+"F6.imprint","IMPRINT",EDGE,{"derivedFrom":sQuery(id+"F6.wireOp",EDGE,"E43.30.0.22")}),1.0]])]});
            var Q773;
            Q773=makeQuery(id+"F6.imprint","IMPRINT",FACE,{"disambiguationData":[TD([[makeQuery(id+"F6.imprint","IMPRINT",EDGE,{"derivedFrom":sQuery(id+"F6.wireOp",EDGE,"E43.30.0.5")}),1.0]])]});
            var Q774;
            Q774=makeQuery(id+"F6.imprint","IMPRINT",FACE,{"disambiguationData":[TD([[makeQuery(id+"F6.imprint","IMPRINT",EDGE,{"derivedFrom":sQuery(id+"F6.wireOp",EDGE,"E389.MirrorC")}),-1.0]])]});
            var Q775;
            Q775=makeQuery(id+"F6.imprint","IMPRINT",FACE,{"disambiguationData":[TD([[makeQuery(id+"F6.imprint","IMPRINT",EDGE,{"derivedFrom":sQuery(id+"F6.wireOp",EDGE,"E441.MirrorC")}),-1.0]])]});
            var Q776;
            Q776=makeQuery(id+"F6.imprint","IMPRINT",FACE,{"disambiguationData":[TD([[makeQuery(id+"F6.imprint","IMPRINT",EDGE,{"derivedFrom":sQuery(id+"F6.wireOp",EDGE,"E43.32.0.22")}),1.0]])]});
            var Q777;
            Q777=makeQuery(id+"F6.imprint","IMPRINT",FACE,{"disambiguationData":[TD([[makeQuery(id+"F6.imprint","IMPRINT",EDGE,{"derivedFrom":sQuery(id+"F6.wireOp",EDGE,"E43.6.0.22")}),1.0]])]});
            var Q778;
            Q778=makeQuery(id+"F6.imprint","IMPRINT",FACE,{"disambiguationData":[TD([[makeQuery(id+"F6.imprint","IMPRINT",EDGE,{"derivedFrom":sQuery(id+"F6.wireOp",EDGE,"E43.6.0.5")}),1.0]])]});
            var Q779;
            Q779=makeQuery(id+"F6.imprint","IMPRINT",FACE,{"disambiguationData":[TD([[makeQuery(id+"F6.imprint","IMPRINT",EDGE,{"derivedFrom":sQuery(id+"F6.wireOp",EDGE,"E43.5.0.14")}),1.0]])]});
            var Q780;
            Q780=makeQuery(id+"F6.imprint","IMPRINT",FACE,{"disambiguationData":[TD([[makeQuery(id+"F6.imprint","IMPRINT",EDGE,{"derivedFrom":sQuery(id+"F6.wireOp",EDGE,"E43.4.0.22")}),1.0]])]});
            var Q781;
            Q781=makeQuery(id+"F6.imprint","IMPRINT",FACE,{"disambiguationData":[TD([[makeQuery(id+"F6.imprint","IMPRINT",EDGE,{"derivedFrom":sQuery(id+"F6.wireOp",EDGE,"E43.9.0.14")}),1.0]])]});
            var Q782;
            Q782=makeQuery(id+"F6.imprint","IMPRINT",FACE,{"disambiguationData":[TD([[makeQuery(id+"F6.imprint","IMPRINT",EDGE,{"derivedFrom":sQuery(id+"F6.wireOp",EDGE,"E43.8.0.22")}),1.0]])]});
            var Q783;
            Q783=makeQuery(id+"F6.imprint","IMPRINT",FACE,{"disambiguationData":[TD([[makeQuery(id+"F6.imprint","IMPRINT",EDGE,{"derivedFrom":sQuery(id+"F6.wireOp",EDGE,"E43.8.0.5")}),1.0]])]});
            var Q784;
            Q784=makeQuery(id+"F6.imprint","IMPRINT",FACE,{"disambiguationData":[TD([[makeQuery(id+"F6.imprint","IMPRINT",EDGE,{"derivedFrom":sQuery(id+"F6.wireOp",EDGE,"E43.7.0.14")}),1.0]])]});
            var Q785;
            Q785=makeQuery(id+"F6.imprint","IMPRINT",FACE,{"disambiguationData":[TD([[makeQuery(id+"F6.imprint","IMPRINT",EDGE,{"derivedFrom":sQuery(id+"F6.wireOp",EDGE,"E664.MirrorC")}),-1.0]])]});
            var Q786;
            Q786=makeQuery(id+"F6.imprint","IMPRINT",FACE,{"disambiguationData":[TD([[makeQuery(id+"F6.imprint","IMPRINT",EDGE,{"derivedFrom":sQuery(id+"F6.wireOp",EDGE,"E43.12.0.5")}),1.0]])]});
            var Q787;
            Q787=makeQuery(id+"F6.imprint","IMPRINT",FACE,{"disambiguationData":[TD([[makeQuery(id+"F6.imprint","IMPRINT",EDGE,{"derivedFrom":sQuery(id+"F6.wireOp",EDGE,"E43.11.0.14")}),1.0]])]});
            var Q788;
            Q788=makeQuery(id+"F6.imprint","IMPRINT",FACE,{"disambiguationData":[TD([[makeQuery(id+"F6.imprint","IMPRINT",EDGE,{"derivedFrom":sQuery(id+"F6.wireOp",EDGE,"E717.MirrorC")}),-1.0]])]});
            var Q789;
            Q789=makeQuery(id+"F6.imprint","IMPRINT",FACE,{"disambiguationData":[TD([[makeQuery(id+"F6.imprint","IMPRINT",EDGE,{"derivedFrom":sQuery(id+"F6.wireOp",EDGE,"E43.10.0.22")}),1.0]])]});
            var Q790;
            Q790=makeQuery(id+"F6.imprint","IMPRINT",FACE,{"disambiguationData":[TD([[makeQuery(id+"F6.imprint","IMPRINT",EDGE,{"derivedFrom":sQuery(id+"F6.wireOp",EDGE,"E43.10.0.5")}),1.0]])]});
            var Q791;
            Q791=makeQuery(id+"F6.imprint","IMPRINT",FACE,{"disambiguationData":[TD([[makeQuery(id+"F6.imprint","IMPRINT",EDGE,{"derivedFrom":sQuery(id+"F6.wireOp",EDGE,"E43.14.0.22")}),1.0]])]});
            var Q792;
            Q792=makeQuery(id+"F6.imprint","IMPRINT",FACE,{"disambiguationData":[TD([[makeQuery(id+"F6.imprint","IMPRINT",EDGE,{"derivedFrom":sQuery(id+"F6.wireOp",EDGE,"E43.14.0.5")}),1.0]])]});
            var Q793;
            Q793=makeQuery(id+"F6.imprint","IMPRINT",FACE,{"disambiguationData":[TD([[makeQuery(id+"F6.imprint","IMPRINT",EDGE,{"derivedFrom":sQuery(id+"F6.wireOp",EDGE,"E43.13.0.14")}),1.0]])]});
            var Q794;
            Q794=makeQuery(id+"F6.imprint","IMPRINT",FACE,{"disambiguationData":[TD([[makeQuery(id+"F6.imprint","IMPRINT",EDGE,{"derivedFrom":sQuery(id+"F6.wireOp",EDGE,"E43.12.0.22")}),1.0]])]});
            var Q795;
            Q795=makeQuery(id+"F6.imprint","IMPRINT",FACE,{"disambiguationData":[TD([[makeQuery(id+"F6.imprint","IMPRINT",EDGE,{"derivedFrom":sQuery(id+"F6.wireOp",EDGE,"E456.MirrorC")}),-1.0]])]});
            var Q796;
            Q796=makeQuery(id+"F6.imprint","IMPRINT",FACE,{"disambiguationData":[TD([[makeQuery(id+"F6.imprint","IMPRINT",EDGE,{"derivedFrom":sQuery(id+"F6.wireOp",EDGE,"E43.16.0.22")}),1.0]])]});
            var Q797;
            Q797=makeQuery(id+"F6.imprint","IMPRINT",FACE,{"disambiguationData":[TD([[makeQuery(id+"F6.imprint","IMPRINT",EDGE,{"derivedFrom":sQuery(id+"F6.wireOp",EDGE,"E43.16.0.5")}),1.0]])]});
            var Q798;
            Q798=makeQuery(id+"F6.imprint","IMPRINT",FACE,{"disambiguationData":[TD([[makeQuery(id+"F6.imprint","IMPRINT",EDGE,{"derivedFrom":sQuery(id+"F6.wireOp",EDGE,"E43.15.0.14")}),1.0]])]});
            var Q799;
            Q799=makeQuery(id+"F6.imprint","IMPRINT",FACE,{"disambiguationData":[TD([[makeQuery(id+"F6.imprint","IMPRINT",EDGE,{"derivedFrom":sQuery(id+"F6.wireOp",EDGE,"E404.MirrorC")}),-1.0]])]});
            var Q800;
            Q800=makeQuery(id+"F6.imprint","IMPRINT",FACE,{"disambiguationData":[TD([[makeQuery(id+"F6.imprint","IMPRINT",EDGE,{"derivedFrom":sQuery(id+"F6.wireOp",EDGE,"E43.18.0.22")}),1.0]])]});
            var Q801;
            Q801=makeQuery(id+"F6.imprint","IMPRINT",FACE,{"disambiguationData":[TD([[makeQuery(id+"F6.imprint","IMPRINT",EDGE,{"derivedFrom":sQuery(id+"F6.wireOp",EDGE,"E43.18.0.5")}),1.0]])]});
            var Q802;
            Q802=makeQuery(id+"F6.imprint","IMPRINT",FACE,{"disambiguationData":[TD([[makeQuery(id+"F6.imprint","IMPRINT",EDGE,{"derivedFrom":sQuery(id+"F6.wireOp",EDGE,"E43.17.0.14")}),1.0]])]});
            var Q803;
            Q803=makeQuery(id+"F6.imprint","IMPRINT",FACE,{"disambiguationData":[TD([[makeQuery(id+"F6.imprint","IMPRINT",EDGE,{"derivedFrom":sQuery(id+"F6.wireOp",EDGE,"E43.21.0.14")}),1.0]])]});
            var Q804;
            Q804=makeQuery(id+"F6.imprint","IMPRINT",FACE,{"disambiguationData":[TD([[makeQuery(id+"F6.imprint","IMPRINT",EDGE,{"derivedFrom":sQuery(id+"F6.wireOp",EDGE,"E43.20.0.22")}),1.0]])]});
            var Q805;
            Q805=makeQuery(id+"F6.imprint","IMPRINT",FACE,{"disambiguationData":[TD([[makeQuery(id+"F6.imprint","IMPRINT",EDGE,{"derivedFrom":sQuery(id+"F6.wireOp",EDGE,"E43.20.0.5")}),1.0]])]});
            var Q806;
            Q806=makeQuery(id+"F6.imprint","IMPRINT",FACE,{"disambiguationData":[TD([[makeQuery(id+"F6.imprint","IMPRINT",EDGE,{"derivedFrom":sQuery(id+"F6.wireOp",EDGE,"E43.19.0.14")}),1.0]])]});
            var Q807;
            Q807=makeQuery(id+"F6.imprint","IMPRINT",FACE,{"disambiguationData":[TD([[makeQuery(id+"F6.imprint","IMPRINT",EDGE,{"derivedFrom":sQuery(id+"F6.wireOp",EDGE,"E329.MirrorC")}),-1.0]])]});
            var Q808;
            Q808=makeQuery(id+"F6.imprint","IMPRINT",FACE,{"disambiguationData":[TD([[makeQuery(id+"F6.imprint","IMPRINT",EDGE,{"derivedFrom":sQuery(id+"F6.wireOp",EDGE,"E266.MirrorC")}),-1.0]])]});
            var Q809;
            Q809=makeQuery(id+"F6.imprint","IMPRINT",FACE,{"disambiguationData":[TD([[makeQuery(id+"F6.imprint","IMPRINT",EDGE,{"derivedFrom":sQuery(id+"F6.wireOp",EDGE,"E671.MirrorC")}),-1.0]])]});
            var Q810;
            Q810=makeQuery(id+"F6.imprint","IMPRINT",FACE,{"disambiguationData":[TD([[makeQuery(id+"F6.imprint","IMPRINT",EDGE,{"derivedFrom":sQuery(id+"F6.wireOp",EDGE,"E252.MirrorC")}),-1.0]])]});
            var Q811;
            Q811=makeQuery(id+"F6.imprint","IMPRINT",FACE,{"disambiguationData":[TD([[makeQuery(id+"F6.imprint","IMPRINT",EDGE,{"derivedFrom":sQuery(id+"F6.wireOp",EDGE,"E298.MirrorC")}),-1.0]])]});
            var Q812;
            Q812=makeQuery(id+"F6.imprint","IMPRINT",FACE,{"disambiguationData":[TD([[makeQuery(id+"F6.imprint","IMPRINT",EDGE,{"derivedFrom":sQuery(id+"F6.wireOp",EDGE,"E282.MirrorC")}),-1.0]])]});
            var Q813;
            Q813=makeQuery(id+"F6.imprint","IMPRINT",FACE,{"disambiguationData":[TD([[makeQuery(id+"F6.imprint","IMPRINT",EDGE,{"derivedFrom":sQuery(id+"F6.wireOp",EDGE,"E604.MirrorC")}),-1.0]])]});
            var Q814;
            Q814=makeQuery(id+"F6.imprint","IMPRINT",FACE,{"disambiguationData":[TD([[makeQuery(id+"F6.imprint","IMPRINT",EDGE,{"derivedFrom":sQuery(id+"F6.wireOp",EDGE,"E43.1.0.15")}),1.0]])]});
            var Q815;
            Q815=makeQuery(id+"F6.imprint","IMPRINT",FACE,{"disambiguationData":[TD([[makeQuery(id+"F6.imprint","IMPRINT",EDGE,{"derivedFrom":sQuery(id+"F6.wireOp",EDGE,"E42.0.8.0")}),1.0]])]});
            var Q816;
            Q816=makeQuery(id+"F6.imprint","IMPRINT",FACE,{"disambiguationData":[TD([[makeQuery(id+"F6.imprint","IMPRINT",EDGE,{"derivedFrom":sQuery(id+"F6.wireOp",EDGE,"E656.MirrorC")}),-1.0]])]});
            var Q817;
            Q817=makeQuery(id+"F6.imprint","IMPRINT",FACE,{"disambiguationData":[TD([[makeQuery(id+"F6.imprint","IMPRINT",EDGE,{"derivedFrom":sQuery(id+"F6.wireOp",EDGE,"E43.4.0.6")}),1.0]])]});
            var Q818;
            Q818=makeQuery(id+"F6.imprint","IMPRINT",FACE,{"disambiguationData":[TD([[makeQuery(id+"F6.imprint","IMPRINT",EDGE,{"derivedFrom":sQuery(id+"F6.wireOp",EDGE,"E43.3.0.15")}),1.0]])]});
            var Q819;
            Q819=makeQuery(id+"F6.imprint","IMPRINT",FACE,{"disambiguationData":[TD([[makeQuery(id+"F6.imprint","IMPRINT",EDGE,{"derivedFrom":sQuery(id+"F6.wireOp",EDGE,"E43.2.0.6")}),1.0]])]});
            var Q820;
            Q820=makeQuery(id+"F6.imprint","IMPRINT",FACE,{"disambiguationData":[TD([[makeQuery(id+"F6.imprint","IMPRINT",EDGE,{"derivedFrom":sQuery(id+"F6.wireOp",EDGE,"E358.MirrorC")}),-1.0]])]});
            var Q821;
            Q821=makeQuery(id+"F6.imprint","IMPRINT",FACE,{"disambiguationData":[TD([[makeQuery(id+"F6.imprint","IMPRINT",EDGE,{"derivedFrom":sQuery(id+"F6.wireOp",EDGE,"E410.MirrorC")}),-1.0]])]});
            var Q822;
            Q822=makeQuery(id+"F6.imprint","IMPRINT",FACE,{"disambiguationData":[TD([[makeQuery(id+"F6.imprint","IMPRINT",EDGE,{"derivedFrom":sQuery(id+"F6.wireOp",EDGE,"E43.6.0.6")}),1.0]])]});
            var Q823;
            Q823=makeQuery(id+"F6.imprint","IMPRINT",FACE,{"disambiguationData":[TD([[makeQuery(id+"F6.imprint","IMPRINT",EDGE,{"derivedFrom":sQuery(id+"F6.wireOp",EDGE,"E43.5.0.15")}),1.0]])]});
            var Q824;
            Q824=makeQuery(id+"F6.imprint","IMPRINT",FACE,{"disambiguationData":[TD([[makeQuery(id+"F6.imprint","IMPRINT",EDGE,{"derivedFrom":sQuery(id+"F6.wireOp",EDGE,"E687.MirrorC")}),-1.0]])]});
            var Q825;
            Q825=makeQuery(id+"F6.imprint","IMPRINT",FACE,{"disambiguationData":[TD([[makeQuery(id+"F6.imprint","IMPRINT",EDGE,{"derivedFrom":sQuery(id+"F6.wireOp",EDGE,"E634.MirrorC")}),-1.0]])]});
            var Q826;
            Q826=makeQuery(id+"F6.imprint","IMPRINT",FACE,{"disambiguationData":[TD([[makeQuery(id+"F6.imprint","IMPRINT",EDGE,{"derivedFrom":sQuery(id+"F6.wireOp",EDGE,"E425.MirrorC")}),-1.0]])]});
            var Q827;
            Q827=makeQuery(id+"F6.imprint","IMPRINT",FACE,{"disambiguationData":[TD([[makeQuery(id+"F6.imprint","IMPRINT",EDGE,{"derivedFrom":sQuery(id+"F6.wireOp",EDGE,"E619.MirrorC")}),-1.0]])]});
            var Q828;
            Q828=makeQuery(id+"F6.imprint","IMPRINT",FACE,{"disambiguationData":[TD([[makeQuery(id+"F6.imprint","IMPRINT",EDGE,{"derivedFrom":sQuery(id+"F6.wireOp",EDGE,"E314.MirrorC")}),-1.0]])]});
            var Q829;
            Q829=makeQuery(id+"F6.imprint","IMPRINT",FACE,{"disambiguationData":[TD([[makeQuery(id+"F6.imprint","IMPRINT",EDGE,{"derivedFrom":sQuery(id+"F6.wireOp",EDGE,"E373.MirrorC")}),-1.0]])]});
            var Q830;
            Q830=makeQuery(id+"F6.imprint","IMPRINT",FACE,{"disambiguationData":[TD([[makeQuery(id+"F6.imprint","IMPRINT",EDGE,{"derivedFrom":sQuery(id+"F6.wireOp",EDGE,"E43.26.0.6")}),1.0]])]});
            var Q831;
            Q831=makeQuery(id+"F6.imprint","IMPRINT",FACE,{"disambiguationData":[TD([[makeQuery(id+"F6.imprint","IMPRINT",EDGE,{"derivedFrom":sQuery(id+"F6.wireOp",EDGE,"E43.25.0.15")}),1.0]])]});
            var Q832;
            Q832=makeQuery(id+"F6.imprint","IMPRINT",FACE,{"disambiguationData":[TD([[makeQuery(id+"F6.imprint","IMPRINT",EDGE,{"derivedFrom":sQuery(id+"F6.wireOp",EDGE,"E43.29.0.15")}),1.0]])]});
            var Q833;
            Q833=makeQuery(id+"F6.imprint","IMPRINT",FACE,{"disambiguationData":[TD([[makeQuery(id+"F6.imprint","IMPRINT",EDGE,{"derivedFrom":sQuery(id+"F6.wireOp",EDGE,"E43.28.0.6")}),1.0]])]});
            var Q834;
            Q834=makeQuery(id+"F6.imprint","IMPRINT",FACE,{"disambiguationData":[TD([[makeQuery(id+"F6.imprint","IMPRINT",EDGE,{"derivedFrom":sQuery(id+"F6.wireOp",EDGE,"E43.27.0.15")}),1.0]])]});
            var Q835;
            Q835=makeQuery(id+"F6.imprint","IMPRINT",FACE,{"disambiguationData":[TD([[makeQuery(id+"F6.imprint","IMPRINT",EDGE,{"derivedFrom":sQuery(id+"F6.wireOp",EDGE,"E43.32.0.6")}),1.0]])]});
            var Q836;
            Q836=makeQuery(id+"F6.imprint","IMPRINT",FACE,{"disambiguationData":[TD([[makeQuery(id+"F6.imprint","IMPRINT",EDGE,{"derivedFrom":sQuery(id+"F6.wireOp",EDGE,"E43.31.0.15")}),1.0]])]});
            var Q837;
            Q837=makeQuery(id+"F6.imprint","IMPRINT",FACE,{"disambiguationData":[TD([[makeQuery(id+"F6.imprint","IMPRINT",EDGE,{"derivedFrom":sQuery(id+"F6.wireOp",EDGE,"E43.30.0.6")}),1.0]])]});
            var Q838;
            Q838=makeQuery(id+"F6.imprint","IMPRINT",FACE,{"disambiguationData":[TD([[makeQuery(id+"F6.imprint","IMPRINT",EDGE,{"derivedFrom":sQuery(id+"F6.wireOp",EDGE,"E710.MirrorC")}),-1.0]])]});
            var Q839;
            Q839=makeQuery(id+"F6.imprint","IMPRINT",FACE,{"disambiguationData":[TD([[makeQuery(id+"F6.imprint","IMPRINT",EDGE,{"derivedFrom":sQuery(id+"F6.wireOp",EDGE,"E502.MirrorC")}),-1.0]])]});
            var Q840;
            Q840=makeQuery(id+"F6.imprint","IMPRINT",FACE,{"disambiguationData":[TD([[makeQuery(id+"F6.imprint","IMPRINT",EDGE,{"derivedFrom":sQuery(id+"F6.wireOp",EDGE,"E43.9.0.15")}),1.0]])]});
            var Q841;
            Q841=makeQuery(id+"F6.imprint","IMPRINT",FACE,{"disambiguationData":[TD([[makeQuery(id+"F6.imprint","IMPRINT",EDGE,{"derivedFrom":sQuery(id+"F6.wireOp",EDGE,"E43.8.0.6")}),1.0]])]});
            var Q842;
            Q842=makeQuery(id+"F6.imprint","IMPRINT",FACE,{"disambiguationData":[TD([[makeQuery(id+"F6.imprint","IMPRINT",EDGE,{"derivedFrom":sQuery(id+"F6.wireOp",EDGE,"E43.7.0.15")}),1.0]])]});
            var Q843;
            Q843=makeQuery(id+"F6.imprint","IMPRINT",FACE,{"disambiguationData":[TD([[makeQuery(id+"F6.imprint","IMPRINT",EDGE,{"derivedFrom":sQuery(id+"F6.wireOp",EDGE,"E43.12.0.6")}),1.0]])]});
            var Q844;
            Q844=makeQuery(id+"F6.imprint","IMPRINT",FACE,{"disambiguationData":[TD([[makeQuery(id+"F6.imprint","IMPRINT",EDGE,{"derivedFrom":sQuery(id+"F6.wireOp",EDGE,"E43.11.0.15")}),1.0]])]});
            var Q845;
            Q845=makeQuery(id+"F6.imprint","IMPRINT",FACE,{"disambiguationData":[TD([[makeQuery(id+"F6.imprint","IMPRINT",EDGE,{"derivedFrom":sQuery(id+"F6.wireOp",EDGE,"E43.10.0.6")}),1.0]])]});
            var Q846;
            Q846=makeQuery(id+"F6.imprint","IMPRINT",FACE,{"disambiguationData":[TD([[makeQuery(id+"F6.imprint","IMPRINT",EDGE,{"derivedFrom":sQuery(id+"F6.wireOp",EDGE,"E43.14.0.6")}),1.0]])]});
            var Q847;
            Q847=makeQuery(id+"F6.imprint","IMPRINT",FACE,{"disambiguationData":[TD([[makeQuery(id+"F6.imprint","IMPRINT",EDGE,{"derivedFrom":sQuery(id+"F6.wireOp",EDGE,"E43.13.0.15")}),1.0]])]});
            var Q848;
            Q848=makeQuery(id+"F6.imprint","IMPRINT",FACE,{"disambiguationData":[TD([[makeQuery(id+"F6.imprint","IMPRINT",EDGE,{"derivedFrom":sQuery(id+"F6.wireOp",EDGE,"E726.MirrorC")}),-1.0]])]});
            var Q849;
            Q849=makeQuery(id+"F6.imprint","IMPRINT",FACE,{"disambiguationData":[TD([[makeQuery(id+"F6.imprint","IMPRINT",EDGE,{"derivedFrom":sQuery(id+"F6.wireOp",EDGE,"E43.16.0.6")}),1.0]])]});
            var Q850;
            Q850=makeQuery(id+"F6.imprint","IMPRINT",FACE,{"disambiguationData":[TD([[makeQuery(id+"F6.imprint","IMPRINT",EDGE,{"derivedFrom":sQuery(id+"F6.wireOp",EDGE,"E43.15.0.15")}),1.0]])]});
            var Q851;
            Q851=makeQuery(id+"F6.imprint","IMPRINT",FACE,{"disambiguationData":[TD([[makeQuery(id+"F6.imprint","IMPRINT",EDGE,{"derivedFrom":sQuery(id+"F6.wireOp",EDGE,"E517.MirrorC")}),-1.0]])]});
            var Q852;
            Q852=makeQuery(id+"F6.imprint","IMPRINT",FACE,{"disambiguationData":[TD([[makeQuery(id+"F6.imprint","IMPRINT",EDGE,{"derivedFrom":sQuery(id+"F6.wireOp",EDGE,"E43.18.0.6")}),1.0]])]});
            var Q853;
            Q853=makeQuery(id+"F6.imprint","IMPRINT",FACE,{"disambiguationData":[TD([[makeQuery(id+"F6.imprint","IMPRINT",EDGE,{"derivedFrom":sQuery(id+"F6.wireOp",EDGE,"E43.17.0.15")}),1.0]])]});
            var Q854;
            Q854=makeQuery(id+"F6.imprint","IMPRINT",FACE,{"disambiguationData":[TD([[makeQuery(id+"F6.imprint","IMPRINT",EDGE,{"derivedFrom":sQuery(id+"F6.wireOp",EDGE,"E465.MirrorC")}),-1.0]])]});
            var Q855;
            Q855=makeQuery(id+"F6.imprint","IMPRINT",FACE,{"disambiguationData":[TD([[makeQuery(id+"F6.imprint","IMPRINT",EDGE,{"derivedFrom":sQuery(id+"F6.wireOp",EDGE,"E43.21.0.15")}),1.0]])]});
            var Q856;
            Q856=makeQuery(id+"F6.imprint","IMPRINT",FACE,{"disambiguationData":[TD([[makeQuery(id+"F6.imprint","IMPRINT",EDGE,{"derivedFrom":sQuery(id+"F6.wireOp",EDGE,"E43.20.0.6")}),1.0]])]});
            var Q857;
            Q857=makeQuery(id+"F6.imprint","IMPRINT",FACE,{"disambiguationData":[TD([[makeQuery(id+"F6.imprint","IMPRINT",EDGE,{"derivedFrom":sQuery(id+"F6.wireOp",EDGE,"E43.19.0.15")}),1.0]])]});
            var Q858;
            Q858=makeQuery(id+"F6.imprint","IMPRINT",FACE,{"disambiguationData":[TD([[makeQuery(id+"F6.imprint","IMPRINT",EDGE,{"derivedFrom":sQuery(id+"F6.wireOp",EDGE,"E43.24.0.6")}),1.0]])]});
            var Q859;
            Q859=makeQuery(id+"F6.imprint","IMPRINT",FACE,{"disambiguationData":[TD([[makeQuery(id+"F6.imprint","IMPRINT",EDGE,{"derivedFrom":sQuery(id+"F6.wireOp",EDGE,"E43.23.0.15")}),1.0]])]});
            var Q860;
            Q860=makeQuery(id+"F6.imprint","IMPRINT",FACE,{"disambiguationData":[TD([[makeQuery(id+"F6.imprint","IMPRINT",EDGE,{"derivedFrom":sQuery(id+"F6.wireOp",EDGE,"E43.22.0.6")}),1.0]])]});
            var Q861;
            Q861=makeQuery(id+"F6.imprint","IMPRINT",FACE,{"disambiguationData":[TD([[makeQuery(id+"F6.imprint","IMPRINT",EDGE,{"derivedFrom":sQuery(id+"F6.wireOp",EDGE,"E267.MirrorC")}),-1.0]])]});
            var Q862;
            Q862=makeQuery(id+"F6.imprint","IMPRINT",FACE,{"disambiguationData":[TD([[makeQuery(id+"F6.imprint","IMPRINT",EDGE,{"derivedFrom":sQuery(id+"F6.wireOp",EDGE,"E253.MirrorC")}),-1.0]])]});
            var Q863;
            Q863=makeQuery(id+"F6.imprint","IMPRINT",FACE,{"disambiguationData":[TD([[makeQuery(id+"F6.imprint","IMPRINT",EDGE,{"derivedFrom":sQuery(id+"F6.wireOp",EDGE,"E680.MirrorC")}),-1.0]])]});
            var Q864;
            Q864=makeQuery(id+"F6.imprint","IMPRINT",FACE,{"disambiguationData":[TD([[makeQuery(id+"F6.imprint","IMPRINT",EDGE,{"derivedFrom":sQuery(id+"F6.wireOp",EDGE,"E299.MirrorC")}),-1.0]])]});
            var Q865;
            Q865=makeQuery(id+"F6.imprint","IMPRINT",FACE,{"disambiguationData":[TD([[makeQuery(id+"F6.imprint","IMPRINT",EDGE,{"derivedFrom":sQuery(id+"F6.wireOp",EDGE,"E283.MirrorC")}),-1.0]])]});
            var Q866;
            Q866=makeQuery(id+"F6.imprint","IMPRINT",FACE,{"disambiguationData":[TD([[makeQuery(id+"F6.imprint","IMPRINT",EDGE,{"derivedFrom":sQuery(id+"F6.wireOp",EDGE,"E419.MirrorC")}),-1.0]])]});
            var Q867;
            Q867=makeQuery(id+"F6.imprint","IMPRINT",FACE,{"disambiguationData":[TD([[makeQuery(id+"F6.imprint","IMPRINT",EDGE,{"derivedFrom":sQuery(id+"F6.wireOp",EDGE,"E43.1.0.16")}),1.0]])]});
            var Q868;
            Q868=makeQuery(id+"F6.imprint","IMPRINT",FACE,{"disambiguationData":[TD([[makeQuery(id+"F6.imprint","IMPRINT",EDGE,{"derivedFrom":sQuery(id+"F6.wireOp",EDGE,"E471.MirrorC")}),-1.0]])]});
            var Q869;
            Q869=makeQuery(id+"F6.imprint","IMPRINT",FACE,{"disambiguationData":[TD([[makeQuery(id+"F6.imprint","IMPRINT",EDGE,{"derivedFrom":sQuery(id+"F6.wireOp",EDGE,"E42.0.9.0")}),1.0]])]});
            var Q870;
            Q870=makeQuery(id+"F6.imprint","IMPRINT",FACE,{"disambiguationData":[TD([[makeQuery(id+"F6.imprint","IMPRINT",EDGE,{"derivedFrom":sQuery(id+"F6.wireOp",EDGE,"E43.4.0.7")}),1.0]])]});
            var Q871;
            Q871=makeQuery(id+"F6.imprint","IMPRINT",FACE,{"disambiguationData":[TD([[makeQuery(id+"F6.imprint","IMPRINT",EDGE,{"derivedFrom":sQuery(id+"F6.wireOp",EDGE,"E43.3.0.16")}),1.0]])]});
            var Q872;
            Q872=makeQuery(id+"F6.imprint","IMPRINT",FACE,{"disambiguationData":[TD([[makeQuery(id+"F6.imprint","IMPRINT",EDGE,{"derivedFrom":sQuery(id+"F6.wireOp",EDGE,"E43.2.0.7")}),1.0]])]});
            var Q873;
            Q873=makeQuery(id+"F6.imprint","IMPRINT",FACE,{"disambiguationData":[TD([[makeQuery(id+"F6.imprint","IMPRINT",EDGE,{"derivedFrom":sQuery(id+"F6.wireOp",EDGE,"E43.6.0.7")}),1.0]])]});
            var Q874;
            Q874=makeQuery(id+"F6.imprint","IMPRINT",FACE,{"disambiguationData":[TD([[makeQuery(id+"F6.imprint","IMPRINT",EDGE,{"derivedFrom":sQuery(id+"F6.wireOp",EDGE,"E43.5.0.16")}),1.0]])]});
            var Q875;
            Q875=makeQuery(id+"F6.imprint","IMPRINT",FACE,{"disambiguationData":[TD([[makeQuery(id+"F6.imprint","IMPRINT",EDGE,{"derivedFrom":sQuery(id+"F6.wireOp",EDGE,"E43.9.0.16")}),1.0]])]});
            var Q876;
            Q876=makeQuery(id+"F6.imprint","IMPRINT",FACE,{"disambiguationData":[TD([[makeQuery(id+"F6.imprint","IMPRINT",EDGE,{"derivedFrom":sQuery(id+"F6.wireOp",EDGE,"E43.8.0.7")}),1.0]])]});
            var Q877;
            Q877=makeQuery(id+"F6.imprint","IMPRINT",FACE,{"disambiguationData":[TD([[makeQuery(id+"F6.imprint","IMPRINT",EDGE,{"derivedFrom":sQuery(id+"F6.wireOp",EDGE,"E43.7.0.16")}),1.0]])]});
            var Q878;
            Q878=makeQuery(id+"F6.imprint","IMPRINT",FACE,{"disambiguationData":[TD([[makeQuery(id+"F6.imprint","IMPRINT",EDGE,{"derivedFrom":sQuery(id+"F6.wireOp",EDGE,"E695.MirrorC")}),-1.0]])]});
            var Q879;
            Q879=makeQuery(id+"F6.imprint","IMPRINT",FACE,{"disambiguationData":[TD([[makeQuery(id+"F6.imprint","IMPRINT",EDGE,{"derivedFrom":sQuery(id+"F6.wireOp",EDGE,"E434.MirrorC")}),-1.0]])]});
            var Q880;
            Q880=makeQuery(id+"F6.imprint","IMPRINT",FACE,{"disambiguationData":[TD([[makeQuery(id+"F6.imprint","IMPRINT",EDGE,{"derivedFrom":sQuery(id+"F6.wireOp",EDGE,"E487.MirrorC")}),-1.0]])]});
            var Q881;
            Q881=makeQuery(id+"F6.imprint","IMPRINT",FACE,{"disambiguationData":[TD([[makeQuery(id+"F6.imprint","IMPRINT",EDGE,{"derivedFrom":sQuery(id+"F6.wireOp",EDGE,"E315.MirrorC")}),-1.0]])]});
            var Q882;
            Q882=makeQuery(id+"F6.imprint","IMPRINT",FACE,{"disambiguationData":[TD([[makeQuery(id+"F6.imprint","IMPRINT",EDGE,{"derivedFrom":sQuery(id+"F6.wireOp",EDGE,"E330.MirrorC")}),-1.0]])]});
            var Q883;
            Q883=makeQuery(id+"F6.imprint","IMPRINT",FACE,{"disambiguationData":[TD([[makeQuery(id+"F6.imprint","IMPRINT",EDGE,{"derivedFrom":sQuery(id+"F6.wireOp",EDGE,"E43.29.0.16")}),1.0]])]});
            var Q884;
            Q884=makeQuery(id+"F6.imprint","IMPRINT",FACE,{"disambiguationData":[TD([[makeQuery(id+"F6.imprint","IMPRINT",EDGE,{"derivedFrom":sQuery(id+"F6.wireOp",EDGE,"E43.28.0.7")}),1.0]])]});
            var Q885;
            Q885=makeQuery(id+"F6.imprint","IMPRINT",FACE,{"disambiguationData":[TD([[makeQuery(id+"F6.imprint","IMPRINT",EDGE,{"derivedFrom":sQuery(id+"F6.wireOp",EDGE,"E43.27.0.16")}),1.0]])]});
            var Q886;
            Q886=makeQuery(id+"F6.imprint","IMPRINT",FACE,{"disambiguationData":[TD([[makeQuery(id+"F6.imprint","IMPRINT",EDGE,{"derivedFrom":sQuery(id+"F6.wireOp",EDGE,"E43.32.0.7")}),1.0]])]});
            var Q887;
            Q887=makeQuery(id+"F6.imprint","IMPRINT",FACE,{"disambiguationData":[TD([[makeQuery(id+"F6.imprint","IMPRINT",EDGE,{"derivedFrom":sQuery(id+"F6.wireOp",EDGE,"E43.31.0.16")}),1.0]])]});
            var Q888;
            Q888=makeQuery(id+"F6.imprint","IMPRINT",FACE,{"disambiguationData":[TD([[makeQuery(id+"F6.imprint","IMPRINT",EDGE,{"derivedFrom":sQuery(id+"F6.wireOp",EDGE,"E43.30.0.7")}),1.0]])]});
            var Q889;
            Q889=makeQuery(id+"F6.imprint","IMPRINT",FACE,{"disambiguationData":[TD([[makeQuery(id+"F6.imprint","IMPRINT",EDGE,{"derivedFrom":sQuery(id+"F6.wireOp",EDGE,"E579.MirrorC")}),-1.0]])]});
            var Q890;
            Q890=makeQuery(id+"F6.imprint","IMPRINT",FACE,{"disambiguationData":[TD([[makeQuery(id+"F6.imprint","IMPRINT",EDGE,{"derivedFrom":sQuery(id+"F6.wireOp",EDGE,"E526.MirrorC")}),-1.0]])]});
            var Q891;
            Q891=makeQuery(id+"F6.imprint","IMPRINT",FACE,{"disambiguationData":[TD([[makeQuery(id+"F6.imprint","IMPRINT",EDGE,{"derivedFrom":sQuery(id+"F6.wireOp",EDGE,"E43.12.0.7")}),1.0]])]});
            var Q892;
            Q892=makeQuery(id+"F6.imprint","IMPRINT",FACE,{"disambiguationData":[TD([[makeQuery(id+"F6.imprint","IMPRINT",EDGE,{"derivedFrom":sQuery(id+"F6.wireOp",EDGE,"E43.11.0.16")}),1.0]])]});
            var Q893;
            Q893=makeQuery(id+"F6.imprint","IMPRINT",FACE,{"disambiguationData":[TD([[makeQuery(id+"F6.imprint","IMPRINT",EDGE,{"derivedFrom":sQuery(id+"F6.wireOp",EDGE,"E748.MirrorC")}),-1.0]])]});
            var Q894;
            Q894=makeQuery(id+"F6.imprint","IMPRINT",FACE,{"disambiguationData":[TD([[makeQuery(id+"F6.imprint","IMPRINT",EDGE,{"derivedFrom":sQuery(id+"F6.wireOp",EDGE,"E43.10.0.7")}),1.0]])]});
            var Q895;
            Q895=makeQuery(id+"F6.imprint","IMPRINT",FACE,{"disambiguationData":[TD([[makeQuery(id+"F6.imprint","IMPRINT",EDGE,{"derivedFrom":sQuery(id+"F6.wireOp",EDGE,"E43.14.0.7")}),1.0]])]});
            var Q896;
            Q896=makeQuery(id+"F6.imprint","IMPRINT",FACE,{"disambiguationData":[TD([[makeQuery(id+"F6.imprint","IMPRINT",EDGE,{"derivedFrom":sQuery(id+"F6.wireOp",EDGE,"E43.13.0.16")}),1.0]])]});
            var Q897;
            Q897=makeQuery(id+"F6.imprint","IMPRINT",FACE,{"disambiguationData":[TD([[makeQuery(id+"F6.imprint","IMPRINT",EDGE,{"derivedFrom":sQuery(id+"F6.wireOp",EDGE,"E542.MirrorC")}),-1.0]])]});
            var Q898;
            Q898=makeQuery(id+"F6.imprint","IMPRINT",FACE,{"disambiguationData":[TD([[makeQuery(id+"F6.imprint","IMPRINT",EDGE,{"derivedFrom":sQuery(id+"F6.wireOp",EDGE,"E594.MirrorC")}),-1.0]])]});
            var Q899;
            Q899=makeQuery(id+"F6.imprint","IMPRINT",FACE,{"disambiguationData":[TD([[makeQuery(id+"F6.imprint","IMPRINT",EDGE,{"derivedFrom":sQuery(id+"F6.wireOp",EDGE,"E43.16.0.7")}),1.0]])]});
            var Q900;
            Q900=makeQuery(id+"F6.imprint","IMPRINT",FACE,{"disambiguationData":[TD([[makeQuery(id+"F6.imprint","IMPRINT",EDGE,{"derivedFrom":sQuery(id+"F6.wireOp",EDGE,"E43.15.0.16")}),1.0]])]});
            var Q901;
            Q901=makeQuery(id+"F6.imprint","IMPRINT",FACE,{"disambiguationData":[TD([[makeQuery(id+"F6.imprint","IMPRINT",EDGE,{"derivedFrom":sQuery(id+"F6.wireOp",EDGE,"E43.18.0.7")}),1.0]])]});
            var Q902;
            Q902=makeQuery(id+"F6.imprint","IMPRINT",FACE,{"disambiguationData":[TD([[makeQuery(id+"F6.imprint","IMPRINT",EDGE,{"derivedFrom":sQuery(id+"F6.wireOp",EDGE,"E43.17.0.16")}),1.0]])]});
            var Q903;
            Q903=makeQuery(id+"F6.imprint","IMPRINT",FACE,{"disambiguationData":[TD([[makeQuery(id+"F6.imprint","IMPRINT",EDGE,{"derivedFrom":sQuery(id+"F6.wireOp",EDGE,"E43.21.0.16")}),1.0]])]});
            var Q904;
            Q904=makeQuery(id+"F6.imprint","IMPRINT",FACE,{"disambiguationData":[TD([[makeQuery(id+"F6.imprint","IMPRINT",EDGE,{"derivedFrom":sQuery(id+"F6.wireOp",EDGE,"E43.20.0.7")}),1.0]])]});
            var Q905;
            Q905=makeQuery(id+"F6.imprint","IMPRINT",FACE,{"disambiguationData":[TD([[makeQuery(id+"F6.imprint","IMPRINT",EDGE,{"derivedFrom":sQuery(id+"F6.wireOp",EDGE,"E43.19.0.16")}),1.0]])]});
            var Q906;
            Q906=makeQuery(id+"F6.imprint","IMPRINT",FACE,{"disambiguationData":[TD([[makeQuery(id+"F6.imprint","IMPRINT",EDGE,{"derivedFrom":sQuery(id+"F6.wireOp",EDGE,"E43.24.0.7")}),1.0]])]});
            var Q907;
            Q907=makeQuery(id+"F6.imprint","IMPRINT",FACE,{"disambiguationData":[TD([[makeQuery(id+"F6.imprint","IMPRINT",EDGE,{"derivedFrom":sQuery(id+"F6.wireOp",EDGE,"E43.23.0.16")}),1.0]])]});
            var Q908;
            Q908=makeQuery(id+"F6.imprint","IMPRINT",FACE,{"disambiguationData":[TD([[makeQuery(id+"F6.imprint","IMPRINT",EDGE,{"derivedFrom":sQuery(id+"F6.wireOp",EDGE,"E43.22.0.7")}),1.0]])]});
            var Q909;
            Q909=makeQuery(id+"F6.imprint","IMPRINT",FACE,{"disambiguationData":[TD([[makeQuery(id+"F6.imprint","IMPRINT",EDGE,{"derivedFrom":sQuery(id+"F6.wireOp",EDGE,"E43.26.0.7")}),1.0]])]});
            var Q910;
            Q910=makeQuery(id+"F6.imprint","IMPRINT",FACE,{"disambiguationData":[TD([[makeQuery(id+"F6.imprint","IMPRINT",EDGE,{"derivedFrom":sQuery(id+"F6.wireOp",EDGE,"E43.25.0.16")}),1.0]])]});
            var Q911;
            Q911=makeQuery(id+"F6.imprint","IMPRINT",FACE,{"disambiguationData":[TD([[makeQuery(id+"F6.imprint","IMPRINT",EDGE,{"derivedFrom":sQuery(id+"F6.wireOp",EDGE,"E548.MirrorC")}),-1.0]])]});
            var Q912;
            Q912=makeQuery(id+"F6.imprint","IMPRINT",FACE,{"disambiguationData":[TD([[makeQuery(id+"F6.imprint","IMPRINT",EDGE,{"derivedFrom":sQuery(id+"F6.wireOp",EDGE,"E480.MirrorC")}),-1.0]])]});
            var Q913;
            Q913=makeQuery(id+"F6.imprint","IMPRINT",FACE,{"disambiguationData":[TD([[makeQuery(id+"F6.imprint","IMPRINT",EDGE,{"derivedFrom":sQuery(id+"F6.wireOp",EDGE,"E533.MirrorC")}),-1.0]])]});
            var Q914;
            Q914=makeQuery(id+"F6.imprint","IMPRINT",FACE,{"disambiguationData":[TD([[makeQuery(id+"F6.imprint","IMPRINT",EDGE,{"derivedFrom":sQuery(id+"F6.wireOp",EDGE,"E510.MirrorC")}),-1.0]])]});
            var Q915;
            Q915=makeQuery(id+"F6.imprint","IMPRINT",FACE,{"disambiguationData":[TD([[makeQuery(id+"F6.imprint","IMPRINT",EDGE,{"derivedFrom":sQuery(id+"F6.wireOp",EDGE,"E563.MirrorC")}),-1.0]])]});
            var Q916;
            Q916=makeQuery(id+"F6.imprint","IMPRINT",FACE,{"disambiguationData":[TD([[makeQuery(id+"F6.imprint","IMPRINT",EDGE,{"derivedFrom":sQuery(id+"F6.wireOp",EDGE,"E496.MirrorC")}),-1.0]])]});
            var Q917;
            Q917=makeQuery(id+"F6.imprint","IMPRINT",FACE,{"disambiguationData":[TD([[makeQuery(id+"F6.imprint","IMPRINT",EDGE,{"derivedFrom":sQuery(id+"F6.wireOp",EDGE,"E793.MirrorC")}),-1.0]])]});
            var Q918;
            Q918=makeQuery(id+"F6.imprint","IMPRINT",FACE,{"disambiguationData":[TD([[makeQuery(id+"F6.imprint","IMPRINT",EDGE,{"derivedFrom":sQuery(id+"F6.wireOp",EDGE,"E741.MirrorC")}),-1.0]])]});
            var Q919;
            Q919=makeQuery(id+"F6.imprint","IMPRINT",FACE,{"disambiguationData":[TD([[makeQuery(id+"F6.imprint","IMPRINT",EDGE,{"derivedFrom":sQuery(id+"F6.wireOp",EDGE,"E639.MirrorC")}),-1.0]])]});
            var Q920;
            Q920=makeQuery(id+"F6.imprint","IMPRINT",FACE,{"disambiguationData":[TD([[makeQuery(id+"F6.imprint","IMPRINT",EDGE,{"derivedFrom":sQuery(id+"F6.wireOp",EDGE,"E588.MirrorC")}),-1.0]])]});
            var Q921;
            Q921=makeQuery(id+"F6.imprint","IMPRINT",FACE,{"disambiguationData":[TD([[makeQuery(id+"F6.imprint","IMPRINT",EDGE,{"derivedFrom":sQuery(id+"F6.wireOp",EDGE,"E378.MirrorC")}),-1.0]])]});
            var Q922;
            Q922=makeQuery(id+"F6.imprint","IMPRINT",FACE,{"disambiguationData":[TD([[makeQuery(id+"F6.imprint","IMPRINT",EDGE,{"derivedFrom":sQuery(id+"F6.wireOp",EDGE,"E756.MirrorC")}),-1.0]])]});
            var Q923;
            Q923=makeQuery(id+"F6.imprint","IMPRINT",FACE,{"disambiguationData":[TD([[makeQuery(id+"F6.imprint","IMPRINT",EDGE,{"derivedFrom":sQuery(id+"F6.wireOp",EDGE,"E809.MirrorC")}),-1.0]])]});
            var Q924;
            Q924=makeQuery(id+"F6.imprint","IMPRINT",FACE,{"disambiguationData":[TD([[makeQuery(id+"F6.imprint","IMPRINT",EDGE,{"derivedFrom":sQuery(id+"F6.wireOp",EDGE,"E602.MirrorC")}),-1.0]])]});
            var Q925;
            Q925=makeQuery(id+"F6.imprint","IMPRINT",FACE,{"disambiguationData":[TD([[makeQuery(id+"F6.imprint","IMPRINT",EDGE,{"derivedFrom":sQuery(id+"F6.wireOp",EDGE,"E654.MirrorC")}),-1.0]])]});
            var Q926;
            Q926=makeQuery(id+"F6.imprint","IMPRINT",FACE,{"disambiguationData":[TD([[makeQuery(id+"F6.imprint","IMPRINT",EDGE,{"derivedFrom":sQuery(id+"F6.wireOp",EDGE,"E394.MirrorC")}),-1.0]])]});
            var Q927;
            Q927=makeQuery(id+"F6.imprint","IMPRINT",FACE,{"disambiguationData":[TD([[makeQuery(id+"F6.imprint","IMPRINT",EDGE,{"derivedFrom":sQuery(id+"F6.wireOp",EDGE,"E763.MirrorC")}),-1.0]])]});
            var Q928;
            Q928=makeQuery(id+"F6.imprint","IMPRINT",FACE,{"disambiguationData":[TD([[makeQuery(id+"F6.imprint","IMPRINT",EDGE,{"derivedFrom":sQuery(id+"F6.wireOp",EDGE,"E557.MirrorC")}),-1.0]])]});
            var Q929;
            Q929=makeQuery(id+"F6.imprint","IMPRINT",FACE,{"disambiguationData":[TD([[makeQuery(id+"F6.imprint","IMPRINT",EDGE,{"derivedFrom":sQuery(id+"F6.wireOp",EDGE,"E609.MirrorC")}),-1.0]])]});
            var Q930;
            Q930=makeQuery(id+"F6.imprint","IMPRINT",FACE,{"disambiguationData":[TD([[makeQuery(id+"F6.imprint","IMPRINT",EDGE,{"derivedFrom":sQuery(id+"F6.wireOp",EDGE,"E348.MirrorC")}),-1.0]])]});
            var Q931;
            Q931=makeQuery(id+"F6.imprint","IMPRINT",FACE,{"disambiguationData":[TD([[makeQuery(id+"F6.imprint","IMPRINT",EDGE,{"derivedFrom":sQuery(id+"F6.wireOp",EDGE,"E778.MirrorC")}),-1.0]])]});
            var Q932;
            Q932=makeQuery(id+"F6.imprint","IMPRINT",FACE,{"disambiguationData":[TD([[makeQuery(id+"F6.imprint","IMPRINT",EDGE,{"derivedFrom":sQuery(id+"F6.wireOp",EDGE,"E572.MirrorC")}),-1.0]])]});
            var Q933;
            Q933=makeQuery(id+"F6.imprint","IMPRINT",FACE,{"disambiguationData":[TD([[makeQuery(id+"F6.imprint","IMPRINT",EDGE,{"derivedFrom":sQuery(id+"F6.wireOp",EDGE,"E624.MirrorC")}),-1.0]])]});
            var Q934;
            Q934=makeQuery(id+"F6.imprint","IMPRINT",FACE,{"disambiguationData":[TD([[makeQuery(id+"F6.imprint","IMPRINT",EDGE,{"derivedFrom":sQuery(id+"F6.wireOp",EDGE,"E362.MirrorC")}),-1.0]])]});
            var Q935;
            Q935=makeQuery(id+"F6.imprint","IMPRINT",FACE,{"disambiguationData":[TD([[makeQuery(id+"F6.imprint","IMPRINT",EDGE,{"derivedFrom":sQuery(id+"F6.wireOp",EDGE,"E700.MirrorC")}),-1.0]])]});
            var Q936;
            Q936=makeQuery(id+"F6.imprint","IMPRINT",FACE,{"disambiguationData":[TD([[makeQuery(id+"F6.imprint","IMPRINT",EDGE,{"derivedFrom":sQuery(id+"F6.wireOp",EDGE,"E647.MirrorC")}),-1.0]])]});
            var Q937;
            Q937=makeQuery(id+"F6.imprint","IMPRINT",FACE,{"disambiguationData":[TD([[makeQuery(id+"F6.imprint","IMPRINT",EDGE,{"derivedFrom":sQuery(id+"F6.wireOp",EDGE,"E454.MirrorC")}),-1.0]])]});
            var Q938;
            Q938=makeQuery(id+"F6.imprint","IMPRINT",FACE,{"disambiguationData":[TD([[makeQuery(id+"F6.imprint","IMPRINT",EDGE,{"derivedFrom":sQuery(id+"F6.wireOp",EDGE,"E43.2.0.8")}),1.0]])]});
            var Q939;
            Q939=makeQuery(id+"F6.imprint","IMPRINT",FACE,{"disambiguationData":[TD([[makeQuery(id+"F6.imprint","IMPRINT",EDGE,{"derivedFrom":sQuery(id+"F6.wireOp",EDGE,"E43.1.0.17")}),1.0]])]});
            var Q940;
            Q940=makeQuery(id+"F6.imprint","IMPRINT",FACE,{"disambiguationData":[TD([[makeQuery(id+"F6.imprint","IMPRINT",EDGE,{"derivedFrom":sQuery(id+"F6.wireOp",EDGE,"E42.0.10.0")}),1.0]])]});
            var Q941;
            Q941=makeQuery(id+"F6.imprint","IMPRINT",FACE,{"disambiguationData":[TD([[makeQuery(id+"F6.imprint","IMPRINT",EDGE,{"derivedFrom":sQuery(id+"F6.wireOp",EDGE,"E402.MirrorC")}),-1.0]])]});
            var Q942;
            Q942=makeQuery(id+"F6.imprint","IMPRINT",FACE,{"disambiguationData":[TD([[makeQuery(id+"F6.imprint","IMPRINT",EDGE,{"derivedFrom":sQuery(id+"F6.wireOp",EDGE,"E43.5.0.17")}),1.0]])]});
            var Q943;
            Q943=makeQuery(id+"F6.imprint","IMPRINT",FACE,{"disambiguationData":[TD([[makeQuery(id+"F6.imprint","IMPRINT",EDGE,{"derivedFrom":sQuery(id+"F6.wireOp",EDGE,"E43.4.0.8")}),1.0]])]});
            var Q944;
            Q944=makeQuery(id+"F6.imprint","IMPRINT",FACE,{"disambiguationData":[TD([[makeQuery(id+"F6.imprint","IMPRINT",EDGE,{"derivedFrom":sQuery(id+"F6.wireOp",EDGE,"E43.3.0.17")}),1.0]])]});
            var Q945;
            Q945=makeQuery(id+"F6.imprint","IMPRINT",FACE,{"disambiguationData":[TD([[makeQuery(id+"F6.imprint","IMPRINT",EDGE,{"derivedFrom":sQuery(id+"F6.wireOp",EDGE,"E43.8.0.8")}),1.0]])]});
            var Q946;
            Q946=makeQuery(id+"F6.imprint","IMPRINT",FACE,{"disambiguationData":[TD([[makeQuery(id+"F6.imprint","IMPRINT",EDGE,{"derivedFrom":sQuery(id+"F6.wireOp",EDGE,"E43.7.0.17")}),1.0]])]});
            var Q947;
            Q947=makeQuery(id+"F6.imprint","IMPRINT",FACE,{"disambiguationData":[TD([[makeQuery(id+"F6.imprint","IMPRINT",EDGE,{"derivedFrom":sQuery(id+"F6.wireOp",EDGE,"E43.6.0.8")}),1.0]])]});
            var Q948;
            Q948=makeQuery(id+"F6.imprint","IMPRINT",FACE,{"disambiguationData":[TD([[makeQuery(id+"F6.imprint","IMPRINT",EDGE,{"derivedFrom":sQuery(id+"F6.wireOp",EDGE,"E43.10.0.8")}),1.0]])]});
            var Q949;
            Q949=makeQuery(id+"F6.imprint","IMPRINT",FACE,{"disambiguationData":[TD([[makeQuery(id+"F6.imprint","IMPRINT",EDGE,{"derivedFrom":sQuery(id+"F6.wireOp",EDGE,"E43.9.0.17")}),1.0]])]});
            var Q950;
            Q950=makeQuery(id+"F6.imprint","IMPRINT",FACE,{"disambiguationData":[TD([[makeQuery(id+"F6.imprint","IMPRINT",EDGE,{"derivedFrom":sQuery(id+"F6.wireOp",EDGE,"E43.13.0.17")}),1.0]])]});
            var Q951;
            Q951=makeQuery(id+"F6.imprint","IMPRINT",FACE,{"disambiguationData":[TD([[makeQuery(id+"F6.imprint","IMPRINT",EDGE,{"derivedFrom":sQuery(id+"F6.wireOp",EDGE,"E43.12.0.8")}),1.0]])]});
            var Q952;
            Q952=makeQuery(id+"F6.imprint","IMPRINT",FACE,{"disambiguationData":[TD([[makeQuery(id+"F6.imprint","IMPRINT",EDGE,{"derivedFrom":sQuery(id+"F6.wireOp",EDGE,"E384.MirrorC")}),-1.0]])]});
            var Q953;
            Q953=makeQuery(id+"F6.imprint","IMPRINT",FACE,{"disambiguationData":[TD([[makeQuery(id+"F6.imprint","IMPRINT",EDGE,{"derivedFrom":sQuery(id+"F6.wireOp",EDGE,"E853.MirrorC")}),-1.0]])]});
            var Q954;
            Q954=makeQuery(id+"F6.imprint","IMPRINT",FACE,{"disambiguationData":[TD([[makeQuery(id+"F6.imprint","IMPRINT",EDGE,{"derivedFrom":sQuery(id+"F6.wireOp",EDGE,"E802.MirrorC")}),-1.0]])]});
            var Q955;
            Q955=makeQuery(id+"F6.imprint","IMPRINT",FACE,{"disambiguationData":[TD([[makeQuery(id+"F6.imprint","IMPRINT",EDGE,{"derivedFrom":sQuery(id+"F6.wireOp",EDGE,"E43.11.0.17")}),1.0]])]});
            var Q956;
            Q956=makeQuery(id+"F6.imprint","IMPRINT",FACE,{"disambiguationData":[TD([[makeQuery(id+"F6.imprint","IMPRINT",EDGE,{"derivedFrom":sQuery(id+"F6.wireOp",EDGE,"E43.16.0.8")}),1.0]])]});
            var Q957;
            Q957=makeQuery(id+"F6.imprint","IMPRINT",FACE,{"disambiguationData":[TD([[makeQuery(id+"F6.imprint","IMPRINT",EDGE,{"derivedFrom":sQuery(id+"F6.wireOp",EDGE,"E43.15.0.17")}),1.0]])]});
            var Q958;
            Q958=makeQuery(id+"F6.imprint","IMPRINT",FACE,{"disambiguationData":[TD([[makeQuery(id+"F6.imprint","IMPRINT",EDGE,{"derivedFrom":sQuery(id+"F6.wireOp",EDGE,"E43.14.0.8")}),1.0]])]});
            var Q959;
            Q959=makeQuery(id+"F6.imprint","IMPRINT",FACE,{"disambiguationData":[TD([[makeQuery(id+"F6.imprint","IMPRINT",EDGE,{"derivedFrom":sQuery(id+"F6.wireOp",EDGE,"E663.MirrorC")}),-1.0]])]});
            var Q960;
            Q960=makeQuery(id+"F6.imprint","IMPRINT",FACE,{"disambiguationData":[TD([[makeQuery(id+"F6.imprint","IMPRINT",EDGE,{"derivedFrom":sQuery(id+"F6.wireOp",EDGE,"E715.MirrorC")}),-1.0]])]});
            var Q961;
            Q961=makeQuery(id+"F6.imprint","IMPRINT",FACE,{"disambiguationData":[TD([[makeQuery(id+"F6.imprint","IMPRINT",EDGE,{"derivedFrom":sQuery(id+"F6.wireOp",EDGE,"E417.MirrorC")}),-1.0]])]});
            var Q962;
            Q962=makeQuery(id+"F6.imprint","IMPRINT",FACE,{"disambiguationData":[TD([[makeQuery(id+"F6.imprint","IMPRINT",EDGE,{"derivedFrom":sQuery(id+"F6.wireOp",EDGE,"E316.MirrorC")}),-1.0]])]});
            var Q963;
            Q963=makeQuery(id+"F6.imprint","IMPRINT",FACE,{"disambiguationData":[TD([[makeQuery(id+"F6.imprint","IMPRINT",EDGE,{"derivedFrom":sQuery(id+"F6.wireOp",EDGE,"E331.MirrorC")}),-1.0]])]});
            var Q964;
            Q964=makeQuery(id+"F6.imprint","IMPRINT",FACE,{"disambiguationData":[TD([[makeQuery(id+"F6.imprint","IMPRINT",EDGE,{"derivedFrom":sQuery(id+"F6.wireOp",EDGE,"E817.MirrorC")}),-1.0]])]});
            var Q965;
            Q965=makeQuery(id+"F6.imprint","IMPRINT",FACE,{"disambiguationData":[TD([[makeQuery(id+"F6.imprint","IMPRINT",EDGE,{"derivedFrom":sQuery(id+"F6.wireOp",EDGE,"E869.MirrorC")}),-1.0]])]});
            var Q966;
            Q966=makeQuery(id+"F6.imprint","IMPRINT",FACE,{"disambiguationData":[TD([[makeQuery(id+"F6.imprint","IMPRINT",EDGE,{"derivedFrom":sQuery(id+"F6.wireOp",EDGE,"E399.MirrorC")}),-1.0]])]});
            var Q967;
            Q967=makeQuery(id+"F6.imprint","IMPRINT",FACE,{"disambiguationData":[TD([[makeQuery(id+"F6.imprint","IMPRINT",EDGE,{"derivedFrom":sQuery(id+"F6.wireOp",EDGE,"E300.MirrorC")}),-1.0]])]});
            var Q968;
            Q968=makeQuery(id+"F6.imprint","IMPRINT",FACE,{"disambiguationData":[TD([[makeQuery(id+"F6.imprint","IMPRINT",EDGE,{"derivedFrom":sQuery(id+"F6.wireOp",EDGE,"E284.MirrorC")}),-1.0]])]});
            var Q969;
            Q969=makeQuery(id+"F6.imprint","IMPRINT",FACE,{"disambiguationData":[TD([[makeQuery(id+"F6.imprint","IMPRINT",EDGE,{"derivedFrom":sQuery(id+"F6.wireOp",EDGE,"E268.MirrorC")}),-1.0]])]});
            var Q970;
            Q970=makeQuery(id+"F6.imprint","IMPRINT",FACE,{"disambiguationData":[TD([[makeQuery(id+"F6.imprint","IMPRINT",EDGE,{"derivedFrom":sQuery(id+"F6.wireOp",EDGE,"E254.MirrorC")}),-1.0]])]});
            var Q971;
            Q971=makeQuery(id+"F6.imprint","IMPRINT",FACE,{"disambiguationData":[TD([[makeQuery(id+"F6.imprint","IMPRINT",EDGE,{"derivedFrom":sQuery(id+"F6.wireOp",EDGE,"E669.MirrorC")}),-1.0]])]});
            var Q972;
            Q972=makeQuery(id+"F6.imprint","IMPRINT",FACE,{"disambiguationData":[TD([[makeQuery(id+"F6.imprint","IMPRINT",EDGE,{"derivedFrom":sQuery(id+"F6.wireOp",EDGE,"E772.MirrorC")}),-1.0]])]});
            var Q973;
            Q973=makeQuery(id+"F6.imprint","IMPRINT",FACE,{"disambiguationData":[TD([[makeQuery(id+"F6.imprint","IMPRINT",EDGE,{"derivedFrom":sQuery(id+"F6.wireOp",EDGE,"E423.MirrorC")}),-1.0]])]});
            var Q974;
            Q974=makeQuery(id+"F6.imprint","IMPRINT",FACE,{"disambiguationData":[TD([[makeQuery(id+"F6.imprint","IMPRINT",EDGE,{"derivedFrom":sQuery(id+"F6.wireOp",EDGE,"E617.MirrorC")}),-1.0]])]});
            var Q975;
            Q975=makeQuery(id+"F6.imprint","IMPRINT",FACE,{"disambiguationData":[TD([[makeQuery(id+"F6.imprint","IMPRINT",EDGE,{"derivedFrom":sQuery(id+"F6.wireOp",EDGE,"E356.MirrorC")}),-1.0]])]});
            var Q976;
            Q976=makeQuery(id+"F6.imprint","IMPRINT",FACE,{"disambiguationData":[TD([[makeQuery(id+"F6.imprint","IMPRINT",EDGE,{"derivedFrom":sQuery(id+"F6.wireOp",EDGE,"E408.MirrorC")}),-1.0]])]});
            var Q977;
            Q977=makeQuery(id+"F6.imprint","IMPRINT",FACE,{"disambiguationData":[TD([[makeQuery(id+"F6.imprint","IMPRINT",EDGE,{"derivedFrom":sQuery(id+"F6.wireOp",EDGE,"E823.MirrorC")}),-1.0]])]});
            var Q978;
            Q978=makeQuery(id+"F6.imprint","IMPRINT",FACE,{"disambiguationData":[TD([[makeQuery(id+"F6.imprint","IMPRINT",EDGE,{"derivedFrom":sQuery(id+"F6.wireOp",EDGE,"E632.MirrorC")}),-1.0]])]});
            var Q979;
            Q979=makeQuery(id+"F6.imprint","IMPRINT",FACE,{"disambiguationData":[TD([[makeQuery(id+"F6.imprint","IMPRINT",EDGE,{"derivedFrom":sQuery(id+"F6.wireOp",EDGE,"E685.MirrorC")}),-1.0]])]});
            var Q980;
            Q980=makeQuery(id+"F6.imprint","IMPRINT",FACE,{"disambiguationData":[TD([[makeQuery(id+"F6.imprint","IMPRINT",EDGE,{"derivedFrom":sQuery(id+"F6.wireOp",EDGE,"E43.17.0.17")}),1.0]])]});
            var Q981;
            Q981=makeQuery(id+"F6.imprint","IMPRINT",FACE,{"disambiguationData":[TD([[makeQuery(id+"F6.imprint","IMPRINT",EDGE,{"derivedFrom":sQuery(id+"F6.wireOp",EDGE,"E368.MirrorC")}),-1.0]])]});
            var Q982;
            Q982=makeQuery(id+"F6.imprint","IMPRINT",FACE,{"disambiguationData":[TD([[makeQuery(id+"F6.imprint","IMPRINT",EDGE,{"derivedFrom":sQuery(id+"F6.wireOp",EDGE,"E43.20.0.8")}),1.0]])]});
            var Q983;
            Q983=makeQuery(id+"F6.imprint","IMPRINT",FACE,{"disambiguationData":[TD([[makeQuery(id+"F6.imprint","IMPRINT",EDGE,{"derivedFrom":sQuery(id+"F6.wireOp",EDGE,"E43.19.0.17")}),1.0]])]});
            var Q984;
            Q984=makeQuery(id+"F6.imprint","IMPRINT",FACE,{"disambiguationData":[TD([[makeQuery(id+"F6.imprint","IMPRINT",EDGE,{"derivedFrom":sQuery(id+"F6.wireOp",EDGE,"E387.MirrorC")}),-1.0]])]});
            var Q985;
            Q985=makeQuery(id+"F6.imprint","IMPRINT",FACE,{"disambiguationData":[TD([[makeQuery(id+"F6.imprint","IMPRINT",EDGE,{"derivedFrom":sQuery(id+"F6.wireOp",EDGE,"E43.18.0.8")}),1.0]])]});
            var Q986;
            Q986=makeQuery(id+"F6.imprint","IMPRINT",FACE,{"disambiguationData":[TD([[makeQuery(id+"F6.imprint","IMPRINT",EDGE,{"derivedFrom":sQuery(id+"F6.wireOp",EDGE,"E439.MirrorC")}),-1.0]])]});
            var Q987;
            Q987=makeQuery(id+"F6.imprint","IMPRINT",FACE,{"disambiguationData":[TD([[makeQuery(id+"F6.imprint","IMPRINT",EDGE,{"derivedFrom":sQuery(id+"F6.wireOp",EDGE,"E43.22.0.8")}),1.0]])]});
            var Q988;
            Q988=makeQuery(id+"F6.imprint","IMPRINT",FACE,{"disambiguationData":[TD([[makeQuery(id+"F6.imprint","IMPRINT",EDGE,{"derivedFrom":sQuery(id+"F6.wireOp",EDGE,"E43.21.0.17")}),1.0]])]});
            var Q989;
            Q989=makeQuery(id+"F6.imprint","IMPRINT",FACE,{"disambiguationData":[TD([[makeQuery(id+"F6.imprint","IMPRINT",EDGE,{"derivedFrom":sQuery(id+"F6.wireOp",EDGE,"E43.25.0.17")}),1.0]])]});
            var Q990;
            Q990=makeQuery(id+"F6.imprint","IMPRINT",FACE,{"disambiguationData":[TD([[makeQuery(id+"F6.imprint","IMPRINT",EDGE,{"derivedFrom":sQuery(id+"F6.wireOp",EDGE,"E43.24.0.8")}),1.0]])]});
            var Q991;
            Q991=makeQuery(id+"F6.imprint","IMPRINT",FACE,{"disambiguationData":[TD([[makeQuery(id+"F6.imprint","IMPRINT",EDGE,{"derivedFrom":sQuery(id+"F6.wireOp",EDGE,"E43.23.0.17")}),1.0]])]});
            var Q992;
            Q992=makeQuery(id+"F6.imprint","IMPRINT",FACE,{"disambiguationData":[TD([[makeQuery(id+"F6.imprint","IMPRINT",EDGE,{"derivedFrom":sQuery(id+"F6.wireOp",EDGE,"E43.28.0.8")}),1.0]])]});
            var Q993;
            Q993=makeQuery(id+"F6.imprint","IMPRINT",FACE,{"disambiguationData":[TD([[makeQuery(id+"F6.imprint","IMPRINT",EDGE,{"derivedFrom":sQuery(id+"F6.wireOp",EDGE,"E43.27.0.17")}),1.0]])]});
            var Q994;
            Q994=makeQuery(id+"F6.imprint","IMPRINT",FACE,{"disambiguationData":[TD([[makeQuery(id+"F6.imprint","IMPRINT",EDGE,{"derivedFrom":sQuery(id+"F6.wireOp",EDGE,"E371.MirrorC")}),-1.0]])]});
            var Q995;
            Q995=makeQuery(id+"F6.imprint","IMPRINT",FACE,{"disambiguationData":[TD([[makeQuery(id+"F6.imprint","IMPRINT",EDGE,{"derivedFrom":sQuery(id+"F6.wireOp",EDGE,"E43.26.0.8")}),1.0]])]});
            var Q996;
            Q996=makeQuery(id+"F6.imprint","IMPRINT",FACE,{"disambiguationData":[TD([[makeQuery(id+"F6.imprint","IMPRINT",EDGE,{"derivedFrom":sQuery(id+"F6.wireOp",EDGE,"E838.MirrorC")}),-1.0]])]});
            var Q997;
            Q997=makeQuery(id+"F6.imprint","IMPRINT",FACE,{"disambiguationData":[TD([[makeQuery(id+"F6.imprint","IMPRINT",EDGE,{"derivedFrom":sQuery(id+"F6.wireOp",EDGE,"E43.30.0.8")}),1.0]])]});
            var Q998;
            Q998=makeQuery(id+"F6.imprint","IMPRINT",FACE,{"disambiguationData":[TD([[makeQuery(id+"F6.imprint","IMPRINT",EDGE,{"derivedFrom":sQuery(id+"F6.wireOp",EDGE,"E787.MirrorC")}),-1.0]])]});
            var Q999;
            Q999=makeQuery(id+"F6.imprint","IMPRINT",FACE,{"disambiguationData":[TD([[makeQuery(id+"F6.imprint","IMPRINT",EDGE,{"derivedFrom":sQuery(id+"F6.wireOp",EDGE,"E43.29.0.17")}),1.0]])]});
            var Q1000;
            Q1000=makeQuery(id+"F6.imprint","IMPRINT",FACE,{"disambiguationData":[TD([[makeQuery(id+"F6.imprint","IMPRINT",EDGE,{"derivedFrom":sQuery(id+"F6.wireOp",EDGE,"E43.32.0.8")}),1.0]])]});
            var Q1001;
            Q1001=makeQuery(id+"F6.imprint","IMPRINT",FACE,{"disambiguationData":[TD([[makeQuery(id+"F6.imprint","IMPRINT",EDGE,{"derivedFrom":sQuery(id+"F6.wireOp",EDGE,"E43.31.0.17")}),1.0]])]});
            var Q1002;
            Q1002=makeQuery(id+"F6.imprint","IMPRINT",FACE,{"disambiguationData":[TD([[makeQuery(id+"F6.imprint","IMPRINT",EDGE,{"derivedFrom":sQuery(id+"F6.wireOp",EDGE,"E43.2.0.9")}),1.0]])]});
            var Q1003;
            Q1003=makeQuery(id+"F6.imprint","IMPRINT",FACE,{"disambiguationData":[TD([[makeQuery(id+"F6.imprint","IMPRINT",EDGE,{"derivedFrom":sQuery(id+"F6.wireOp",EDGE,"E43.1.0.18")}),1.0]])]});
            var Q1004;
            Q1004=makeQuery(id+"F6.imprint","IMPRINT",FACE,{"disambiguationData":[TD([[makeQuery(id+"F6.imprint","IMPRINT",EDGE,{"derivedFrom":sQuery(id+"F6.wireOp",EDGE,"E42.0.11.0")}),1.0]])]});
            var Q1005;
            Q1005=makeQuery(id+"F6.imprint","IMPRINT",FACE,{"disambiguationData":[TD([[makeQuery(id+"F6.imprint","IMPRINT",EDGE,{"derivedFrom":sQuery(id+"F6.wireOp",EDGE,"E43.5.0.18")}),1.0]])]});
            var Q1006;
            Q1006=makeQuery(id+"F6.imprint","IMPRINT",FACE,{"disambiguationData":[TD([[makeQuery(id+"F6.imprint","IMPRINT",EDGE,{"derivedFrom":sQuery(id+"F6.wireOp",EDGE,"E43.4.0.9")}),1.0]])]});
            var Q1007;
            Q1007=makeQuery(id+"F6.imprint","IMPRINT",FACE,{"disambiguationData":[TD([[makeQuery(id+"F6.imprint","IMPRINT",EDGE,{"derivedFrom":sQuery(id+"F6.wireOp",EDGE,"E43.3.0.18")}),1.0]])]});
            var Q1008;
            Q1008=makeQuery(id+"F6.imprint","IMPRINT",FACE,{"disambiguationData":[TD([[makeQuery(id+"F6.imprint","IMPRINT",EDGE,{"derivedFrom":sQuery(id+"F6.wireOp",EDGE,"E43.8.0.9")}),1.0]])]});
            var Q1009;
            Q1009=makeQuery(id+"F6.imprint","IMPRINT",FACE,{"disambiguationData":[TD([[makeQuery(id+"F6.imprint","IMPRINT",EDGE,{"derivedFrom":sQuery(id+"F6.wireOp",EDGE,"E43.7.0.18")}),1.0]])]});
            var Q1010;
            Q1010=makeQuery(id+"F6.imprint","IMPRINT",FACE,{"disambiguationData":[TD([[makeQuery(id+"F6.imprint","IMPRINT",EDGE,{"derivedFrom":sQuery(id+"F6.wireOp",EDGE,"E43.6.0.9")}),1.0]])]});
            var Q1011;
            Q1011=makeQuery(id+"F6.imprint","IMPRINT",FACE,{"disambiguationData":[TD([[makeQuery(id+"F6.imprint","IMPRINT",EDGE,{"derivedFrom":sQuery(id+"F6.wireOp",EDGE,"E43.10.0.9")}),1.0]])]});
            var Q1012;
            Q1012=makeQuery(id+"F6.imprint","IMPRINT",FACE,{"disambiguationData":[TD([[makeQuery(id+"F6.imprint","IMPRINT",EDGE,{"derivedFrom":sQuery(id+"F6.wireOp",EDGE,"E43.9.0.18")}),1.0]])]});
            var Q1013;
            Q1013=makeQuery(id+"F6.imprint","IMPRINT",FACE,{"disambiguationData":[TD([[makeQuery(id+"F6.imprint","IMPRINT",EDGE,{"derivedFrom":sQuery(id+"F6.wireOp",EDGE,"E43.13.0.18")}),1.0]])]});
            var Q1014;
            Q1014=makeQuery(id+"F6.imprint","IMPRINT",FACE,{"disambiguationData":[TD([[makeQuery(id+"F6.imprint","IMPRINT",EDGE,{"derivedFrom":sQuery(id+"F6.wireOp",EDGE,"E43.12.0.9")}),1.0]])]});
            var Q1015;
            Q1015=makeQuery(id+"F6.imprint","IMPRINT",FACE,{"disambiguationData":[TD([[makeQuery(id+"F6.imprint","IMPRINT",EDGE,{"derivedFrom":sQuery(id+"F6.wireOp",EDGE,"E43.11.0.18")}),1.0]])]});
            var Q1016;
            Q1016=makeQuery(id+"F6.imprint","IMPRINT",FACE,{"disambiguationData":[TD([[makeQuery(id+"F6.imprint","IMPRINT",EDGE,{"derivedFrom":sQuery(id+"F6.wireOp",EDGE,"E43.16.0.9")}),1.0]])]});
            var Q1017;
            Q1017=makeQuery(id+"F6.imprint","IMPRINT",FACE,{"disambiguationData":[TD([[makeQuery(id+"F6.imprint","IMPRINT",EDGE,{"derivedFrom":sQuery(id+"F6.wireOp",EDGE,"E43.15.0.18")}),1.0]])]});
            var Q1018;
            Q1018=makeQuery(id+"F6.imprint","IMPRINT",FACE,{"disambiguationData":[TD([[makeQuery(id+"F6.imprint","IMPRINT",EDGE,{"derivedFrom":sQuery(id+"F6.wireOp",EDGE,"E43.14.0.9")}),1.0]])]});
            var Q1019;
            Q1019=makeQuery(id+"F6.imprint","IMPRINT",FACE,{"disambiguationData":[TD([[makeQuery(id+"F6.imprint","IMPRINT",EDGE,{"derivedFrom":sQuery(id+"F6.wireOp",EDGE,"E317.MirrorC")}),-1.0]])]});
            var Q1020;
            Q1020=makeQuery(id+"F6.imprint","IMPRINT",FACE,{"disambiguationData":[TD([[makeQuery(id+"F6.imprint","IMPRINT",EDGE,{"derivedFrom":sQuery(id+"F6.wireOp",EDGE,"E332.MirrorC")}),-1.0]])]});
            var Q1021;
            Q1021=makeQuery(id+"F6.imprint","IMPRINT",FACE,{"disambiguationData":[TD([[makeQuery(id+"F6.imprint","IMPRINT",EDGE,{"derivedFrom":sQuery(id+"F6.wireOp",EDGE,"E301.MirrorC")}),-1.0]])]});
            var Q1022;
            Q1022=makeQuery(id+"F6.imprint","IMPRINT",FACE,{"disambiguationData":[TD([[makeQuery(id+"F6.imprint","IMPRINT",EDGE,{"derivedFrom":sQuery(id+"F6.wireOp",EDGE,"E285.MirrorC")}),-1.0]])]});
            var Q1023;
            Q1023=makeQuery(id+"F6.imprint","IMPRINT",FACE,{"disambiguationData":[TD([[makeQuery(id+"F6.imprint","IMPRINT",EDGE,{"derivedFrom":sQuery(id+"F6.wireOp",EDGE,"E269.MirrorC")}),-1.0]])]});
            var Q1024;
            Q1024=makeQuery(id+"F6.imprint","IMPRINT",FACE,{"disambiguationData":[TD([[makeQuery(id+"F6.imprint","IMPRINT",EDGE,{"derivedFrom":sQuery(id+"F6.wireOp",EDGE,"E255.MirrorC")}),-1.0]])]});
            var Q1025;
            Q1025=makeQuery(id+"F6.imprint","IMPRINT",FACE,{"disambiguationData":[TD([[makeQuery(id+"F6.imprint","IMPRINT",EDGE,{"derivedFrom":sQuery(id+"F6.wireOp",EDGE,"E43.17.0.18")}),1.0]])]});
            var Q1026;
            Q1026=makeQuery(id+"F6.imprint","IMPRINT",FACE,{"disambiguationData":[TD([[makeQuery(id+"F6.imprint","IMPRINT",EDGE,{"derivedFrom":sQuery(id+"F6.wireOp",EDGE,"E43.20.0.9")}),1.0]])]});
            var Q1027;
            Q1027=makeQuery(id+"F6.imprint","IMPRINT",FACE,{"disambiguationData":[TD([[makeQuery(id+"F6.imprint","IMPRINT",EDGE,{"derivedFrom":sQuery(id+"F6.wireOp",EDGE,"E43.19.0.18")}),1.0]])]});
            var Q1028;
            Q1028=makeQuery(id+"F6.imprint","IMPRINT",FACE,{"disambiguationData":[TD([[makeQuery(id+"F6.imprint","IMPRINT",EDGE,{"derivedFrom":sQuery(id+"F6.wireOp",EDGE,"E43.18.0.9")}),1.0]])]});
            var Q1029;
            Q1029=makeQuery(id+"F6.imprint","IMPRINT",FACE,{"disambiguationData":[TD([[makeQuery(id+"F6.imprint","IMPRINT",EDGE,{"derivedFrom":sQuery(id+"F6.wireOp",EDGE,"E43.22.0.9")}),1.0]])]});
            var Q1030;
            Q1030=makeQuery(id+"F6.imprint","IMPRINT",FACE,{"disambiguationData":[TD([[makeQuery(id+"F6.imprint","IMPRINT",EDGE,{"derivedFrom":sQuery(id+"F6.wireOp",EDGE,"E43.21.0.18")}),1.0]])]});
            var Q1031;
            Q1031=makeQuery(id+"F6.imprint","IMPRINT",FACE,{"disambiguationData":[TD([[makeQuery(id+"F6.imprint","IMPRINT",EDGE,{"derivedFrom":sQuery(id+"F6.wireOp",EDGE,"E43.25.0.18")}),1.0]])]});
            var Q1032;
            Q1032=makeQuery(id+"F6.imprint","IMPRINT",FACE,{"disambiguationData":[TD([[makeQuery(id+"F6.imprint","IMPRINT",EDGE,{"derivedFrom":sQuery(id+"F6.wireOp",EDGE,"E43.24.0.9")}),1.0]])]});
            var Q1033;
            Q1033=makeQuery(id+"F6.imprint","IMPRINT",FACE,{"disambiguationData":[TD([[makeQuery(id+"F6.imprint","IMPRINT",EDGE,{"derivedFrom":sQuery(id+"F6.wireOp",EDGE,"E43.23.0.18")}),1.0]])]});
            var Q1034;
            Q1034=makeQuery(id+"F6.imprint","IMPRINT",FACE,{"disambiguationData":[TD([[makeQuery(id+"F6.imprint","IMPRINT",EDGE,{"derivedFrom":sQuery(id+"F6.wireOp",EDGE,"E43.28.0.9")}),1.0]])]});
            var Q1035;
            Q1035=makeQuery(id+"F6.imprint","IMPRINT",FACE,{"disambiguationData":[TD([[makeQuery(id+"F6.imprint","IMPRINT",EDGE,{"derivedFrom":sQuery(id+"F6.wireOp",EDGE,"E43.27.0.18")}),1.0]])]});
            var Q1036;
            Q1036=makeQuery(id+"F6.imprint","IMPRINT",FACE,{"disambiguationData":[TD([[makeQuery(id+"F6.imprint","IMPRINT",EDGE,{"derivedFrom":sQuery(id+"F6.wireOp",EDGE,"E43.26.0.9")}),1.0]])]});
            var Q1037;
            Q1037=makeQuery(id+"F6.imprint","IMPRINT",FACE,{"disambiguationData":[TD([[makeQuery(id+"F6.imprint","IMPRINT",EDGE,{"derivedFrom":sQuery(id+"F6.wireOp",EDGE,"E43.30.0.9")}),1.0]])]});
            var Q1038;
            Q1038=makeQuery(id+"F6.imprint","IMPRINT",FACE,{"disambiguationData":[TD([[makeQuery(id+"F6.imprint","IMPRINT",EDGE,{"derivedFrom":sQuery(id+"F6.wireOp",EDGE,"E43.29.0.18")}),1.0]])]});
            var Q1039;
            Q1039=makeQuery(id+"F6.imprint","IMPRINT",FACE,{"disambiguationData":[TD([[makeQuery(id+"F6.imprint","IMPRINT",EDGE,{"derivedFrom":sQuery(id+"F6.wireOp",EDGE,"E43.32.0.9")}),1.0]])]});
            var Q1040;
            Q1040=makeQuery(id+"F6.imprint","IMPRINT",FACE,{"disambiguationData":[TD([[makeQuery(id+"F6.imprint","IMPRINT",EDGE,{"derivedFrom":sQuery(id+"F6.wireOp",EDGE,"E43.31.0.18")}),1.0]])]});
            var Q1041;
            Q1041=makeQuery(id+"F6.imprint","IMPRINT",FACE,{"disambiguationData":[TD([[makeQuery(id+"F6.imprint","IMPRINT",EDGE,{"derivedFrom":sQuery(id+"F6.wireOp",EDGE,"E43.3.0.1")}),1.0]])]});
            var Q1042;
            Q1042=makeQuery(id+"F6.imprint","IMPRINT",FACE,{"disambiguationData":[TD([[makeQuery(id+"F6.imprint","IMPRINT",EDGE,{"derivedFrom":sQuery(id+"F6.wireOp",EDGE,"E43.2.0.10")}),1.0]])]});
            var Q1043;
            Q1043=makeQuery(id+"F6.imprint","IMPRINT",FACE,{"disambiguationData":[TD([[makeQuery(id+"F6.imprint","IMPRINT",EDGE,{"derivedFrom":sQuery(id+"F6.wireOp",EDGE,"E43.1.0.19")}),1.0]])]});
            var Q1044;
            Q1044=makeQuery(id+"F6.imprint","IMPRINT",FACE,{"disambiguationData":[TD([[makeQuery(id+"F6.imprint","IMPRINT",EDGE,{"derivedFrom":sQuery(id+"F6.wireOp",EDGE,"E43.1.0.1")}),1.0]])]});
            var Q1045;
            Q1045=makeQuery(id+"F6.imprint","IMPRINT",FACE,{"disambiguationData":[TD([[makeQuery(id+"F6.imprint","IMPRINT",EDGE,{"derivedFrom":sQuery(id+"F6.wireOp",EDGE,"E43.5.0.19")}),1.0]])]});
            var Q1046;
            Q1046=makeQuery(id+"F6.imprint","IMPRINT",FACE,{"disambiguationData":[TD([[makeQuery(id+"F6.imprint","IMPRINT",EDGE,{"derivedFrom":sQuery(id+"F6.wireOp",EDGE,"E43.5.0.1")}),1.0]])]});
            var Q1047;
            Q1047=makeQuery(id+"F6.imprint","IMPRINT",FACE,{"disambiguationData":[TD([[makeQuery(id+"F6.imprint","IMPRINT",EDGE,{"derivedFrom":sQuery(id+"F6.wireOp",EDGE,"E43.4.0.10")}),1.0]])]});
            var Q1048;
            Q1048=makeQuery(id+"F6.imprint","IMPRINT",FACE,{"disambiguationData":[TD([[makeQuery(id+"F6.imprint","IMPRINT",EDGE,{"derivedFrom":sQuery(id+"F6.wireOp",EDGE,"E43.3.0.19")}),1.0]])]});
            var Q1049;
            Q1049=makeQuery(id+"F6.imprint","IMPRINT",FACE,{"disambiguationData":[TD([[makeQuery(id+"F6.imprint","IMPRINT",EDGE,{"derivedFrom":sQuery(id+"F6.wireOp",EDGE,"E43.8.0.10")}),1.0]])]});
            var Q1050;
            Q1050=makeQuery(id+"F6.imprint","IMPRINT",FACE,{"disambiguationData":[TD([[makeQuery(id+"F6.imprint","IMPRINT",EDGE,{"derivedFrom":sQuery(id+"F6.wireOp",EDGE,"E43.7.0.19")}),1.0]])]});
            var Q1051;
            Q1051=makeQuery(id+"F6.imprint","IMPRINT",FACE,{"disambiguationData":[TD([[makeQuery(id+"F6.imprint","IMPRINT",EDGE,{"derivedFrom":sQuery(id+"F6.wireOp",EDGE,"E43.7.0.1")}),1.0]])]});
            var Q1052;
            Q1052=makeQuery(id+"F6.imprint","IMPRINT",FACE,{"disambiguationData":[TD([[makeQuery(id+"F6.imprint","IMPRINT",EDGE,{"derivedFrom":sQuery(id+"F6.wireOp",EDGE,"E43.6.0.10")}),1.0]])]});
            var Q1053;
            Q1053=makeQuery(id+"F6.imprint","IMPRINT",FACE,{"disambiguationData":[TD([[makeQuery(id+"F6.imprint","IMPRINT",EDGE,{"derivedFrom":sQuery(id+"F6.wireOp",EDGE,"E43.11.0.1")}),1.0]])]});
            var Q1054;
            Q1054=makeQuery(id+"F6.imprint","IMPRINT",FACE,{"disambiguationData":[TD([[makeQuery(id+"F6.imprint","IMPRINT",EDGE,{"derivedFrom":sQuery(id+"F6.wireOp",EDGE,"E43.10.0.10")}),1.0]])]});
            var Q1055;
            Q1055=makeQuery(id+"F6.imprint","IMPRINT",FACE,{"disambiguationData":[TD([[makeQuery(id+"F6.imprint","IMPRINT",EDGE,{"derivedFrom":sQuery(id+"F6.wireOp",EDGE,"E43.9.0.19")}),1.0]])]});
            var Q1056;
            Q1056=makeQuery(id+"F6.imprint","IMPRINT",FACE,{"disambiguationData":[TD([[makeQuery(id+"F6.imprint","IMPRINT",EDGE,{"derivedFrom":sQuery(id+"F6.wireOp",EDGE,"E43.9.0.1")}),1.0]])]});
            var Q1057;
            Q1057=makeQuery(id+"F6.imprint","IMPRINT",FACE,{"disambiguationData":[TD([[makeQuery(id+"F6.imprint","IMPRINT",EDGE,{"derivedFrom":sQuery(id+"F6.wireOp",EDGE,"E43.13.0.19")}),1.0]])]});
            var Q1058;
            Q1058=makeQuery(id+"F6.imprint","IMPRINT",FACE,{"disambiguationData":[TD([[makeQuery(id+"F6.imprint","IMPRINT",EDGE,{"derivedFrom":sQuery(id+"F6.wireOp",EDGE,"E43.13.0.1")}),1.0]])]});
            var Q1059;
            Q1059=makeQuery(id+"F6.imprint","IMPRINT",FACE,{"disambiguationData":[TD([[makeQuery(id+"F6.imprint","IMPRINT",EDGE,{"derivedFrom":sQuery(id+"F6.wireOp",EDGE,"E43.12.0.10")}),1.0]])]});
            var Q1060;
            Q1060=makeQuery(id+"F6.imprint","IMPRINT",FACE,{"disambiguationData":[TD([[makeQuery(id+"F6.imprint","IMPRINT",EDGE,{"derivedFrom":sQuery(id+"F6.wireOp",EDGE,"E43.11.0.19")}),1.0]])]});
            var Q1061;
            Q1061=makeQuery(id+"F6.imprint","IMPRINT",FACE,{"disambiguationData":[TD([[makeQuery(id+"F6.imprint","IMPRINT",EDGE,{"derivedFrom":sQuery(id+"F6.wireOp",EDGE,"E43.16.0.10")}),1.0]])]});
            var Q1062;
            Q1062=makeQuery(id+"F6.imprint","IMPRINT",FACE,{"disambiguationData":[TD([[makeQuery(id+"F6.imprint","IMPRINT",EDGE,{"derivedFrom":sQuery(id+"F6.wireOp",EDGE,"E43.15.0.19")}),1.0]])]});
            var Q1063;
            Q1063=makeQuery(id+"F6.imprint","IMPRINT",FACE,{"disambiguationData":[TD([[makeQuery(id+"F6.imprint","IMPRINT",EDGE,{"derivedFrom":sQuery(id+"F6.wireOp",EDGE,"E43.15.0.1")}),1.0]])]});
            var Q1064;
            Q1064=makeQuery(id+"F6.imprint","IMPRINT",FACE,{"disambiguationData":[TD([[makeQuery(id+"F6.imprint","IMPRINT",EDGE,{"derivedFrom":sQuery(id+"F6.wireOp",EDGE,"E43.14.0.10")}),1.0]])]});
            var Q1065;
            Q1065=makeQuery(id+"F6.imprint","IMPRINT",FACE,{"disambiguationData":[TD([[makeQuery(id+"F6.imprint","IMPRINT",EDGE,{"derivedFrom":sQuery(id+"F6.wireOp",EDGE,"E43.17.0.1")}),1.0]])]});
            var Q1066;
            Q1066=makeQuery(id+"F6.imprint","IMPRINT",FACE,{"disambiguationData":[TD([[makeQuery(id+"F6.imprint","IMPRINT",EDGE,{"derivedFrom":sQuery(id+"F6.wireOp",EDGE,"E43.17.0.19")}),1.0]])]});
            var Q1067;
            Q1067=makeQuery(id+"F6.imprint","IMPRINT",FACE,{"disambiguationData":[TD([[makeQuery(id+"F6.imprint","IMPRINT",EDGE,{"derivedFrom":sQuery(id+"F6.wireOp",EDGE,"E318.MirrorC")}),-1.0]])]});
            var Q1068;
            Q1068=makeQuery(id+"F6.imprint","IMPRINT",FACE,{"disambiguationData":[TD([[makeQuery(id+"F6.imprint","IMPRINT",EDGE,{"derivedFrom":sQuery(id+"F6.wireOp",EDGE,"E333.MirrorC")}),-1.0]])]});
            var Q1069;
            Q1069=makeQuery(id+"F6.imprint","IMPRINT",FACE,{"disambiguationData":[TD([[makeQuery(id+"F6.imprint","IMPRINT",EDGE,{"derivedFrom":sQuery(id+"F6.wireOp",EDGE,"E302.MirrorC")}),-1.0]])]});
            var Q1070;
            Q1070=makeQuery(id+"F6.imprint","IMPRINT",FACE,{"disambiguationData":[TD([[makeQuery(id+"F6.imprint","IMPRINT",EDGE,{"derivedFrom":sQuery(id+"F6.wireOp",EDGE,"E286.MirrorC")}),-1.0]])]});
            var Q1071;
            Q1071=makeQuery(id+"F6.imprint","IMPRINT",FACE,{"disambiguationData":[TD([[makeQuery(id+"F6.imprint","IMPRINT",EDGE,{"derivedFrom":sQuery(id+"F6.wireOp",EDGE,"E270.MirrorC")}),-1.0]])]});
            var Q1072;
            Q1072=makeQuery(id+"F6.imprint","IMPRINT",FACE,{"disambiguationData":[TD([[makeQuery(id+"F6.imprint","IMPRINT",EDGE,{"derivedFrom":sQuery(id+"F6.wireOp",EDGE,"E256.MirrorC")}),-1.0]])]});
            var Q1073;
            Q1073=makeQuery(id+"F6.imprint","IMPRINT",FACE,{"disambiguationData":[TD([[makeQuery(id+"F6.imprint","IMPRINT",EDGE,{"derivedFrom":sQuery(id+"F6.wireOp",EDGE,"E43.20.0.10")}),1.0]])]});
            var Q1074;
            Q1074=makeQuery(id+"F6.imprint","IMPRINT",FACE,{"disambiguationData":[TD([[makeQuery(id+"F6.imprint","IMPRINT",EDGE,{"derivedFrom":sQuery(id+"F6.wireOp",EDGE,"E43.19.0.19")}),1.0]])]});
            var Q1075;
            Q1075=makeQuery(id+"F6.imprint","IMPRINT",FACE,{"disambiguationData":[TD([[makeQuery(id+"F6.imprint","IMPRINT",EDGE,{"derivedFrom":sQuery(id+"F6.wireOp",EDGE,"E43.19.0.1")}),1.0]])]});
            var Q1076;
            Q1076=makeQuery(id+"F6.imprint","IMPRINT",FACE,{"disambiguationData":[TD([[makeQuery(id+"F6.imprint","IMPRINT",EDGE,{"derivedFrom":sQuery(id+"F6.wireOp",EDGE,"E43.18.0.10")}),1.0]])]});
            var Q1077;
            Q1077=makeQuery(id+"F6.imprint","IMPRINT",FACE,{"disambiguationData":[TD([[makeQuery(id+"F6.imprint","IMPRINT",EDGE,{"derivedFrom":sQuery(id+"F6.wireOp",EDGE,"E43.23.0.1")}),1.0]])]});
            var Q1078;
            Q1078=makeQuery(id+"F6.imprint","IMPRINT",FACE,{"disambiguationData":[TD([[makeQuery(id+"F6.imprint","IMPRINT",EDGE,{"derivedFrom":sQuery(id+"F6.wireOp",EDGE,"E43.22.0.10")}),1.0]])]});
            var Q1079;
            Q1079=makeQuery(id+"F6.imprint","IMPRINT",FACE,{"disambiguationData":[TD([[makeQuery(id+"F6.imprint","IMPRINT",EDGE,{"derivedFrom":sQuery(id+"F6.wireOp",EDGE,"E43.21.0.19")}),1.0]])]});
            var Q1080;
            Q1080=makeQuery(id+"F6.imprint","IMPRINT",FACE,{"disambiguationData":[TD([[makeQuery(id+"F6.imprint","IMPRINT",EDGE,{"derivedFrom":sQuery(id+"F6.wireOp",EDGE,"E43.21.0.1")}),1.0]])]});
            var Q1081;
            Q1081=makeQuery(id+"F6.imprint","IMPRINT",FACE,{"disambiguationData":[TD([[makeQuery(id+"F6.imprint","IMPRINT",EDGE,{"derivedFrom":sQuery(id+"F6.wireOp",EDGE,"E43.25.0.19")}),1.0]])]});
            var Q1082;
            Q1082=makeQuery(id+"F6.imprint","IMPRINT",FACE,{"disambiguationData":[TD([[makeQuery(id+"F6.imprint","IMPRINT",EDGE,{"derivedFrom":sQuery(id+"F6.wireOp",EDGE,"E43.25.0.1")}),1.0]])]});
            var Q1083;
            Q1083=makeQuery(id+"F6.imprint","IMPRINT",FACE,{"disambiguationData":[TD([[makeQuery(id+"F6.imprint","IMPRINT",EDGE,{"derivedFrom":sQuery(id+"F6.wireOp",EDGE,"E43.24.0.10")}),1.0]])]});
            var Q1084;
            Q1084=makeQuery(id+"F6.imprint","IMPRINT",FACE,{"disambiguationData":[TD([[makeQuery(id+"F6.imprint","IMPRINT",EDGE,{"derivedFrom":sQuery(id+"F6.wireOp",EDGE,"E43.23.0.19")}),1.0]])]});
            var Q1085;
            Q1085=makeQuery(id+"F6.imprint","IMPRINT",FACE,{"disambiguationData":[TD([[makeQuery(id+"F6.imprint","IMPRINT",EDGE,{"derivedFrom":sQuery(id+"F6.wireOp",EDGE,"E43.28.0.10")}),1.0]])]});
            var Q1086;
            Q1086=makeQuery(id+"F6.imprint","IMPRINT",FACE,{"disambiguationData":[TD([[makeQuery(id+"F6.imprint","IMPRINT",EDGE,{"derivedFrom":sQuery(id+"F6.wireOp",EDGE,"E43.27.0.19")}),1.0]])]});
            var Q1087;
            Q1087=makeQuery(id+"F6.imprint","IMPRINT",FACE,{"disambiguationData":[TD([[makeQuery(id+"F6.imprint","IMPRINT",EDGE,{"derivedFrom":sQuery(id+"F6.wireOp",EDGE,"E43.27.0.1")}),1.0]])]});
            var Q1088;
            Q1088=makeQuery(id+"F6.imprint","IMPRINT",FACE,{"disambiguationData":[TD([[makeQuery(id+"F6.imprint","IMPRINT",EDGE,{"derivedFrom":sQuery(id+"F6.wireOp",EDGE,"E43.26.0.10")}),1.0]])]});
            var Q1089;
            Q1089=makeQuery(id+"F6.imprint","IMPRINT",FACE,{"disambiguationData":[TD([[makeQuery(id+"F6.imprint","IMPRINT",EDGE,{"derivedFrom":sQuery(id+"F6.wireOp",EDGE,"E43.31.0.1")}),1.0]])]});
            var Q1090;
            Q1090=makeQuery(id+"F6.imprint","IMPRINT",FACE,{"disambiguationData":[TD([[makeQuery(id+"F6.imprint","IMPRINT",EDGE,{"derivedFrom":sQuery(id+"F6.wireOp",EDGE,"E43.30.0.10")}),1.0]])]});
            var Q1091;
            Q1091=makeQuery(id+"F6.imprint","IMPRINT",FACE,{"disambiguationData":[TD([[makeQuery(id+"F6.imprint","IMPRINT",EDGE,{"derivedFrom":sQuery(id+"F6.wireOp",EDGE,"E43.29.0.19")}),1.0]])]});
            var Q1092;
            Q1092=makeQuery(id+"F6.imprint","IMPRINT",FACE,{"disambiguationData":[TD([[makeQuery(id+"F6.imprint","IMPRINT",EDGE,{"derivedFrom":sQuery(id+"F6.wireOp",EDGE,"E43.29.0.1")}),1.0]])]});
            var Q1093;
            Q1093=makeQuery(id+"F6.imprint","IMPRINT",FACE,{"disambiguationData":[TD([[makeQuery(id+"F6.imprint","IMPRINT",EDGE,{"derivedFrom":sQuery(id+"F6.wireOp",EDGE,"E43.32.0.10")}),1.0]])]});
            var Q1094;
            Q1094=makeQuery(id+"F6.imprint","IMPRINT",FACE,{"disambiguationData":[TD([[makeQuery(id+"F6.imprint","IMPRINT",EDGE,{"derivedFrom":sQuery(id+"F6.wireOp",EDGE,"E43.31.0.19")}),1.0]])]});
            var Q1095;
            Q1095=makeQuery(id+"F6.imprint","IMPRINT",FACE,{"disambiguationData":[TD([[makeQuery(id+"F6.imprint","IMPRINT",EDGE,{"derivedFrom":sQuery(id+"F6.wireOp",EDGE,"E43.5.0.20")}),1.0]])]});
            var Q1096;
            Q1096=makeQuery(id+"F6.imprint","IMPRINT",FACE,{"disambiguationData":[TD([[makeQuery(id+"F6.imprint","IMPRINT",EDGE,{"derivedFrom":sQuery(id+"F6.wireOp",EDGE,"E43.5.0.2")}),1.0]])]});
            var Q1097;
            Q1097=makeQuery(id+"F6.imprint","IMPRINT",FACE,{"disambiguationData":[TD([[makeQuery(id+"F6.imprint","IMPRINT",EDGE,{"derivedFrom":sQuery(id+"F6.wireOp",EDGE,"E43.4.0.12")}),1.0]])]});
            var Q1098;
            Q1098=makeQuery(id+"F6.imprint","IMPRINT",FACE,{"disambiguationData":[TD([[makeQuery(id+"F6.imprint","IMPRINT",EDGE,{"derivedFrom":sQuery(id+"F6.wireOp",EDGE,"E43.3.0.20")}),1.0]])]});
            var Q1099;
            Q1099=makeQuery(id+"F6.imprint","IMPRINT",FACE,{"disambiguationData":[TD([[makeQuery(id+"F6.imprint","IMPRINT",EDGE,{"derivedFrom":sQuery(id+"F6.wireOp",EDGE,"E43.8.0.12")}),1.0]])]});
            var Q1100;
            Q1100=makeQuery(id+"F6.imprint","IMPRINT",FACE,{"disambiguationData":[TD([[makeQuery(id+"F6.imprint","IMPRINT",EDGE,{"derivedFrom":sQuery(id+"F6.wireOp",EDGE,"E43.7.0.20")}),1.0]])]});
            var Q1101;
            Q1101=makeQuery(id+"F6.imprint","IMPRINT",FACE,{"disambiguationData":[TD([[makeQuery(id+"F6.imprint","IMPRINT",EDGE,{"derivedFrom":sQuery(id+"F6.wireOp",EDGE,"E43.7.0.2")}),1.0]])]});
            var Q1102;
            Q1102=makeQuery(id+"F6.imprint","IMPRINT",FACE,{"disambiguationData":[TD([[makeQuery(id+"F6.imprint","IMPRINT",EDGE,{"derivedFrom":sQuery(id+"F6.wireOp",EDGE,"E43.6.0.12")}),1.0]])]});
            var Q1103;
            Q1103=makeQuery(id+"F6.imprint","IMPRINT",FACE,{"disambiguationData":[TD([[makeQuery(id+"F6.imprint","IMPRINT",EDGE,{"derivedFrom":sQuery(id+"F6.wireOp",EDGE,"E43.11.0.2")}),1.0]])]});
            var Q1104;
            Q1104=makeQuery(id+"F6.imprint","IMPRINT",FACE,{"disambiguationData":[TD([[makeQuery(id+"F6.imprint","IMPRINT",EDGE,{"derivedFrom":sQuery(id+"F6.wireOp",EDGE,"E43.10.0.12")}),1.0]])]});
            var Q1105;
            Q1105=makeQuery(id+"F6.imprint","IMPRINT",FACE,{"disambiguationData":[TD([[makeQuery(id+"F6.imprint","IMPRINT",EDGE,{"derivedFrom":sQuery(id+"F6.wireOp",EDGE,"E43.9.0.20")}),1.0]])]});
            var Q1106;
            Q1106=makeQuery(id+"F6.imprint","IMPRINT",FACE,{"disambiguationData":[TD([[makeQuery(id+"F6.imprint","IMPRINT",EDGE,{"derivedFrom":sQuery(id+"F6.wireOp",EDGE,"E43.9.0.2")}),1.0]])]});
            var Q1107;
            Q1107=makeQuery(id+"F6.imprint","IMPRINT",FACE,{"disambiguationData":[TD([[makeQuery(id+"F6.imprint","IMPRINT",EDGE,{"derivedFrom":sQuery(id+"F6.wireOp",EDGE,"E43.13.0.20")}),1.0]])]});
            var Q1108;
            Q1108=makeQuery(id+"F6.imprint","IMPRINT",FACE,{"disambiguationData":[TD([[makeQuery(id+"F6.imprint","IMPRINT",EDGE,{"derivedFrom":sQuery(id+"F6.wireOp",EDGE,"E43.13.0.2")}),1.0]])]});
            var Q1109;
            Q1109=makeQuery(id+"F6.imprint","IMPRINT",FACE,{"disambiguationData":[TD([[makeQuery(id+"F6.imprint","IMPRINT",EDGE,{"derivedFrom":sQuery(id+"F6.wireOp",EDGE,"E43.12.0.12")}),1.0]])]});
            var Q1110;
            Q1110=makeQuery(id+"F6.imprint","IMPRINT",FACE,{"disambiguationData":[TD([[makeQuery(id+"F6.imprint","IMPRINT",EDGE,{"derivedFrom":sQuery(id+"F6.wireOp",EDGE,"E43.11.0.20")}),1.0]])]});
            var Q1111;
            Q1111=makeQuery(id+"F6.imprint","IMPRINT",FACE,{"disambiguationData":[TD([[makeQuery(id+"F6.imprint","IMPRINT",EDGE,{"derivedFrom":sQuery(id+"F6.wireOp",EDGE,"E43.16.0.12")}),1.0]])]});
            var Q1112;
            Q1112=makeQuery(id+"F6.imprint","IMPRINT",FACE,{"disambiguationData":[TD([[makeQuery(id+"F6.imprint","IMPRINT",EDGE,{"derivedFrom":sQuery(id+"F6.wireOp",EDGE,"E43.15.0.20")}),1.0]])]});
            var Q1113;
            Q1113=makeQuery(id+"F6.imprint","IMPRINT",FACE,{"disambiguationData":[TD([[makeQuery(id+"F6.imprint","IMPRINT",EDGE,{"derivedFrom":sQuery(id+"F6.wireOp",EDGE,"E43.15.0.2")}),1.0]])]});
            var Q1114;
            Q1114=makeQuery(id+"F6.imprint","IMPRINT",FACE,{"disambiguationData":[TD([[makeQuery(id+"F6.imprint","IMPRINT",EDGE,{"derivedFrom":sQuery(id+"F6.wireOp",EDGE,"E43.14.0.12")}),1.0]])]});
            var Q1115;
            Q1115=makeQuery(id+"F6.imprint","IMPRINT",FACE,{"disambiguationData":[TD([[makeQuery(id+"F6.imprint","IMPRINT",EDGE,{"derivedFrom":sQuery(id+"F6.wireOp",EDGE,"E43.17.0.2")}),1.0]])]});
            var Q1116;
            Q1116=makeQuery(id+"F6.imprint","IMPRINT",FACE,{"disambiguationData":[TD([[makeQuery(id+"F6.imprint","IMPRINT",EDGE,{"derivedFrom":sQuery(id+"F6.wireOp",EDGE,"E43.17.0.20")}),1.0]])]});
            var Q1117;
            Q1117=makeQuery(id+"F6.imprint","IMPRINT",FACE,{"disambiguationData":[TD([[makeQuery(id+"F6.imprint","IMPRINT",EDGE,{"derivedFrom":sQuery(id+"F6.wireOp",EDGE,"E43.20.0.12")}),1.0]])]});
            var Q1118;
            Q1118=makeQuery(id+"F6.imprint","IMPRINT",FACE,{"disambiguationData":[TD([[makeQuery(id+"F6.imprint","IMPRINT",EDGE,{"derivedFrom":sQuery(id+"F6.wireOp",EDGE,"E43.19.0.20")}),1.0]])]});
            var Q1119;
            Q1119=makeQuery(id+"F6.imprint","IMPRINT",FACE,{"disambiguationData":[TD([[makeQuery(id+"F6.imprint","IMPRINT",EDGE,{"derivedFrom":sQuery(id+"F6.wireOp",EDGE,"E43.19.0.2")}),1.0]])]});
            var Q1120;
            Q1120=makeQuery(id+"F6.imprint","IMPRINT",FACE,{"disambiguationData":[TD([[makeQuery(id+"F6.imprint","IMPRINT",EDGE,{"derivedFrom":sQuery(id+"F6.wireOp",EDGE,"E43.18.0.12")}),1.0]])]});
            var Q1121;
            Q1121=makeQuery(id+"F6.imprint","IMPRINT",FACE,{"disambiguationData":[TD([[makeQuery(id+"F6.imprint","IMPRINT",EDGE,{"derivedFrom":sQuery(id+"F6.wireOp",EDGE,"E319.MirrorC")}),-1.0]])]});
            var Q1122;
            Q1122=makeQuery(id+"F6.imprint","IMPRINT",FACE,{"disambiguationData":[TD([[makeQuery(id+"F6.imprint","IMPRINT",EDGE,{"derivedFrom":sQuery(id+"F6.wireOp",EDGE,"E334.MirrorC")}),-1.0]])]});
            var Q1123;
            Q1123=makeQuery(id+"F6.imprint","IMPRINT",FACE,{"disambiguationData":[TD([[makeQuery(id+"F6.imprint","IMPRINT",EDGE,{"derivedFrom":sQuery(id+"F6.wireOp",EDGE,"E303.MirrorC")}),-1.0]])]});
            var Q1124;
            Q1124=makeQuery(id+"F6.imprint","IMPRINT",FACE,{"disambiguationData":[TD([[makeQuery(id+"F6.imprint","IMPRINT",EDGE,{"derivedFrom":sQuery(id+"F6.wireOp",EDGE,"E287.MirrorC")}),-1.0]])]});
            var Q1125;
            Q1125=makeQuery(id+"F6.imprint","IMPRINT",FACE,{"disambiguationData":[TD([[makeQuery(id+"F6.imprint","IMPRINT",EDGE,{"derivedFrom":sQuery(id+"F6.wireOp",EDGE,"E271.MirrorC")}),-1.0]])]});
            var Q1126;
            Q1126=makeQuery(id+"F6.imprint","IMPRINT",FACE,{"disambiguationData":[TD([[makeQuery(id+"F6.imprint","IMPRINT",EDGE,{"derivedFrom":sQuery(id+"F6.wireOp",EDGE,"E257.MirrorC")}),-1.0]])]});
            var Q1127;
            Q1127=makeQuery(id+"F6.imprint","IMPRINT",FACE,{"disambiguationData":[TD([[makeQuery(id+"F6.imprint","IMPRINT",EDGE,{"derivedFrom":sQuery(id+"F6.wireOp",EDGE,"E43.3.0.2")}),1.0]])]});
            var Q1128;
            Q1128=makeQuery(id+"F6.imprint","IMPRINT",FACE,{"disambiguationData":[TD([[makeQuery(id+"F6.imprint","IMPRINT",EDGE,{"derivedFrom":sQuery(id+"F6.wireOp",EDGE,"E43.2.0.12")}),1.0]])]});
            var Q1129;
            Q1129=makeQuery(id+"F6.imprint","IMPRINT",FACE,{"disambiguationData":[TD([[makeQuery(id+"F6.imprint","IMPRINT",EDGE,{"derivedFrom":sQuery(id+"F6.wireOp",EDGE,"E43.1.0.20")}),1.0]])]});
            var Q1130;
            Q1130=makeQuery(id+"F6.imprint","IMPRINT",FACE,{"disambiguationData":[TD([[makeQuery(id+"F6.imprint","IMPRINT",EDGE,{"derivedFrom":sQuery(id+"F6.wireOp",EDGE,"E43.1.0.2")}),1.0]])]});
            var Q1131;
            Q1131=makeQuery(id+"F6.imprint","IMPRINT",FACE,{"disambiguationData":[TD([[makeQuery(id+"F6.imprint","IMPRINT",EDGE,{"derivedFrom":sQuery(id+"F6.wireOp",EDGE,"E43.23.0.2")}),1.0]])]});
            var Q1132;
            Q1132=makeQuery(id+"F6.imprint","IMPRINT",FACE,{"disambiguationData":[TD([[makeQuery(id+"F6.imprint","IMPRINT",EDGE,{"derivedFrom":sQuery(id+"F6.wireOp",EDGE,"E43.22.0.12")}),1.0]])]});
            var Q1133;
            Q1133=makeQuery(id+"F6.imprint","IMPRINT",FACE,{"disambiguationData":[TD([[makeQuery(id+"F6.imprint","IMPRINT",EDGE,{"derivedFrom":sQuery(id+"F6.wireOp",EDGE,"E43.21.0.20")}),1.0]])]});
            var Q1134;
            Q1134=makeQuery(id+"F6.imprint","IMPRINT",FACE,{"disambiguationData":[TD([[makeQuery(id+"F6.imprint","IMPRINT",EDGE,{"derivedFrom":sQuery(id+"F6.wireOp",EDGE,"E43.21.0.2")}),1.0]])]});
            var Q1135;
            Q1135=makeQuery(id+"F6.imprint","IMPRINT",FACE,{"disambiguationData":[TD([[makeQuery(id+"F6.imprint","IMPRINT",EDGE,{"derivedFrom":sQuery(id+"F6.wireOp",EDGE,"E43.25.0.20")}),1.0]])]});
            var Q1136;
            Q1136=makeQuery(id+"F6.imprint","IMPRINT",FACE,{"disambiguationData":[TD([[makeQuery(id+"F6.imprint","IMPRINT",EDGE,{"derivedFrom":sQuery(id+"F6.wireOp",EDGE,"E43.25.0.2")}),1.0]])]});
            var Q1137;
            Q1137=makeQuery(id+"F6.imprint","IMPRINT",FACE,{"disambiguationData":[TD([[makeQuery(id+"F6.imprint","IMPRINT",EDGE,{"derivedFrom":sQuery(id+"F6.wireOp",EDGE,"E43.24.0.12")}),1.0]])]});
            var Q1138;
            Q1138=makeQuery(id+"F6.imprint","IMPRINT",FACE,{"disambiguationData":[TD([[makeQuery(id+"F6.imprint","IMPRINT",EDGE,{"derivedFrom":sQuery(id+"F6.wireOp",EDGE,"E43.23.0.20")}),1.0]])]});
            var Q1139;
            Q1139=makeQuery(id+"F6.imprint","IMPRINT",FACE,{"disambiguationData":[TD([[makeQuery(id+"F6.imprint","IMPRINT",EDGE,{"derivedFrom":sQuery(id+"F6.wireOp",EDGE,"E43.28.0.12")}),1.0]])]});
            var Q1140;
            Q1140=makeQuery(id+"F6.imprint","IMPRINT",FACE,{"disambiguationData":[TD([[makeQuery(id+"F6.imprint","IMPRINT",EDGE,{"derivedFrom":sQuery(id+"F6.wireOp",EDGE,"E43.27.0.20")}),1.0]])]});
            var Q1141;
            Q1141=makeQuery(id+"F6.imprint","IMPRINT",FACE,{"disambiguationData":[TD([[makeQuery(id+"F6.imprint","IMPRINT",EDGE,{"derivedFrom":sQuery(id+"F6.wireOp",EDGE,"E43.27.0.2")}),1.0]])]});
            var Q1142;
            Q1142=makeQuery(id+"F6.imprint","IMPRINT",FACE,{"disambiguationData":[TD([[makeQuery(id+"F6.imprint","IMPRINT",EDGE,{"derivedFrom":sQuery(id+"F6.wireOp",EDGE,"E43.26.0.12")}),1.0]])]});
            var Q1143;
            Q1143=makeQuery(id+"F6.imprint","IMPRINT",FACE,{"disambiguationData":[TD([[makeQuery(id+"F6.imprint","IMPRINT",EDGE,{"derivedFrom":sQuery(id+"F6.wireOp",EDGE,"E43.31.0.2")}),1.0]])]});
            var Q1144;
            Q1144=makeQuery(id+"F6.imprint","IMPRINT",FACE,{"disambiguationData":[TD([[makeQuery(id+"F6.imprint","IMPRINT",EDGE,{"derivedFrom":sQuery(id+"F6.wireOp",EDGE,"E43.30.0.12")}),1.0]])]});
            var Q1145;
            Q1145=makeQuery(id+"F6.imprint","IMPRINT",FACE,{"disambiguationData":[TD([[makeQuery(id+"F6.imprint","IMPRINT",EDGE,{"derivedFrom":sQuery(id+"F6.wireOp",EDGE,"E43.29.0.20")}),1.0]])]});
            var Q1146;
            Q1146=makeQuery(id+"F6.imprint","IMPRINT",FACE,{"disambiguationData":[TD([[makeQuery(id+"F6.imprint","IMPRINT",EDGE,{"derivedFrom":sQuery(id+"F6.wireOp",EDGE,"E43.29.0.2")}),1.0]])]});
            var Q1147;
            Q1147=makeQuery(id+"F6.imprint","IMPRINT",FACE,{"disambiguationData":[TD([[makeQuery(id+"F6.imprint","IMPRINT",EDGE,{"derivedFrom":sQuery(id+"F6.wireOp",EDGE,"E43.32.0.12")}),1.0]])]});
            var Q1148;
            Q1148=makeQuery(id+"F6.imprint","IMPRINT",FACE,{"disambiguationData":[TD([[makeQuery(id+"F6.imprint","IMPRINT",EDGE,{"derivedFrom":sQuery(id+"F6.wireOp",EDGE,"E43.31.0.20")}),1.0]])]});
            var Q1149;
            Q1149=makeQuery(id+"F6.imprint","IMPRINT",FACE,{"disambiguationData":[TD([[makeQuery(id+"F6.imprint","IMPRINT",EDGE,{"derivedFrom":sQuery(id+"F6.wireOp",EDGE,"E43.8.0.13")}),1.0]])]});
            var Q1150;
            Q1150=makeQuery(id+"F6.imprint","IMPRINT",FACE,{"disambiguationData":[TD([[makeQuery(id+"F6.imprint","IMPRINT",EDGE,{"derivedFrom":sQuery(id+"F6.wireOp",EDGE,"E43.7.0.21")}),1.0]])]});
            var Q1151;
            Q1151=makeQuery(id+"F6.imprint","IMPRINT",FACE,{"disambiguationData":[TD([[makeQuery(id+"F6.imprint","IMPRINT",EDGE,{"derivedFrom":sQuery(id+"F6.wireOp",EDGE,"E43.7.0.4")}),1.0]])]});
            var Q1152;
            Q1152=makeQuery(id+"F6.imprint","IMPRINT",FACE,{"disambiguationData":[TD([[makeQuery(id+"F6.imprint","IMPRINT",EDGE,{"derivedFrom":sQuery(id+"F6.wireOp",EDGE,"E43.6.0.13")}),1.0]])]});
            var Q1153;
            Q1153=makeQuery(id+"F6.imprint","IMPRINT",FACE,{"disambiguationData":[TD([[makeQuery(id+"F6.imprint","IMPRINT",EDGE,{"derivedFrom":sQuery(id+"F6.wireOp",EDGE,"E43.11.0.4")}),1.0]])]});
            var Q1154;
            Q1154=makeQuery(id+"F6.imprint","IMPRINT",FACE,{"disambiguationData":[TD([[makeQuery(id+"F6.imprint","IMPRINT",EDGE,{"derivedFrom":sQuery(id+"F6.wireOp",EDGE,"E43.10.0.13")}),1.0]])]});
            var Q1155;
            Q1155=makeQuery(id+"F6.imprint","IMPRINT",FACE,{"disambiguationData":[TD([[makeQuery(id+"F6.imprint","IMPRINT",EDGE,{"derivedFrom":sQuery(id+"F6.wireOp",EDGE,"E43.9.0.21")}),1.0]])]});
            var Q1156;
            Q1156=makeQuery(id+"F6.imprint","IMPRINT",FACE,{"disambiguationData":[TD([[makeQuery(id+"F6.imprint","IMPRINT",EDGE,{"derivedFrom":sQuery(id+"F6.wireOp",EDGE,"E43.9.0.4")}),1.0]])]});
            var Q1157;
            Q1157=makeQuery(id+"F6.imprint","IMPRINT",FACE,{"disambiguationData":[TD([[makeQuery(id+"F6.imprint","IMPRINT",EDGE,{"derivedFrom":sQuery(id+"F6.wireOp",EDGE,"E43.13.0.21")}),1.0]])]});
            var Q1158;
            Q1158=makeQuery(id+"F6.imprint","IMPRINT",FACE,{"disambiguationData":[TD([[makeQuery(id+"F6.imprint","IMPRINT",EDGE,{"derivedFrom":sQuery(id+"F6.wireOp",EDGE,"E43.13.0.4")}),1.0]])]});
            var Q1159;
            Q1159=makeQuery(id+"F6.imprint","IMPRINT",FACE,{"disambiguationData":[TD([[makeQuery(id+"F6.imprint","IMPRINT",EDGE,{"derivedFrom":sQuery(id+"F6.wireOp",EDGE,"E43.12.0.13")}),1.0]])]});
            var Q1160;
            Q1160=makeQuery(id+"F6.imprint","IMPRINT",FACE,{"disambiguationData":[TD([[makeQuery(id+"F6.imprint","IMPRINT",EDGE,{"derivedFrom":sQuery(id+"F6.wireOp",EDGE,"E43.11.0.21")}),1.0]])]});
            var Q1161;
            Q1161=makeQuery(id+"F6.imprint","IMPRINT",FACE,{"disambiguationData":[TD([[makeQuery(id+"F6.imprint","IMPRINT",EDGE,{"derivedFrom":sQuery(id+"F6.wireOp",EDGE,"E43.16.0.13")}),1.0]])]});
            var Q1162;
            Q1162=makeQuery(id+"F6.imprint","IMPRINT",FACE,{"disambiguationData":[TD([[makeQuery(id+"F6.imprint","IMPRINT",EDGE,{"derivedFrom":sQuery(id+"F6.wireOp",EDGE,"E43.15.0.21")}),1.0]])]});
            var Q1163;
            Q1163=makeQuery(id+"F6.imprint","IMPRINT",FACE,{"disambiguationData":[TD([[makeQuery(id+"F6.imprint","IMPRINT",EDGE,{"derivedFrom":sQuery(id+"F6.wireOp",EDGE,"E43.15.0.4")}),1.0]])]});
            var Q1164;
            Q1164=makeQuery(id+"F6.imprint","IMPRINT",FACE,{"disambiguationData":[TD([[makeQuery(id+"F6.imprint","IMPRINT",EDGE,{"derivedFrom":sQuery(id+"F6.wireOp",EDGE,"E43.14.0.13")}),1.0]])]});
            var Q1165;
            Q1165=makeQuery(id+"F6.imprint","IMPRINT",FACE,{"disambiguationData":[TD([[makeQuery(id+"F6.imprint","IMPRINT",EDGE,{"derivedFrom":sQuery(id+"F6.wireOp",EDGE,"E43.17.0.4")}),1.0]])]});
            var Q1166;
            Q1166=makeQuery(id+"F6.imprint","IMPRINT",FACE,{"disambiguationData":[TD([[makeQuery(id+"F6.imprint","IMPRINT",EDGE,{"derivedFrom":sQuery(id+"F6.wireOp",EDGE,"E43.17.0.21")}),1.0]])]});
            var Q1167;
            Q1167=makeQuery(id+"F6.imprint","IMPRINT",FACE,{"disambiguationData":[TD([[makeQuery(id+"F6.imprint","IMPRINT",EDGE,{"derivedFrom":sQuery(id+"F6.wireOp",EDGE,"E43.20.0.13")}),1.0]])]});
            var Q1168;
            Q1168=makeQuery(id+"F6.imprint","IMPRINT",FACE,{"disambiguationData":[TD([[makeQuery(id+"F6.imprint","IMPRINT",EDGE,{"derivedFrom":sQuery(id+"F6.wireOp",EDGE,"E43.19.0.21")}),1.0]])]});
            var Q1169;
            Q1169=makeQuery(id+"F6.imprint","IMPRINT",FACE,{"disambiguationData":[TD([[makeQuery(id+"F6.imprint","IMPRINT",EDGE,{"derivedFrom":sQuery(id+"F6.wireOp",EDGE,"E43.19.0.4")}),1.0]])]});
            var Q1170;
            Q1170=makeQuery(id+"F6.imprint","IMPRINT",FACE,{"disambiguationData":[TD([[makeQuery(id+"F6.imprint","IMPRINT",EDGE,{"derivedFrom":sQuery(id+"F6.wireOp",EDGE,"E43.18.0.13")}),1.0]])]});
            var Q1171;
            Q1171=makeQuery(id+"F6.imprint","IMPRINT",FACE,{"disambiguationData":[TD([[makeQuery(id+"F6.imprint","IMPRINT",EDGE,{"derivedFrom":sQuery(id+"F6.wireOp",EDGE,"E43.23.0.4")}),1.0]])]});
            var Q1172;
            Q1172=makeQuery(id+"F6.imprint","IMPRINT",FACE,{"disambiguationData":[TD([[makeQuery(id+"F6.imprint","IMPRINT",EDGE,{"derivedFrom":sQuery(id+"F6.wireOp",EDGE,"E43.22.0.13")}),1.0]])]});
            var Q1173;
            Q1173=makeQuery(id+"F6.imprint","IMPRINT",FACE,{"disambiguationData":[TD([[makeQuery(id+"F6.imprint","IMPRINT",EDGE,{"derivedFrom":sQuery(id+"F6.wireOp",EDGE,"E43.21.0.21")}),1.0]])]});
            var Q1174;
            Q1174=makeQuery(id+"F6.imprint","IMPRINT",FACE,{"disambiguationData":[TD([[makeQuery(id+"F6.imprint","IMPRINT",EDGE,{"derivedFrom":sQuery(id+"F6.wireOp",EDGE,"E43.21.0.4")}),1.0]])]});
            var Q1175;
            Q1175=makeQuery(id+"F6.imprint","IMPRINT",FACE,{"disambiguationData":[TD([[makeQuery(id+"F6.imprint","IMPRINT",EDGE,{"derivedFrom":sQuery(id+"F6.wireOp",EDGE,"E335.MirrorC")}),-1.0]])]});
            var Q1176;
            Q1176=makeQuery(id+"F6.imprint","IMPRINT",FACE,{"disambiguationData":[TD([[makeQuery(id+"F6.imprint","IMPRINT",EDGE,{"derivedFrom":sQuery(id+"F6.wireOp",EDGE,"E304.MirrorC")}),-1.0]])]});
            var Q1177;
            Q1177=makeQuery(id+"F6.imprint","IMPRINT",FACE,{"disambiguationData":[TD([[makeQuery(id+"F6.imprint","IMPRINT",EDGE,{"derivedFrom":sQuery(id+"F6.wireOp",EDGE,"E288.MirrorC")}),-1.0]])]});
            var Q1178;
            Q1178=makeQuery(id+"F6.imprint","IMPRINT",FACE,{"disambiguationData":[TD([[makeQuery(id+"F6.imprint","IMPRINT",EDGE,{"derivedFrom":sQuery(id+"F6.wireOp",EDGE,"E272.MirrorC")}),-1.0]])]});
            var Q1179;
            Q1179=makeQuery(id+"F6.imprint","IMPRINT",FACE,{"disambiguationData":[TD([[makeQuery(id+"F6.imprint","IMPRINT",EDGE,{"derivedFrom":sQuery(id+"F6.wireOp",EDGE,"E258.MirrorC")}),-1.0]])]});
            var Q1180;
            Q1180=makeQuery(id+"F6.imprint","IMPRINT",FACE,{"disambiguationData":[TD([[makeQuery(id+"F6.imprint","IMPRINT",EDGE,{"derivedFrom":sQuery(id+"F6.wireOp",EDGE,"E43.3.0.4")}),1.0]])]});
            var Q1181;
            Q1181=makeQuery(id+"F6.imprint","IMPRINT",FACE,{"disambiguationData":[TD([[makeQuery(id+"F6.imprint","IMPRINT",EDGE,{"derivedFrom":sQuery(id+"F6.wireOp",EDGE,"E43.2.0.13")}),1.0]])]});
            var Q1182;
            Q1182=makeQuery(id+"F6.imprint","IMPRINT",FACE,{"disambiguationData":[TD([[makeQuery(id+"F6.imprint","IMPRINT",EDGE,{"derivedFrom":sQuery(id+"F6.wireOp",EDGE,"E43.1.0.21")}),1.0]])]});
            var Q1183;
            Q1183=makeQuery(id+"F6.imprint","IMPRINT",FACE,{"disambiguationData":[TD([[makeQuery(id+"F6.imprint","IMPRINT",EDGE,{"derivedFrom":sQuery(id+"F6.wireOp",EDGE,"E43.1.0.4")}),1.0]])]});
            var Q1184;
            Q1184=makeQuery(id+"F6.imprint","IMPRINT",FACE,{"disambiguationData":[TD([[makeQuery(id+"F6.imprint","IMPRINT",EDGE,{"derivedFrom":sQuery(id+"F6.wireOp",EDGE,"E43.5.0.21")}),1.0]])]});
            var Q1185;
            Q1185=makeQuery(id+"F6.imprint","IMPRINT",FACE,{"disambiguationData":[TD([[makeQuery(id+"F6.imprint","IMPRINT",EDGE,{"derivedFrom":sQuery(id+"F6.wireOp",EDGE,"E43.5.0.4")}),1.0]])]});
            var Q1186;
            Q1186=makeQuery(id+"F6.imprint","IMPRINT",FACE,{"disambiguationData":[TD([[makeQuery(id+"F6.imprint","IMPRINT",EDGE,{"derivedFrom":sQuery(id+"F6.wireOp",EDGE,"E43.4.0.13")}),1.0]])]});
            var Q1187;
            Q1187=makeQuery(id+"F6.imprint","IMPRINT",FACE,{"disambiguationData":[TD([[makeQuery(id+"F6.imprint","IMPRINT",EDGE,{"derivedFrom":sQuery(id+"F6.wireOp",EDGE,"E43.3.0.21")}),1.0]])]});
            var Q1188;
            Q1188=makeQuery(id+"F6.imprint","IMPRINT",FACE,{"disambiguationData":[TD([[makeQuery(id+"F6.imprint","IMPRINT",EDGE,{"derivedFrom":sQuery(id+"F6.wireOp",EDGE,"E320.MirrorC")}),-1.0]])]});
            var Q1189;
            Q1189=makeQuery(id+"F6.imprint","IMPRINT",FACE,{"disambiguationData":[TD([[makeQuery(id+"F6.imprint","IMPRINT",EDGE,{"derivedFrom":sQuery(id+"F6.wireOp",EDGE,"E43.25.0.21")}),1.0]])]});
            var Q1190;
            Q1190=makeQuery(id+"F6.imprint","IMPRINT",FACE,{"disambiguationData":[TD([[makeQuery(id+"F6.imprint","IMPRINT",EDGE,{"derivedFrom":sQuery(id+"F6.wireOp",EDGE,"E43.25.0.4")}),1.0]])]});
            var Q1191;
            Q1191=makeQuery(id+"F6.imprint","IMPRINT",FACE,{"disambiguationData":[TD([[makeQuery(id+"F6.imprint","IMPRINT",EDGE,{"derivedFrom":sQuery(id+"F6.wireOp",EDGE,"E43.24.0.13")}),1.0]])]});
            var Q1192;
            Q1192=makeQuery(id+"F6.imprint","IMPRINT",FACE,{"disambiguationData":[TD([[makeQuery(id+"F6.imprint","IMPRINT",EDGE,{"derivedFrom":sQuery(id+"F6.wireOp",EDGE,"E43.23.0.21")}),1.0]])]});
            var Q1193;
            Q1193=makeQuery(id+"F6.imprint","IMPRINT",FACE,{"disambiguationData":[TD([[makeQuery(id+"F6.imprint","IMPRINT",EDGE,{"derivedFrom":sQuery(id+"F6.wireOp",EDGE,"E43.28.0.13")}),1.0]])]});
            var Q1194;
            Q1194=makeQuery(id+"F6.imprint","IMPRINT",FACE,{"disambiguationData":[TD([[makeQuery(id+"F6.imprint","IMPRINT",EDGE,{"derivedFrom":sQuery(id+"F6.wireOp",EDGE,"E43.27.0.21")}),1.0]])]});
            var Q1195;
            Q1195=makeQuery(id+"F6.imprint","IMPRINT",FACE,{"disambiguationData":[TD([[makeQuery(id+"F6.imprint","IMPRINT",EDGE,{"derivedFrom":sQuery(id+"F6.wireOp",EDGE,"E43.27.0.4")}),1.0]])]});
            var Q1196;
            Q1196=makeQuery(id+"F6.imprint","IMPRINT",FACE,{"disambiguationData":[TD([[makeQuery(id+"F6.imprint","IMPRINT",EDGE,{"derivedFrom":sQuery(id+"F6.wireOp",EDGE,"E43.26.0.13")}),1.0]])]});
            var Q1197;
            Q1197=makeQuery(id+"F6.imprint","IMPRINT",FACE,{"disambiguationData":[TD([[makeQuery(id+"F6.imprint","IMPRINT",EDGE,{"derivedFrom":sQuery(id+"F6.wireOp",EDGE,"E43.31.0.4")}),1.0]])]});
            var Q1198;
            Q1198=makeQuery(id+"F6.imprint","IMPRINT",FACE,{"disambiguationData":[TD([[makeQuery(id+"F6.imprint","IMPRINT",EDGE,{"derivedFrom":sQuery(id+"F6.wireOp",EDGE,"E43.30.0.13")}),1.0]])]});
            var Q1199;
            Q1199=makeQuery(id+"F6.imprint","IMPRINT",FACE,{"disambiguationData":[TD([[makeQuery(id+"F6.imprint","IMPRINT",EDGE,{"derivedFrom":sQuery(id+"F6.wireOp",EDGE,"E43.29.0.21")}),1.0]])]});
            var Q1200;
            Q1200=makeQuery(id+"F6.imprint","IMPRINT",FACE,{"disambiguationData":[TD([[makeQuery(id+"F6.imprint","IMPRINT",EDGE,{"derivedFrom":sQuery(id+"F6.wireOp",EDGE,"E43.29.0.4")}),1.0]])]});
            var Q1201;
            Q1201=makeQuery(id+"F6.imprint","IMPRINT",FACE,{"disambiguationData":[TD([[makeQuery(id+"F6.imprint","IMPRINT",EDGE,{"derivedFrom":sQuery(id+"F6.wireOp",EDGE,"E43.32.0.13")}),1.0]])]});
            var Q1202;
            Q1202=makeQuery(id+"F6.imprint","IMPRINT",FACE,{"disambiguationData":[TD([[makeQuery(id+"F6.imprint","IMPRINT",EDGE,{"derivedFrom":sQuery(id+"F6.wireOp",EDGE,"E43.31.0.21")}),1.0]])]});
            var Q1203;
            Q1203=makeQuery(id+"F6.imprint","IMPRINT",FACE,{"disambiguationData":[TD([[makeQuery(id+"F6.imprint","IMPRINT",EDGE,{"derivedFrom":sQuery(id+"F6.wireOp",EDGE,"E43.11.0.5")}),1.0]])]});
            var Q1204;
            Q1204=makeQuery(id+"F6.imprint","IMPRINT",FACE,{"disambiguationData":[TD([[makeQuery(id+"F6.imprint","IMPRINT",EDGE,{"derivedFrom":sQuery(id+"F6.wireOp",EDGE,"E43.10.0.14")}),1.0]])]});
            var Q1205;
            Q1205=makeQuery(id+"F6.imprint","IMPRINT",FACE,{"disambiguationData":[TD([[makeQuery(id+"F6.imprint","IMPRINT",EDGE,{"derivedFrom":sQuery(id+"F6.wireOp",EDGE,"E43.9.0.22")}),1.0]])]});
            var Q1206;
            Q1206=makeQuery(id+"F6.imprint","IMPRINT",FACE,{"disambiguationData":[TD([[makeQuery(id+"F6.imprint","IMPRINT",EDGE,{"derivedFrom":sQuery(id+"F6.wireOp",EDGE,"E43.9.0.5")}),1.0]])]});
            var Q1207;
            Q1207=makeQuery(id+"F6.imprint","IMPRINT",FACE,{"disambiguationData":[TD([[makeQuery(id+"F6.imprint","IMPRINT",EDGE,{"derivedFrom":sQuery(id+"F6.wireOp",EDGE,"E43.13.0.22")}),1.0]])]});
            var Q1208;
            Q1208=makeQuery(id+"F6.imprint","IMPRINT",FACE,{"disambiguationData":[TD([[makeQuery(id+"F6.imprint","IMPRINT",EDGE,{"derivedFrom":sQuery(id+"F6.wireOp",EDGE,"E43.13.0.5")}),1.0]])]});
            var Q1209;
            Q1209=makeQuery(id+"F6.imprint","IMPRINT",FACE,{"disambiguationData":[TD([[makeQuery(id+"F6.imprint","IMPRINT",EDGE,{"derivedFrom":sQuery(id+"F6.wireOp",EDGE,"E43.12.0.14")}),1.0]])]});
            var Q1210;
            Q1210=makeQuery(id+"F6.imprint","IMPRINT",FACE,{"disambiguationData":[TD([[makeQuery(id+"F6.imprint","IMPRINT",EDGE,{"derivedFrom":sQuery(id+"F6.wireOp",EDGE,"E43.11.0.22")}),1.0]])]});
            var Q1211;
            Q1211=makeQuery(id+"F6.imprint","IMPRINT",FACE,{"disambiguationData":[TD([[makeQuery(id+"F6.imprint","IMPRINT",EDGE,{"derivedFrom":sQuery(id+"F6.wireOp",EDGE,"E43.16.0.14")}),1.0]])]});
            var Q1212;
            Q1212=makeQuery(id+"F6.imprint","IMPRINT",FACE,{"disambiguationData":[TD([[makeQuery(id+"F6.imprint","IMPRINT",EDGE,{"derivedFrom":sQuery(id+"F6.wireOp",EDGE,"E43.15.0.22")}),1.0]])]});
            var Q1213;
            Q1213=makeQuery(id+"F6.imprint","IMPRINT",FACE,{"disambiguationData":[TD([[makeQuery(id+"F6.imprint","IMPRINT",EDGE,{"derivedFrom":sQuery(id+"F6.wireOp",EDGE,"E43.15.0.5")}),1.0]])]});
            var Q1214;
            Q1214=makeQuery(id+"F6.imprint","IMPRINT",FACE,{"disambiguationData":[TD([[makeQuery(id+"F6.imprint","IMPRINT",EDGE,{"derivedFrom":sQuery(id+"F6.wireOp",EDGE,"E43.14.0.14")}),1.0]])]});
            var Q1215;
            Q1215=makeQuery(id+"F6.imprint","IMPRINT",FACE,{"disambiguationData":[TD([[makeQuery(id+"F6.imprint","IMPRINT",EDGE,{"derivedFrom":sQuery(id+"F6.wireOp",EDGE,"E43.17.0.5")}),1.0]])]});
            var Q1216;
            Q1216=makeQuery(id+"F6.imprint","IMPRINT",FACE,{"disambiguationData":[TD([[makeQuery(id+"F6.imprint","IMPRINT",EDGE,{"derivedFrom":sQuery(id+"F6.wireOp",EDGE,"E43.17.0.22")}),1.0]])]});
            var Q1217;
            Q1217=makeQuery(id+"F6.imprint","IMPRINT",FACE,{"disambiguationData":[TD([[makeQuery(id+"F6.imprint","IMPRINT",EDGE,{"derivedFrom":sQuery(id+"F6.wireOp",EDGE,"E43.20.0.14")}),1.0]])]});
            var Q1218;
            Q1218=makeQuery(id+"F6.imprint","IMPRINT",FACE,{"disambiguationData":[TD([[makeQuery(id+"F6.imprint","IMPRINT",EDGE,{"derivedFrom":sQuery(id+"F6.wireOp",EDGE,"E43.19.0.22")}),1.0]])]});
            var Q1219;
            Q1219=makeQuery(id+"F6.imprint","IMPRINT",FACE,{"disambiguationData":[TD([[makeQuery(id+"F6.imprint","IMPRINT",EDGE,{"derivedFrom":sQuery(id+"F6.wireOp",EDGE,"E43.19.0.5")}),1.0]])]});
            var Q1220;
            Q1220=makeQuery(id+"F6.imprint","IMPRINT",FACE,{"disambiguationData":[TD([[makeQuery(id+"F6.imprint","IMPRINT",EDGE,{"derivedFrom":sQuery(id+"F6.wireOp",EDGE,"E43.18.0.14")}),1.0]])]});
            var Q1221;
            Q1221=makeQuery(id+"F6.imprint","IMPRINT",FACE,{"disambiguationData":[TD([[makeQuery(id+"F6.imprint","IMPRINT",EDGE,{"derivedFrom":sQuery(id+"F6.wireOp",EDGE,"E43.23.0.5")}),1.0]])]});
            var Q1222;
            Q1222=makeQuery(id+"F6.imprint","IMPRINT",FACE,{"disambiguationData":[TD([[makeQuery(id+"F6.imprint","IMPRINT",EDGE,{"derivedFrom":sQuery(id+"F6.wireOp",EDGE,"E43.22.0.14")}),1.0]])]});
            var Q1223;
            Q1223=makeQuery(id+"F6.imprint","IMPRINT",FACE,{"disambiguationData":[TD([[makeQuery(id+"F6.imprint","IMPRINT",EDGE,{"derivedFrom":sQuery(id+"F6.wireOp",EDGE,"E43.21.0.22")}),1.0]])]});
            var Q1224;
            Q1224=makeQuery(id+"F6.imprint","IMPRINT",FACE,{"disambiguationData":[TD([[makeQuery(id+"F6.imprint","IMPRINT",EDGE,{"derivedFrom":sQuery(id+"F6.wireOp",EDGE,"E43.21.0.5")}),1.0]])]});
            var Q1225;
            Q1225=makeQuery(id+"F6.imprint","IMPRINT",FACE,{"disambiguationData":[TD([[makeQuery(id+"F6.imprint","IMPRINT",EDGE,{"derivedFrom":sQuery(id+"F6.wireOp",EDGE,"E43.25.0.22")}),1.0]])]});
            var Q1226;
            Q1226=makeQuery(id+"F6.imprint","IMPRINT",FACE,{"disambiguationData":[TD([[makeQuery(id+"F6.imprint","IMPRINT",EDGE,{"derivedFrom":sQuery(id+"F6.wireOp",EDGE,"E43.25.0.5")}),1.0]])]});
            var Q1227;
            Q1227=makeQuery(id+"F6.imprint","IMPRINT",FACE,{"disambiguationData":[TD([[makeQuery(id+"F6.imprint","IMPRINT",EDGE,{"derivedFrom":sQuery(id+"F6.wireOp",EDGE,"E43.24.0.14")}),1.0]])]});
            var Q1228;
            Q1228=makeQuery(id+"F6.imprint","IMPRINT",FACE,{"disambiguationData":[TD([[makeQuery(id+"F6.imprint","IMPRINT",EDGE,{"derivedFrom":sQuery(id+"F6.wireOp",EDGE,"E43.23.0.22")}),1.0]])]});
            var Q1229;
            Q1229=makeQuery(id+"F6.imprint","IMPRINT",FACE,{"disambiguationData":[TD([[makeQuery(id+"F6.imprint","IMPRINT",EDGE,{"derivedFrom":sQuery(id+"F6.wireOp",EDGE,"E336.MirrorC")}),-1.0]])]});
            var Q1230;
            Q1230=makeQuery(id+"F6.imprint","IMPRINT",FACE,{"disambiguationData":[TD([[makeQuery(id+"F6.imprint","IMPRINT",EDGE,{"derivedFrom":sQuery(id+"F6.wireOp",EDGE,"E305.MirrorC")}),-1.0]])]});
            var Q1231;
            Q1231=makeQuery(id+"F6.imprint","IMPRINT",FACE,{"disambiguationData":[TD([[makeQuery(id+"F6.imprint","IMPRINT",EDGE,{"derivedFrom":sQuery(id+"F6.wireOp",EDGE,"E289.MirrorC")}),-1.0]])]});
            var Q1232;
            Q1232=makeQuery(id+"F6.imprint","IMPRINT",FACE,{"disambiguationData":[TD([[makeQuery(id+"F6.imprint","IMPRINT",EDGE,{"derivedFrom":sQuery(id+"F6.wireOp",EDGE,"E273.MirrorC")}),-1.0]])]});
            var Q1233;
            Q1233=makeQuery(id+"F6.imprint","IMPRINT",FACE,{"disambiguationData":[TD([[makeQuery(id+"F6.imprint","IMPRINT",EDGE,{"derivedFrom":sQuery(id+"F6.wireOp",EDGE,"E259.MirrorC")}),-1.0]])]});
            var Q1234;
            Q1234=makeQuery(id+"F6.imprint","IMPRINT",FACE,{"disambiguationData":[TD([[makeQuery(id+"F6.imprint","IMPRINT",EDGE,{"derivedFrom":sQuery(id+"F6.wireOp",EDGE,"E43.3.0.5")}),1.0]])]});
            var Q1235;
            Q1235=makeQuery(id+"F6.imprint","IMPRINT",FACE,{"disambiguationData":[TD([[makeQuery(id+"F6.imprint","IMPRINT",EDGE,{"derivedFrom":sQuery(id+"F6.wireOp",EDGE,"E43.2.0.14")}),1.0]])]});
            var Q1236;
            Q1236=makeQuery(id+"F6.imprint","IMPRINT",FACE,{"disambiguationData":[TD([[makeQuery(id+"F6.imprint","IMPRINT",EDGE,{"derivedFrom":sQuery(id+"F6.wireOp",EDGE,"E43.1.0.22")}),1.0]])]});
            var Q1237;
            Q1237=makeQuery(id+"F6.imprint","IMPRINT",FACE,{"disambiguationData":[TD([[makeQuery(id+"F6.imprint","IMPRINT",EDGE,{"derivedFrom":sQuery(id+"F6.wireOp",EDGE,"E43.1.0.5")}),1.0]])]});
            var Q1238;
            Q1238=makeQuery(id+"F6.imprint","IMPRINT",FACE,{"disambiguationData":[TD([[makeQuery(id+"F6.imprint","IMPRINT",EDGE,{"derivedFrom":sQuery(id+"F6.wireOp",EDGE,"E43.5.0.22")}),1.0]])]});
            var Q1239;
            Q1239=makeQuery(id+"F6.imprint","IMPRINT",FACE,{"disambiguationData":[TD([[makeQuery(id+"F6.imprint","IMPRINT",EDGE,{"derivedFrom":sQuery(id+"F6.wireOp",EDGE,"E43.5.0.5")}),1.0]])]});
            var Q1240;
            Q1240=makeQuery(id+"F6.imprint","IMPRINT",FACE,{"disambiguationData":[TD([[makeQuery(id+"F6.imprint","IMPRINT",EDGE,{"derivedFrom":sQuery(id+"F6.wireOp",EDGE,"E43.4.0.14")}),1.0]])]});
            var Q1241;
            Q1241=makeQuery(id+"F6.imprint","IMPRINT",FACE,{"disambiguationData":[TD([[makeQuery(id+"F6.imprint","IMPRINT",EDGE,{"derivedFrom":sQuery(id+"F6.wireOp",EDGE,"E43.3.0.22")}),1.0]])]});
            var Q1242;
            Q1242=makeQuery(id+"F6.imprint","IMPRINT",FACE,{"disambiguationData":[TD([[makeQuery(id+"F6.imprint","IMPRINT",EDGE,{"derivedFrom":sQuery(id+"F6.wireOp",EDGE,"E43.8.0.14")}),1.0]])]});
            var Q1243;
            Q1243=makeQuery(id+"F6.imprint","IMPRINT",FACE,{"disambiguationData":[TD([[makeQuery(id+"F6.imprint","IMPRINT",EDGE,{"derivedFrom":sQuery(id+"F6.wireOp",EDGE,"E43.7.0.22")}),1.0]])]});
            var Q1244;
            Q1244=makeQuery(id+"F6.imprint","IMPRINT",FACE,{"disambiguationData":[TD([[makeQuery(id+"F6.imprint","IMPRINT",EDGE,{"derivedFrom":sQuery(id+"F6.wireOp",EDGE,"E43.7.0.5")}),1.0]])]});
            var Q1245;
            Q1245=makeQuery(id+"F6.imprint","IMPRINT",FACE,{"disambiguationData":[TD([[makeQuery(id+"F6.imprint","IMPRINT",EDGE,{"derivedFrom":sQuery(id+"F6.wireOp",EDGE,"E43.6.0.14")}),1.0]])]});
            var Q1246;
            Q1246=makeQuery(id+"F6.imprint","IMPRINT",FACE,{"disambiguationData":[TD([[makeQuery(id+"F6.imprint","IMPRINT",EDGE,{"derivedFrom":sQuery(id+"F6.wireOp",EDGE,"E321.MirrorC")}),-1.0]])]});
            var Q1247;
            Q1247=makeQuery(id+"F6.imprint","IMPRINT",FACE,{"disambiguationData":[TD([[makeQuery(id+"F6.imprint","IMPRINT",EDGE,{"derivedFrom":sQuery(id+"F6.wireOp",EDGE,"E337.MirrorC")}),-1.0]])]});
            var Q1248;
            Q1248=makeQuery(id+"F6.imprint","IMPRINT",FACE,{"disambiguationData":[TD([[makeQuery(id+"F6.imprint","IMPRINT",EDGE,{"derivedFrom":sQuery(id+"F6.wireOp",EDGE,"E43.28.0.14")}),1.0]])]});
            var Q1249;
            Q1249=makeQuery(id+"F6.imprint","IMPRINT",FACE,{"disambiguationData":[TD([[makeQuery(id+"F6.imprint","IMPRINT",EDGE,{"derivedFrom":sQuery(id+"F6.wireOp",EDGE,"E43.27.0.22")}),1.0]])]});
            var Q1250;
            Q1250=makeQuery(id+"F6.imprint","IMPRINT",FACE,{"disambiguationData":[TD([[makeQuery(id+"F6.imprint","IMPRINT",EDGE,{"derivedFrom":sQuery(id+"F6.wireOp",EDGE,"E43.27.0.5")}),1.0]])]});
            var Q1251;
            Q1251=makeQuery(id+"F6.imprint","IMPRINT",FACE,{"disambiguationData":[TD([[makeQuery(id+"F6.imprint","IMPRINT",EDGE,{"derivedFrom":sQuery(id+"F6.wireOp",EDGE,"E43.26.0.14")}),1.0]])]});
            var Q1252;
            Q1252=makeQuery(id+"F6.imprint","IMPRINT",FACE,{"disambiguationData":[TD([[makeQuery(id+"F6.imprint","IMPRINT",EDGE,{"derivedFrom":sQuery(id+"F6.wireOp",EDGE,"E43.31.0.5")}),1.0]])]});
            var Q1253;
            Q1253=makeQuery(id+"F6.imprint","IMPRINT",FACE,{"disambiguationData":[TD([[makeQuery(id+"F6.imprint","IMPRINT",EDGE,{"derivedFrom":sQuery(id+"F6.wireOp",EDGE,"E43.30.0.14")}),1.0]])]});
            var Q1254;
            Q1254=makeQuery(id+"F6.imprint","IMPRINT",FACE,{"disambiguationData":[TD([[makeQuery(id+"F6.imprint","IMPRINT",EDGE,{"derivedFrom":sQuery(id+"F6.wireOp",EDGE,"E43.29.0.22")}),1.0]])]});
            var Q1255;
            Q1255=makeQuery(id+"F6.imprint","IMPRINT",FACE,{"disambiguationData":[TD([[makeQuery(id+"F6.imprint","IMPRINT",EDGE,{"derivedFrom":sQuery(id+"F6.wireOp",EDGE,"E43.29.0.5")}),1.0]])]});
            var Q1256;
            Q1256=makeQuery(id+"F6.imprint","IMPRINT",FACE,{"disambiguationData":[TD([[makeQuery(id+"F6.imprint","IMPRINT",EDGE,{"derivedFrom":sQuery(id+"F6.wireOp",EDGE,"E43.32.0.14")}),1.0]])]});
            var Q1257;
            Q1257=makeQuery(id+"F6.imprint","IMPRINT",FACE,{"disambiguationData":[TD([[makeQuery(id+"F6.imprint","IMPRINT",EDGE,{"derivedFrom":sQuery(id+"F6.wireOp",EDGE,"E43.31.0.22")}),1.0]])]});
            var Q1258;
            Q1258=makeQuery(id+"F6.imprint","IMPRINT",FACE,{"disambiguationData":[TD([[makeQuery(id+"F6.imprint","IMPRINT",EDGE,{"derivedFrom":sQuery(id+"F6.wireOp",EDGE,"E43.13.0.6")}),1.0]])]});
            var Q1259;
            Q1259=makeQuery(id+"F6.imprint","IMPRINT",FACE,{"disambiguationData":[TD([[makeQuery(id+"F6.imprint","IMPRINT",EDGE,{"derivedFrom":sQuery(id+"F6.wireOp",EDGE,"E43.12.0.15")}),1.0]])]});
            var Q1260;
            Q1260=makeQuery(id+"F6.imprint","IMPRINT",FACE,{"disambiguationData":[TD([[makeQuery(id+"F6.imprint","IMPRINT",EDGE,{"derivedFrom":sQuery(id+"F6.wireOp",EDGE,"E43.16.0.15")}),1.0]])]});
            var Q1261;
            Q1261=makeQuery(id+"F6.imprint","IMPRINT",FACE,{"disambiguationData":[TD([[makeQuery(id+"F6.imprint","IMPRINT",EDGE,{"derivedFrom":sQuery(id+"F6.wireOp",EDGE,"E43.15.0.6")}),1.0]])]});
            var Q1262;
            Q1262=makeQuery(id+"F6.imprint","IMPRINT",FACE,{"disambiguationData":[TD([[makeQuery(id+"F6.imprint","IMPRINT",EDGE,{"derivedFrom":sQuery(id+"F6.wireOp",EDGE,"E43.14.0.15")}),1.0]])]});
            var Q1263;
            Q1263=makeQuery(id+"F6.imprint","IMPRINT",FACE,{"disambiguationData":[TD([[makeQuery(id+"F6.imprint","IMPRINT",EDGE,{"derivedFrom":sQuery(id+"F6.wireOp",EDGE,"E43.17.0.6")}),1.0]])]});
            var Q1264;
            Q1264=makeQuery(id+"F6.imprint","IMPRINT",FACE,{"disambiguationData":[TD([[makeQuery(id+"F6.imprint","IMPRINT",EDGE,{"derivedFrom":sQuery(id+"F6.wireOp",EDGE,"E43.20.0.15")}),1.0]])]});
            var Q1265;
            Q1265=makeQuery(id+"F6.imprint","IMPRINT",FACE,{"disambiguationData":[TD([[makeQuery(id+"F6.imprint","IMPRINT",EDGE,{"derivedFrom":sQuery(id+"F6.wireOp",EDGE,"E43.19.0.6")}),1.0]])]});
            var Q1266;
            Q1266=makeQuery(id+"F6.imprint","IMPRINT",FACE,{"disambiguationData":[TD([[makeQuery(id+"F6.imprint","IMPRINT",EDGE,{"derivedFrom":sQuery(id+"F6.wireOp",EDGE,"E43.18.0.15")}),1.0]])]});
            var Q1267;
            Q1267=makeQuery(id+"F6.imprint","IMPRINT",FACE,{"disambiguationData":[TD([[makeQuery(id+"F6.imprint","IMPRINT",EDGE,{"derivedFrom":sQuery(id+"F6.wireOp",EDGE,"E43.23.0.6")}),1.0]])]});
            var Q1268;
            Q1268=makeQuery(id+"F6.imprint","IMPRINT",FACE,{"disambiguationData":[TD([[makeQuery(id+"F6.imprint","IMPRINT",EDGE,{"derivedFrom":sQuery(id+"F6.wireOp",EDGE,"E43.22.0.15")}),1.0]])]});
            var Q1269;
            Q1269=makeQuery(id+"F6.imprint","IMPRINT",FACE,{"disambiguationData":[TD([[makeQuery(id+"F6.imprint","IMPRINT",EDGE,{"derivedFrom":sQuery(id+"F6.wireOp",EDGE,"E43.21.0.6")}),1.0]])]});
            var Q1270;
            Q1270=makeQuery(id+"F6.imprint","IMPRINT",FACE,{"disambiguationData":[TD([[makeQuery(id+"F6.imprint","IMPRINT",EDGE,{"derivedFrom":sQuery(id+"F6.wireOp",EDGE,"E43.25.0.6")}),1.0]])]});
            var Q1271;
            Q1271=makeQuery(id+"F6.imprint","IMPRINT",FACE,{"disambiguationData":[TD([[makeQuery(id+"F6.imprint","IMPRINT",EDGE,{"derivedFrom":sQuery(id+"F6.wireOp",EDGE,"E43.24.0.15")}),1.0]])]});
            var Q1272;
            Q1272=makeQuery(id+"F6.imprint","IMPRINT",FACE,{"disambiguationData":[TD([[makeQuery(id+"F6.imprint","IMPRINT",EDGE,{"derivedFrom":sQuery(id+"F6.wireOp",EDGE,"E43.28.0.15")}),1.0]])]});
            var Q1273;
            Q1273=makeQuery(id+"F6.imprint","IMPRINT",FACE,{"disambiguationData":[TD([[makeQuery(id+"F6.imprint","IMPRINT",EDGE,{"derivedFrom":sQuery(id+"F6.wireOp",EDGE,"E43.27.0.6")}),1.0]])]});
            var Q1274;
            Q1274=makeQuery(id+"F6.imprint","IMPRINT",FACE,{"disambiguationData":[TD([[makeQuery(id+"F6.imprint","IMPRINT",EDGE,{"derivedFrom":sQuery(id+"F6.wireOp",EDGE,"E43.26.0.15")}),1.0]])]});
            var Q1275;
            Q1275=makeQuery(id+"F6.imprint","IMPRINT",FACE,{"disambiguationData":[TD([[makeQuery(id+"F6.imprint","IMPRINT",EDGE,{"derivedFrom":sQuery(id+"F6.wireOp",EDGE,"E245.MirrorC")}),-1.0]])]});
            var Q1276;
            Q1276=makeQuery(id+"F6.imprint","IMPRINT",FACE,{"disambiguationData":[TD([[makeQuery(id+"F6.imprint","IMPRINT",EDGE,{"derivedFrom":sQuery(id+"F6.wireOp",EDGE,"E306.MirrorC")}),-1.0]])]});
            var Q1277;
            Q1277=makeQuery(id+"F6.imprint","IMPRINT",FACE,{"disambiguationData":[TD([[makeQuery(id+"F6.imprint","IMPRINT",EDGE,{"derivedFrom":sQuery(id+"F6.wireOp",EDGE,"E290.MirrorC")}),-1.0]])]});
            var Q1278;
            Q1278=makeQuery(id+"F6.imprint","IMPRINT",FACE,{"disambiguationData":[TD([[makeQuery(id+"F6.imprint","IMPRINT",EDGE,{"derivedFrom":sQuery(id+"F6.wireOp",EDGE,"E274.MirrorC")}),-1.0]])]});
            var Q1279;
            Q1279=makeQuery(id+"F6.imprint","IMPRINT",FACE,{"disambiguationData":[TD([[makeQuery(id+"F6.imprint","IMPRINT",EDGE,{"derivedFrom":sQuery(id+"F6.wireOp",EDGE,"E260.MirrorC")}),-1.0]])]});
            var Q1280;
            Q1280=makeQuery(id+"F6.imprint","IMPRINT",FACE,{"disambiguationData":[TD([[makeQuery(id+"F6.imprint","IMPRINT",EDGE,{"derivedFrom":sQuery(id+"F6.wireOp",EDGE,"E43.3.0.6")}),1.0]])]});
            var Q1281;
            Q1281=makeQuery(id+"F6.imprint","IMPRINT",FACE,{"disambiguationData":[TD([[makeQuery(id+"F6.imprint","IMPRINT",EDGE,{"derivedFrom":sQuery(id+"F6.wireOp",EDGE,"E43.2.0.15")}),1.0]])]});
            var Q1282;
            Q1282=makeQuery(id+"F6.imprint","IMPRINT",FACE,{"disambiguationData":[TD([[makeQuery(id+"F6.imprint","IMPRINT",EDGE,{"derivedFrom":sQuery(id+"F6.wireOp",EDGE,"E43.1.0.6")}),1.0]])]});
            var Q1283;
            Q1283=makeQuery(id+"F6.imprint","IMPRINT",FACE,{"disambiguationData":[TD([[makeQuery(id+"F6.imprint","IMPRINT",EDGE,{"derivedFrom":sQuery(id+"F6.wireOp",EDGE,"E43.5.0.6")}),1.0]])]});
            var Q1284;
            Q1284=makeQuery(id+"F6.imprint","IMPRINT",FACE,{"disambiguationData":[TD([[makeQuery(id+"F6.imprint","IMPRINT",EDGE,{"derivedFrom":sQuery(id+"F6.wireOp",EDGE,"E43.4.0.15")}),1.0]])]});
            var Q1285;
            Q1285=makeQuery(id+"F6.imprint","IMPRINT",FACE,{"disambiguationData":[TD([[makeQuery(id+"F6.imprint","IMPRINT",EDGE,{"derivedFrom":sQuery(id+"F6.wireOp",EDGE,"E43.8.0.15")}),1.0]])]});
            var Q1286;
            Q1286=makeQuery(id+"F6.imprint","IMPRINT",FACE,{"disambiguationData":[TD([[makeQuery(id+"F6.imprint","IMPRINT",EDGE,{"derivedFrom":sQuery(id+"F6.wireOp",EDGE,"E43.7.0.6")}),1.0]])]});
            var Q1287;
            Q1287=makeQuery(id+"F6.imprint","IMPRINT",FACE,{"disambiguationData":[TD([[makeQuery(id+"F6.imprint","IMPRINT",EDGE,{"derivedFrom":sQuery(id+"F6.wireOp",EDGE,"E43.6.0.15")}),1.0]])]});
            var Q1288;
            Q1288=makeQuery(id+"F6.imprint","IMPRINT",FACE,{"disambiguationData":[TD([[makeQuery(id+"F6.imprint","IMPRINT",EDGE,{"derivedFrom":sQuery(id+"F6.wireOp",EDGE,"E43.11.0.6")}),1.0]])]});
            var Q1289;
            Q1289=makeQuery(id+"F6.imprint","IMPRINT",FACE,{"disambiguationData":[TD([[makeQuery(id+"F6.imprint","IMPRINT",EDGE,{"derivedFrom":sQuery(id+"F6.wireOp",EDGE,"E43.10.0.15")}),1.0]])]});
            var Q1290;
            Q1290=makeQuery(id+"F6.imprint","IMPRINT",FACE,{"disambiguationData":[TD([[makeQuery(id+"F6.imprint","IMPRINT",EDGE,{"derivedFrom":sQuery(id+"F6.wireOp",EDGE,"E43.9.0.6")}),1.0]])]});
            var Q1291;
            Q1291=makeQuery(id+"F6.imprint","IMPRINT",FACE,{"disambiguationData":[TD([[makeQuery(id+"F6.imprint","IMPRINT",EDGE,{"derivedFrom":sQuery(id+"F6.wireOp",EDGE,"E43.31.0.6")}),1.0]])]});
            var Q1292;
            Q1292=makeQuery(id+"F6.imprint","IMPRINT",FACE,{"disambiguationData":[TD([[makeQuery(id+"F6.imprint","IMPRINT",EDGE,{"derivedFrom":sQuery(id+"F6.wireOp",EDGE,"E43.30.0.15")}),1.0]])]});
            var Q1293;
            Q1293=makeQuery(id+"F6.imprint","IMPRINT",FACE,{"disambiguationData":[TD([[makeQuery(id+"F6.imprint","IMPRINT",EDGE,{"derivedFrom":sQuery(id+"F6.wireOp",EDGE,"E43.29.0.6")}),1.0]])]});
            var Q1294;
            Q1294=makeQuery(id+"F6.imprint","IMPRINT",FACE,{"disambiguationData":[TD([[makeQuery(id+"F6.imprint","IMPRINT",EDGE,{"derivedFrom":sQuery(id+"F6.wireOp",EDGE,"E43.32.0.15")}),1.0]])]});
            var Q1295;
            Q1295=makeQuery(id+"F6.imprint","IMPRINT",FACE,{"disambiguationData":[TD([[makeQuery(id+"F6.imprint","IMPRINT",EDGE,{"derivedFrom":sQuery(id+"F6.wireOp",EDGE,"E874.MirrorC")}),-1.0]])]});
            var Q1296;
            Q1296=makeQuery(id+"F6.imprint","IMPRINT",FACE,{"disambiguationData":[TD([[makeQuery(id+"F6.imprint","IMPRINT",EDGE,{"derivedFrom":sQuery(id+"F6.wireOp",EDGE,"E855.MirrorC")}),-1.0]])]});
            var Q1297;
            Q1297=makeQuery(id+"F6.imprint","IMPRINT",FACE,{"disambiguationData":[TD([[makeQuery(id+"F6.imprint","IMPRINT",EDGE,{"derivedFrom":sQuery(id+"F6.wireOp",EDGE,"E889.MirrorC")}),-1.0]])]});
            var Q1298;
            Q1298=makeQuery(id+"F6.imprint","IMPRINT",FACE,{"disambiguationData":[TD([[makeQuery(id+"F6.imprint","IMPRINT",EDGE,{"derivedFrom":sQuery(id+"F6.wireOp",EDGE,"E871.MirrorC")}),-1.0]])]});
            var Q1299;
            Q1299=makeQuery(id+"F6.imprint","IMPRINT",FACE,{"disambiguationData":[TD([[makeQuery(id+"F6.imprint","IMPRINT",EDGE,{"derivedFrom":sQuery(id+"F6.wireOp",EDGE,"E843.MirrorC")}),-1.0]])]});
            var Q1300;
            Q1300=makeQuery(id+"F6.imprint","IMPRINT",FACE,{"disambiguationData":[TD([[makeQuery(id+"F6.imprint","IMPRINT",EDGE,{"derivedFrom":sQuery(id+"F6.wireOp",EDGE,"E896.MirrorC")}),-1.0]])]});
            var Q1301;
            Q1301=makeQuery(id+"F6.imprint","IMPRINT",FACE,{"disambiguationData":[TD([[makeQuery(id+"F6.imprint","IMPRINT",EDGE,{"derivedFrom":sQuery(id+"F6.wireOp",EDGE,"E727.MirrorC")}),-1.0]])]});
            var Q1302;
            Q1302=makeQuery(id+"F6.imprint","IMPRINT",FACE,{"disambiguationData":[TD([[makeQuery(id+"F6.imprint","IMPRINT",EDGE,{"derivedFrom":sQuery(id+"F6.wireOp",EDGE,"E825.MirrorC")}),-1.0]])]});
            var Q1303;
            Q1303=makeQuery(id+"F6.imprint","IMPRINT",FACE,{"disambiguationData":[TD([[makeQuery(id+"F6.imprint","IMPRINT",EDGE,{"derivedFrom":sQuery(id+"F6.wireOp",EDGE,"E858.MirrorC")}),-1.0]])]});
            var Q1304;
            Q1304=makeQuery(id+"F6.imprint","IMPRINT",FACE,{"disambiguationData":[TD([[makeQuery(id+"F6.imprint","IMPRINT",EDGE,{"derivedFrom":sQuery(id+"F6.wireOp",EDGE,"E840.MirrorC")}),-1.0]])]});
            var Q1305;
            Q1305=makeQuery(id+"F6.imprint","IMPRINT",FACE,{"disambiguationData":[TD([[makeQuery(id+"F6.imprint","IMPRINT",EDGE,{"derivedFrom":sQuery(id+"F6.wireOp",EDGE,"E742.MirrorC")}),-1.0]])]});
            var Q1306;
            Q1306=makeQuery(id+"F6.imprint","IMPRINT",FACE,{"disambiguationData":[TD([[makeQuery(id+"F6.imprint","IMPRINT",EDGE,{"derivedFrom":sQuery(id+"F6.wireOp",EDGE,"E757.MirrorC")}),-1.0]])]});
            var Q1307;
            Q1307=makeQuery(id+"F6.imprint","IMPRINT",FACE,{"disambiguationData":[TD([[makeQuery(id+"F6.imprint","IMPRINT",EDGE,{"derivedFrom":sQuery(id+"F6.wireOp",EDGE,"E886.MirrorC")}),-1.0]])]});
            var Q1308;
            Q1308=makeQuery(id+"F6.imprint","IMPRINT",FACE,{"disambiguationData":[TD([[makeQuery(id+"F6.imprint","IMPRINT",EDGE,{"derivedFrom":sQuery(id+"F6.wireOp",EDGE,"E902.MirrorC")}),-1.0]])]});
            var Q1309;
            Q1309=makeQuery(id+"F6.imprint","IMPRINT",FACE,{"disambiguationData":[TD([[makeQuery(id+"F6.imprint","IMPRINT",EDGE,{"derivedFrom":sQuery(id+"F6.wireOp",EDGE,"E803.MirrorC")}),-1.0]])]});
            var Q1310;
            Q1310=makeQuery(id+"F6.imprint","IMPRINT",FACE,{"disambiguationData":[TD([[makeQuery(id+"F6.imprint","IMPRINT",EDGE,{"derivedFrom":sQuery(id+"F6.wireOp",EDGE,"E818.MirrorC")}),-1.0]])]});
            var Q1311;
            Q1311=makeQuery(id+"F6.imprint","IMPRINT",FACE,{"disambiguationData":[TD([[makeQuery(id+"F6.imprint","IMPRINT",EDGE,{"derivedFrom":sQuery(id+"F6.wireOp",EDGE,"E773.MirrorC")}),-1.0]])]});
            var Q1312;
            Q1312=makeQuery(id+"F6.imprint","IMPRINT",FACE,{"disambiguationData":[TD([[makeQuery(id+"F6.imprint","IMPRINT",EDGE,{"derivedFrom":sQuery(id+"F6.wireOp",EDGE,"E788.MirrorC")}),-1.0]])]});
            var Q1313;
            Q1313=makeQuery(id+"F6.imprint","IMPRINT",FACE,{"disambiguationData":[TD([[makeQuery(id+"F6.imprint","IMPRINT",EDGE,{"derivedFrom":sQuery(id+"F6.wireOp",EDGE,"E863.MirrorC")}),-1.0]])]});
            var Q1314;
            Q1314=makeQuery(id+"F6.imprint","IMPRINT",FACE,{"disambiguationData":[TD([[makeQuery(id+"F6.imprint","IMPRINT",EDGE,{"derivedFrom":sQuery(id+"F6.wireOp",EDGE,"E878.MirrorC")}),-1.0]])]});
            var Q1315;
            Q1315=makeQuery(id+"F6.imprint","IMPRINT",FACE,{"disambiguationData":[TD([[makeQuery(id+"F6.imprint","IMPRINT",EDGE,{"derivedFrom":sQuery(id+"F6.wireOp",EDGE,"E832.MirrorC")}),-1.0]])]});
            var Q1316;
            Q1316=makeQuery(id+"F6.imprint","IMPRINT",FACE,{"disambiguationData":[TD([[makeQuery(id+"F6.imprint","IMPRINT",EDGE,{"derivedFrom":sQuery(id+"F6.wireOp",EDGE,"E848.MirrorC")}),-1.0]])]});
            var Q1317;
            Q1317=makeQuery(id+"F6.imprint","IMPRINT",FACE,{"disambiguationData":[TD([[makeQuery(id+"F6.imprint","IMPRINT",EDGE,{"derivedFrom":sQuery(id+"F6.wireOp",EDGE,"E894.MirrorC")}),-1.0]])]});
            var Q1318;
            Q1318=makeQuery(id+"F6.imprint","IMPRINT",FACE,{"disambiguationData":[TD([[makeQuery(id+"F6.imprint","IMPRINT",EDGE,{"derivedFrom":sQuery(id+"F6.wireOp",EDGE,"E42.0.3.0")}),1.0]])]});
            var Q1319;
            Q1319=makeQuery(id+"F6.imprint","IMPRINT",FACE,{"disambiguationData":[TD([[makeQuery(id+"F6.imprint","IMPRINT",EDGE,{"derivedFrom":sQuery(id+"F6.wireOp",EDGE,"E42.0.2.0")}),1.0]])]});
            var Q1320;
            Q1320=makeQuery(id+"F6.imprint","IMPRINT",FACE,{"disambiguationData":[TD([[makeQuery(id+"F6.imprint","IMPRINT",EDGE,{"derivedFrom":sQuery(id+"F6.wireOp",EDGE,"E43.3.0.26")}),1.0]])]});
            var Q1321;
            Q1321=makeQuery(id+"F6.imprint","IMPRINT",FACE,{"disambiguationData":[TD([[makeQuery(id+"F6.imprint","IMPRINT",EDGE,{"derivedFrom":sQuery(id+"F6.wireOp",EDGE,"E43.5.0.26")}),1.0]])]});
            var Q1322;
            Q1322=makeQuery(id+"F6.imprint","IMPRINT",FACE,{"disambiguationData":[TD([[makeQuery(id+"F6.imprint","IMPRINT",EDGE,{"derivedFrom":sQuery(id+"F6.wireOp",EDGE,"E43.9.0.26")}),1.0]])]});
            var Q1323;
            Q1323=makeQuery(id+"F6.imprint","IMPRINT",FACE,{"disambiguationData":[TD([[makeQuery(id+"F6.imprint","IMPRINT",EDGE,{"derivedFrom":sQuery(id+"F6.wireOp",EDGE,"E43.7.0.26")}),1.0]])]});
            var Q1324;
            Q1324=makeQuery(id+"F6.imprint","IMPRINT",FACE,{"disambiguationData":[TD([[makeQuery(id+"F6.imprint","IMPRINT",EDGE,{"derivedFrom":sQuery(id+"F6.wireOp",EDGE,"E43.11.0.26")}),1.0]])]});
            var Q1325;
            Q1325=makeQuery(id+"F6.imprint","IMPRINT",FACE,{"disambiguationData":[TD([[makeQuery(id+"F6.imprint","IMPRINT",EDGE,{"derivedFrom":sQuery(id+"F6.wireOp",EDGE,"E43.13.0.26")}),1.0]])]});
            var Q1326;
            Q1326=makeQuery(id+"F6.imprint","IMPRINT",FACE,{"disambiguationData":[TD([[makeQuery(id+"F6.imprint","IMPRINT",EDGE,{"derivedFrom":sQuery(id+"F6.wireOp",EDGE,"E43.15.0.26")}),1.0]])]});
            var Q1327;
            Q1327=makeQuery(id+"F6.imprint","IMPRINT",FACE,{"disambiguationData":[TD([[makeQuery(id+"F6.imprint","IMPRINT",EDGE,{"derivedFrom":sQuery(id+"F6.wireOp",EDGE,"E43.17.0.26")}),1.0]])]});
            var Q1328;
            Q1328=makeQuery(id+"F6.imprint","IMPRINT",FACE,{"disambiguationData":[TD([[makeQuery(id+"F6.imprint","IMPRINT",EDGE,{"derivedFrom":sQuery(id+"F6.wireOp",EDGE,"E200.MirrorC")}),-1.0]])]});
            var Q1329;
            Q1329=makeQuery(id+"F6.imprint","IMPRINT",FACE,{"disambiguationData":[TD([[makeQuery(id+"F6.imprint","IMPRINT",EDGE,{"derivedFrom":sQuery(id+"F6.wireOp",EDGE,"E175.MirrorC")}),-1.0]])]});
            var Q1330;
            Q1330=makeQuery(id+"F6.imprint","IMPRINT",FACE,{"disambiguationData":[TD([[makeQuery(id+"F6.imprint","IMPRINT",EDGE,{"derivedFrom":sQuery(id+"F6.wireOp",EDGE,"E151.MirrorC")}),-1.0]])]});
            var Q1331;
            Q1331=makeQuery(id+"F6.imprint","IMPRINT",FACE,{"disambiguationData":[TD([[makeQuery(id+"F6.imprint","IMPRINT",EDGE,{"derivedFrom":sQuery(id+"F6.wireOp",EDGE,"E126.MirrorC")}),-1.0]])]});
            var Q1332;
            Q1332=makeQuery(id+"F6.imprint","IMPRINT",FACE,{"disambiguationData":[TD([[makeQuery(id+"F6.imprint","IMPRINT",EDGE,{"derivedFrom":sQuery(id+"F6.wireOp",EDGE,"E224.MirrorC")}),-1.0]])]});
            var Q1333;
            Q1333=makeQuery(id+"F6.imprint","IMPRINT",FACE,{"disambiguationData":[TD([[makeQuery(id+"F6.imprint","IMPRINT",EDGE,{"derivedFrom":sQuery(id+"F6.wireOp",EDGE,"E43.1.0.26")}),1.0]])]});
            var Q1334;
            Q1334=makeQuery(id+"F6.imprint","IMPRINT",FACE,{"disambiguationData":[TD([[makeQuery(id+"F6.imprint","IMPRINT",EDGE,{"derivedFrom":sQuery(id+"F6.wireOp",EDGE,"E43.21.0.26")}),1.0]])]});
            var Q1335;
            Q1335=makeQuery(id+"F6.imprint","IMPRINT",FACE,{"disambiguationData":[TD([[makeQuery(id+"F6.imprint","IMPRINT",EDGE,{"derivedFrom":sQuery(id+"F6.wireOp",EDGE,"E43.19.0.26")}),1.0]])]});
            var Q1336;
            Q1336=makeQuery(id+"F6.imprint","IMPRINT",FACE,{"disambiguationData":[TD([[makeQuery(id+"F6.imprint","IMPRINT",EDGE,{"derivedFrom":sQuery(id+"F6.wireOp",EDGE,"E43.23.0.26")}),1.0]])]});
            var Q1337;
            Q1337=makeQuery(id+"F6.imprint","IMPRINT",FACE,{"disambiguationData":[TD([[makeQuery(id+"F6.imprint","IMPRINT",EDGE,{"derivedFrom":sQuery(id+"F6.wireOp",EDGE,"E43.25.0.26")}),1.0]])]});
            var Q1338;
            Q1338=makeQuery(id+"F6.imprint","IMPRINT",FACE,{"disambiguationData":[TD([[makeQuery(id+"F6.imprint","IMPRINT",EDGE,{"derivedFrom":sQuery(id+"F6.wireOp",EDGE,"E43.29.0.26")}),1.0]])]});
            var Q1339;
            Q1339=makeQuery(id+"F6.imprint","IMPRINT",FACE,{"disambiguationData":[TD([[makeQuery(id+"F6.imprint","IMPRINT",EDGE,{"derivedFrom":sQuery(id+"F6.wireOp",EDGE,"E43.27.0.26")}),1.0]])]});
            var Q1340;
            Q1340=makeQuery(id+"F6.imprint","IMPRINT",FACE,{"disambiguationData":[TD([[makeQuery(id+"F6.imprint","IMPRINT",EDGE,{"derivedFrom":sQuery(id+"F6.wireOp",EDGE,"E43.31.0.26")}),1.0]])]});
            var Q1341;
            Q1341=makeQuery(id+"F6.imprint","IMPRINT",FACE,{"disambiguationData":[TD([[makeQuery(id+"F6.imprint","IMPRINT",EDGE,{"derivedFrom":sQuery(id+"F6.wireOp",EDGE,"E106.MirrorC")}),-1.0]])]});
            var Q1342;
            Q1342=makeQuery(id+"F6.imprint","IMPRINT",FACE,{"disambiguationData":[TD([[makeQuery(id+"F6.imprint","IMPRINT",EDGE,{"derivedFrom":sQuery(id+"F6.wireOp",EDGE,"E81.MirrorC")}),-1.0]])]});
            var Q1343;
            Q1343=makeQuery(id+"F6.imprint","IMPRINT",FACE,{"disambiguationData":[TD([[makeQuery(id+"F6.imprint","IMPRINT",EDGE,{"derivedFrom":sQuery(id+"F6.wireOp",EDGE,"E55.MirrorC")}),-1.0]])]});
            var Q1344;
            Q1344=makeQuery(id+"F6.imprint","IMPRINT",FACE,{"disambiguationData":[TD([[makeQuery(id+"F6.imprint","IMPRINT",EDGE,{"derivedFrom":sQuery(id+"F6.wireOp",EDGE,"E173.MirrorC")}),-1.0]])]});
            var Q1345;
            Q1345=makeQuery(id+"F6.imprint","IMPRINT",FACE,{"disambiguationData":[TD([[makeQuery(id+"F6.imprint","IMPRINT",EDGE,{"derivedFrom":sQuery(id+"F6.wireOp",EDGE,"E149.MirrorC")}),-1.0]])]});
            var Q1346;
            Q1346=makeQuery(id+"F6.imprint","IMPRINT",FACE,{"disambiguationData":[TD([[makeQuery(id+"F6.imprint","IMPRINT",EDGE,{"derivedFrom":sQuery(id+"F6.wireOp",EDGE,"E124.MirrorC")}),-1.0]])]});
            var Q1347;
            Q1347=makeQuery(id+"F6.imprint","IMPRINT",FACE,{"disambiguationData":[TD([[makeQuery(id+"F6.imprint","IMPRINT",EDGE,{"derivedFrom":sQuery(id+"F6.wireOp",EDGE,"E222.MirrorC")}),-1.0]])]});
            var Q1348;
            Q1348=makeQuery(id+"F6.imprint","IMPRINT",FACE,{"disambiguationData":[TD([[makeQuery(id+"F6.imprint","IMPRINT",EDGE,{"derivedFrom":sQuery(id+"F6.wireOp",EDGE,"E198.MirrorC")}),-1.0]])]});
            var Q1349;
            Q1349=makeQuery(id+"F6.imprint","IMPRINT",FACE,{"disambiguationData":[TD([[makeQuery(id+"F6.imprint","IMPRINT",EDGE,{"derivedFrom":sQuery(id+"F6.wireOp",EDGE,"E43.3.0.24")}),1.0]])]});
            var Q1350;
            Q1350=makeQuery(id+"F6.imprint","IMPRINT",FACE,{"disambiguationData":[TD([[makeQuery(id+"F6.imprint","IMPRINT",EDGE,{"derivedFrom":sQuery(id+"F6.wireOp",EDGE,"E43.1.0.24")}),1.0]])]});
            var Q1351;
            Q1351=makeQuery(id+"F6.imprint","IMPRINT",FACE,{"disambiguationData":[TD([[makeQuery(id+"F6.imprint","IMPRINT",EDGE,{"derivedFrom":sQuery(id+"F6.wireOp",EDGE,"E43.5.0.24")}),1.0]])]});
            var Q1352;
            Q1352=makeQuery(id+"F6.imprint","IMPRINT",FACE,{"disambiguationData":[TD([[makeQuery(id+"F6.imprint","IMPRINT",EDGE,{"derivedFrom":sQuery(id+"F6.wireOp",EDGE,"E43.25.0.24")}),1.0]])]});
            var Q1353;
            Q1353=makeQuery(id+"F6.imprint","IMPRINT",FACE,{"disambiguationData":[TD([[makeQuery(id+"F6.imprint","IMPRINT",EDGE,{"derivedFrom":sQuery(id+"F6.wireOp",EDGE,"E43.27.0.24")}),1.0]])]});
            var Q1354;
            Q1354=makeQuery(id+"F6.imprint","IMPRINT",FACE,{"disambiguationData":[TD([[makeQuery(id+"F6.imprint","IMPRINT",EDGE,{"derivedFrom":sQuery(id+"F6.wireOp",EDGE,"E43.31.0.24")}),1.0]])]});
            var Q1355;
            Q1355=makeQuery(id+"F6.imprint","IMPRINT",FACE,{"disambiguationData":[TD([[makeQuery(id+"F6.imprint","IMPRINT",EDGE,{"derivedFrom":sQuery(id+"F6.wireOp",EDGE,"E43.29.0.24")}),1.0]])]});
            var Q1356;
            Q1356=makeQuery(id+"F6.imprint","IMPRINT",FACE,{"disambiguationData":[TD([[makeQuery(id+"F6.imprint","IMPRINT",EDGE,{"derivedFrom":sQuery(id+"F6.wireOp",EDGE,"E102.MirrorC")}),-1.0]])]});
            var Q1357;
            Q1357=makeQuery(id+"F6.imprint","IMPRINT",FACE,{"disambiguationData":[TD([[makeQuery(id+"F6.imprint","IMPRINT",EDGE,{"derivedFrom":sQuery(id+"F6.wireOp",EDGE,"E77.MirrorC")}),-1.0]])]});
            var Q1358;
            Q1358=makeQuery(id+"F6.imprint","IMPRINT",FACE,{"disambiguationData":[TD([[makeQuery(id+"F6.imprint","IMPRINT",EDGE,{"derivedFrom":sQuery(id+"F6.wireOp",EDGE,"E53.MirrorC")}),-1.0]])]});
            var Q1359;
            Q1359=makeQuery(id+"F6.imprint","IMPRINT",FACE,{"disambiguationData":[TD([[makeQuery(id+"F6.imprint","IMPRINT",EDGE,{"derivedFrom":sQuery(id+"F6.wireOp",EDGE,"E43.7.0.24")}),1.0]])]});
            var Q1360;
            Q1360=makeQuery(id+"F6.imprint","IMPRINT",FACE,{"disambiguationData":[TD([[makeQuery(id+"F6.imprint","IMPRINT",EDGE,{"derivedFrom":sQuery(id+"F6.wireOp",EDGE,"E43.11.0.24")}),1.0]])]});
            var Q1361;
            Q1361=makeQuery(id+"F6.imprint","IMPRINT",FACE,{"disambiguationData":[TD([[makeQuery(id+"F6.imprint","IMPRINT",EDGE,{"derivedFrom":sQuery(id+"F6.wireOp",EDGE,"E43.9.0.24")}),1.0]])]});
            var Q1362;
            Q1362=makeQuery(id+"F6.imprint","IMPRINT",FACE,{"disambiguationData":[TD([[makeQuery(id+"F6.imprint","IMPRINT",EDGE,{"derivedFrom":sQuery(id+"F6.wireOp",EDGE,"E43.13.0.24")}),1.0]])]});
            var Q1363;
            Q1363=makeQuery(id+"F6.imprint","IMPRINT",FACE,{"disambiguationData":[TD([[makeQuery(id+"F6.imprint","IMPRINT",EDGE,{"derivedFrom":sQuery(id+"F6.wireOp",EDGE,"E43.15.0.24")}),1.0]])]});
            var Q1364;
            Q1364=makeQuery(id+"F6.imprint","IMPRINT",FACE,{"disambiguationData":[TD([[makeQuery(id+"F6.imprint","IMPRINT",EDGE,{"derivedFrom":sQuery(id+"F6.wireOp",EDGE,"E43.17.0.24")}),1.0]])]});
            var Q1365;
            Q1365=makeQuery(id+"F6.imprint","IMPRINT",FACE,{"disambiguationData":[TD([[makeQuery(id+"F6.imprint","IMPRINT",EDGE,{"derivedFrom":sQuery(id+"F6.wireOp",EDGE,"E43.19.0.24")}),1.0]])]});
            var Q1366;
            Q1366=makeQuery(id+"F6.imprint","IMPRINT",FACE,{"disambiguationData":[TD([[makeQuery(id+"F6.imprint","IMPRINT",EDGE,{"derivedFrom":sQuery(id+"F6.wireOp",EDGE,"E43.23.0.24")}),1.0]])]});
            var Q1367;
            Q1367=makeQuery(id+"F6.imprint","IMPRINT",FACE,{"disambiguationData":[TD([[makeQuery(id+"F6.imprint","IMPRINT",EDGE,{"derivedFrom":sQuery(id+"F6.wireOp",EDGE,"E43.21.0.24")}),1.0]])]});
            var Q1368;
            Q1368=makeQuery(id+"F6.imprint","IMPRINT",FACE,{"disambiguationData":[TD([[makeQuery(id+"F6.imprint","IMPRINT",EDGE,{"derivedFrom":sQuery(id+"F6.wireOp",EDGE,"E174.MirrorC")}),-1.0]])]});
            var Q1369;
            Q1369=makeQuery(id+"F6.imprint","IMPRINT",FACE,{"disambiguationData":[TD([[makeQuery(id+"F6.imprint","IMPRINT",EDGE,{"derivedFrom":sQuery(id+"F6.wireOp",EDGE,"E150.MirrorC")}),-1.0]])]});
            var Q1370;
            Q1370=makeQuery(id+"F6.imprint","IMPRINT",FACE,{"disambiguationData":[TD([[makeQuery(id+"F6.imprint","IMPRINT",EDGE,{"derivedFrom":sQuery(id+"F6.wireOp",EDGE,"E125.MirrorC")}),-1.0]])]});
            var Q1371;
            Q1371=makeQuery(id+"F6.imprint","IMPRINT",FACE,{"disambiguationData":[TD([[makeQuery(id+"F6.imprint","IMPRINT",EDGE,{"derivedFrom":sQuery(id+"F6.wireOp",EDGE,"E223.MirrorC")}),-1.0]])]});
            var Q1372;
            Q1372=makeQuery(id+"F6.imprint","IMPRINT",FACE,{"disambiguationData":[TD([[makeQuery(id+"F6.imprint","IMPRINT",EDGE,{"derivedFrom":sQuery(id+"F6.wireOp",EDGE,"E199.MirrorC")}),-1.0]])]});
            var Q1373;
            Q1373=makeQuery(id+"F6.imprint","IMPRINT",FACE,{"disambiguationData":[TD([[makeQuery(id+"F6.imprint","IMPRINT",EDGE,{"derivedFrom":sQuery(id+"F6.wireOp",EDGE,"E43.3.0.25")}),1.0]])]});
            var Q1374;
            Q1374=makeQuery(id+"F6.imprint","IMPRINT",FACE,{"disambiguationData":[TD([[makeQuery(id+"F6.imprint","IMPRINT",EDGE,{"derivedFrom":sQuery(id+"F6.wireOp",EDGE,"E43.5.0.25")}),1.0]])]});
            var Q1375;
            Q1375=makeQuery(id+"F6.imprint","IMPRINT",FACE,{"disambiguationData":[TD([[makeQuery(id+"F6.imprint","IMPRINT",EDGE,{"derivedFrom":sQuery(id+"F6.wireOp",EDGE,"E43.7.0.25")}),1.0]])]});
            var Q1376;
            Q1376=makeQuery(id+"F6.imprint","IMPRINT",FACE,{"disambiguationData":[TD([[makeQuery(id+"F6.imprint","IMPRINT",EDGE,{"derivedFrom":sQuery(id+"F6.wireOp",EDGE,"E43.27.0.25")}),1.0]])]});
            var Q1377;
            Q1377=makeQuery(id+"F6.imprint","IMPRINT",FACE,{"disambiguationData":[TD([[makeQuery(id+"F6.imprint","IMPRINT",EDGE,{"derivedFrom":sQuery(id+"F6.wireOp",EDGE,"E43.31.0.25")}),1.0]])]});
            var Q1378;
            Q1378=makeQuery(id+"F6.imprint","IMPRINT",FACE,{"disambiguationData":[TD([[makeQuery(id+"F6.imprint","IMPRINT",EDGE,{"derivedFrom":sQuery(id+"F6.wireOp",EDGE,"E43.29.0.25")}),1.0]])]});
            var Q1379;
            Q1379=makeQuery(id+"F6.imprint","IMPRINT",FACE,{"disambiguationData":[TD([[makeQuery(id+"F6.imprint","IMPRINT",EDGE,{"derivedFrom":sQuery(id+"F6.wireOp",EDGE,"E103.MirrorC")}),-1.0]])]});
            var Q1380;
            Q1380=makeQuery(id+"F6.imprint","IMPRINT",FACE,{"disambiguationData":[TD([[makeQuery(id+"F6.imprint","IMPRINT",EDGE,{"derivedFrom":sQuery(id+"F6.wireOp",EDGE,"E80.MirrorC")}),-1.0]])]});
            var Q1381;
            Q1381=makeQuery(id+"F6.imprint","IMPRINT",FACE,{"disambiguationData":[TD([[makeQuery(id+"F6.imprint","IMPRINT",EDGE,{"derivedFrom":sQuery(id+"F6.wireOp",EDGE,"E54.MirrorC")}),-1.0]])]});
            var Q1382;
            Q1382=makeQuery(id+"F6.imprint","IMPRINT",FACE,{"disambiguationData":[TD([[makeQuery(id+"F6.imprint","IMPRINT",EDGE,{"derivedFrom":sQuery(id+"F6.wireOp",EDGE,"E43.11.0.25")}),1.0]])]});
            var Q1383;
            Q1383=makeQuery(id+"F6.imprint","IMPRINT",FACE,{"disambiguationData":[TD([[makeQuery(id+"F6.imprint","IMPRINT",EDGE,{"derivedFrom":sQuery(id+"F6.wireOp",EDGE,"E43.9.0.25")}),1.0]])]});
            var Q1384;
            Q1384=makeQuery(id+"F6.imprint","IMPRINT",FACE,{"disambiguationData":[TD([[makeQuery(id+"F6.imprint","IMPRINT",EDGE,{"derivedFrom":sQuery(id+"F6.wireOp",EDGE,"E43.13.0.25")}),1.0]])]});
            var Q1385;
            Q1385=makeQuery(id+"F6.imprint","IMPRINT",FACE,{"disambiguationData":[TD([[makeQuery(id+"F6.imprint","IMPRINT",EDGE,{"derivedFrom":sQuery(id+"F6.wireOp",EDGE,"E43.15.0.25")}),1.0]])]});
            var Q1386;
            Q1386=makeQuery(id+"F6.imprint","IMPRINT",FACE,{"disambiguationData":[TD([[makeQuery(id+"F6.imprint","IMPRINT",EDGE,{"derivedFrom":sQuery(id+"F6.wireOp",EDGE,"E43.17.0.25")}),1.0]])]});
            var Q1387;
            Q1387=makeQuery(id+"F6.imprint","IMPRINT",FACE,{"disambiguationData":[TD([[makeQuery(id+"F6.imprint","IMPRINT",EDGE,{"derivedFrom":sQuery(id+"F6.wireOp",EDGE,"E43.19.0.25")}),1.0]])]});
            var Q1388;
            Q1388=makeQuery(id+"F6.imprint","IMPRINT",FACE,{"disambiguationData":[TD([[makeQuery(id+"F6.imprint","IMPRINT",EDGE,{"derivedFrom":sQuery(id+"F6.wireOp",EDGE,"E43.23.0.25")}),1.0]])]});
            var Q1389;
            Q1389=makeQuery(id+"F6.imprint","IMPRINT",FACE,{"disambiguationData":[TD([[makeQuery(id+"F6.imprint","IMPRINT",EDGE,{"derivedFrom":sQuery(id+"F6.wireOp",EDGE,"E43.21.0.25")}),1.0]])]});
            var Q1390;
            Q1390=makeQuery(id+"F6.imprint","IMPRINT",FACE,{"disambiguationData":[TD([[makeQuery(id+"F6.imprint","IMPRINT",EDGE,{"derivedFrom":sQuery(id+"F6.wireOp",EDGE,"E43.25.0.25")}),1.0]])]});
            var Q1391;
            Q1391=makeQuery(id+"F6.imprint","IMPRINT",FACE,{"disambiguationData":[TD([[makeQuery(id+"F6.imprint","IMPRINT",EDGE,{"derivedFrom":sQuery(id+"F6.wireOp",EDGE,"E176.MirrorC")}),-1.0]])]});
            var Q1392;
            Q1392=makeQuery(id+"F6.imprint","IMPRINT",FACE,{"disambiguationData":[TD([[makeQuery(id+"F6.imprint","IMPRINT",EDGE,{"derivedFrom":sQuery(id+"F6.wireOp",EDGE,"E152.MirrorC")}),-1.0]])]});
            var Q1393;
            Q1393=makeQuery(id+"F6.imprint","IMPRINT",FACE,{"disambiguationData":[TD([[makeQuery(id+"F6.imprint","IMPRINT",EDGE,{"derivedFrom":sQuery(id+"F6.wireOp",EDGE,"E127.MirrorC")}),-1.0]])]});
            var Q1394;
            Q1394=makeQuery(id+"F6.imprint","IMPRINT",FACE,{"disambiguationData":[TD([[makeQuery(id+"F6.imprint","IMPRINT",EDGE,{"derivedFrom":sQuery(id+"F6.wireOp",EDGE,"E107.MirrorC")}),-1.0]])]});
            var Q1395;
            Q1395=makeQuery(id+"F6.imprint","IMPRINT",FACE,{"disambiguationData":[TD([[makeQuery(id+"F6.imprint","IMPRINT",EDGE,{"derivedFrom":sQuery(id+"F6.wireOp",EDGE,"E225.MirrorC")}),-1.0]])]});
            var Q1396;
            Q1396=makeQuery(id+"F6.imprint","IMPRINT",FACE,{"disambiguationData":[TD([[makeQuery(id+"F6.imprint","IMPRINT",EDGE,{"derivedFrom":sQuery(id+"F6.wireOp",EDGE,"E201.MirrorC")}),-1.0]])]});
            var Q1397;
            Q1397=makeQuery(id+"F6.imprint","IMPRINT",FACE,{"disambiguationData":[TD([[makeQuery(id+"F6.imprint","IMPRINT",EDGE,{"derivedFrom":sQuery(id+"F6.wireOp",EDGE,"E82.MirrorC")}),-1.0]])]});
            var Q1398;
            Q1398=makeQuery(id+"F6.imprint","IMPRINT",FACE,{"disambiguationData":[TD([[makeQuery(id+"F6.imprint","IMPRINT",EDGE,{"derivedFrom":sQuery(id+"F6.wireOp",EDGE,"E56.MirrorC")}),-1.0]])]});
            var Q1399;
            Q1399=makeQuery(id+"F6.imprint","IMPRINT",FACE,{"disambiguationData":[TD([[makeQuery(id+"F6.imprint","IMPRINT",EDGE,{"derivedFrom":sQuery(id+"F6.wireOp",EDGE,"E177.MirrorC")}),-1.0]])]});
            var Q1400;
            Q1400=makeQuery(id+"F6.imprint","IMPRINT",FACE,{"disambiguationData":[TD([[makeQuery(id+"F6.imprint","IMPRINT",EDGE,{"derivedFrom":sQuery(id+"F6.wireOp",EDGE,"E153.MirrorC")}),-1.0]])]});
            var Q1401;
            Q1401=makeQuery(id+"F6.imprint","IMPRINT",FACE,{"disambiguationData":[TD([[makeQuery(id+"F6.imprint","IMPRINT",EDGE,{"derivedFrom":sQuery(id+"F6.wireOp",EDGE,"E128.MirrorC")}),-1.0]])]});
            var Q1402;
            Q1402=makeQuery(id+"F6.imprint","IMPRINT",FACE,{"disambiguationData":[TD([[makeQuery(id+"F6.imprint","IMPRINT",EDGE,{"derivedFrom":sQuery(id+"F6.wireOp",EDGE,"E108.MirrorC")}),-1.0]])]});
            var Q1403;
            Q1403=makeQuery(id+"F6.imprint","IMPRINT",FACE,{"disambiguationData":[TD([[makeQuery(id+"F6.imprint","IMPRINT",EDGE,{"derivedFrom":sQuery(id+"F6.wireOp",EDGE,"E227.MirrorC")}),-1.0]])]});
            var Q1404;
            Q1404=makeQuery(id+"F6.imprint","IMPRINT",FACE,{"disambiguationData":[TD([[makeQuery(id+"F6.imprint","IMPRINT",EDGE,{"derivedFrom":sQuery(id+"F6.wireOp",EDGE,"E204.MirrorC")}),-1.0]])]});
            var Q1405;
            Q1405=makeQuery(id+"F6.imprint","IMPRINT",FACE,{"disambiguationData":[TD([[makeQuery(id+"F6.imprint","IMPRINT",EDGE,{"derivedFrom":sQuery(id+"F6.wireOp",EDGE,"E83.MirrorC")}),-1.0]])]});
            var Q1406;
            Q1406=makeQuery(id+"F6.imprint","IMPRINT",FACE,{"disambiguationData":[TD([[makeQuery(id+"F6.imprint","IMPRINT",EDGE,{"derivedFrom":sQuery(id+"F6.wireOp",EDGE,"E60.MirrorC")}),-1.0]])]});
            var Q1407;
            Q1407=makeQuery(id+"F6.imprint","IMPRINT",FACE,{"disambiguationData":[TD([[makeQuery(id+"F6.imprint","IMPRINT",EDGE,{"derivedFrom":sQuery(id+"F6.wireOp",EDGE,"E181.MirrorC")}),-1.0]])]});
            var Q1408;
            Q1408=makeQuery(id+"F6.imprint","IMPRINT",FACE,{"disambiguationData":[TD([[makeQuery(id+"F6.imprint","IMPRINT",EDGE,{"derivedFrom":sQuery(id+"F6.wireOp",EDGE,"E156.MirrorC")}),-1.0]])]});
            var Q1409;
            Q1409=makeQuery(id+"F6.imprint","IMPRINT",FACE,{"disambiguationData":[TD([[makeQuery(id+"F6.imprint","IMPRINT",EDGE,{"derivedFrom":sQuery(id+"F6.wireOp",EDGE,"E134.MirrorC")}),-1.0]])]});
            var Q1410;
            Q1410=makeQuery(id+"F6.imprint","IMPRINT",FACE,{"disambiguationData":[TD([[makeQuery(id+"F6.imprint","IMPRINT",EDGE,{"derivedFrom":sQuery(id+"F6.wireOp",EDGE,"E109.MirrorC")}),-1.0]])]});
            var Q1411;
            Q1411=makeQuery(id+"F6.imprint","IMPRINT",FACE,{"disambiguationData":[TD([[makeQuery(id+"F6.imprint","IMPRINT",EDGE,{"derivedFrom":sQuery(id+"F6.wireOp",EDGE,"E229.MirrorC")}),-1.0]])]});
            var Q1412;
            Q1412=makeQuery(id+"F6.imprint","IMPRINT",FACE,{"disambiguationData":[TD([[makeQuery(id+"F6.imprint","IMPRINT",EDGE,{"derivedFrom":sQuery(id+"F6.wireOp",EDGE,"E205.MirrorC")}),-1.0]])]});
            var Q1413;
            Q1413=makeQuery(id+"F6.imprint","IMPRINT",FACE,{"disambiguationData":[TD([[makeQuery(id+"F6.imprint","IMPRINT",EDGE,{"derivedFrom":sQuery(id+"F6.wireOp",EDGE,"E84.MirrorC")}),-1.0]])]});
            var Q1414;
            Q1414=makeQuery(id+"F6.imprint","IMPRINT",FACE,{"disambiguationData":[TD([[makeQuery(id+"F6.imprint","IMPRINT",EDGE,{"derivedFrom":sQuery(id+"F6.wireOp",EDGE,"E61.MirrorC")}),-1.0]])]});
            var Q1415;
            Q1415=makeQuery(id+"F6.imprint","IMPRINT",FACE,{"disambiguationData":[TD([[makeQuery(id+"F6.imprint","IMPRINT",EDGE,{"derivedFrom":sQuery(id+"F6.wireOp",EDGE,"E182.MirrorC")}),-1.0]])]});
            var Q1416;
            Q1416=makeQuery(id+"F6.imprint","IMPRINT",FACE,{"disambiguationData":[TD([[makeQuery(id+"F6.imprint","IMPRINT",EDGE,{"derivedFrom":sQuery(id+"F6.wireOp",EDGE,"E157.MirrorC")}),-1.0]])]});
            var Q1417;
            Q1417=makeQuery(id+"F6.imprint","IMPRINT",FACE,{"disambiguationData":[TD([[makeQuery(id+"F6.imprint","IMPRINT",EDGE,{"derivedFrom":sQuery(id+"F6.wireOp",EDGE,"E135.MirrorC")}),-1.0]])]});
            var Q1418;
            Q1418=makeQuery(id+"F6.imprint","IMPRINT",FACE,{"disambiguationData":[TD([[makeQuery(id+"F6.imprint","IMPRINT",EDGE,{"derivedFrom":sQuery(id+"F6.wireOp",EDGE,"E110.MirrorC")}),-1.0]])]});
            var Q1419;
            Q1419=makeQuery(id+"F6.imprint","IMPRINT",FACE,{"disambiguationData":[TD([[makeQuery(id+"F6.imprint","IMPRINT",EDGE,{"derivedFrom":sQuery(id+"F6.wireOp",EDGE,"E231.MirrorC")}),-1.0]])]});
            var Q1420;
            Q1420=makeQuery(id+"F6.imprint","IMPRINT",FACE,{"disambiguationData":[TD([[makeQuery(id+"F6.imprint","IMPRINT",EDGE,{"derivedFrom":sQuery(id+"F6.wireOp",EDGE,"E206.MirrorC")}),-1.0]])]});
            var Q1421;
            Q1421=makeQuery(id+"F6.imprint","IMPRINT",FACE,{"disambiguationData":[TD([[makeQuery(id+"F6.imprint","IMPRINT",EDGE,{"derivedFrom":sQuery(id+"F6.wireOp",EDGE,"E87.MirrorC")}),-1.0]])]});
            var Q1422;
            Q1422=makeQuery(id+"F6.imprint","IMPRINT",FACE,{"disambiguationData":[TD([[makeQuery(id+"F6.imprint","IMPRINT",EDGE,{"derivedFrom":sQuery(id+"F6.wireOp",EDGE,"E62.MirrorC")}),-1.0]])]});
            var Q1423;
            Q1423=makeQuery(id+"F6.imprint","IMPRINT",FACE,{"disambiguationData":[TD([[makeQuery(id+"F6.imprint","IMPRINT",EDGE,{"derivedFrom":sQuery(id+"F6.wireOp",EDGE,"E183.MirrorC")}),-1.0]])]});
            var Q1424;
            Q1424=makeQuery(id+"F6.imprint","IMPRINT",FACE,{"disambiguationData":[TD([[makeQuery(id+"F6.imprint","IMPRINT",EDGE,{"derivedFrom":sQuery(id+"F6.wireOp",EDGE,"E160.MirrorC")}),-1.0]])]});
            var Q1425;
            Q1425=makeQuery(id+"F6.imprint","IMPRINT",FACE,{"disambiguationData":[TD([[makeQuery(id+"F6.imprint","IMPRINT",EDGE,{"derivedFrom":sQuery(id+"F6.wireOp",EDGE,"E136.MirrorC")}),-1.0]])]});
            var Q1426;
            Q1426=makeQuery(id+"F6.imprint","IMPRINT",FACE,{"disambiguationData":[TD([[makeQuery(id+"F6.imprint","IMPRINT",EDGE,{"derivedFrom":sQuery(id+"F6.wireOp",EDGE,"E111.MirrorC")}),-1.0]])]});
            var Q1427;
            Q1427=makeQuery(id+"F6.imprint","IMPRINT",FACE,{"disambiguationData":[TD([[makeQuery(id+"F6.imprint","IMPRINT",EDGE,{"derivedFrom":sQuery(id+"F6.wireOp",EDGE,"E232.MirrorC")}),-1.0]])]});
            var Q1428;
            Q1428=makeQuery(id+"F6.imprint","IMPRINT",FACE,{"disambiguationData":[TD([[makeQuery(id+"F6.imprint","IMPRINT",EDGE,{"derivedFrom":sQuery(id+"F6.wireOp",EDGE,"E207.MirrorC")}),-1.0]])]});
            var Q1429;
            Q1429=makeQuery(id+"F6.imprint","IMPRINT",FACE,{"disambiguationData":[TD([[makeQuery(id+"F6.imprint","IMPRINT",EDGE,{"derivedFrom":sQuery(id+"F6.wireOp",EDGE,"E43.2.0.23")}),1.0]])]});
            var Q1430;
            Q1430=makeQuery(id+"F6.imprint","IMPRINT",FACE,{"disambiguationData":[TD([[makeQuery(id+"F6.imprint","IMPRINT",EDGE,{"derivedFrom":sQuery(id+"F6.wireOp",EDGE,"E43.6.0.23")}),1.0]])]});
            var Q1431;
            Q1431=makeQuery(id+"F6.imprint","IMPRINT",FACE,{"disambiguationData":[TD([[makeQuery(id+"F6.imprint","IMPRINT",EDGE,{"derivedFrom":sQuery(id+"F6.wireOp",EDGE,"E43.4.0.23")}),1.0]])]});
            var Q1432;
            Q1432=makeQuery(id+"F6.imprint","IMPRINT",FACE,{"disambiguationData":[TD([[makeQuery(id+"F6.imprint","IMPRINT",EDGE,{"derivedFrom":sQuery(id+"F6.wireOp",EDGE,"E43.26.0.23")}),1.0]])]});
            var Q1433;
            Q1433=makeQuery(id+"F6.imprint","IMPRINT",FACE,{"disambiguationData":[TD([[makeQuery(id+"F6.imprint","IMPRINT",EDGE,{"derivedFrom":sQuery(id+"F6.wireOp",EDGE,"E43.24.0.23")}),1.0]])]});
            var Q1434;
            Q1434=makeQuery(id+"F6.imprint","IMPRINT",FACE,{"disambiguationData":[TD([[makeQuery(id+"F6.imprint","IMPRINT",EDGE,{"derivedFrom":sQuery(id+"F6.wireOp",EDGE,"E43.28.0.23")}),1.0]])]});
            var Q1435;
            Q1435=makeQuery(id+"F6.imprint","IMPRINT",FACE,{"disambiguationData":[TD([[makeQuery(id+"F6.imprint","IMPRINT",EDGE,{"derivedFrom":sQuery(id+"F6.wireOp",EDGE,"E43.30.0.23")}),1.0]])]});
            var Q1436;
            Q1436=makeQuery(id+"F6.imprint","IMPRINT",FACE,{"disambiguationData":[TD([[makeQuery(id+"F6.imprint","IMPRINT",EDGE,{"derivedFrom":sQuery(id+"F6.wireOp",EDGE,"E88.MirrorC")}),-1.0]])]});
            var Q1437;
            Q1437=makeQuery(id+"F6.imprint","IMPRINT",FACE,{"disambiguationData":[TD([[makeQuery(id+"F6.imprint","IMPRINT",EDGE,{"derivedFrom":sQuery(id+"F6.wireOp",EDGE,"E63.MirrorC")}),-1.0]])]});
            var Q1438;
            Q1438=makeQuery(id+"F6.imprint","IMPRINT",FACE,{"disambiguationData":[TD([[makeQuery(id+"F6.imprint","IMPRINT",EDGE,{"derivedFrom":sQuery(id+"F6.wireOp",EDGE,"E43.32.0.23")}),1.0]])]});
            var Q1439;
            Q1439=makeQuery(id+"F6.imprint","IMPRINT",FACE,{"disambiguationData":[TD([[makeQuery(id+"F6.imprint","IMPRINT",EDGE,{"derivedFrom":sQuery(id+"F6.wireOp",EDGE,"E43.8.0.23")}),1.0]])]});
            var Q1440;
            Q1440=makeQuery(id+"F6.imprint","IMPRINT",FACE,{"disambiguationData":[TD([[makeQuery(id+"F6.imprint","IMPRINT",EDGE,{"derivedFrom":sQuery(id+"F6.wireOp",EDGE,"E43.10.0.23")}),1.0]])]});
            var Q1441;
            Q1441=makeQuery(id+"F6.imprint","IMPRINT",FACE,{"disambiguationData":[TD([[makeQuery(id+"F6.imprint","IMPRINT",EDGE,{"derivedFrom":sQuery(id+"F6.wireOp",EDGE,"E43.14.0.23")}),1.0]])]});
            var Q1442;
            Q1442=makeQuery(id+"F6.imprint","IMPRINT",FACE,{"disambiguationData":[TD([[makeQuery(id+"F6.imprint","IMPRINT",EDGE,{"derivedFrom":sQuery(id+"F6.wireOp",EDGE,"E43.12.0.23")}),1.0]])]});
            var Q1443;
            Q1443=makeQuery(id+"F6.imprint","IMPRINT",FACE,{"disambiguationData":[TD([[makeQuery(id+"F6.imprint","IMPRINT",EDGE,{"derivedFrom":sQuery(id+"F6.wireOp",EDGE,"E43.16.0.23")}),1.0]])]});
            var Q1444;
            Q1444=makeQuery(id+"F6.imprint","IMPRINT",FACE,{"disambiguationData":[TD([[makeQuery(id+"F6.imprint","IMPRINT",EDGE,{"derivedFrom":sQuery(id+"F6.wireOp",EDGE,"E43.18.0.23")}),1.0]])]});
            var Q1445;
            Q1445=makeQuery(id+"F6.imprint","IMPRINT",FACE,{"disambiguationData":[TD([[makeQuery(id+"F6.imprint","IMPRINT",EDGE,{"derivedFrom":sQuery(id+"F6.wireOp",EDGE,"E43.20.0.23")}),1.0]])]});
            var Q1446;
            Q1446=makeQuery(id+"F6.imprint","IMPRINT",FACE,{"disambiguationData":[TD([[makeQuery(id+"F6.imprint","IMPRINT",EDGE,{"derivedFrom":sQuery(id+"F6.wireOp",EDGE,"E43.22.0.23")}),1.0]])]});
            var Q1447;
            Q1447=makeQuery(id+"F6.imprint","IMPRINT",FACE,{"disambiguationData":[TD([[makeQuery(id+"F6.imprint","IMPRINT",EDGE,{"derivedFrom":sQuery(id+"F6.wireOp",EDGE,"E184.MirrorC")}),-1.0]])]});
            var Q1448;
            Q1448=makeQuery(id+"F6.imprint","IMPRINT",FACE,{"disambiguationData":[TD([[makeQuery(id+"F6.imprint","IMPRINT",EDGE,{"derivedFrom":sQuery(id+"F6.wireOp",EDGE,"E161.MirrorC")}),-1.0]])]});
            var Q1449;
            Q1449=makeQuery(id+"F6.imprint","IMPRINT",FACE,{"disambiguationData":[TD([[makeQuery(id+"F6.imprint","IMPRINT",EDGE,{"derivedFrom":sQuery(id+"F6.wireOp",EDGE,"E137.MirrorC")}),-1.0]])]});
            var Q1450;
            Q1450=makeQuery(id+"F6.imprint","IMPRINT",FACE,{"disambiguationData":[TD([[makeQuery(id+"F6.imprint","IMPRINT",EDGE,{"derivedFrom":sQuery(id+"F6.wireOp",EDGE,"E114.MirrorC")}),-1.0]])]});
            var Q1451;
            Q1451=makeQuery(id+"F6.imprint","IMPRINT",FACE,{"disambiguationData":[TD([[makeQuery(id+"F6.imprint","IMPRINT",EDGE,{"derivedFrom":sQuery(id+"F6.wireOp",EDGE,"E233.MirrorC")}),-1.0]])]});
            var Q1452;
            Q1452=makeQuery(id+"F6.imprint","IMPRINT",FACE,{"disambiguationData":[TD([[makeQuery(id+"F6.imprint","IMPRINT",EDGE,{"derivedFrom":sQuery(id+"F6.wireOp",EDGE,"E209.MirrorC")}),-1.0]])]});
            var Q1453;
            Q1453=makeQuery(id+"F6.imprint","IMPRINT",FACE,{"disambiguationData":[TD([[makeQuery(id+"F6.imprint","IMPRINT",EDGE,{"derivedFrom":sQuery(id+"F6.wireOp",EDGE,"E43.2.0.24")}),1.0]])]});
            var Q1454;
            Q1454=makeQuery(id+"F6.imprint","IMPRINT",FACE,{"disambiguationData":[TD([[makeQuery(id+"F6.imprint","IMPRINT",EDGE,{"derivedFrom":sQuery(id+"F6.wireOp",EDGE,"E43.6.0.24")}),1.0]])]});
            var Q1455;
            Q1455=makeQuery(id+"F6.imprint","IMPRINT",FACE,{"disambiguationData":[TD([[makeQuery(id+"F6.imprint","IMPRINT",EDGE,{"derivedFrom":sQuery(id+"F6.wireOp",EDGE,"E43.4.0.24")}),1.0]])]});
            var Q1456;
            Q1456=makeQuery(id+"F6.imprint","IMPRINT",FACE,{"disambiguationData":[TD([[makeQuery(id+"F6.imprint","IMPRINT",EDGE,{"derivedFrom":sQuery(id+"F6.wireOp",EDGE,"E43.8.0.24")}),1.0]])]});
            var Q1457;
            Q1457=makeQuery(id+"F6.imprint","IMPRINT",FACE,{"disambiguationData":[TD([[makeQuery(id+"F6.imprint","IMPRINT",EDGE,{"derivedFrom":sQuery(id+"F6.wireOp",EDGE,"E43.28.0.24")}),1.0]])]});
            var Q1458;
            Q1458=makeQuery(id+"F6.imprint","IMPRINT",FACE,{"disambiguationData":[TD([[makeQuery(id+"F6.imprint","IMPRINT",EDGE,{"derivedFrom":sQuery(id+"F6.wireOp",EDGE,"E43.30.0.24")}),1.0]])]});
            var Q1459;
            Q1459=makeQuery(id+"F6.imprint","IMPRINT",FACE,{"disambiguationData":[TD([[makeQuery(id+"F6.imprint","IMPRINT",EDGE,{"derivedFrom":sQuery(id+"F6.wireOp",EDGE,"E89.MirrorC")}),-1.0]])]});
            var Q1460;
            Q1460=makeQuery(id+"F6.imprint","IMPRINT",FACE,{"disambiguationData":[TD([[makeQuery(id+"F6.imprint","IMPRINT",EDGE,{"derivedFrom":sQuery(id+"F6.wireOp",EDGE,"E64.MirrorC")}),-1.0]])]});
            var Q1461;
            Q1461=makeQuery(id+"F6.imprint","IMPRINT",FACE,{"disambiguationData":[TD([[makeQuery(id+"F6.imprint","IMPRINT",EDGE,{"derivedFrom":sQuery(id+"F6.wireOp",EDGE,"E43.32.0.24")}),1.0]])]});
            var Q1462;
            Q1462=makeQuery(id+"F6.imprint","IMPRINT",FACE,{"disambiguationData":[TD([[makeQuery(id+"F6.imprint","IMPRINT",EDGE,{"derivedFrom":sQuery(id+"F6.wireOp",EDGE,"E43.10.0.24")}),1.0]])]});
            var Q1463;
            Q1463=makeQuery(id+"F6.imprint","IMPRINT",FACE,{"disambiguationData":[TD([[makeQuery(id+"F6.imprint","IMPRINT",EDGE,{"derivedFrom":sQuery(id+"F6.wireOp",EDGE,"E43.14.0.24")}),1.0]])]});
            var Q1464;
            Q1464=makeQuery(id+"F6.imprint","IMPRINT",FACE,{"disambiguationData":[TD([[makeQuery(id+"F6.imprint","IMPRINT",EDGE,{"derivedFrom":sQuery(id+"F6.wireOp",EDGE,"E43.12.0.24")}),1.0]])]});
            var Q1465;
            Q1465=makeQuery(id+"F6.imprint","IMPRINT",FACE,{"disambiguationData":[TD([[makeQuery(id+"F6.imprint","IMPRINT",EDGE,{"derivedFrom":sQuery(id+"F6.wireOp",EDGE,"E43.16.0.24")}),1.0]])]});
            var Q1466;
            Q1466=makeQuery(id+"F6.imprint","IMPRINT",FACE,{"disambiguationData":[TD([[makeQuery(id+"F6.imprint","IMPRINT",EDGE,{"derivedFrom":sQuery(id+"F6.wireOp",EDGE,"E43.18.0.24")}),1.0]])]});
            var Q1467;
            Q1467=makeQuery(id+"F6.imprint","IMPRINT",FACE,{"disambiguationData":[TD([[makeQuery(id+"F6.imprint","IMPRINT",EDGE,{"derivedFrom":sQuery(id+"F6.wireOp",EDGE,"E43.20.0.24")}),1.0]])]});
            var Q1468;
            Q1468=makeQuery(id+"F6.imprint","IMPRINT",FACE,{"disambiguationData":[TD([[makeQuery(id+"F6.imprint","IMPRINT",EDGE,{"derivedFrom":sQuery(id+"F6.wireOp",EDGE,"E43.22.0.24")}),1.0]])]});
            var Q1469;
            Q1469=makeQuery(id+"F6.imprint","IMPRINT",FACE,{"disambiguationData":[TD([[makeQuery(id+"F6.imprint","IMPRINT",EDGE,{"derivedFrom":sQuery(id+"F6.wireOp",EDGE,"E43.26.0.24")}),1.0]])]});
            var Q1470;
            Q1470=makeQuery(id+"F6.imprint","IMPRINT",FACE,{"disambiguationData":[TD([[makeQuery(id+"F6.imprint","IMPRINT",EDGE,{"derivedFrom":sQuery(id+"F6.wireOp",EDGE,"E43.24.0.24")}),1.0]])]});
            var Q1471;
            Q1471=makeQuery(id+"F6.imprint","IMPRINT",FACE,{"disambiguationData":[TD([[makeQuery(id+"F6.imprint","IMPRINT",EDGE,{"derivedFrom":sQuery(id+"F6.wireOp",EDGE,"E43.2.0.25")}),1.0]])]});
            var Q1472;
            Q1472=makeQuery(id+"F6.imprint","IMPRINT",FACE,{"disambiguationData":[TD([[makeQuery(id+"F6.imprint","IMPRINT",EDGE,{"derivedFrom":sQuery(id+"F6.wireOp",EDGE,"E43.4.0.25")}),1.0]])]});
            var Q1473;
            Q1473=makeQuery(id+"F6.imprint","IMPRINT",FACE,{"disambiguationData":[TD([[makeQuery(id+"F6.imprint","IMPRINT",EDGE,{"derivedFrom":sQuery(id+"F6.wireOp",EDGE,"E43.6.0.25")}),1.0]])]});
            var Q1474;
            Q1474=makeQuery(id+"F6.imprint","IMPRINT",FACE,{"disambiguationData":[TD([[makeQuery(id+"F6.imprint","IMPRINT",EDGE,{"derivedFrom":sQuery(id+"F6.wireOp",EDGE,"E43.10.0.25")}),1.0]])]});
            var Q1475;
            Q1475=makeQuery(id+"F6.imprint","IMPRINT",FACE,{"disambiguationData":[TD([[makeQuery(id+"F6.imprint","IMPRINT",EDGE,{"derivedFrom":sQuery(id+"F6.wireOp",EDGE,"E43.8.0.25")}),1.0]])]});
            var Q1476;
            Q1476=makeQuery(id+"F6.imprint","IMPRINT",FACE,{"disambiguationData":[TD([[makeQuery(id+"F6.imprint","IMPRINT",EDGE,{"derivedFrom":sQuery(id+"F6.wireOp",EDGE,"E43.12.0.25")}),1.0]])]});
            var Q1477;
            Q1477=makeQuery(id+"F6.imprint","IMPRINT",FACE,{"disambiguationData":[TD([[makeQuery(id+"F6.imprint","IMPRINT",EDGE,{"derivedFrom":sQuery(id+"F6.wireOp",EDGE,"E43.14.0.25")}),1.0]])]});
            var Q1478;
            Q1478=makeQuery(id+"F6.imprint","IMPRINT",FACE,{"disambiguationData":[TD([[makeQuery(id+"F6.imprint","IMPRINT",EDGE,{"derivedFrom":sQuery(id+"F6.wireOp",EDGE,"E138.MirrorC")}),-1.0]])]});
            var Q1479;
            Q1479=makeQuery(id+"F6.imprint","IMPRINT",FACE,{"disambiguationData":[TD([[makeQuery(id+"F6.imprint","IMPRINT",EDGE,{"derivedFrom":sQuery(id+"F6.wireOp",EDGE,"E115.MirrorC")}),-1.0]])]});
            var Q1480;
            Q1480=makeQuery(id+"F6.imprint","IMPRINT",FACE,{"disambiguationData":[TD([[makeQuery(id+"F6.imprint","IMPRINT",EDGE,{"derivedFrom":sQuery(id+"F6.wireOp",EDGE,"E234.MirrorC")}),-1.0]])]});
            var Q1481;
            Q1481=makeQuery(id+"F6.imprint","IMPRINT",FACE,{"disambiguationData":[TD([[makeQuery(id+"F6.imprint","IMPRINT",EDGE,{"derivedFrom":sQuery(id+"F6.wireOp",EDGE,"E210.MirrorC")}),-1.0]])]});
            var Q1482;
            Q1482=makeQuery(id+"F6.imprint","IMPRINT",FACE,{"disambiguationData":[TD([[makeQuery(id+"F6.imprint","IMPRINT",EDGE,{"derivedFrom":sQuery(id+"F6.wireOp",EDGE,"E186.MirrorC")}),-1.0]])]});
            var Q1483;
            Q1483=makeQuery(id+"F6.imprint","IMPRINT",FACE,{"disambiguationData":[TD([[makeQuery(id+"F6.imprint","IMPRINT",EDGE,{"derivedFrom":sQuery(id+"F6.wireOp",EDGE,"E162.MirrorC")}),-1.0]])]});
            var Q1484;
            Q1484=makeQuery(id+"F6.imprint","IMPRINT",FACE,{"disambiguationData":[TD([[makeQuery(id+"F6.imprint","IMPRINT",EDGE,{"derivedFrom":sQuery(id+"F6.wireOp",EDGE,"E92.MirrorC")}),-1.0]])]});
            var Q1485;
            Q1485=makeQuery(id+"F6.imprint","IMPRINT",FACE,{"disambiguationData":[TD([[makeQuery(id+"F6.imprint","IMPRINT",EDGE,{"derivedFrom":sQuery(id+"F6.wireOp",EDGE,"E43.16.0.25")}),1.0]])]});
            var Q1486;
            Q1486=makeQuery(id+"F6.imprint","IMPRINT",FACE,{"disambiguationData":[TD([[makeQuery(id+"F6.imprint","IMPRINT",EDGE,{"derivedFrom":sQuery(id+"F6.wireOp",EDGE,"E43.18.0.25")}),1.0]])]});
            var Q1487;
            Q1487=makeQuery(id+"F6.imprint","IMPRINT",FACE,{"disambiguationData":[TD([[makeQuery(id+"F6.imprint","IMPRINT",EDGE,{"derivedFrom":sQuery(id+"F6.wireOp",EDGE,"E43.22.0.25")}),1.0]])]});
            var Q1488;
            Q1488=makeQuery(id+"F6.imprint","IMPRINT",FACE,{"disambiguationData":[TD([[makeQuery(id+"F6.imprint","IMPRINT",EDGE,{"derivedFrom":sQuery(id+"F6.wireOp",EDGE,"E43.20.0.25")}),1.0]])]});
            var Q1489;
            Q1489=makeQuery(id+"F6.imprint","IMPRINT",FACE,{"disambiguationData":[TD([[makeQuery(id+"F6.imprint","IMPRINT",EDGE,{"derivedFrom":sQuery(id+"F6.wireOp",EDGE,"E43.24.0.25")}),1.0]])]});
            var Q1490;
            Q1490=makeQuery(id+"F6.imprint","IMPRINT",FACE,{"disambiguationData":[TD([[makeQuery(id+"F6.imprint","IMPRINT",EDGE,{"derivedFrom":sQuery(id+"F6.wireOp",EDGE,"E43.26.0.25")}),1.0]])]});
            var Q1491;
            Q1491=makeQuery(id+"F6.imprint","IMPRINT",FACE,{"disambiguationData":[TD([[makeQuery(id+"F6.imprint","IMPRINT",EDGE,{"derivedFrom":sQuery(id+"F6.wireOp",EDGE,"E43.30.0.25")}),1.0]])]});
            var Q1492;
            Q1492=makeQuery(id+"F6.imprint","IMPRINT",FACE,{"disambiguationData":[TD([[makeQuery(id+"F6.imprint","IMPRINT",EDGE,{"derivedFrom":sQuery(id+"F6.wireOp",EDGE,"E43.28.0.25")}),1.0]])]});
            var Q1493;
            Q1493=makeQuery(id+"F6.imprint","IMPRINT",FACE,{"disambiguationData":[TD([[makeQuery(id+"F6.imprint","IMPRINT",EDGE,{"derivedFrom":sQuery(id+"F6.wireOp",EDGE,"E65.MirrorC")}),-1.0]])]});
            var Q1494;
            Q1494=makeQuery(id+"F6.imprint","IMPRINT",FACE,{"disambiguationData":[TD([[makeQuery(id+"F6.imprint","IMPRINT",EDGE,{"derivedFrom":sQuery(id+"F6.wireOp",EDGE,"E43.2.0.26")}),1.0]])]});
            var Q1495;
            Q1495=makeQuery(id+"F6.imprint","IMPRINT",FACE,{"disambiguationData":[TD([[makeQuery(id+"F6.imprint","IMPRINT",EDGE,{"derivedFrom":sQuery(id+"F6.wireOp",EDGE,"E43.4.0.26")}),1.0]])]});
            var Q1496;
            Q1496=makeQuery(id+"F6.imprint","IMPRINT",FACE,{"disambiguationData":[TD([[makeQuery(id+"F6.imprint","IMPRINT",EDGE,{"derivedFrom":sQuery(id+"F6.wireOp",EDGE,"E43.6.0.26")}),1.0]])]});
            var Q1497;
            Q1497=makeQuery(id+"F6.imprint","IMPRINT",FACE,{"disambiguationData":[TD([[makeQuery(id+"F6.imprint","IMPRINT",EDGE,{"derivedFrom":sQuery(id+"F6.wireOp",EDGE,"E43.10.0.26")}),1.0]])]});
            var Q1498;
            Q1498=makeQuery(id+"F6.imprint","IMPRINT",FACE,{"disambiguationData":[TD([[makeQuery(id+"F6.imprint","IMPRINT",EDGE,{"derivedFrom":sQuery(id+"F6.wireOp",EDGE,"E43.8.0.26")}),1.0]])]});
            var Q1499;
            Q1499=makeQuery(id+"F6.imprint","IMPRINT",FACE,{"disambiguationData":[TD([[makeQuery(id+"F6.imprint","IMPRINT",EDGE,{"derivedFrom":sQuery(id+"F6.wireOp",EDGE,"E43.12.0.26")}),1.0]])]});
            var Q1500;
            Q1500=makeQuery(id+"F6.imprint","IMPRINT",FACE,{"disambiguationData":[TD([[makeQuery(id+"F6.imprint","IMPRINT",EDGE,{"derivedFrom":sQuery(id+"F6.wireOp",EDGE,"E43.14.0.26")}),1.0]])]});
            var Q1501;
            Q1501=makeQuery(id+"F6.imprint","IMPRINT",FACE,{"disambiguationData":[TD([[makeQuery(id+"F6.imprint","IMPRINT",EDGE,{"derivedFrom":sQuery(id+"F6.wireOp",EDGE,"E43.16.0.26")}),1.0]])]});
            var Q1502;
            Q1502=makeQuery(id+"F6.imprint","IMPRINT",FACE,{"disambiguationData":[TD([[makeQuery(id+"F6.imprint","IMPRINT",EDGE,{"derivedFrom":sQuery(id+"F6.wireOp",EDGE,"E139.MirrorC")}),-1.0]])]});
            var Q1503;
            Q1503=makeQuery(id+"F6.imprint","IMPRINT",FACE,{"disambiguationData":[TD([[makeQuery(id+"F6.imprint","IMPRINT",EDGE,{"derivedFrom":sQuery(id+"F6.wireOp",EDGE,"E116.MirrorC")}),-1.0]])]});
            var Q1504;
            Q1504=makeQuery(id+"F6.imprint","IMPRINT",FACE,{"disambiguationData":[TD([[makeQuery(id+"F6.imprint","IMPRINT",EDGE,{"derivedFrom":sQuery(id+"F6.wireOp",EDGE,"E237.MirrorC")}),-1.0]])]});
            var Q1505;
            Q1505=makeQuery(id+"F6.imprint","IMPRINT",FACE,{"disambiguationData":[TD([[makeQuery(id+"F6.imprint","IMPRINT",EDGE,{"derivedFrom":sQuery(id+"F6.wireOp",EDGE,"E211.MirrorC")}),-1.0]])]});
            var Q1506;
            Q1506=makeQuery(id+"F6.imprint","IMPRINT",FACE,{"disambiguationData":[TD([[makeQuery(id+"F6.imprint","IMPRINT",EDGE,{"derivedFrom":sQuery(id+"F6.wireOp",EDGE,"E190.MirrorC")}),-1.0]])]});
            var Q1507;
            Q1507=makeQuery(id+"F6.imprint","IMPRINT",FACE,{"disambiguationData":[TD([[makeQuery(id+"F6.imprint","IMPRINT",EDGE,{"derivedFrom":sQuery(id+"F6.wireOp",EDGE,"E163.MirrorC")}),-1.0]])]});
            var Q1508;
            Q1508=makeQuery(id+"F6.imprint","IMPRINT",FACE,{"disambiguationData":[TD([[makeQuery(id+"F6.imprint","IMPRINT",EDGE,{"derivedFrom":sQuery(id+"F6.wireOp",EDGE,"E43.18.0.26")}),1.0]])]});
            var Q1509;
            Q1509=makeQuery(id+"F6.imprint","IMPRINT",FACE,{"disambiguationData":[TD([[makeQuery(id+"F6.imprint","IMPRINT",EDGE,{"derivedFrom":sQuery(id+"F6.wireOp",EDGE,"E43.22.0.26")}),1.0]])]});
            var Q1510;
            Q1510=makeQuery(id+"F6.imprint","IMPRINT",FACE,{"disambiguationData":[TD([[makeQuery(id+"F6.imprint","IMPRINT",EDGE,{"derivedFrom":sQuery(id+"F6.wireOp",EDGE,"E43.20.0.26")}),1.0]])]});
            var Q1511;
            Q1511=makeQuery(id+"F6.imprint","IMPRINT",FACE,{"disambiguationData":[TD([[makeQuery(id+"F6.imprint","IMPRINT",EDGE,{"derivedFrom":sQuery(id+"F6.wireOp",EDGE,"E43.24.0.26")}),1.0]])]});
            var Q1512;
            Q1512=makeQuery(id+"F6.imprint","IMPRINT",FACE,{"disambiguationData":[TD([[makeQuery(id+"F6.imprint","IMPRINT",EDGE,{"derivedFrom":sQuery(id+"F6.wireOp",EDGE,"E43.26.0.26")}),1.0]])]});
            var Q1513;
            Q1513=makeQuery(id+"F6.imprint","IMPRINT",FACE,{"disambiguationData":[TD([[makeQuery(id+"F6.imprint","IMPRINT",EDGE,{"derivedFrom":sQuery(id+"F6.wireOp",EDGE,"E43.30.0.26")}),1.0]])]});
            var Q1514;
            Q1514=makeQuery(id+"F6.imprint","IMPRINT",FACE,{"disambiguationData":[TD([[makeQuery(id+"F6.imprint","IMPRINT",EDGE,{"derivedFrom":sQuery(id+"F6.wireOp",EDGE,"E43.28.0.26")}),1.0]])]});
            var Q1515;
            Q1515=makeQuery(id+"F6.imprint","IMPRINT",FACE,{"disambiguationData":[TD([[makeQuery(id+"F6.imprint","IMPRINT",EDGE,{"derivedFrom":sQuery(id+"F6.wireOp",EDGE,"E66.MirrorC")}),-1.0]])]});
            var Q1516;
            Q1516=makeQuery(id+"F6.imprint","IMPRINT",FACE,{"disambiguationData":[TD([[makeQuery(id+"F6.imprint","IMPRINT",EDGE,{"derivedFrom":sQuery(id+"F6.wireOp",EDGE,"E43.32.0.26")}),1.0]])]});
            var Q1517;
            Q1517=makeQuery(id+"F6.imprint","IMPRINT",FACE,{"disambiguationData":[TD([[makeQuery(id+"F6.imprint","IMPRINT",EDGE,{"derivedFrom":sQuery(id+"F6.wireOp",EDGE,"E93.MirrorC")}),-1.0]])]});
            var Q1518;
            Q1518=makeQuery(id+"F6.imprint","IMPRINT",FACE,{"disambiguationData":[TD([[makeQuery(id+"F6.imprint","IMPRINT",EDGE,{"derivedFrom":sQuery(id+"F6.wireOp",EDGE,"E140.MirrorC")}),-1.0]])]});
            var Q1519;
            Q1519=makeQuery(id+"F6.imprint","IMPRINT",FACE,{"disambiguationData":[TD([[makeQuery(id+"F6.imprint","IMPRINT",EDGE,{"derivedFrom":sQuery(id+"F6.wireOp",EDGE,"E117.MirrorC")}),-1.0]])]});
            var Q1520;
            Q1520=makeQuery(id+"F6.imprint","IMPRINT",FACE,{"disambiguationData":[TD([[makeQuery(id+"F6.imprint","IMPRINT",EDGE,{"derivedFrom":sQuery(id+"F6.wireOp",EDGE,"E239.MirrorC")}),-1.0]])]});
            var Q1521;
            Q1521=makeQuery(id+"F6.imprint","IMPRINT",FACE,{"disambiguationData":[TD([[makeQuery(id+"F6.imprint","IMPRINT",EDGE,{"derivedFrom":sQuery(id+"F6.wireOp",EDGE,"E213.MirrorC")}),-1.0]])]});
            var Q1522;
            Q1522=makeQuery(id+"F6.imprint","IMPRINT",FACE,{"disambiguationData":[TD([[makeQuery(id+"F6.imprint","IMPRINT",EDGE,{"derivedFrom":sQuery(id+"F6.wireOp",EDGE,"E191.MirrorC")}),-1.0]])]});
            var Q1523;
            Q1523=makeQuery(id+"F6.imprint","IMPRINT",FACE,{"disambiguationData":[TD([[makeQuery(id+"F6.imprint","IMPRINT",EDGE,{"derivedFrom":sQuery(id+"F6.wireOp",EDGE,"E164.MirrorC")}),-1.0]])]});
            var Q1524;
            Q1524=makeQuery(id+"F6.imprint","IMPRINT",FACE,{"disambiguationData":[TD([[makeQuery(id+"F6.imprint","IMPRINT",EDGE,{"derivedFrom":sQuery(id+"F6.wireOp",EDGE,"E67.MirrorC")}),-1.0]])]});
            var Q1525;
            Q1525=makeQuery(id+"F6.imprint","IMPRINT",FACE,{"disambiguationData":[TD([[makeQuery(id+"F6.imprint","IMPRINT",EDGE,{"derivedFrom":sQuery(id+"F6.wireOp",EDGE,"E95.MirrorC")}),-1.0]])]});
            var Q1526;
            Q1526=makeQuery(id+"F6.imprint","IMPRINT",FACE,{"disambiguationData":[TD([[makeQuery(id+"F6.imprint","IMPRINT",EDGE,{"derivedFrom":sQuery(id+"F6.wireOp",EDGE,"E141.MirrorC")}),-1.0]])]});
            var Q1527;
            Q1527=makeQuery(id+"F6.imprint","IMPRINT",FACE,{"disambiguationData":[TD([[makeQuery(id+"F6.imprint","IMPRINT",EDGE,{"derivedFrom":sQuery(id+"F6.wireOp",EDGE,"E119.MirrorC")}),-1.0]])]});
            var Q1528;
            Q1528=makeQuery(id+"F6.imprint","IMPRINT",FACE,{"disambiguationData":[TD([[makeQuery(id+"F6.imprint","IMPRINT",EDGE,{"derivedFrom":sQuery(id+"F6.wireOp",EDGE,"E240.MirrorC")}),-1.0]])]});
            var Q1529;
            Q1529=makeQuery(id+"F6.imprint","IMPRINT",FACE,{"disambiguationData":[TD([[makeQuery(id+"F6.imprint","IMPRINT",EDGE,{"derivedFrom":sQuery(id+"F6.wireOp",EDGE,"E214.MirrorC")}),-1.0]])]});
            var Q1530;
            Q1530=makeQuery(id+"F6.imprint","IMPRINT",FACE,{"disambiguationData":[TD([[makeQuery(id+"F6.imprint","IMPRINT",EDGE,{"derivedFrom":sQuery(id+"F6.wireOp",EDGE,"E192.MirrorC")}),-1.0]])]});
            var Q1531;
            Q1531=makeQuery(id+"F6.imprint","IMPRINT",FACE,{"disambiguationData":[TD([[makeQuery(id+"F6.imprint","IMPRINT",EDGE,{"derivedFrom":sQuery(id+"F6.wireOp",EDGE,"E165.MirrorC")}),-1.0]])]});
            var Q1532;
            Q1532=makeQuery(id+"F6.imprint","IMPRINT",FACE,{"disambiguationData":[TD([[makeQuery(id+"F6.imprint","IMPRINT",EDGE,{"derivedFrom":sQuery(id+"F6.wireOp",EDGE,"E70.MirrorC")}),-1.0]])]});
            var Q1533;
            Q1533=makeQuery(id+"F6.imprint","IMPRINT",FACE,{"disambiguationData":[TD([[makeQuery(id+"F6.imprint","IMPRINT",EDGE,{"derivedFrom":sQuery(id+"F6.wireOp",EDGE,"E49.MirrorC")}),-1.0]])]});
            var Q1534;
            Q1534=makeQuery(id+"F6.imprint","IMPRINT",FACE,{"disambiguationData":[TD([[makeQuery(id+"F6.imprint","IMPRINT",EDGE,{"derivedFrom":sQuery(id+"F6.wireOp",EDGE,"E96.MirrorC")}),-1.0]])]});
            var Q1535;
            Q1535=makeQuery(id+"F6.imprint","IMPRINT",FACE,{"disambiguationData":[TD([[makeQuery(id+"F6.imprint","IMPRINT",EDGE,{"derivedFrom":sQuery(id+"F6.wireOp",EDGE,"E144.MirrorC")}),-1.0]])]});
            var Q1536;
            Q1536=makeQuery(id+"F6.imprint","IMPRINT",FACE,{"disambiguationData":[TD([[makeQuery(id+"F6.imprint","IMPRINT",EDGE,{"derivedFrom":sQuery(id+"F6.wireOp",EDGE,"E121.MirrorC")}),-1.0]])]});
            var Q1537;
            Q1537=makeQuery(id+"F6.imprint","IMPRINT",FACE,{"disambiguationData":[TD([[makeQuery(id+"F6.imprint","IMPRINT",EDGE,{"derivedFrom":sQuery(id+"F6.wireOp",EDGE,"E241.MirrorC")}),-1.0]])]});
            var Q1538;
            Q1538=makeQuery(id+"F6.imprint","IMPRINT",FACE,{"disambiguationData":[TD([[makeQuery(id+"F6.imprint","IMPRINT",EDGE,{"derivedFrom":sQuery(id+"F6.wireOp",EDGE,"E215.MirrorC")}),-1.0]])]});
            var Q1539;
            Q1539=makeQuery(id+"F6.imprint","IMPRINT",FACE,{"disambiguationData":[TD([[makeQuery(id+"F6.imprint","IMPRINT",EDGE,{"derivedFrom":sQuery(id+"F6.wireOp",EDGE,"E193.MirrorC")}),-1.0]])]});
            var Q1540;
            Q1540=makeQuery(id+"F6.imprint","IMPRINT",FACE,{"disambiguationData":[TD([[makeQuery(id+"F6.imprint","IMPRINT",EDGE,{"derivedFrom":sQuery(id+"F6.wireOp",EDGE,"E168.MirrorC")}),-1.0]])]});
            var Q1541;
            Q1541=makeQuery(id+"F6.imprint","IMPRINT",FACE,{"disambiguationData":[TD([[makeQuery(id+"F6.imprint","IMPRINT",EDGE,{"derivedFrom":sQuery(id+"F6.wireOp",EDGE,"E71.MirrorC")}),-1.0]])]});
            var Q1542;
            Q1542=makeQuery(id+"F6.imprint","IMPRINT",FACE,{"disambiguationData":[TD([[makeQuery(id+"F6.imprint","IMPRINT",EDGE,{"derivedFrom":sQuery(id+"F6.wireOp",EDGE,"E50.MirrorC")}),-1.0]])]});
            var Q1543;
            Q1543=makeQuery(id+"F6.imprint","IMPRINT",FACE,{"disambiguationData":[TD([[makeQuery(id+"F6.imprint","IMPRINT",EDGE,{"derivedFrom":sQuery(id+"F6.wireOp",EDGE,"E97.MirrorC")}),-1.0]])]});
            var Q1544;
            Q1544=makeQuery(id+"F6.imprint","IMPRINT",FACE,{"disambiguationData":[TD([[makeQuery(id+"F6.imprint","IMPRINT",EDGE,{"derivedFrom":sQuery(id+"F6.wireOp",EDGE,"E147.MirrorC")}),-1.0]])]});
            var Q1545;
            Q1545=makeQuery(id+"F6.imprint","IMPRINT",FACE,{"disambiguationData":[TD([[makeQuery(id+"F6.imprint","IMPRINT",EDGE,{"derivedFrom":sQuery(id+"F6.wireOp",EDGE,"E122.MirrorC")}),-1.0]])]});
            var Q1546;
            Q1546=makeQuery(id+"F6.imprint","IMPRINT",FACE,{"disambiguationData":[TD([[makeQuery(id+"F6.imprint","IMPRINT",EDGE,{"derivedFrom":sQuery(id+"F6.wireOp",EDGE,"E243.MirrorC")}),-1.0]])]});
            var Q1547;
            Q1547=makeQuery(id+"F6.imprint","IMPRINT",FACE,{"disambiguationData":[TD([[makeQuery(id+"F6.imprint","IMPRINT",EDGE,{"derivedFrom":sQuery(id+"F6.wireOp",EDGE,"E217.MirrorC")}),-1.0]])]});
            var Q1548;
            Q1548=makeQuery(id+"F6.imprint","IMPRINT",FACE,{"disambiguationData":[TD([[makeQuery(id+"F6.imprint","IMPRINT",EDGE,{"derivedFrom":sQuery(id+"F6.wireOp",EDGE,"E194.MirrorC")}),-1.0]])]});
            var Q1549;
            Q1549=makeQuery(id+"F6.imprint","IMPRINT",FACE,{"disambiguationData":[TD([[makeQuery(id+"F6.imprint","IMPRINT",EDGE,{"derivedFrom":sQuery(id+"F6.wireOp",EDGE,"E169.MirrorC")}),-1.0]])]});
            var Q1550;
            Q1550=makeQuery(id+"F6.imprint","IMPRINT",FACE,{"disambiguationData":[TD([[makeQuery(id+"F6.imprint","IMPRINT",EDGE,{"derivedFrom":sQuery(id+"F6.wireOp",EDGE,"E148.MirrorC")}),-1.0]])]});
            var Q1551;
            Q1551=makeQuery(id+"F6.imprint","IMPRINT",FACE,{"disambiguationData":[TD([[makeQuery(id+"F6.imprint","IMPRINT",EDGE,{"derivedFrom":sQuery(id+"F6.wireOp",EDGE,"E123.MirrorC")}),-1.0]])]});
            var Q1552;
            Q1552=makeQuery(id+"F6.imprint","IMPRINT",FACE,{"disambiguationData":[TD([[makeQuery(id+"F6.imprint","IMPRINT",EDGE,{"derivedFrom":sQuery(id+"F6.wireOp",EDGE,"E72.MirrorC")}),-1.0]])]});
            var Q1553;
            Q1553=makeQuery(id+"F6.imprint","IMPRINT",FACE,{"disambiguationData":[TD([[makeQuery(id+"F6.imprint","IMPRINT",EDGE,{"derivedFrom":sQuery(id+"F6.wireOp",EDGE,"E51.MirrorC")}),-1.0]])]});
            var Q1554;
            Q1554=makeQuery(id+"F6.imprint","IMPRINT",FACE,{"disambiguationData":[TD([[makeQuery(id+"F6.imprint","IMPRINT",EDGE,{"derivedFrom":sQuery(id+"F6.wireOp",EDGE,"E98.MirrorC")}),-1.0]])]});
            var Q1555;
            Q1555=makeQuery(id+"F6.imprint","IMPRINT",FACE,{"disambiguationData":[TD([[makeQuery(id+"F6.imprint","IMPRINT",EDGE,{"derivedFrom":sQuery(id+"F6.wireOp",EDGE,"E43.13.0.23")}),1.0]])]});
            var Q1556;
            Q1556=makeQuery(id+"F6.imprint","IMPRINT",FACE,{"disambiguationData":[TD([[makeQuery(id+"F6.imprint","IMPRINT",EDGE,{"derivedFrom":sQuery(id+"F6.wireOp",EDGE,"E43.11.0.23")}),1.0]])]});
            var Q1557;
            Q1557=makeQuery(id+"F6.imprint","IMPRINT",FACE,{"disambiguationData":[TD([[makeQuery(id+"F6.imprint","IMPRINT",EDGE,{"derivedFrom":sQuery(id+"F6.wireOp",EDGE,"E43.15.0.23")}),1.0]])]});
            var Q1558;
            Q1558=makeQuery(id+"F6.imprint","IMPRINT",FACE,{"disambiguationData":[TD([[makeQuery(id+"F6.imprint","IMPRINT",EDGE,{"derivedFrom":sQuery(id+"F6.wireOp",EDGE,"E43.17.0.23")}),1.0]])]});
            var Q1559;
            Q1559=makeQuery(id+"F6.imprint","IMPRINT",FACE,{"disambiguationData":[TD([[makeQuery(id+"F6.imprint","IMPRINT",EDGE,{"derivedFrom":sQuery(id+"F6.wireOp",EDGE,"E43.19.0.23")}),1.0]])]});
            var Q1560;
            Q1560=makeQuery(id+"F6.imprint","IMPRINT",FACE,{"disambiguationData":[TD([[makeQuery(id+"F6.imprint","IMPRINT",EDGE,{"derivedFrom":sQuery(id+"F6.wireOp",EDGE,"E43.21.0.23")}),1.0]])]});
            var Q1561;
            Q1561=makeQuery(id+"F6.imprint","IMPRINT",FACE,{"disambiguationData":[TD([[makeQuery(id+"F6.imprint","IMPRINT",EDGE,{"derivedFrom":sQuery(id+"F6.wireOp",EDGE,"E43.25.0.23")}),1.0]])]});
            var Q1562;
            Q1562=makeQuery(id+"F6.imprint","IMPRINT",FACE,{"disambiguationData":[TD([[makeQuery(id+"F6.imprint","IMPRINT",EDGE,{"derivedFrom":sQuery(id+"F6.wireOp",EDGE,"E43.23.0.23")}),1.0]])]});
            var Q1563;
            Q1563=makeQuery(id+"F6.imprint","IMPRINT",FACE,{"disambiguationData":[TD([[makeQuery(id+"F6.imprint","IMPRINT",EDGE,{"derivedFrom":sQuery(id+"F6.wireOp",EDGE,"E43.27.0.23")}),1.0]])]});
            var Q1564;
            Q1564=makeQuery(id+"F6.imprint","IMPRINT",FACE,{"disambiguationData":[TD([[makeQuery(id+"F6.imprint","IMPRINT",EDGE,{"derivedFrom":sQuery(id+"F6.wireOp",EDGE,"E221.MirrorC")}),-1.0]])]});
            var Q1565;
            Q1565=makeQuery(id+"F6.imprint","IMPRINT",FACE,{"disambiguationData":[TD([[makeQuery(id+"F6.imprint","IMPRINT",EDGE,{"derivedFrom":sQuery(id+"F6.wireOp",EDGE,"E197.MirrorC")}),-1.0]])]});
            var Q1566;
            Q1566=makeQuery(id+"F6.imprint","IMPRINT",FACE,{"disambiguationData":[TD([[makeQuery(id+"F6.imprint","IMPRINT",EDGE,{"derivedFrom":sQuery(id+"F6.wireOp",EDGE,"E170.MirrorC")}),-1.0]])]});
            var Q1567;
            Q1567=makeQuery(id+"F6.imprint","IMPRINT",FACE,{"disambiguationData":[TD([[makeQuery(id+"F6.imprint","IMPRINT",EDGE,{"derivedFrom":sQuery(id+"F6.wireOp",EDGE,"E43.1.0.23")}),1.0]])]});
            var Q1568;
            Q1568=makeQuery(id+"F6.imprint","IMPRINT",FACE,{"disambiguationData":[TD([[makeQuery(id+"F6.imprint","IMPRINT",EDGE,{"derivedFrom":sQuery(id+"F6.wireOp",EDGE,"E43.5.0.23")}),1.0]])]});
            var Q1569;
            Q1569=makeQuery(id+"F6.imprint","IMPRINT",FACE,{"disambiguationData":[TD([[makeQuery(id+"F6.imprint","IMPRINT",EDGE,{"derivedFrom":sQuery(id+"F6.wireOp",EDGE,"E43.3.0.23")}),1.0]])]});
            var Q1570;
            Q1570=makeQuery(id+"F6.imprint","IMPRINT",FACE,{"disambiguationData":[TD([[makeQuery(id+"F6.imprint","IMPRINT",EDGE,{"derivedFrom":sQuery(id+"F6.wireOp",EDGE,"E43.7.0.23")}),1.0]])]});
            var Q1571;
            Q1571=makeQuery(id+"F6.imprint","IMPRINT",FACE,{"disambiguationData":[TD([[makeQuery(id+"F6.imprint","IMPRINT",EDGE,{"derivedFrom":sQuery(id+"F6.wireOp",EDGE,"E43.9.0.23")}),1.0]])]});
            var Q1572;
            Q1572=makeQuery(id+"F6.imprint","IMPRINT",FACE,{"disambiguationData":[TD([[makeQuery(id+"F6.imprint","IMPRINT",EDGE,{"derivedFrom":sQuery(id+"F6.wireOp",EDGE,"E43.29.0.23")}),1.0]])]});
            var Q1573;
            Q1573=makeQuery(id+"F6.imprint","IMPRINT",FACE,{"disambiguationData":[TD([[makeQuery(id+"F6.imprint","IMPRINT",EDGE,{"derivedFrom":sQuery(id+"F6.wireOp",EDGE,"E76.MirrorC")}),-1.0]])]});
            var Q1574;
            Q1574=makeQuery(id+"F6.imprint","IMPRINT",FACE,{"disambiguationData":[TD([[makeQuery(id+"F6.imprint","IMPRINT",EDGE,{"derivedFrom":sQuery(id+"F6.wireOp",EDGE,"E43.31.0.23")}),1.0]])]});
            var Q1575;
            Q1575=makeQuery(id+"F6.imprint","IMPRINT",FACE,{"disambiguationData":[TD([[makeQuery(id+"F6.imprint","IMPRINT",EDGE,{"derivedFrom":sQuery(id+"F6.wireOp",EDGE,"E101.MirrorC")}),-1.0]])]});
            var Q1576;
            Q1576=makeQuery(id+"F6.imprint","IMPRINT",FACE,{"disambiguationData":[TD([[makeQuery(id+"F6.imprint","IMPRINT",EDGE,{"derivedFrom":sQuery(id+"F6.wireOp",EDGE,"E42.0.1.0")}),1.0]])]});
            var Q1577;
            Q1577=makeQuery(id+"F6.imprint","IMPRINT",FACE,{"disambiguationData":[TD([[makeQuery(id+"F6.imprint","IMPRINT",EDGE,{"derivedFrom":sQuery(id+"F6.wireOp",EDGE,"E38")}),1.0]])]});
            var Q1578;
            Q1578=makeQuery(id+"F6.imprint","IMPRINT",FACE,{"disambiguationData":[TD([[makeQuery(id+"F6.imprint","IMPRINT",EDGE,{"derivedFrom":sQuery(id+"F6.wireOp",EDGE,"E41.0.1.0")}),1.0]])]});
            var Q1579;
            Q1579=makeQuery(id+"F6.imprint","IMPRINT",FACE,{"disambiguationData":[TD([[makeQuery(id+"F6.imprint","IMPRINT",EDGE,{"derivedFrom":sQuery(id+"F6.wireOp",EDGE,"E43.5.0.3")}),-1.0]])]});
            var Q1580;
            Q1580=makeQuery(id+"F6.imprint","IMPRINT",FACE,{"disambiguationData":[TD([[makeQuery(id+"F6.imprint","IMPRINT",EDGE,{"derivedFrom":sQuery(id+"F6.wireOp",EDGE,"E43.20.0.3")}),-1.0]])]});
            var Q1581;
            Q1581=makeQuery(id+"F6.imprint","IMPRINT",FACE,{"disambiguationData":[TD([[makeQuery(id+"F6.imprint","IMPRINT",EDGE,{"derivedFrom":sQuery(id+"F6.wireOp",EDGE,"E43.4.0.3")}),-1.0]])]});
            var Q1582;
            Q1582=makeQuery(id+"F6.imprint","IMPRINT",FACE,{"disambiguationData":[TD([[makeQuery(id+"F6.imprint","IMPRINT",EDGE,{"derivedFrom":sQuery(id+"F6.wireOp",EDGE,"E43.13.0.3")}),-1.0]])]});
            var Q1583;
            Q1583=makeQuery(id+"F6.imprint","IMPRINT",FACE,{"disambiguationData":[TD([[makeQuery(id+"F6.imprint","IMPRINT",EDGE,{"derivedFrom":sQuery(id+"F6.wireOp",EDGE,"E43.18.0.3")}),-1.0]])]});
            var Q1584;
            Q1584=makeQuery(id+"F6.imprint","IMPRINT",FACE,{"disambiguationData":[TD([[makeQuery(id+"F6.imprint","IMPRINT",EDGE,{"derivedFrom":sQuery(id+"F6.wireOp",EDGE,"E43.31.0.3")}),-1.0]])]});
            var Q1585;
            Q1585=makeQuery(id+"F6.imprint","IMPRINT",FACE,{"disambiguationData":[TD([[makeQuery(id+"F6.imprint","IMPRINT",EDGE,{"derivedFrom":sQuery(id+"F6.wireOp",EDGE,"E43.27.0.3")}),-1.0]])]});
            var Q1586;
            Q1586=makeQuery(id+"F6.imprint","IMPRINT",FACE,{"disambiguationData":[TD([[makeQuery(id+"F6.imprint","IMPRINT",EDGE,{"derivedFrom":sQuery(id+"F6.wireOp",EDGE,"E43.28.0.3")}),-1.0]])]});
            var Q1587;
            Q1587=makeQuery(id+"F6.imprint","IMPRINT",FACE,{"disambiguationData":[TD([[makeQuery(id+"F6.imprint","IMPRINT",EDGE,{"derivedFrom":sQuery(id+"F6.wireOp",EDGE,"E43.3.0.3")}),-1.0]])]});
            var Q1588;
            Q1588=makeQuery(id+"F6.imprint","IMPRINT",FACE,{"disambiguationData":[TD([[makeQuery(id+"F6.imprint","IMPRINT",EDGE,{"derivedFrom":sQuery(id+"F6.wireOp",EDGE,"E43.26.0.3")}),-1.0]])]});
            var Q1589;
            Q1589=makeQuery(id+"F6.imprint","IMPRINT",FACE,{"disambiguationData":[TD([[makeQuery(id+"F6.imprint","IMPRINT",EDGE,{"derivedFrom":sQuery(id+"F6.wireOp",EDGE,"E43.23.0.3")}),-1.0]])]});
            var Q1590;
            Q1590=makeQuery(id+"F6.imprint","IMPRINT",FACE,{"disambiguationData":[TD([[makeQuery(id+"F6.imprint","IMPRINT",EDGE,{"derivedFrom":sQuery(id+"F6.wireOp",EDGE,"E43.10.0.3")}),-1.0]])]});
            var Q1591;
            Q1591=makeQuery(id+"F6.imprint","IMPRINT",FACE,{"disambiguationData":[TD([[makeQuery(id+"F6.imprint","IMPRINT",EDGE,{"derivedFrom":sQuery(id+"F6.wireOp",EDGE,"E43.30.0.3")}),-1.0]])]});
            var Q1592;
            Q1592=makeQuery(id+"F6.imprint","IMPRINT",FACE,{"disambiguationData":[TD([[makeQuery(id+"F6.imprint","IMPRINT",EDGE,{"derivedFrom":sQuery(id+"F6.wireOp",EDGE,"E43.1.0.3")}),-1.0]])]});
            var Q1593;
            Q1593=makeQuery(id+"F6.imprint","IMPRINT",FACE,{"disambiguationData":[TD([[makeQuery(id+"F6.imprint","IMPRINT",EDGE,{"derivedFrom":sQuery(id+"F6.wireOp",EDGE,"E43.22.0.3")}),-1.0]])]});
            var Q1594;
            Q1594=makeQuery(id+"F6.imprint","IMPRINT",FACE,{"disambiguationData":[TD([[makeQuery(id+"F6.imprint","IMPRINT",EDGE,{"derivedFrom":sQuery(id+"F6.wireOp",EDGE,"E43.32.0.3")}),-1.0]])]});
            var Q1595;
            Q1595=makeQuery(id+"F6.imprint","IMPRINT",FACE,{"disambiguationData":[TD([[makeQuery(id+"F6.imprint","IMPRINT",EDGE,{"derivedFrom":sQuery(id+"F6.wireOp",EDGE,"E43.16.0.3")}),-1.0]])]});
            var Q1596;
            Q1596=makeQuery(id+"F6.imprint","IMPRINT",FACE,{"disambiguationData":[TD([[makeQuery(id+"F6.imprint","IMPRINT",EDGE,{"derivedFrom":sQuery(id+"F6.wireOp",EDGE,"E43.12.0.3")}),-1.0]])]});
            var Q1597;
            Q1597=makeQuery(id+"F6.imprint","IMPRINT",FACE,{"disambiguationData":[TD([[makeQuery(id+"F6.imprint","IMPRINT",EDGE,{"derivedFrom":sQuery(id+"F6.wireOp",EDGE,"E43.15.0.3")}),-1.0]])]});
            var Q1598;
            Q1598=makeQuery(id+"F6.imprint","IMPRINT",FACE,{"disambiguationData":[TD([[makeQuery(id+"F6.imprint","IMPRINT",EDGE,{"derivedFrom":sQuery(id+"F6.wireOp",EDGE,"E43.21.0.3")}),-1.0]])]});
            var Q1599;
            Q1599=makeQuery(id+"F6.imprint","IMPRINT",FACE,{"disambiguationData":[TD([[makeQuery(id+"F6.imprint","IMPRINT",EDGE,{"derivedFrom":sQuery(id+"F6.wireOp",EDGE,"E43.17.0.3")}),-1.0]])]});
            var Q1600;
            Q1600=makeQuery(id+"F6.imprint","IMPRINT",FACE,{"disambiguationData":[TD([[makeQuery(id+"F6.imprint","IMPRINT",EDGE,{"derivedFrom":sQuery(id+"F6.wireOp",EDGE,"E43.29.0.3")}),-1.0]])]});
            var Q1601;
            Q1601=makeQuery(id+"F6.imprint","IMPRINT",FACE,{"disambiguationData":[TD([[makeQuery(id+"F6.imprint","IMPRINT",EDGE,{"derivedFrom":sQuery(id+"F6.wireOp",EDGE,"E43.24.0.3")}),-1.0]])]});
            var Q1602;
            Q1602=makeQuery(id+"F6.imprint","IMPRINT",FACE,{"disambiguationData":[TD([[makeQuery(id+"F6.imprint","IMPRINT",EDGE,{"derivedFrom":sQuery(id+"F6.wireOp",EDGE,"E43.14.0.3")}),-1.0]])]});
            var Q1603;
            Q1603=makeQuery(id+"F6.imprint","IMPRINT",FACE,{"disambiguationData":[TD([[makeQuery(id+"F6.imprint","IMPRINT",EDGE,{"derivedFrom":sQuery(id+"F6.wireOp",EDGE,"E43.1.0.25")}),1.0]])]});
            var Q1604;
            Q1604=makeQuery(id+"F6.imprint","IMPRINT",FACE,{"disambiguationData":[TD([[makeQuery(id+"F6.imprint","IMPRINT",EDGE,{"derivedFrom":sQuery(id+"F6.wireOp",EDGE,"E43.6.0.3")}),-1.0]])]});
            var Q1605;
            Q1605=makeQuery(id+"F6.imprint","IMPRINT",FACE,{"disambiguationData":[TD([[makeQuery(id+"F6.imprint","IMPRINT",EDGE,{"derivedFrom":sQuery(id+"F6.wireOp",EDGE,"E43.8.0.3")}),-1.0]])]});
            var Q1606;
            Q1606=makeQuery(id+"F6.imprint","IMPRINT",FACE,{"disambiguationData":[TD([[makeQuery(id+"F6.imprint","IMPRINT",EDGE,{"derivedFrom":sQuery(id+"F6.wireOp",EDGE,"E43.19.0.3")}),-1.0]])]});
            var Q1607;
            Q1607=makeQuery(id+"F6.imprint","IMPRINT",FACE,{"disambiguationData":[TD([[makeQuery(id+"F6.imprint","IMPRINT",EDGE,{"derivedFrom":sQuery(id+"F6.wireOp",EDGE,"E43.9.0.3")}),-1.0]])]});
            var Q1608;
            Q1608=makeQuery(id+"F6.imprint","IMPRINT",FACE,{"disambiguationData":[TD([[makeQuery(id+"F6.imprint","IMPRINT",EDGE,{"derivedFrom":sQuery(id+"F6.wireOp",EDGE,"E43.7.0.3")}),-1.0]])]});
            var Q1609;
            Q1609=makeQuery(id+"F6.imprint","IMPRINT",FACE,{"disambiguationData":[TD([[makeQuery(id+"F6.imprint","IMPRINT",EDGE,{"derivedFrom":sQuery(id+"F6.wireOp",EDGE,"E41.0.12.0")}),-1.0]])]});
            var Q1610;
            Q1610=makeQuery(id+"F6.imprint","IMPRINT",FACE,{"disambiguationData":[TD([[makeQuery(id+"F6.imprint","IMPRINT",EDGE,{"derivedFrom":sQuery(id+"F6.wireOp",EDGE,"E43.25.0.3")}),-1.0]])]});
            var Q1611;
            Q1611=makeQuery(id+"F6.imprint","IMPRINT",FACE,{"disambiguationData":[TD([[makeQuery(id+"F6.imprint","IMPRINT",EDGE,{"derivedFrom":sQuery(id+"F6.wireOp",EDGE,"E43.2.0.3")}),-1.0]])]});
            var Q1612;
            Q1612=makeQuery(id+"F6.imprint","IMPRINT",FACE,{"disambiguationData":[TD([[makeQuery(id+"F6.imprint","IMPRINT",EDGE,{"derivedFrom":sQuery(id+"F6.wireOp",EDGE,"E43.32.0.25")}),1.0]])]});
            var Q1613;
            Q1613=makeQuery(id+"F6.imprint","IMPRINT",FACE,{"disambiguationData":[TD([[makeQuery(id+"F6.imprint","IMPRINT",EDGE,{"derivedFrom":sQuery(id+"F6.wireOp",EDGE,"E46.MirrorC")}),-1.0]])]});
            var Q1614;
            Q1614=makeQuery(id+"F6.imprint","IMPRINT",FACE,{"disambiguationData":[TD([[makeQuery(id+"F6.imprint","IMPRINT",EDGE,{"derivedFrom":sQuery(id+"F6.wireOp",EDGE,"E43.11.0.3")}),-1.0]])]});
            var Q1615;
            Q1615=makeQuery(id+"F6.imprint","IMPRINT",FACE,{"disambiguationData":[TD([[makeQuery(id+"F6.imprint","IMPRINT",EDGE,{"derivedFrom":sQuery(id+"F6.wireOp",EDGE,"E52.MirrorC")}),-1.0]])]});
            var Q1616;
            Q1616=makeQuery(id+"F6.imprint","IMPRINT",FACE,{"disambiguationData":[TD([[makeQuery(id+"F6.imprint","IMPRINT",EDGE,{"derivedFrom":sQuery(id+"F6.wireOp",EDGE,"E39")}),1.0]])]});
            extrude(context, id + "F7", {"entities" : qUnion([Q0, Q1, Q2, Q3, Q4, Q5, Q6, Q7, Q8, Q9, Q10, Q11, Q12, Q13, Q14, Q15, Q16, Q17, Q18, Q19, Q20, Q21, Q22, Q23, Q24, Q25, Q26, Q27, Q28, Q29, Q30, Q31, Q32, Q33, Q34, Q35, Q36, Q37, Q38, Q39, Q40, Q41, Q42, Q43, Q44, Q45, Q46, Q47, Q48, Q49, Q50, Q51, Q52, Q53, Q54, Q55, Q56, Q57, Q58, Q59, Q60, Q61, Q62, Q63, Q64, Q65, Q66, Q67, Q68, Q69, Q70, Q71, Q72, Q73, Q74, Q75, Q76, Q77, Q78, Q79, Q80, Q81, Q82, Q83, Q84, Q85, Q86, Q87, Q88, Q89, Q90, Q91, Q92, Q93, Q94, Q95, Q96, Q97, Q98, Q99, Q100, Q101, Q102, Q103, Q104, Q105, Q106, Q107, Q108, Q109, Q110, Q111, Q112, Q113, Q114, Q115, Q116, Q117, Q118, Q119, Q120, Q121, Q122, Q123, Q124, Q125, Q126, Q127, Q128, Q129, Q130, Q131, Q132, Q133, Q134, Q135, Q136, Q137, Q138, Q139, Q140, Q141, Q142, Q143, Q144, Q145, Q146, Q147, Q148, Q149, Q150, Q151, Q152, Q153, Q154, Q155, Q156, Q157, Q158, Q159, Q160, Q161, Q162, Q163, Q164, Q165, Q166, Q167, Q168, Q169, Q170, Q171, Q172, Q173, Q174, Q175, Q176, Q177, Q178, Q179, Q180, Q181, Q182, Q183, Q184, Q185, Q186, Q187, Q188, Q189, Q190, Q191, Q192, Q193, Q194, Q195, Q196, Q197, Q198, Q199, Q200, Q201, Q202, Q203, Q204, Q205, Q206, Q207, Q208, Q209, Q210, Q211, Q212, Q213, Q214, Q215, Q216, Q217, Q218, Q219, Q220, Q221, Q222, Q223, Q224, Q225, Q226, Q227, Q228, Q229, Q230, Q231, Q232, Q233, Q234, Q235, Q236, Q237, Q238, Q239, Q240, Q241, Q242, Q243, Q244, Q245, Q246, Q247, Q248, Q249, Q250, Q251, Q252, Q253, Q254, Q255, Q256, Q257, Q258, Q259, Q260, Q261, Q262, Q263, Q264, Q265, Q266, Q267, Q268, Q269, Q270, Q271, Q272, Q273, Q274, Q275, Q276, Q277, Q278, Q279, Q280, Q281, Q282, Q283, Q284, Q285, Q286, Q287, Q288, Q289, Q290, Q291, Q292, Q293, Q294, Q295, Q296, Q297, Q298, Q299, Q300, Q301, Q302, Q303, Q304, Q305, Q306, Q307, Q308, Q309, Q310, Q311, Q312, Q313, Q314, Q315, Q316, Q317, Q318, Q319, Q320, Q321, Q322, Q323, Q324, Q325, Q326, Q327, Q328, Q329, Q330, Q331, Q332, Q333, Q334, Q335, Q336, Q337, Q338, Q339, Q340, Q341, Q342, Q343, Q344, Q345, Q346, Q347, Q348, Q349, Q350, Q351, Q352, Q353, Q354, Q355, Q356, Q357, Q358, Q359, Q360, Q361, Q362, Q363, Q364, Q365, Q366, Q367, Q368, Q369, Q370, Q371, Q372, Q373, Q374, Q375, Q376, Q377, Q378, Q379, Q380, Q381, Q382, Q383, Q384, Q385, Q386, Q387, Q388, Q389, Q390, Q391, Q392, Q393, Q394, Q395, Q396, Q397, Q398, Q399, Q400, Q401, Q402, Q403, Q404, Q405, Q406, Q407, Q408, Q409, Q410, Q411, Q412, Q413, Q414, Q415, Q416, Q417, Q418, Q419, Q420, Q421, Q422, Q423, Q424, Q425, Q426, Q427, Q428, Q429, Q430, Q431, Q432, Q433, Q434, Q435, Q436, Q437, Q438, Q439, Q440, Q441, Q442, Q443, Q444, Q445, Q446, Q447, Q448, Q449, Q450, Q451, Q452, Q453, Q454, Q455, Q456, Q457, Q458, Q459, Q460, Q461, Q462, Q463, Q464, Q465, Q466, Q467, Q468, Q469, Q470, Q471, Q472, Q473, Q474, Q475, Q476, Q477, Q478, Q479, Q480, Q481, Q482, Q483, Q484, Q485, Q486, Q487, Q488, Q489, Q490, Q491, Q492, Q493, Q494, Q495, Q496, Q497, Q498, Q499, Q500, Q501, Q502, Q503, Q504, Q505, Q506, Q507, Q508, Q509, Q510, Q511, Q512, Q513, Q514, Q515, Q516, Q517, Q518, Q519, Q520, Q521, Q522, Q523, Q524, Q525, Q526, Q527, Q528, Q529, Q530, Q531, Q532, Q533, Q534, Q535, Q536, Q537, Q538, Q539, Q540, Q541, Q542, Q543, Q544, Q545, Q546, Q547, Q548, Q549, Q550, Q551, Q552, Q553, Q554, Q555, Q556, Q557, Q558, Q559, Q560, Q561, Q562, Q563, Q564, Q565, Q566, Q567, Q568, Q569, Q570, Q571, Q572, Q573, Q574, Q575, Q576, Q577, Q578, Q579, Q580, Q581, Q582, Q583, Q584, Q585, Q586, Q587, Q588, Q589, Q590, Q591, Q592, Q593, Q594, Q595, Q596, Q597, Q598, Q599, Q600, Q601, Q602, Q603, Q604, Q605, Q606, Q607, Q608, Q609, Q610, Q611, Q612, Q613, Q614, Q615, Q616, Q617, Q618, Q619, Q620, Q621, Q622, Q623, Q624, Q625, Q626, Q627, Q628, Q629, Q630, Q631, Q632, Q633, Q634, Q635, Q636, Q637, Q638, Q639, Q640, Q641, Q642, Q643, Q644, Q645, Q646, Q647, Q648, Q649, Q650, Q651, Q652, Q653, Q654, Q655, Q656, Q657, Q658, Q659, Q660, Q661, Q662, Q663, Q664, Q665, Q666, Q667, Q668, Q669, Q670, Q671, Q672, Q673, Q674, Q675, Q676, Q677, Q678, Q679, Q680, Q681, Q682, Q683, Q684, Q685, Q686, Q687, Q688, Q689, Q690, Q691, Q692, Q693, Q694, Q695, Q696, Q697, Q698, Q699, Q700, Q701, Q702, Q703, Q704, Q705, Q706, Q707, Q708, Q709, Q710, Q711, Q712, Q713, Q714, Q715, Q716, Q717, Q718, Q719, Q720, Q721, Q722, Q723, Q724, Q725, Q726, Q727, Q728, Q729, Q730, Q731, Q732, Q733, Q734, Q735, Q736, Q737, Q738, Q739, Q740, Q741, Q742, Q743, Q744, Q745, Q746, Q747, Q748, Q749, Q750, Q751, Q752, Q753, Q754, Q755, Q756, Q757, Q758, Q759, Q760, Q761, Q762, Q763, Q764, Q765, Q766, Q767, Q768, Q769, Q770, Q771, Q772, Q773, Q774, Q775, Q776, Q777, Q778, Q779, Q780, Q781, Q782, Q783, Q784, Q785, Q786, Q787, Q788, Q789, Q790, Q791, Q792, Q793, Q794, Q795, Q796, Q797, Q798, Q799, Q800, Q801, Q802, Q803, Q804, Q805, Q806, Q807, Q808, Q809, Q810, Q811, Q812, Q813, Q814, Q815, Q816, Q817, Q818, Q819, Q820, Q821, Q822, Q823, Q824, Q825, Q826, Q827, Q828, Q829, Q830, Q831, Q832, Q833, Q834, Q835, Q836, Q837, Q838, Q839, Q840, Q841, Q842, Q843, Q844, Q845, Q846, Q847, Q848, Q849, Q850, Q851, Q852, Q853, Q854, Q855, Q856, Q857, Q858, Q859, Q860, Q861, Q862, Q863, Q864, Q865, Q866, Q867, Q868, Q869, Q870, Q871, Q872, Q873, Q874, Q875, Q876, Q877, Q878, Q879, Q880, Q881, Q882, Q883, Q884, Q885, Q886, Q887, Q888, Q889, Q890, Q891, Q892, Q893, Q894, Q895, Q896, Q897, Q898, Q899, Q900, Q901, Q902, Q903, Q904, Q905, Q906, Q907, Q908, Q909, Q910, Q911, Q912, Q913, Q914, Q915, Q916, Q917, Q918, Q919, Q920, Q921, Q922, Q923, Q924, Q925, Q926, Q927, Q928, Q929, Q930, Q931, Q932, Q933, Q934, Q935, Q936, Q937, Q938, Q939, Q940, Q941, Q942, Q943, Q944, Q945, Q946, Q947, Q948, Q949, Q950, Q951, Q952, Q953, Q954, Q955, Q956, Q957, Q958, Q959, Q960, Q961, Q962, Q963, Q964, Q965, Q966, Q967, Q968, Q969, Q970, Q971, Q972, Q973, Q974, Q975, Q976, Q977, Q978, Q979, Q980, Q981, Q982, Q983, Q984, Q985, Q986, Q987, Q988, Q989, Q990, Q991, Q992, Q993, Q994, Q995, Q996, Q997, Q998, Q999, Q1000, Q1001, Q1002, Q1003, Q1004, Q1005, Q1006, Q1007, Q1008, Q1009, Q1010, Q1011, Q1012, Q1013, Q1014, Q1015, Q1016, Q1017, Q1018, Q1019, Q1020, Q1021, Q1022, Q1023, Q1024, Q1025, Q1026, Q1027, Q1028, Q1029, Q1030, Q1031, Q1032, Q1033, Q1034, Q1035, Q1036, Q1037, Q1038, Q1039, Q1040, Q1041, Q1042, Q1043, Q1044, Q1045, Q1046, Q1047, Q1048, Q1049, Q1050, Q1051, Q1052, Q1053, Q1054, Q1055, Q1056, Q1057, Q1058, Q1059, Q1060, Q1061, Q1062, Q1063, Q1064, Q1065, Q1066, Q1067, Q1068, Q1069, Q1070, Q1071, Q1072, Q1073, Q1074, Q1075, Q1076, Q1077, Q1078, Q1079, Q1080, Q1081, Q1082, Q1083, Q1084, Q1085, Q1086, Q1087, Q1088, Q1089, Q1090, Q1091, Q1092, Q1093, Q1094, Q1095, Q1096, Q1097, Q1098, Q1099, Q1100, Q1101, Q1102, Q1103, Q1104, Q1105, Q1106, Q1107, Q1108, Q1109, Q1110, Q1111, Q1112, Q1113, Q1114, Q1115, Q1116, Q1117, Q1118, Q1119, Q1120, Q1121, Q1122, Q1123, Q1124, Q1125, Q1126, Q1127, Q1128, Q1129, Q1130, Q1131, Q1132, Q1133, Q1134, Q1135, Q1136, Q1137, Q1138, Q1139, Q1140, Q1141, Q1142, Q1143, Q1144, Q1145, Q1146, Q1147, Q1148, Q1149, Q1150, Q1151, Q1152, Q1153, Q1154, Q1155, Q1156, Q1157, Q1158, Q1159, Q1160, Q1161, Q1162, Q1163, Q1164, Q1165, Q1166, Q1167, Q1168, Q1169, Q1170, Q1171, Q1172, Q1173, Q1174, Q1175, Q1176, Q1177, Q1178, Q1179, Q1180, Q1181, Q1182, Q1183, Q1184, Q1185, Q1186, Q1187, Q1188, Q1189, Q1190, Q1191, Q1192, Q1193, Q1194, Q1195, Q1196, Q1197, Q1198, Q1199, Q1200, Q1201, Q1202, Q1203, Q1204, Q1205, Q1206, Q1207, Q1208, Q1209, Q1210, Q1211, Q1212, Q1213, Q1214, Q1215, Q1216, Q1217, Q1218, Q1219, Q1220, Q1221, Q1222, Q1223, Q1224, Q1225, Q1226, Q1227, Q1228, Q1229, Q1230, Q1231, Q1232, Q1233, Q1234, Q1235, Q1236, Q1237, Q1238, Q1239, Q1240, Q1241, Q1242, Q1243, Q1244, Q1245, Q1246, Q1247, Q1248, Q1249, Q1250, Q1251, Q1252, Q1253, Q1254, Q1255, Q1256, Q1257, Q1258, Q1259, Q1260, Q1261, Q1262, Q1263, Q1264, Q1265, Q1266, Q1267, Q1268, Q1269, Q1270, Q1271, Q1272, Q1273, Q1274, Q1275, Q1276, Q1277, Q1278, Q1279, Q1280, Q1281, Q1282, Q1283, Q1284, Q1285, Q1286, Q1287, Q1288, Q1289, Q1290, Q1291, Q1292, Q1293, Q1294, Q1295, Q1296, Q1297, Q1298, Q1299, Q1300, Q1301, Q1302, Q1303, Q1304, Q1305, Q1306, Q1307, Q1308, Q1309, Q1310, Q1311, Q1312, Q1313, Q1314, Q1315, Q1316, Q1317, Q1318, Q1319, Q1320, Q1321, Q1322, Q1323, Q1324, Q1325, Q1326, Q1327, Q1328, Q1329, Q1330, Q1331, Q1332, Q1333, Q1334, Q1335, Q1336, Q1337, Q1338, Q1339, Q1340, Q1341, Q1342, Q1343, Q1344, Q1345, Q1346, Q1347, Q1348, Q1349, Q1350, Q1351, Q1352, Q1353, Q1354, Q1355, Q1356, Q1357, Q1358, Q1359, Q1360, Q1361, Q1362, Q1363, Q1364, Q1365, Q1366, Q1367, Q1368, Q1369, Q1370, Q1371, Q1372, Q1373, Q1374, Q1375, Q1376, Q1377, Q1378, Q1379, Q1380, Q1381, Q1382, Q1383, Q1384, Q1385, Q1386, Q1387, Q1388, Q1389, Q1390, Q1391, Q1392, Q1393, Q1394, Q1395, Q1396, Q1397, Q1398, Q1399, Q1400, Q1401, Q1402, Q1403, Q1404, Q1405, Q1406, Q1407, Q1408, Q1409, Q1410, Q1411, Q1412, Q1413, Q1414, Q1415, Q1416, Q1417, Q1418, Q1419, Q1420, Q1421, Q1422, Q1423, Q1424, Q1425, Q1426, Q1427, Q1428, Q1429, Q1430, Q1431, Q1432, Q1433, Q1434, Q1435, Q1436, Q1437, Q1438, Q1439, Q1440, Q1441, Q1442, Q1443, Q1444, Q1445, Q1446, Q1447, Q1448, Q1449, Q1450, Q1451, Q1452, Q1453, Q1454, Q1455, Q1456, Q1457, Q1458, Q1459, Q1460, Q1461, Q1462, Q1463, Q1464, Q1465, Q1466, Q1467, Q1468, Q1469, Q1470, Q1471, Q1472, Q1473, Q1474, Q1475, Q1476, Q1477, Q1478, Q1479, Q1480, Q1481, Q1482, Q1483, Q1484, Q1485, Q1486, Q1487, Q1488, Q1489, Q1490, Q1491, Q1492, Q1493, Q1494, Q1495, Q1496, Q1497, Q1498, Q1499, Q1500, Q1501, Q1502, Q1503, Q1504, Q1505, Q1506, Q1507, Q1508, Q1509, Q1510, Q1511, Q1512, Q1513, Q1514, Q1515, Q1516, Q1517, Q1518, Q1519, Q1520, Q1521, Q1522, Q1523, Q1524, Q1525, Q1526, Q1527, Q1528, Q1529, Q1530, Q1531, Q1532, Q1533, Q1534, Q1535, Q1536, Q1537, Q1538, Q1539, Q1540, Q1541, Q1542, Q1543, Q1544, Q1545, Q1546, Q1547, Q1548, Q1549, Q1550, Q1551, Q1552, Q1553, Q1554, Q1555, Q1556, Q1557, Q1558, Q1559, Q1560, Q1561, Q1562, Q1563, Q1564, Q1565, Q1566, Q1567, Q1568, Q1569, Q1570, Q1571, Q1572, Q1573, Q1574, Q1575, Q1576, Q1577, Q1578, Q1579, Q1580, Q1581, Q1582, Q1583, Q1584, Q1585, Q1586, Q1587, Q1588, Q1589, Q1590, Q1591, Q1592, Q1593, Q1594, Q1595, Q1596, Q1597, Q1598, Q1599, Q1600, Q1601, Q1602, Q1603, Q1604, Q1605, Q1606, Q1607, Q1608, Q1609, Q1610, Q1611, Q1612, Q1613, Q1614, Q1615, Q1616]), "operationType" : NewBodyOperationType.REMOVE, "oppositeDirection" : true, "depth" : 25 * mm});
        }
        {
            var Q0;
            Q0=makeQuery(id+"F3.boolean.opBoolean","INTERSECT",EDGE,{"derivedFrom":[makeQuery(id+"F1.opExtrude","SWEPT_FACE",FACE,{"disambiguationData":[OSD([sQuery(id+"F0.wireOp",EDGE,"E0")])]}),makeQuery(id+"F3.opExtrude","CAP_FACE",FACE,{"disambiguationData":[OSD([sQuery(id+"F2.wireOp",EDGE,"E8"),sQuery(id+"F2.wireOp",EDGE,"E9"),sQuery(id+"F2.wireOp",EDGE,"E10"),sQuery(id+"F2.wireOp",EDGE,"E11"),sQuery(id+"F2.wireOp",EDGE,"E19"),sQuery(id+"F2.wireOp",EDGE,"E20.1.0.0"),sQuery(id+"F2.wireOp",EDGE,"E20.2.0.0"),sQuery(id+"F2.wireOp",EDGE,"E20.3.0.0"),sQuery(id+"F2.wireOp",EDGE,"E20.4.0.0"),sQuery(id+"F2.wireOp",EDGE,"E20.5.0.0"),sQuery(id+"F2.wireOp",EDGE,"E20.6.0.0"),sQuery(id+"F2.wireOp",EDGE,"E20.7.0.0"),sQuery(id+"F2.wireOp",EDGE,"E20.8.0.0"),sQuery(id+"F2.wireOp",EDGE,"E20.9.0.0"),sQuery(id+"F2.wireOp",EDGE,"E20.10.0.0"),sQuery(id+"F2.wireOp",EDGE,"E20.11.0.0"),sQuery(id+"F2.wireOp",EDGE,"E20.12.0.0"),sQuery(id+"F2.wireOp",EDGE,"E20.13.0.0"),sQuery(id+"F2.wireOp",EDGE,"E20.14.0.0")])],"isStart":false})]});
            var Q1;
            Q1=makeQuery(id+"F5.boolean.opBoolean","INTERSECT",EDGE,{"derivedFrom":[makeQuery(id+"F1.opExtrude","SWEPT_FACE",FACE,{"disambiguationData":[OSD([sQuery(id+"F0.wireOp",EDGE,"E0")])]}),makeQuery(id+"F5.opExtrude","CAP_FACE",FACE,{"disambiguationData":[OSD([sQuery(id+"F4.wireOp",EDGE,"E23"),sQuery(id+"F4.wireOp",EDGE,"E24"),sQuery(id+"F4.wireOp",EDGE,"E25"),sQuery(id+"F4.wireOp",EDGE,"E26"),sQuery(id+"F4.wireOp",EDGE,"E34"),sQuery(id+"F4.wireOp",EDGE,"E35.1.0.0"),sQuery(id+"F4.wireOp",EDGE,"E35.2.0.0"),sQuery(id+"F4.wireOp",EDGE,"E35.3.0.0"),sQuery(id+"F4.wireOp",EDGE,"E35.4.0.0"),sQuery(id+"F4.wireOp",EDGE,"E35.5.0.0"),sQuery(id+"F4.wireOp",EDGE,"E35.6.0.0"),sQuery(id+"F4.wireOp",EDGE,"E35.7.0.0"),sQuery(id+"F4.wireOp",EDGE,"E35.8.0.0"),sQuery(id+"F4.wireOp",EDGE,"E35.9.0.0"),sQuery(id+"F4.wireOp",EDGE,"E35.10.0.0"),sQuery(id+"F4.wireOp",EDGE,"E35.11.0.0"),sQuery(id+"F4.wireOp",EDGE,"E35.12.0.0"),sQuery(id+"F4.wireOp",EDGE,"E35.13.0.0"),sQuery(id+"F4.wireOp",EDGE,"E35.14.0.0")])],"isStart":false})]});
            fillet(context, id + "F8", {"entities" : qUnion([Q0, Q1]), "radius" : 2 * mm, "tangentPropagation" : true, "allowEdgeOverflow" : false});
        }
        {
            var Q0;
            Q0=makeQuery(id+"F1.opExtrude","CAP_EDGE",EDGE,{"disambiguationData":[OSD([sQuery(id+"F0.wireOp",EDGE,"E3"),sQuery(id+"F0.wireOp",EDGE,"E5")])],"isStart":true});
            var Q1;
            Q1=makeQuery(id+"F1.opExtrude","CAP_EDGE",EDGE,{"disambiguationData":[OSD([sQuery(id+"F0.wireOp",EDGE,"E3"),sQuery(id+"F0.wireOp",EDGE,"E5")])],"isStart":false});
            fillet(context, id + "F9", {"entities" : qUnion([Q0, Q1]), "radius" : 4 * mm, "tangentPropagation" : true, "allowEdgeOverflow" : false});
        }
    });
